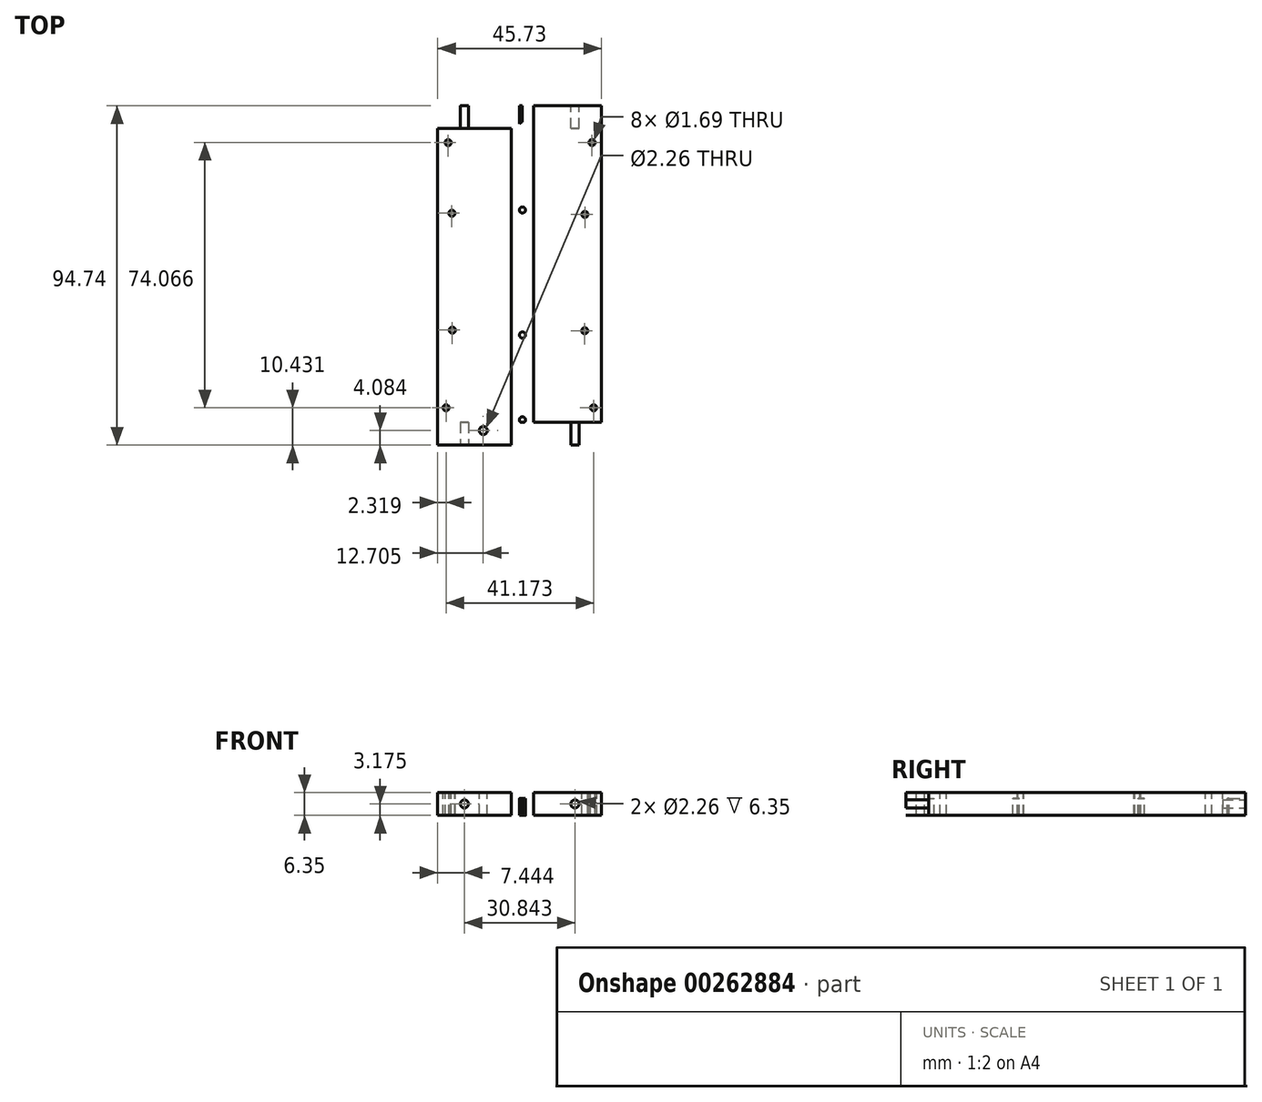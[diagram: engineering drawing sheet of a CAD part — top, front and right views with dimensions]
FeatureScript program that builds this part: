
annotation { "Feature Type Name" : "Feature", "Feature Type Description" : "" }
export const myFeature = defineFeature(function(context is Context, id is Id, definition is map)
    precondition{}
    {
        {
            var Q0;
            Q0=qCreatedBy(makeId("Top.planeOp"),FACE);
            var sketch = newSketch(context, id + "F0", { "sketchPlane" : qUnion([Q0])});
            skLineSegment(sketch, "E0.bottom", {"start": v(0, 0) * mm, "end": v(52.07, 0) * mm});
            skLineSegment(sketch, "E0.top", {"start": v(0, 101.6) * mm, "end": v(52.07, 101.6) * mm});
            skLineSegment(sketch, "E0.left", {"start": v(0, 0) * mm, "end": v(0, 101.6) * mm});
            skLineSegment(sketch, "E0.right", {"start": v(52.07, 0) * mm, "end": v(52.07, 101.6) * mm});
            skLineSegment(sketch, "E1.bottom", {"start": v(3.17, 3.43) * mm, "end": v(48.9, 3.43) * mm});
            skLineSegment(sketch, "E1.top", {"start": v(3.17, 98.17) * mm, "end": v(48.9, 98.17) * mm});
            skLineSegment(sketch, "E1.left", {"start": v(3.17, 3.43) * mm, "end": v(3.17, 98.17) * mm});
            skLineSegment(sketch, "E1.right", {"start": v(48.9, 3.43) * mm, "end": v(48.9, 98.17) * mm});
            skSolve(sketch);
        }
        {
            var Q0;
            {var subQ0=sQuery(id+"F0.wireOp",EDGE,"E1.left");Q0=makeQuery(id+"F0.imprint","IMPRINT",FACE,{"disambiguationData":[TD([[makeQuery(id+"F0.imprint","IMPRINT",EDGE,{"derivedFrom":subQ0}),-1.0]])]});}
            var Q1;
            {var subQ0=sQuery(id+"F0.wireOp",EDGE,"E1.right");Q1=makeQuery(id+"F0.imprint","IMPRINT",FACE,{"disambiguationData":[TD([[makeQuery(id+"F0.imprint","IMPRINT",EDGE,{"derivedFrom":subQ0}),1.0]])]});}
            var Q2;
            {var subQ0=sQuery(id+"F0.wireOp",EDGE,"10e28cab-1427-4d4f-a1a2-41381d8ae787");Q2=makeQuery(id+"F0.imprint","IMPRINT",FACE,{"disambiguationData":[TD([[makeQuery(id+"F0.imprint","IMPRINT",EDGE,{"derivedFrom":subQ0}),1.0]])]});}
            var Q3;
            {var subQ0=sQuery(id+"F0.wireOp",EDGE,"10e28cab-1427-4d4f-a1a2-41381d8ae787");Q3=makeQuery(id+"F0.imprint","IMPRINT",FACE,{"disambiguationData":[TD([[makeQuery(id+"F0.imprint","IMPRINT",EDGE,{"derivedFrom":subQ0}),-1.0]])]});}
            extrude(context, id + "F1", {"entities" : qUnion([Q0, Q1, Q2, Q3]), "oppositeDirection" : true, "depth" : 6.35 * mm});
        }
        {
            var Q0;
            Q0=qCreatedBy(makeId("Top.planeOp"),FACE);
            var Q1;
            Q1=qCreatedBy(makeId("Front.planeOp"),FACE);
            var Q2;
            Q2=qCreatedBy(makeId("Top.planeOp"),FACE);
            var Q3;
            Q3=qCreatedBy(makeId("Top.planeOp"),FACE);
            var sketch = newSketch(context, id + "F2", { "sketchPlane" : qUnion([Q0, Q1, Q2, Q3])});
            skLineSegment(sketch, "E2", {"start": v(3.17, 11.6) * mm, "end": v(3.17, 90.4) * mm});
            skLineSegment(sketch, "E3", {"start": v(3.17, 90.65) * mm, "end": v(48.9, 90.65) * mm});
            skLineSegment(sketch, "E4", {"start": v(48.9, 90.65) * mm, "end": v(48.9, 11.85) * mm});
            skLineSegment(sketch, "E5", {"start": v(48.9, 11.85) * mm, "end": v(3.17, 11.85) * mm});
            skLineSegment(sketch, "E6", {"start": v(25.2, 45.84) * mm, "end": v(25.2, 56.82) * mm});
            skLineSegment(sketch, "E7", {"start": v(25.2, 56.82) * mm, "end": v(28.45, 56.82) * mm});
            skLineSegment(sketch, "E8", {"start": v(28.45, 56.82) * mm, "end": v(28.45, 45.84) * mm});
            skLineSegment(sketch, "E9", {"start": v(28.45, 45.84) * mm, "end": v(25.2, 45.84) * mm});
            skLineSegment(sketch, "E10", {"start": v(14.78, 45.41) * mm, "end": v(14.78, 30.68) * mm});
            skArc(sketch, "E11", {"start": v(14.78, 30.68) * mm, "mid": v(14.1, 29.06) * mm, "end": v(12.48, 28.38) * mm});
            skLineSegment(sketch, "E12", {"start": v(12.48, 28.38) * mm, "end": v(3.17, 28.38) * mm});
            skLineSegment(sketch, "E13", {"start": v(3.17, 28.38) * mm, "end": v(3.17, 27.9) * mm});
            skLineSegment(sketch, "E14", {"start": v(3.17, 27.9) * mm, "end": v(12.48, 27.9) * mm});
            skArc(sketch, "E15", {"start": v(12.48, 27.9) * mm, "mid": v(14.45, 28.71) * mm, "end": v(15.26, 30.68) * mm});
            skLineSegment(sketch, "E16", {"start": v(15.26, 30.68) * mm, "end": v(15.26, 45.41) * mm});
            skArc(sketch, "E17", {"start": v(15.26, 45.41) * mm, "mid": v(15.93, 47.04) * mm, "end": v(17.56, 47.71) * mm});
            skLineSegment(sketch, "E18", {"start": v(17.56, 47.71) * mm, "end": v(25.2, 47.71) * mm});
            skLineSegment(sketch, "E19", {"start": v(25.2, 47.71) * mm, "end": v(25.2, 48.2) * mm});
            skLineSegment(sketch, "E20", {"start": v(25.2, 48.2) * mm, "end": v(17.56, 48.2) * mm});
            skArc(sketch, "E21", {"start": v(17.56, 48.2) * mm, "mid": v(15.6, 47.38) * mm, "end": v(14.78, 45.41) * mm});
            skLineSegment(sketch, "E22", {"start": v(25.2, 56.49) * mm, "end": v(25.2, 56.82) * mm});
            skLineSegment(sketch, "E23", {"start": v(28.45, 56.82) * mm, "end": v(28.45, 56.5) * mm});
            skLineSegment(sketch, "E24", {"start": v(28.45, 56.5) * mm, "end": v(36.08, 56.5) * mm});
            skLineSegment(sketch, "E25", {"start": v(36.08, 56.5) * mm, "end": v(36.27, 56.5) * mm});
            skLineSegment(sketch, "E26", {"start": v(36.27, 56.5) * mm, "end": v(36.44, 56.53) * mm});
            skLineSegment(sketch, "E27", {"start": v(36.44, 56.53) * mm, "end": v(36.62, 56.57) * mm});
            skLineSegment(sketch, "E28", {"start": v(36.62, 56.57) * mm, "end": v(36.79, 56.63) * mm});
            skLineSegment(sketch, "E29", {"start": v(36.79, 56.63) * mm, "end": v(36.95, 56.7) * mm});
            skLineSegment(sketch, "E30", {"start": v(36.95, 56.7) * mm, "end": v(37.11, 56.78) * mm});
            skLineSegment(sketch, "E31", {"start": v(37.11, 56.78) * mm, "end": v(37.26, 56.87) * mm});
            skLineSegment(sketch, "E32", {"start": v(37.26, 56.87) * mm, "end": v(37.4, 56.98) * mm});
            skLineSegment(sketch, "E33", {"start": v(37.4, 56.98) * mm, "end": v(37.53, 57.1) * mm});
            skLineSegment(sketch, "E34", {"start": v(37.53, 57.1) * mm, "end": v(37.65, 57.23) * mm});
            skLineSegment(sketch, "E35", {"start": v(37.65, 57.23) * mm, "end": v(37.76, 57.37) * mm});
            skLineSegment(sketch, "E36", {"start": v(37.76, 57.37) * mm, "end": v(37.86, 57.52) * mm});
            skLineSegment(sketch, "E37", {"start": v(37.86, 57.52) * mm, "end": v(37.94, 57.68) * mm});
            skLineSegment(sketch, "E38", {"start": v(37.94, 57.68) * mm, "end": v(38, 57.85) * mm});
            skLineSegment(sketch, "E39", {"start": v(38, 57.85) * mm, "end": v(38.06, 58.02) * mm});
            skLineSegment(sketch, "E40", {"start": v(38.06, 58.02) * mm, "end": v(38.1, 58.2) * mm});
            skLineSegment(sketch, "E41", {"start": v(38.1, 58.2) * mm, "end": v(38.12, 58.37) * mm});
            skLineSegment(sketch, "E42", {"start": v(38.12, 58.37) * mm, "end": v(38.13, 58.55) * mm});
            skLineSegment(sketch, "E43", {"start": v(38.13, 58.55) * mm, "end": v(38.13, 73.9) * mm});
            skLineSegment(sketch, "E44", {"start": v(38.13, 73.9) * mm, "end": v(38.14, 73.9) * mm});
            skLineSegment(sketch, "E45", {"start": v(38.14, 73.9) * mm, "end": v(38.14, 73.91) * mm});
            skLineSegment(sketch, "E46", {"start": v(38.14, 73.91) * mm, "end": v(38.18, 74.18) * mm});
            skLineSegment(sketch, "E47", {"start": v(38.18, 74.18) * mm, "end": v(38.24, 74.43) * mm});
            skLineSegment(sketch, "E48", {"start": v(38.24, 74.43) * mm, "end": v(38.32, 74.69) * mm});
            skLineSegment(sketch, "E49", {"start": v(38.32, 74.69) * mm, "end": v(38.42, 74.93) * mm});
            skLineSegment(sketch, "E50", {"start": v(38.42, 74.93) * mm, "end": v(38.54, 75.17) * mm});
            skLineSegment(sketch, "E51", {"start": v(38.54, 75.17) * mm, "end": v(38.68, 75.39) * mm});
            skLineSegment(sketch, "E52", {"start": v(38.68, 75.39) * mm, "end": v(38.84, 75.6) * mm});
            skLineSegment(sketch, "E53", {"start": v(38.84, 75.6) * mm, "end": v(39.02, 75.8) * mm});
            skLineSegment(sketch, "E54", {"start": v(39.02, 75.8) * mm, "end": v(39.22, 75.97) * mm});
            skLineSegment(sketch, "E55", {"start": v(39.22, 75.97) * mm, "end": v(39.43, 76.13) * mm});
            skLineSegment(sketch, "E56", {"start": v(39.43, 76.13) * mm, "end": v(39.65, 76.28) * mm});
            skLineSegment(sketch, "E57", {"start": v(39.65, 76.28) * mm, "end": v(39.88, 76.4) * mm});
            skLineSegment(sketch, "E58", {"start": v(39.88, 76.4) * mm, "end": v(40.13, 76.5) * mm});
            skLineSegment(sketch, "E59", {"start": v(40.13, 76.5) * mm, "end": v(40.38, 76.58) * mm});
            skLineSegment(sketch, "E60", {"start": v(40.38, 76.58) * mm, "end": v(40.64, 76.64) * mm});
            skLineSegment(sketch, "E61", {"start": v(40.64, 76.64) * mm, "end": v(40.9, 76.67) * mm});
            skLineSegment(sketch, "E62", {"start": v(40.9, 76.67) * mm, "end": v(40.91, 76.67) * mm});
            skLineSegment(sketch, "E63", {"start": v(40.91, 76.67) * mm, "end": v(40.91, 76.68) * mm});
            skLineSegment(sketch, "E64", {"start": v(40.91, 76.68) * mm, "end": v(48.9, 76.68) * mm});
            skLineSegment(sketch, "E65", {"start": v(48.9, 76.68) * mm, "end": v(48.9, 90.65) * mm});
            skLineSegment(sketch, "E66", {"start": v(48.9, 90.65) * mm, "end": v(3.17, 90.65) * mm});
            skLineSegment(sketch, "E67", {"start": v(3.17, 90.65) * mm, "end": v(3.17, 76.67) * mm});
            skLineSegment(sketch, "E68", {"start": v(3.17, 76.67) * mm, "end": v(12.73, 76.67) * mm});
            skLineSegment(sketch, "E69", {"start": v(12.73, 76.67) * mm, "end": v(12.73, 76.66) * mm});
            skLineSegment(sketch, "E70", {"start": v(12.73, 76.66) * mm, "end": v(12.74, 76.66) * mm});
            skLineSegment(sketch, "E71", {"start": v(12.74, 76.66) * mm, "end": v(13, 76.62) * mm});
            skLineSegment(sketch, "E72", {"start": v(13, 76.62) * mm, "end": v(13.26, 76.56) * mm});
            skLineSegment(sketch, "E73", {"start": v(13.26, 76.56) * mm, "end": v(13.5, 76.48) * mm});
            skLineSegment(sketch, "E74", {"start": v(13.5, 76.48) * mm, "end": v(13.75, 76.38) * mm});
            skLineSegment(sketch, "E75", {"start": v(13.75, 76.38) * mm, "end": v(13.99, 76.26) * mm});
            skLineSegment(sketch, "E76", {"start": v(13.99, 76.26) * mm, "end": v(14.21, 76.12) * mm});
            skLineSegment(sketch, "E77", {"start": v(14.21, 76.12) * mm, "end": v(14.42, 75.96) * mm});
            skLineSegment(sketch, "E78", {"start": v(14.42, 75.96) * mm, "end": v(14.62, 75.78) * mm});
            skLineSegment(sketch, "E79", {"start": v(14.62, 75.78) * mm, "end": v(14.8, 75.58) * mm});
            skLineSegment(sketch, "E80", {"start": v(14.8, 75.58) * mm, "end": v(14.96, 75.37) * mm});
            skLineSegment(sketch, "E81", {"start": v(14.96, 75.37) * mm, "end": v(15.1, 75.15) * mm});
            skLineSegment(sketch, "E82", {"start": v(15.1, 75.15) * mm, "end": v(15.22, 74.91) * mm});
            skLineSegment(sketch, "E83", {"start": v(15.22, 74.91) * mm, "end": v(15.32, 74.67) * mm});
            skLineSegment(sketch, "E84", {"start": v(15.32, 74.67) * mm, "end": v(15.4, 74.42) * mm});
            skLineSegment(sketch, "E85", {"start": v(15.4, 74.42) * mm, "end": v(15.46, 74.16) * mm});
            skLineSegment(sketch, "E86", {"start": v(15.46, 74.16) * mm, "end": v(15.5, 73.9) * mm});
            skLineSegment(sketch, "E87", {"start": v(15.5, 73.9) * mm, "end": v(15.5, 73.89) * mm});
            skLineSegment(sketch, "E88", {"start": v(15.5, 73.89) * mm, "end": v(15.5, 73.89) * mm});
            skLineSegment(sketch, "E89", {"start": v(15.5, 73.89) * mm, "end": v(15.5, 58.54) * mm});
            skLineSegment(sketch, "E90", {"start": v(15.5, 58.54) * mm, "end": v(15.51, 58.35) * mm});
            skLineSegment(sketch, "E91", {"start": v(15.51, 58.35) * mm, "end": v(15.54, 58.18) * mm});
            skLineSegment(sketch, "E92", {"start": v(15.54, 58.18) * mm, "end": v(15.58, 58) * mm});
            skLineSegment(sketch, "E93", {"start": v(15.58, 58) * mm, "end": v(15.63, 57.83) * mm});
            skLineSegment(sketch, "E94", {"start": v(15.63, 57.83) * mm, "end": v(15.7, 57.67) * mm});
            skLineSegment(sketch, "E95", {"start": v(15.7, 57.67) * mm, "end": v(15.78, 57.5) * mm});
            skLineSegment(sketch, "E96", {"start": v(15.78, 57.5) * mm, "end": v(15.88, 57.36) * mm});
            skLineSegment(sketch, "E97", {"start": v(15.88, 57.36) * mm, "end": v(15.99, 57.22) * mm});
            skLineSegment(sketch, "E98", {"start": v(15.99, 57.22) * mm, "end": v(16.1, 57.08) * mm});
            skLineSegment(sketch, "E99", {"start": v(16.1, 57.08) * mm, "end": v(16.24, 56.96) * mm});
            skLineSegment(sketch, "E100", {"start": v(16.24, 56.96) * mm, "end": v(16.38, 56.86) * mm});
            skLineSegment(sketch, "E101", {"start": v(16.38, 56.86) * mm, "end": v(16.53, 56.76) * mm});
            skLineSegment(sketch, "E102", {"start": v(16.53, 56.76) * mm, "end": v(16.69, 56.68) * mm});
            skLineSegment(sketch, "E103", {"start": v(16.69, 56.68) * mm, "end": v(16.85, 56.6) * mm});
            skLineSegment(sketch, "E104", {"start": v(16.85, 56.6) * mm, "end": v(17.02, 56.56) * mm});
            skLineSegment(sketch, "E105", {"start": v(17.02, 56.56) * mm, "end": v(17.2, 56.52) * mm});
            skLineSegment(sketch, "E106", {"start": v(17.2, 56.52) * mm, "end": v(17.37, 56.5) * mm});
            skLineSegment(sketch, "E107", {"start": v(17.37, 56.5) * mm, "end": v(17.56, 56.49) * mm});
            skLineSegment(sketch, "E108", {"start": v(17.56, 56.49) * mm, "end": v(25.2, 56.49) * mm});
            skLineSegment(sketch, "E109", {"start": v(38.39, 73.65) * mm, "end": v(38.39, 58.55) * mm});
            skArc(sketch, "E110", {"start": v(38.39, 58.55) * mm, "mid": v(37.71, 56.92) * mm, "end": v(36.09, 56.25) * mm});
            skLineSegment(sketch, "E111", {"start": v(36.09, 56.25) * mm, "end": v(28.45, 56.25) * mm});
            skLineSegment(sketch, "E112", {"start": v(28.45, 56.25) * mm, "end": v(28.45, 55.77) * mm});
            skLineSegment(sketch, "E113", {"start": v(28.45, 55.77) * mm, "end": v(36.09, 55.77) * mm});
            skArc(sketch, "E114", {"start": v(36.09, 55.77) * mm, "mid": v(38.05, 56.58) * mm, "end": v(38.87, 58.55) * mm});
            skLineSegment(sketch, "E115", {"start": v(38.87, 58.55) * mm, "end": v(38.87, 73.65) * mm});
            skArc(sketch, "E116", {"start": v(38.87, 73.65) * mm, "mid": v(39.54, 75.27) * mm, "end": v(41.17, 75.95) * mm});
            skLineSegment(sketch, "E117", {"start": v(41.17, 75.95) * mm, "end": v(47.9, 75.95) * mm});
            skLineSegment(sketch, "E118", {"start": v(47.9, 75.95) * mm, "end": v(47.9, 76.43) * mm});
            skLineSegment(sketch, "E119", {"start": v(47.9, 76.43) * mm, "end": v(41.17, 76.43) * mm});
            skArc(sketch, "E120", {"start": v(41.17, 76.43) * mm, "mid": v(39.2, 75.61) * mm, "end": v(38.39, 73.65) * mm});
            skLineSegment(sketch, "E121", {"start": v(28.45, 50.12) * mm, "end": v(28.45, 48.46) * mm});
            skLineSegment(sketch, "E122", {"start": v(28.45, 48.46) * mm, "end": v(36.33, 48.46) * mm});
            skLineSegment(sketch, "E123", {"start": v(36.33, 48.46) * mm, "end": v(36.33, 48.45) * mm});
            skLineSegment(sketch, "E124", {"start": v(36.33, 48.45) * mm, "end": v(36.34, 48.45) * mm});
            skLineSegment(sketch, "E125", {"start": v(36.34, 48.45) * mm, "end": v(36.6, 48.42) * mm});
            skLineSegment(sketch, "E126", {"start": v(36.6, 48.42) * mm, "end": v(36.87, 48.36) * mm});
            skLineSegment(sketch, "E127", {"start": v(36.87, 48.36) * mm, "end": v(37.12, 48.28) * mm});
            skLineSegment(sketch, "E128", {"start": v(37.12, 48.28) * mm, "end": v(37.36, 48.18) * mm});
            skLineSegment(sketch, "E129", {"start": v(37.36, 48.18) * mm, "end": v(37.6, 48.06) * mm});
            skLineSegment(sketch, "E130", {"start": v(37.6, 48.06) * mm, "end": v(37.82, 47.92) * mm});
            skLineSegment(sketch, "E131", {"start": v(37.82, 47.92) * mm, "end": v(38.03, 47.75) * mm});
            skLineSegment(sketch, "E132", {"start": v(38.03, 47.75) * mm, "end": v(38.23, 47.58) * mm});
            skLineSegment(sketch, "E133", {"start": v(38.23, 47.58) * mm, "end": v(38.4, 47.38) * mm});
            skLineSegment(sketch, "E134", {"start": v(38.4, 47.38) * mm, "end": v(38.57, 47.17) * mm});
            skLineSegment(sketch, "E135", {"start": v(38.57, 47.17) * mm, "end": v(38.7, 46.95) * mm});
            skLineSegment(sketch, "E136", {"start": v(38.7, 46.95) * mm, "end": v(38.83, 46.71) * mm});
            skLineSegment(sketch, "E137", {"start": v(38.83, 46.71) * mm, "end": v(38.93, 46.47) * mm});
            skLineSegment(sketch, "E138", {"start": v(38.93, 46.47) * mm, "end": v(39.01, 46.21) * mm});
            skLineSegment(sketch, "E139", {"start": v(39.01, 46.21) * mm, "end": v(39.07, 45.96) * mm});
            skLineSegment(sketch, "E140", {"start": v(39.07, 45.96) * mm, "end": v(39.1, 45.7) * mm});
            skLineSegment(sketch, "E141", {"start": v(39.1, 45.7) * mm, "end": v(39.1, 45.68) * mm});
            skLineSegment(sketch, "E142", {"start": v(39.1, 45.68) * mm, "end": v(39.12, 45.68) * mm});
            skLineSegment(sketch, "E143", {"start": v(39.12, 45.68) * mm, "end": v(39.12, 30.7) * mm});
            skLineSegment(sketch, "E144", {"start": v(39.12, 30.7) * mm, "end": v(39.12, 30.52) * mm});
            skLineSegment(sketch, "E145", {"start": v(39.12, 30.52) * mm, "end": v(39.15, 30.34) * mm});
            skLineSegment(sketch, "E146", {"start": v(39.15, 30.34) * mm, "end": v(39.19, 30.17) * mm});
            skLineSegment(sketch, "E147", {"start": v(39.19, 30.17) * mm, "end": v(39.24, 30) * mm});
            skLineSegment(sketch, "E148", {"start": v(39.24, 30) * mm, "end": v(39.3, 29.83) * mm});
            skLineSegment(sketch, "E149", {"start": v(39.3, 29.83) * mm, "end": v(39.39, 29.67) * mm});
            skLineSegment(sketch, "E150", {"start": v(39.39, 29.67) * mm, "end": v(39.49, 29.52) * mm});
            skLineSegment(sketch, "E151", {"start": v(39.49, 29.52) * mm, "end": v(39.6, 29.38) * mm});
            skLineSegment(sketch, "E152", {"start": v(39.6, 29.38) * mm, "end": v(39.71, 29.25) * mm});
            skLineSegment(sketch, "E153", {"start": v(39.71, 29.25) * mm, "end": v(39.85, 29.13) * mm});
            skLineSegment(sketch, "E154", {"start": v(39.85, 29.13) * mm, "end": v(39.99, 29.02) * mm});
            skLineSegment(sketch, "E155", {"start": v(39.99, 29.02) * mm, "end": v(40.14, 28.93) * mm});
            skLineSegment(sketch, "E156", {"start": v(40.14, 28.93) * mm, "end": v(40.3, 28.84) * mm});
            skLineSegment(sketch, "E157", {"start": v(40.3, 28.84) * mm, "end": v(40.46, 28.78) * mm});
            skLineSegment(sketch, "E158", {"start": v(40.46, 28.78) * mm, "end": v(40.63, 28.72) * mm});
            skLineSegment(sketch, "E159", {"start": v(40.63, 28.72) * mm, "end": v(40.8, 28.68) * mm});
            skLineSegment(sketch, "E160", {"start": v(40.8, 28.68) * mm, "end": v(40.98, 28.66) * mm});
            skLineSegment(sketch, "E161", {"start": v(40.98, 28.66) * mm, "end": v(41.17, 28.65) * mm});
            skLineSegment(sketch, "E162", {"start": v(41.17, 28.65) * mm, "end": v(48.9, 28.65) * mm});
            skLineSegment(sketch, "E163", {"start": v(48.9, 28.65) * mm, "end": v(48.9, 43.61) * mm});
            skLineSegment(sketch, "E164", {"start": v(48.9, 43.61) * mm, "end": v(46.28, 43.61) * mm});
            skLineSegment(sketch, "E165", {"start": v(46.28, 43.61) * mm, "end": v(46.28, 43.62) * mm});
            skLineSegment(sketch, "E166", {"start": v(46.28, 43.62) * mm, "end": v(46.27, 43.62) * mm});
            skLineSegment(sketch, "E167", {"start": v(46.27, 43.62) * mm, "end": v(46, 43.66) * mm});
            skLineSegment(sketch, "E168", {"start": v(46, 43.66) * mm, "end": v(45.74, 43.72) * mm});
            skLineSegment(sketch, "E169", {"start": v(45.74, 43.72) * mm, "end": v(45.5, 43.8) * mm});
            skLineSegment(sketch, "E170", {"start": v(45.5, 43.8) * mm, "end": v(45.25, 43.9) * mm});
            skLineSegment(sketch, "E171", {"start": v(45.25, 43.9) * mm, "end": v(45.01, 44.02) * mm});
            skLineSegment(sketch, "E172", {"start": v(45.01, 44.02) * mm, "end": v(44.79, 44.16) * mm});
            skLineSegment(sketch, "E173", {"start": v(44.79, 44.16) * mm, "end": v(44.58, 44.32) * mm});
            skLineSegment(sketch, "E174", {"start": v(44.58, 44.32) * mm, "end": v(44.38, 44.5) * mm});
            skLineSegment(sketch, "E175", {"start": v(44.38, 44.5) * mm, "end": v(44.2, 44.7) * mm});
            skLineSegment(sketch, "E176", {"start": v(44.2, 44.7) * mm, "end": v(44.04, 44.9) * mm});
            skLineSegment(sketch, "E177", {"start": v(44.04, 44.9) * mm, "end": v(43.9, 45.13) * mm});
            skLineSegment(sketch, "E178", {"start": v(43.9, 45.13) * mm, "end": v(43.78, 45.36) * mm});
            skLineSegment(sketch, "E179", {"start": v(43.78, 45.36) * mm, "end": v(43.68, 45.6) * mm});
            skLineSegment(sketch, "E180", {"start": v(43.68, 45.6) * mm, "end": v(43.6, 45.86) * mm});
            skLineSegment(sketch, "E181", {"start": v(43.6, 45.86) * mm, "end": v(43.54, 46.12) * mm});
            skLineSegment(sketch, "E182", {"start": v(43.54, 46.12) * mm, "end": v(43.5, 46.38) * mm});
            skLineSegment(sketch, "E183", {"start": v(43.5, 46.38) * mm, "end": v(43.5, 46.4) * mm});
            skLineSegment(sketch, "E184", {"start": v(43.5, 46.4) * mm, "end": v(43.5, 46.4) * mm});
            skLineSegment(sketch, "E185", {"start": v(43.5, 46.4) * mm, "end": v(43.5, 48.07) * mm});
            skLineSegment(sketch, "E186", {"start": v(43.5, 48.07) * mm, "end": v(43.49, 48.26) * mm});
            skLineSegment(sketch, "E187", {"start": v(43.49, 48.26) * mm, "end": v(43.46, 48.43) * mm});
            skLineSegment(sketch, "E188", {"start": v(43.46, 48.43) * mm, "end": v(43.42, 48.6) * mm});
            skLineSegment(sketch, "E189", {"start": v(43.42, 48.6) * mm, "end": v(43.37, 48.78) * mm});
            skLineSegment(sketch, "E190", {"start": v(43.37, 48.78) * mm, "end": v(43.3, 48.94) * mm});
            skLineSegment(sketch, "E191", {"start": v(43.3, 48.94) * mm, "end": v(43.22, 49.1) * mm});
            skLineSegment(sketch, "E192", {"start": v(43.22, 49.1) * mm, "end": v(43.12, 49.25) * mm});
            skLineSegment(sketch, "E193", {"start": v(43.12, 49.25) * mm, "end": v(43.02, 49.4) * mm});
            skLineSegment(sketch, "E194", {"start": v(43.02, 49.4) * mm, "end": v(42.9, 49.53) * mm});
            skLineSegment(sketch, "E195", {"start": v(42.9, 49.53) * mm, "end": v(42.76, 49.65) * mm});
            skLineSegment(sketch, "E196", {"start": v(42.76, 49.65) * mm, "end": v(42.62, 49.75) * mm});
            skLineSegment(sketch, "E197", {"start": v(42.62, 49.75) * mm, "end": v(42.47, 49.85) * mm});
            skLineSegment(sketch, "E198", {"start": v(42.47, 49.85) * mm, "end": v(42.31, 49.93) * mm});
            skLineSegment(sketch, "E199", {"start": v(42.31, 49.93) * mm, "end": v(42.15, 50) * mm});
            skLineSegment(sketch, "E200", {"start": v(42.15, 50) * mm, "end": v(41.98, 50.05) * mm});
            skLineSegment(sketch, "E201", {"start": v(41.98, 50.05) * mm, "end": v(41.8, 50.1) * mm});
            skLineSegment(sketch, "E202", {"start": v(41.8, 50.1) * mm, "end": v(41.63, 50.12) * mm});
            skLineSegment(sketch, "E203", {"start": v(41.63, 50.12) * mm, "end": v(41.44, 50.12) * mm});
            skLineSegment(sketch, "E204", {"start": v(41.44, 50.12) * mm, "end": v(28.45, 50.12) * mm});
            skLineSegment(sketch, "E205", {"start": v(3.17, 59.88) * mm, "end": v(7.05, 59.88) * mm});
            skArc(sketch, "E206", {"start": v(7.05, 59.88) * mm, "mid": v(8.68, 59.2) * mm, "end": v(9.35, 57.58) * mm});
            skLineSegment(sketch, "E207", {"start": v(9.35, 57.58) * mm, "end": v(9.35, 55.84) * mm});
            skArc(sketch, "E208", {"start": v(9.35, 55.84) * mm, "mid": v(10.16, 53.88) * mm, "end": v(12.13, 53.06) * mm});
            skLineSegment(sketch, "E209", {"start": v(12.13, 53.06) * mm, "end": v(25.2, 53.06) * mm});
            skLineSegment(sketch, "E210", {"start": v(25.2, 53.06) * mm, "end": v(25.2, 53.54) * mm});
            skLineSegment(sketch, "E211", {"start": v(25.2, 53.54) * mm, "end": v(12.13, 53.54) * mm});
            skArc(sketch, "E212", {"start": v(12.13, 53.54) * mm, "mid": v(10.5, 54.22) * mm, "end": v(9.83, 55.84) * mm});
            skLineSegment(sketch, "E213", {"start": v(9.83, 55.84) * mm, "end": v(9.83, 57.58) * mm});
            skArc(sketch, "E214", {"start": v(9.83, 57.58) * mm, "mid": v(9.02, 59.55) * mm, "end": v(7.05, 60.36) * mm});
            skLineSegment(sketch, "E215", {"start": v(7.05, 60.36) * mm, "end": v(3.17, 60.36) * mm});
            skLineSegment(sketch, "E216", {"start": v(3.17, 60.36) * mm, "end": v(3.17, 59.88) * mm});
            skLineSegment(sketch, "E217", {"start": v(25.2, 53.8) * mm, "end": v(25.2, 55.5) * mm});
            skLineSegment(sketch, "E218", {"start": v(25.2, 55.5) * mm, "end": v(17.3, 55.5) * mm});
            skLineSegment(sketch, "E219", {"start": v(17.3, 55.5) * mm, "end": v(17.3, 55.5) * mm});
            skLineSegment(sketch, "E220", {"start": v(17.3, 55.5) * mm, "end": v(17.29, 55.5) * mm});
            skLineSegment(sketch, "E221", {"start": v(17.29, 55.5) * mm, "end": v(17.02, 55.54) * mm});
            skLineSegment(sketch, "E222", {"start": v(17.02, 55.54) * mm, "end": v(16.77, 55.6) * mm});
            skLineSegment(sketch, "E223", {"start": v(16.77, 55.6) * mm, "end": v(16.51, 55.68) * mm});
            skLineSegment(sketch, "E224", {"start": v(16.51, 55.68) * mm, "end": v(16.27, 55.78) * mm});
            skLineSegment(sketch, "E225", {"start": v(16.27, 55.78) * mm, "end": v(16.03, 55.9) * mm});
            skLineSegment(sketch, "E226", {"start": v(16.03, 55.9) * mm, "end": v(15.81, 56.04) * mm});
            skLineSegment(sketch, "E227", {"start": v(15.81, 56.04) * mm, "end": v(15.6, 56.2) * mm});
            skLineSegment(sketch, "E228", {"start": v(15.6, 56.2) * mm, "end": v(15.4, 56.38) * mm});
            skLineSegment(sketch, "E229", {"start": v(15.4, 56.38) * mm, "end": v(15.23, 56.58) * mm});
            skLineSegment(sketch, "E230", {"start": v(15.23, 56.58) * mm, "end": v(15.06, 56.79) * mm});
            skLineSegment(sketch, "E231", {"start": v(15.06, 56.79) * mm, "end": v(14.92, 57.01) * mm});
            skLineSegment(sketch, "E232", {"start": v(14.92, 57.01) * mm, "end": v(14.8, 57.25) * mm});
            skLineSegment(sketch, "E233", {"start": v(14.8, 57.25) * mm, "end": v(14.7, 57.5) * mm});
            skLineSegment(sketch, "E234", {"start": v(14.7, 57.5) * mm, "end": v(14.62, 57.74) * mm});
            skLineSegment(sketch, "E235", {"start": v(14.62, 57.74) * mm, "end": v(14.56, 58) * mm});
            skLineSegment(sketch, "E236", {"start": v(14.56, 58) * mm, "end": v(14.53, 58.27) * mm});
            skLineSegment(sketch, "E237", {"start": v(14.53, 58.27) * mm, "end": v(14.53, 58.28) * mm});
            skLineSegment(sketch, "E238", {"start": v(14.53, 58.28) * mm, "end": v(14.52, 58.28) * mm});
            skLineSegment(sketch, "E239", {"start": v(14.52, 58.28) * mm, "end": v(14.52, 73.63) * mm});
            skLineSegment(sketch, "E240", {"start": v(14.52, 73.63) * mm, "end": v(14.5, 73.81) * mm});
            skLineSegment(sketch, "E241", {"start": v(14.5, 73.81) * mm, "end": v(14.48, 73.99) * mm});
            skLineSegment(sketch, "E242", {"start": v(14.48, 73.99) * mm, "end": v(14.45, 74.16) * mm});
            skLineSegment(sketch, "E243", {"start": v(14.45, 74.16) * mm, "end": v(14.4, 74.33) * mm});
            skLineSegment(sketch, "E244", {"start": v(14.4, 74.33) * mm, "end": v(14.32, 74.5) * mm});
            skLineSegment(sketch, "E245", {"start": v(14.32, 74.5) * mm, "end": v(14.24, 74.65) * mm});
            skLineSegment(sketch, "E246", {"start": v(14.24, 74.65) * mm, "end": v(14.15, 74.8) * mm});
            skLineSegment(sketch, "E247", {"start": v(14.15, 74.8) * mm, "end": v(14.04, 74.95) * mm});
            skLineSegment(sketch, "E248", {"start": v(14.04, 74.95) * mm, "end": v(13.92, 75.08) * mm});
            skLineSegment(sketch, "E249", {"start": v(13.92, 75.08) * mm, "end": v(13.79, 75.2) * mm});
            skLineSegment(sketch, "E250", {"start": v(13.79, 75.2) * mm, "end": v(13.64, 75.3) * mm});
            skLineSegment(sketch, "E251", {"start": v(13.64, 75.3) * mm, "end": v(13.5, 75.4) * mm});
            skLineSegment(sketch, "E252", {"start": v(13.5, 75.4) * mm, "end": v(13.34, 75.48) * mm});
            skLineSegment(sketch, "E253", {"start": v(13.34, 75.48) * mm, "end": v(13.17, 75.55) * mm});
            skLineSegment(sketch, "E254", {"start": v(13.17, 75.55) * mm, "end": v(13, 75.6) * mm});
            skLineSegment(sketch, "E255", {"start": v(13, 75.6) * mm, "end": v(12.83, 75.65) * mm});
            skLineSegment(sketch, "E256", {"start": v(12.83, 75.65) * mm, "end": v(12.65, 75.67) * mm});
            skLineSegment(sketch, "E257", {"start": v(12.65, 75.67) * mm, "end": v(12.47, 75.68) * mm});
            skLineSegment(sketch, "E258", {"start": v(12.47, 75.68) * mm, "end": v(3.17, 75.68) * mm});
            skLineSegment(sketch, "E259", {"start": v(3.17, 75.68) * mm, "end": v(3.17, 60.61) * mm});
            skLineSegment(sketch, "E260", {"start": v(3.17, 60.61) * mm, "end": v(7.3, 60.61) * mm});
            skLineSegment(sketch, "E261", {"start": v(7.3, 60.61) * mm, "end": v(7.3, 60.6) * mm});
            skLineSegment(sketch, "E262", {"start": v(7.3, 60.6) * mm, "end": v(7.31, 60.6) * mm});
            skLineSegment(sketch, "E263", {"start": v(7.31, 60.6) * mm, "end": v(7.58, 60.57) * mm});
            skLineSegment(sketch, "E264", {"start": v(7.58, 60.57) * mm, "end": v(7.84, 60.51) * mm});
            skLineSegment(sketch, "E265", {"start": v(7.84, 60.51) * mm, "end": v(8.09, 60.43) * mm});
            skLineSegment(sketch, "E266", {"start": v(8.09, 60.43) * mm, "end": v(8.33, 60.33) * mm});
            skLineSegment(sketch, "E267", {"start": v(8.33, 60.33) * mm, "end": v(8.57, 60.2) * mm});
            skLineSegment(sketch, "E268", {"start": v(8.57, 60.2) * mm, "end": v(8.8, 60.07) * mm});
            skLineSegment(sketch, "E269", {"start": v(8.8, 60.07) * mm, "end": v(9, 59.9) * mm});
            skLineSegment(sketch, "E270", {"start": v(9, 59.9) * mm, "end": v(9.2, 59.73) * mm});
            skLineSegment(sketch, "E271", {"start": v(9.2, 59.73) * mm, "end": v(9.38, 59.53) * mm});
            skLineSegment(sketch, "E272", {"start": v(9.38, 59.53) * mm, "end": v(9.54, 59.32) * mm});
            skLineSegment(sketch, "E273", {"start": v(9.54, 59.32) * mm, "end": v(9.68, 59.1) * mm});
            skLineSegment(sketch, "E274", {"start": v(9.68, 59.1) * mm, "end": v(9.8, 58.86) * mm});
            skLineSegment(sketch, "E275", {"start": v(9.8, 58.86) * mm, "end": v(9.9, 58.62) * mm});
            skLineSegment(sketch, "E276", {"start": v(9.9, 58.62) * mm, "end": v(9.98, 58.36) * mm});
            skLineSegment(sketch, "E277", {"start": v(9.98, 58.36) * mm, "end": v(10.04, 58.1) * mm});
            skLineSegment(sketch, "E278", {"start": v(10.04, 58.1) * mm, "end": v(10.07, 57.84) * mm});
            skLineSegment(sketch, "E279", {"start": v(10.07, 57.84) * mm, "end": v(10.07, 57.83) * mm});
            skLineSegment(sketch, "E280", {"start": v(10.07, 57.83) * mm, "end": v(10.09, 57.83) * mm});
            skLineSegment(sketch, "E281", {"start": v(10.09, 57.83) * mm, "end": v(10.09, 55.85) * mm});
            skLineSegment(sketch, "E282", {"start": v(10.09, 55.85) * mm, "end": v(10.1, 55.66) * mm});
            skLineSegment(sketch, "E283", {"start": v(10.1, 55.66) * mm, "end": v(10.12, 55.49) * mm});
            skLineSegment(sketch, "E284", {"start": v(10.12, 55.49) * mm, "end": v(10.16, 55.31) * mm});
            skLineSegment(sketch, "E285", {"start": v(10.16, 55.31) * mm, "end": v(10.2, 55.14) * mm});
            skLineSegment(sketch, "E286", {"start": v(10.2, 55.14) * mm, "end": v(10.28, 54.98) * mm});
            skLineSegment(sketch, "E287", {"start": v(10.28, 54.98) * mm, "end": v(10.36, 54.82) * mm});
            skLineSegment(sketch, "E288", {"start": v(10.36, 54.82) * mm, "end": v(10.46, 54.67) * mm});
            skLineSegment(sketch, "E289", {"start": v(10.46, 54.67) * mm, "end": v(10.56, 54.53) * mm});
            skLineSegment(sketch, "E290", {"start": v(10.56, 54.53) * mm, "end": v(10.68, 54.4) * mm});
            skLineSegment(sketch, "E291", {"start": v(10.68, 54.4) * mm, "end": v(10.82, 54.28) * mm});
            skLineSegment(sketch, "E292", {"start": v(10.82, 54.28) * mm, "end": v(10.96, 54.17) * mm});
            skLineSegment(sketch, "E293", {"start": v(10.96, 54.17) * mm, "end": v(11.1, 54.07) * mm});
            skLineSegment(sketch, "E294", {"start": v(11.1, 54.07) * mm, "end": v(11.27, 53.99) * mm});
            skLineSegment(sketch, "E295", {"start": v(11.27, 53.99) * mm, "end": v(11.43, 53.92) * mm});
            skLineSegment(sketch, "E296", {"start": v(11.43, 53.92) * mm, "end": v(11.6, 53.87) * mm});
            skLineSegment(sketch, "E297", {"start": v(11.6, 53.87) * mm, "end": v(11.78, 53.83) * mm});
            skLineSegment(sketch, "E298", {"start": v(11.78, 53.83) * mm, "end": v(11.95, 53.8) * mm});
            skLineSegment(sketch, "E299", {"start": v(11.95, 53.8) * mm, "end": v(12.14, 53.8) * mm});
            skLineSegment(sketch, "E300", {"start": v(12.14, 53.8) * mm, "end": v(25.2, 53.8) * mm});
            skLineSegment(sketch, "E301", {"start": v(9.1, 55.59) * mm, "end": v(9.1, 57.57) * mm});
            skLineSegment(sketch, "E302", {"start": v(9.1, 57.57) * mm, "end": v(9.09, 57.76) * mm});
            skLineSegment(sketch, "E303", {"start": v(9.09, 57.76) * mm, "end": v(9.06, 57.93) * mm});
            skLineSegment(sketch, "E304", {"start": v(9.06, 57.93) * mm, "end": v(9.03, 58.1) * mm});
            skLineSegment(sketch, "E305", {"start": v(9.03, 58.1) * mm, "end": v(8.97, 58.28) * mm});
            skLineSegment(sketch, "E306", {"start": v(8.97, 58.28) * mm, "end": v(8.9, 58.44) * mm});
            skLineSegment(sketch, "E307", {"start": v(8.9, 58.44) * mm, "end": v(8.82, 58.6) * mm});
            skLineSegment(sketch, "E308", {"start": v(8.82, 58.6) * mm, "end": v(8.73, 58.75) * mm});
            skLineSegment(sketch, "E309", {"start": v(8.73, 58.75) * mm, "end": v(8.62, 58.9) * mm});
            skLineSegment(sketch, "E310", {"start": v(8.62, 58.9) * mm, "end": v(8.5, 59.02) * mm});
            skLineSegment(sketch, "E311", {"start": v(8.5, 59.02) * mm, "end": v(8.36, 59.15) * mm});
            skLineSegment(sketch, "E312", {"start": v(8.36, 59.15) * mm, "end": v(8.22, 59.25) * mm});
            skLineSegment(sketch, "E313", {"start": v(8.22, 59.25) * mm, "end": v(8.07, 59.35) * mm});
            skLineSegment(sketch, "E314", {"start": v(8.07, 59.35) * mm, "end": v(7.91, 59.43) * mm});
            skLineSegment(sketch, "E315", {"start": v(7.91, 59.43) * mm, "end": v(7.75, 59.5) * mm});
            skLineSegment(sketch, "E316", {"start": v(7.75, 59.5) * mm, "end": v(7.58, 59.55) * mm});
            skLineSegment(sketch, "E317", {"start": v(7.58, 59.55) * mm, "end": v(7.4, 59.6) * mm});
            skLineSegment(sketch, "E318", {"start": v(7.4, 59.6) * mm, "end": v(7.23, 59.62) * mm});
            skLineSegment(sketch, "E319", {"start": v(7.23, 59.62) * mm, "end": v(7.04, 59.62) * mm});
            skLineSegment(sketch, "E320", {"start": v(7.04, 59.62) * mm, "end": v(3.17, 59.62) * mm});
            skLineSegment(sketch, "E321", {"start": v(3.17, 59.62) * mm, "end": v(3.17, 44.59) * mm});
            skLineSegment(sketch, "E322", {"start": v(3.17, 44.59) * mm, "end": v(7.1, 44.59) * mm});
            skLineSegment(sketch, "E323", {"start": v(7.1, 44.59) * mm, "end": v(7.29, 44.6) * mm});
            skLineSegment(sketch, "E324", {"start": v(7.29, 44.6) * mm, "end": v(7.46, 44.62) * mm});
            skLineSegment(sketch, "E325", {"start": v(7.46, 44.62) * mm, "end": v(7.64, 44.66) * mm});
            skLineSegment(sketch, "E326", {"start": v(7.64, 44.66) * mm, "end": v(7.8, 44.71) * mm});
            skLineSegment(sketch, "E327", {"start": v(7.8, 44.71) * mm, "end": v(7.97, 44.78) * mm});
            skLineSegment(sketch, "E328", {"start": v(7.97, 44.78) * mm, "end": v(8.13, 44.86) * mm});
            skLineSegment(sketch, "E329", {"start": v(8.13, 44.86) * mm, "end": v(8.28, 44.96) * mm});
            skLineSegment(sketch, "E330", {"start": v(8.28, 44.96) * mm, "end": v(8.42, 45.07) * mm});
            skLineSegment(sketch, "E331", {"start": v(8.42, 45.07) * mm, "end": v(8.55, 45.19) * mm});
            skLineSegment(sketch, "E332", {"start": v(8.55, 45.19) * mm, "end": v(8.68, 45.32) * mm});
            skLineSegment(sketch, "E333", {"start": v(8.68, 45.32) * mm, "end": v(8.78, 45.46) * mm});
            skLineSegment(sketch, "E334", {"start": v(8.78, 45.46) * mm, "end": v(8.88, 45.6) * mm});
            skLineSegment(sketch, "E335", {"start": v(8.88, 45.6) * mm, "end": v(8.96, 45.77) * mm});
            skLineSegment(sketch, "E336", {"start": v(8.96, 45.77) * mm, "end": v(9.03, 45.93) * mm});
            skLineSegment(sketch, "E337", {"start": v(9.03, 45.93) * mm, "end": v(9.08, 46.1) * mm});
            skLineSegment(sketch, "E338", {"start": v(9.08, 46.1) * mm, "end": v(9.12, 46.28) * mm});
            skLineSegment(sketch, "E339", {"start": v(9.12, 46.28) * mm, "end": v(9.15, 46.45) * mm});
            skLineSegment(sketch, "E340", {"start": v(9.15, 46.45) * mm, "end": v(9.15, 46.64) * mm});
            skLineSegment(sketch, "E341", {"start": v(9.15, 46.64) * mm, "end": v(9.15, 48.32) * mm});
            skLineSegment(sketch, "E342", {"start": v(9.15, 48.32) * mm, "end": v(9.16, 48.32) * mm});
            skLineSegment(sketch, "E343", {"start": v(9.16, 48.32) * mm, "end": v(9.17, 48.33) * mm});
            skLineSegment(sketch, "E344", {"start": v(9.17, 48.33) * mm, "end": v(9.2, 48.6) * mm});
            skLineSegment(sketch, "E345", {"start": v(9.2, 48.6) * mm, "end": v(9.26, 48.85) * mm});
            skLineSegment(sketch, "E346", {"start": v(9.26, 48.85) * mm, "end": v(9.34, 49.1) * mm});
            skLineSegment(sketch, "E347", {"start": v(9.34, 49.1) * mm, "end": v(9.44, 49.35) * mm});
            skLineSegment(sketch, "E348", {"start": v(9.44, 49.35) * mm, "end": v(9.56, 49.58) * mm});
            skLineSegment(sketch, "E349", {"start": v(9.56, 49.58) * mm, "end": v(9.7, 49.8) * mm});
            skLineSegment(sketch, "E350", {"start": v(9.7, 49.8) * mm, "end": v(9.86, 50.01) * mm});
            skLineSegment(sketch, "E351", {"start": v(9.86, 50.01) * mm, "end": v(10.04, 50.21) * mm});
            skLineSegment(sketch, "E352", {"start": v(10.04, 50.21) * mm, "end": v(10.24, 50.39) * mm});
            skLineSegment(sketch, "E353", {"start": v(10.24, 50.39) * mm, "end": v(10.45, 50.55) * mm});
            skLineSegment(sketch, "E354", {"start": v(10.45, 50.55) * mm, "end": v(10.67, 50.7) * mm});
            skLineSegment(sketch, "E355", {"start": v(10.67, 50.7) * mm, "end": v(10.9, 50.81) * mm});
            skLineSegment(sketch, "E356", {"start": v(10.9, 50.81) * mm, "end": v(11.15, 50.92) * mm});
            skLineSegment(sketch, "E357", {"start": v(11.15, 50.92) * mm, "end": v(11.4, 51) * mm});
            skLineSegment(sketch, "E358", {"start": v(11.4, 51) * mm, "end": v(11.66, 51.05) * mm});
            skLineSegment(sketch, "E359", {"start": v(11.66, 51.05) * mm, "end": v(11.92, 51.09) * mm});
            skLineSegment(sketch, "E360", {"start": v(11.92, 51.09) * mm, "end": v(11.94, 51.09) * mm});
            skLineSegment(sketch, "E361", {"start": v(11.94, 51.09) * mm, "end": v(11.94, 51.1) * mm});
            skLineSegment(sketch, "E362", {"start": v(11.94, 51.1) * mm, "end": v(25.2, 51.1) * mm});
            skLineSegment(sketch, "E363", {"start": v(25.2, 51.1) * mm, "end": v(25.2, 52.8) * mm});
            skLineSegment(sketch, "E364", {"start": v(25.2, 52.8) * mm, "end": v(11.88, 52.8) * mm});
            skLineSegment(sketch, "E365", {"start": v(11.88, 52.8) * mm, "end": v(11.88, 52.82) * mm});
            skLineSegment(sketch, "E366", {"start": v(11.88, 52.82) * mm, "end": v(11.87, 52.82) * mm});
            skLineSegment(sketch, "E367", {"start": v(11.87, 52.82) * mm, "end": v(11.6, 52.85) * mm});
            skLineSegment(sketch, "E368", {"start": v(11.6, 52.85) * mm, "end": v(11.34, 52.91) * mm});
            skLineSegment(sketch, "E369", {"start": v(11.34, 52.91) * mm, "end": v(11.1, 53) * mm});
            skLineSegment(sketch, "E370", {"start": v(11.1, 53) * mm, "end": v(10.85, 53.1) * mm});
            skLineSegment(sketch, "E371", {"start": v(10.85, 53.1) * mm, "end": v(10.61, 53.21) * mm});
            skLineSegment(sketch, "E372", {"start": v(10.61, 53.21) * mm, "end": v(10.39, 53.36) * mm});
            skLineSegment(sketch, "E373", {"start": v(10.39, 53.36) * mm, "end": v(10.18, 53.52) * mm});
            skLineSegment(sketch, "E374", {"start": v(10.18, 53.52) * mm, "end": v(9.98, 53.7) * mm});
            skLineSegment(sketch, "E375", {"start": v(9.98, 53.7) * mm, "end": v(9.8, 53.9) * mm});
            skLineSegment(sketch, "E376", {"start": v(9.8, 53.9) * mm, "end": v(9.64, 54.1) * mm});
            skLineSegment(sketch, "E377", {"start": v(9.64, 54.1) * mm, "end": v(9.5, 54.32) * mm});
            skLineSegment(sketch, "E378", {"start": v(9.5, 54.32) * mm, "end": v(9.38, 54.56) * mm});
            skLineSegment(sketch, "E379", {"start": v(9.38, 54.56) * mm, "end": v(9.28, 54.8) * mm});
            skLineSegment(sketch, "E380", {"start": v(9.28, 54.8) * mm, "end": v(9.2, 55.06) * mm});
            skLineSegment(sketch, "E381", {"start": v(9.2, 55.06) * mm, "end": v(9.14, 55.32) * mm});
            skLineSegment(sketch, "E382", {"start": v(9.14, 55.32) * mm, "end": v(9.1, 55.58) * mm});
            skLineSegment(sketch, "E383", {"start": v(9.1, 55.58) * mm, "end": v(9.1, 55.59) * mm});
            skLineSegment(sketch, "E384", {"start": v(9.1, 55.59) * mm, "end": v(9.1, 55.59) * mm});
            skLineSegment(sketch, "E385", {"start": v(26.9, 42.17) * mm, "end": v(26.9, 43.19) * mm});
            skLineSegment(sketch, "E386", {"start": v(26.9, 43.19) * mm, "end": v(28.22, 43.19) * mm});
            skLineSegment(sketch, "E387", {"start": v(28.22, 43.19) * mm, "end": v(28.22, 42.17) * mm});
            skLineSegment(sketch, "E388", {"start": v(28.22, 42.17) * mm, "end": v(26.9, 42.17) * mm});
            skLineSegment(sketch, "E389", {"start": v(28.6, 42.17) * mm, "end": v(28.6, 43.19) * mm});
            skLineSegment(sketch, "E390", {"start": v(28.6, 43.19) * mm, "end": v(29.92, 43.19) * mm});
            skLineSegment(sketch, "E391", {"start": v(29.92, 43.19) * mm, "end": v(29.92, 42.17) * mm});
            skLineSegment(sketch, "E392", {"start": v(29.92, 42.17) * mm, "end": v(28.6, 42.17) * mm});
            skLineSegment(sketch, "E393", {"start": v(21.8, 42.17) * mm, "end": v(21.8, 43.19) * mm});
            skLineSegment(sketch, "E394", {"start": v(21.8, 43.19) * mm, "end": v(23.11, 43.19) * mm});
            skLineSegment(sketch, "E395", {"start": v(23.11, 43.19) * mm, "end": v(23.11, 42.17) * mm});
            skLineSegment(sketch, "E396", {"start": v(23.11, 42.17) * mm, "end": v(21.8, 42.17) * mm});
            skLineSegment(sketch, "E397", {"start": v(25.8, 43.19) * mm, "end": v(25.8, 44.25) * mm});
            skLineSegment(sketch, "E398", {"start": v(25.8, 44.25) * mm, "end": v(26.31, 44.25) * mm});
            skLineSegment(sketch, "E399", {"start": v(26.31, 44.25) * mm, "end": v(26.31, 43.19) * mm});
            skLineSegment(sketch, "E400", {"start": v(26.31, 43.19) * mm, "end": v(25.8, 43.19) * mm});
            skLineSegment(sketch, "E401", {"start": v(27.33, 43.19) * mm, "end": v(27.33, 44.25) * mm});
            skLineSegment(sketch, "E402", {"start": v(27.33, 44.25) * mm, "end": v(27.84, 44.25) * mm});
            skLineSegment(sketch, "E403", {"start": v(27.84, 44.25) * mm, "end": v(27.84, 43.19) * mm});
            skLineSegment(sketch, "E404", {"start": v(27.84, 43.19) * mm, "end": v(27.33, 43.19) * mm});
            skLineSegment(sketch, "E405", {"start": v(28.44, 47.73) * mm, "end": v(36.08, 47.73) * mm});
            skArc(sketch, "E406", {"start": v(36.08, 47.73) * mm, "mid": v(37.7, 47.05) * mm, "end": v(38.38, 45.43) * mm});
            skLineSegment(sketch, "E407", {"start": v(38.38, 45.43) * mm, "end": v(38.38, 30.7) * mm});
            skArc(sketch, "E408", {"start": v(38.38, 30.7) * mm, "mid": v(39.2, 28.73) * mm, "end": v(41.16, 27.92) * mm});
            skLineSegment(sketch, "E409", {"start": v(41.16, 27.92) * mm, "end": v(48.9, 27.92) * mm});
            skLineSegment(sketch, "E410", {"start": v(48.9, 27.92) * mm, "end": v(48.9, 28.4) * mm});
            skLineSegment(sketch, "E411", {"start": v(48.9, 28.4) * mm, "end": v(41.16, 28.4) * mm});
            skArc(sketch, "E412", {"start": v(41.16, 28.4) * mm, "mid": v(39.53, 29.07) * mm, "end": v(38.86, 30.7) * mm});
            skLineSegment(sketch, "E413", {"start": v(38.86, 30.7) * mm, "end": v(38.86, 45.43) * mm});
            skArc(sketch, "E414", {"start": v(38.86, 45.43) * mm, "mid": v(38.05, 47.4) * mm, "end": v(36.08, 48.2) * mm});
            skLineSegment(sketch, "E415", {"start": v(36.08, 48.2) * mm, "end": v(28.44, 48.2) * mm});
            skLineSegment(sketch, "E416", {"start": v(28.44, 48.2) * mm, "end": v(28.44, 47.73) * mm});
            skLineSegment(sketch, "E417", {"start": v(28.45, 50.38) * mm, "end": v(41.45, 50.38) * mm});
            skArc(sketch, "E418", {"start": v(41.45, 50.38) * mm, "mid": v(43.08, 49.7) * mm, "end": v(43.75, 48.08) * mm});
            skLineSegment(sketch, "E419", {"start": v(43.75, 48.08) * mm, "end": v(43.75, 46.65) * mm});
            skArc(sketch, "E420", {"start": v(43.75, 46.65) * mm, "mid": v(44.56, 44.68) * mm, "end": v(46.53, 43.87) * mm});
            skLineSegment(sketch, "E421", {"start": v(46.53, 43.87) * mm, "end": v(48.9, 43.87) * mm});
            skLineSegment(sketch, "E422", {"start": v(48.9, 43.87) * mm, "end": v(48.9, 44.35) * mm});
            skLineSegment(sketch, "E423", {"start": v(48.9, 44.35) * mm, "end": v(46.53, 44.35) * mm});
            skArc(sketch, "E424", {"start": v(46.53, 44.35) * mm, "mid": v(44.9, 45.02) * mm, "end": v(44.23, 46.65) * mm});
            skLineSegment(sketch, "E425", {"start": v(44.23, 46.65) * mm, "end": v(44.23, 48.08) * mm});
            skArc(sketch, "E426", {"start": v(44.23, 48.08) * mm, "mid": v(43.42, 50.05) * mm, "end": v(41.45, 50.86) * mm});
            skLineSegment(sketch, "E427", {"start": v(41.45, 50.86) * mm, "end": v(28.45, 50.86) * mm});
            skLineSegment(sketch, "E428", {"start": v(28.45, 50.86) * mm, "end": v(28.45, 50.38) * mm});
            skLineSegment(sketch, "E429", {"start": v(47.9, 76.43) * mm, "end": v(48.9, 76.43) * mm});
            skLineSegment(sketch, "E430", {"start": v(48.9, 76.43) * mm, "end": v(48.9, 75.95) * mm});
            skLineSegment(sketch, "E431", {"start": v(48.9, 75.95) * mm, "end": v(47.9, 75.95) * mm});
            skLineSegment(sketch, "E432", {"start": v(9.4, 48.06) * mm, "end": v(9.4, 46.63) * mm});
            skArc(sketch, "E433", {"start": v(9.4, 46.63) * mm, "mid": v(8.73, 45) * mm, "end": v(7.1, 44.33) * mm});
            skLineSegment(sketch, "E434", {"start": v(7.1, 44.33) * mm, "end": v(3.17, 44.33) * mm});
            skLineSegment(sketch, "E435", {"start": v(3.17, 44.33) * mm, "end": v(3.17, 43.99) * mm});
            skLineSegment(sketch, "E436", {"start": v(3.17, 43.99) * mm, "end": v(7.1, 43.99) * mm});
            skArc(sketch, "E437", {"start": v(7.1, 43.99) * mm, "mid": v(9.05, 44.73) * mm, "end": v(9.9, 46.63) * mm});
            skLineSegment(sketch, "E438", {"start": v(9.9, 46.63) * mm, "end": v(9.9, 48.06) * mm});
            skArc(sketch, "E439", {"start": v(9.9, 48.06) * mm, "mid": v(10.56, 49.69) * mm, "end": v(12.19, 50.36) * mm});
            skLineSegment(sketch, "E440", {"start": v(12.19, 50.36) * mm, "end": v(25.2, 50.36) * mm});
            skLineSegment(sketch, "E441", {"start": v(25.2, 50.36) * mm, "end": v(25.2, 50.85) * mm});
            skLineSegment(sketch, "E442", {"start": v(25.2, 50.85) * mm, "end": v(12.19, 50.85) * mm});
            skArc(sketch, "E443", {"start": v(12.19, 50.85) * mm, "mid": v(10.22, 50.03) * mm, "end": v(9.4, 48.06) * mm});
            skLineSegment(sketch, "E444", {"start": v(3.17, 75.93) * mm, "end": v(12.47, 75.93) * mm});
            skArc(sketch, "E445", {"start": v(12.47, 75.93) * mm, "mid": v(14.1, 75.26) * mm, "end": v(14.77, 73.63) * mm});
            skLineSegment(sketch, "E446", {"start": v(14.77, 73.63) * mm, "end": v(14.77, 58.53) * mm});
            skArc(sketch, "E447", {"start": v(14.77, 58.53) * mm, "mid": v(15.58, 56.56) * mm, "end": v(17.55, 55.75) * mm});
            skLineSegment(sketch, "E448", {"start": v(17.55, 55.75) * mm, "end": v(25.2, 55.75) * mm});
            skLineSegment(sketch, "E449", {"start": v(25.2, 55.75) * mm, "end": v(25.2, 56.23) * mm});
            skLineSegment(sketch, "E450", {"start": v(25.2, 56.23) * mm, "end": v(17.55, 56.23) * mm});
            skArc(sketch, "E451", {"start": v(17.55, 56.23) * mm, "mid": v(15.93, 56.9) * mm, "end": v(15.25, 58.53) * mm});
            skLineSegment(sketch, "E452", {"start": v(15.25, 58.53) * mm, "end": v(15.25, 73.63) * mm});
            skArc(sketch, "E453", {"start": v(15.25, 73.63) * mm, "mid": v(14.44, 75.6) * mm, "end": v(12.47, 76.41) * mm});
            skLineSegment(sketch, "E454", {"start": v(12.47, 76.41) * mm, "end": v(3.17, 76.41) * mm});
            skLineSegment(sketch, "E455", {"start": v(3.17, 76.41) * mm, "end": v(3.17, 75.93) * mm});
            skLineSegment(sketch, "E456", {"start": v(28.45, 52.82) * mm, "end": v(28.45, 51.12) * mm});
            skLineSegment(sketch, "E457", {"start": v(28.45, 51.12) * mm, "end": v(41.7, 51.12) * mm});
            skLineSegment(sketch, "E458", {"start": v(41.7, 51.12) * mm, "end": v(41.7, 51.1) * mm});
            skLineSegment(sketch, "E459", {"start": v(41.7, 51.1) * mm, "end": v(41.71, 51.1) * mm});
            skLineSegment(sketch, "E460", {"start": v(41.71, 51.1) * mm, "end": v(41.98, 51.07) * mm});
            skLineSegment(sketch, "E461", {"start": v(41.98, 51.07) * mm, "end": v(42.24, 51.01) * mm});
            skLineSegment(sketch, "E462", {"start": v(42.24, 51.01) * mm, "end": v(42.49, 50.93) * mm});
            skLineSegment(sketch, "E463", {"start": v(42.49, 50.93) * mm, "end": v(42.73, 50.83) * mm});
            skLineSegment(sketch, "E464", {"start": v(42.73, 50.83) * mm, "end": v(42.97, 50.7) * mm});
            skLineSegment(sketch, "E465", {"start": v(42.97, 50.7) * mm, "end": v(43.2, 50.57) * mm});
            skLineSegment(sketch, "E466", {"start": v(43.2, 50.57) * mm, "end": v(43.4, 50.4) * mm});
            skLineSegment(sketch, "E467", {"start": v(43.4, 50.4) * mm, "end": v(43.6, 50.23) * mm});
            skLineSegment(sketch, "E468", {"start": v(43.6, 50.23) * mm, "end": v(43.78, 50.03) * mm});
            skLineSegment(sketch, "E469", {"start": v(43.78, 50.03) * mm, "end": v(43.94, 49.82) * mm});
            skLineSegment(sketch, "E470", {"start": v(43.94, 49.82) * mm, "end": v(44.08, 49.6) * mm});
            skLineSegment(sketch, "E471", {"start": v(44.08, 49.6) * mm, "end": v(44.2, 49.36) * mm});
            skLineSegment(sketch, "E472", {"start": v(44.2, 49.36) * mm, "end": v(44.3, 49.12) * mm});
            skLineSegment(sketch, "E473", {"start": v(44.3, 49.12) * mm, "end": v(44.38, 48.87) * mm});
            skLineSegment(sketch, "E474", {"start": v(44.38, 48.87) * mm, "end": v(44.44, 48.6) * mm});
            skLineSegment(sketch, "E475", {"start": v(44.44, 48.6) * mm, "end": v(44.47, 48.34) * mm});
            skLineSegment(sketch, "E476", {"start": v(44.47, 48.34) * mm, "end": v(44.47, 48.33) * mm});
            skLineSegment(sketch, "E477", {"start": v(44.47, 48.33) * mm, "end": v(44.49, 48.33) * mm});
            skLineSegment(sketch, "E478", {"start": v(44.49, 48.33) * mm, "end": v(44.49, 46.65) * mm});
            skLineSegment(sketch, "E479", {"start": v(44.49, 46.65) * mm, "end": v(44.5, 46.47) * mm});
            skLineSegment(sketch, "E480", {"start": v(44.5, 46.47) * mm, "end": v(44.52, 46.3) * mm});
            skLineSegment(sketch, "E481", {"start": v(44.52, 46.3) * mm, "end": v(44.56, 46.12) * mm});
            skLineSegment(sketch, "E482", {"start": v(44.56, 46.12) * mm, "end": v(44.6, 45.95) * mm});
            skLineSegment(sketch, "E483", {"start": v(44.6, 45.95) * mm, "end": v(44.68, 45.78) * mm});
            skLineSegment(sketch, "E484", {"start": v(44.68, 45.78) * mm, "end": v(44.76, 45.63) * mm});
            skLineSegment(sketch, "E485", {"start": v(44.76, 45.63) * mm, "end": v(44.86, 45.48) * mm});
            skLineSegment(sketch, "E486", {"start": v(44.86, 45.48) * mm, "end": v(44.96, 45.33) * mm});
            skLineSegment(sketch, "E487", {"start": v(44.96, 45.33) * mm, "end": v(45.08, 45.2) * mm});
            skLineSegment(sketch, "E488", {"start": v(45.08, 45.2) * mm, "end": v(45.22, 45.08) * mm});
            skLineSegment(sketch, "E489", {"start": v(45.22, 45.08) * mm, "end": v(45.36, 44.97) * mm});
            skLineSegment(sketch, "E490", {"start": v(45.36, 44.97) * mm, "end": v(45.5, 44.88) * mm});
            skLineSegment(sketch, "E491", {"start": v(45.5, 44.88) * mm, "end": v(45.67, 44.8) * mm});
            skLineSegment(sketch, "E492", {"start": v(45.67, 44.8) * mm, "end": v(45.83, 44.73) * mm});
            skLineSegment(sketch, "E493", {"start": v(45.83, 44.73) * mm, "end": v(46, 44.67) * mm});
            skLineSegment(sketch, "E494", {"start": v(46, 44.67) * mm, "end": v(46.17, 44.63) * mm});
            skLineSegment(sketch, "E495", {"start": v(46.17, 44.63) * mm, "end": v(46.35, 44.61) * mm});
            skLineSegment(sketch, "E496", {"start": v(46.35, 44.61) * mm, "end": v(46.54, 44.6) * mm});
            skLineSegment(sketch, "E497", {"start": v(46.54, 44.6) * mm, "end": v(48.9, 44.6) * mm});
            skLineSegment(sketch, "E498", {"start": v(48.9, 44.6) * mm, "end": v(48.9, 59.64) * mm});
            skLineSegment(sketch, "E499", {"start": v(48.9, 59.64) * mm, "end": v(46.6, 59.64) * mm});
            skLineSegment(sketch, "E500", {"start": v(46.6, 59.64) * mm, "end": v(46.41, 59.63) * mm});
            skLineSegment(sketch, "E501", {"start": v(46.41, 59.63) * mm, "end": v(46.23, 59.6) * mm});
            skLineSegment(sketch, "E502", {"start": v(46.23, 59.6) * mm, "end": v(46.06, 59.57) * mm});
            skLineSegment(sketch, "E503", {"start": v(46.06, 59.57) * mm, "end": v(45.89, 59.52) * mm});
            skLineSegment(sketch, "E504", {"start": v(45.89, 59.52) * mm, "end": v(45.72, 59.45) * mm});
            skLineSegment(sketch, "E505", {"start": v(45.72, 59.45) * mm, "end": v(45.57, 59.37) * mm});
            skLineSegment(sketch, "E506", {"start": v(45.57, 59.37) * mm, "end": v(45.42, 59.27) * mm});
            skLineSegment(sketch, "E507", {"start": v(45.42, 59.27) * mm, "end": v(45.27, 59.16) * mm});
            skLineSegment(sketch, "E508", {"start": v(45.27, 59.16) * mm, "end": v(45.14, 59.04) * mm});
            skLineSegment(sketch, "E509", {"start": v(45.14, 59.04) * mm, "end": v(45.02, 58.9) * mm});
            skLineSegment(sketch, "E510", {"start": v(45.02, 58.9) * mm, "end": v(44.91, 58.77) * mm});
            skLineSegment(sketch, "E511", {"start": v(44.91, 58.77) * mm, "end": v(44.82, 58.62) * mm});
            skLineSegment(sketch, "E512", {"start": v(44.82, 58.62) * mm, "end": v(44.74, 58.46) * mm});
            skLineSegment(sketch, "E513", {"start": v(44.74, 58.46) * mm, "end": v(44.67, 58.3) * mm});
            skLineSegment(sketch, "E514", {"start": v(44.67, 58.3) * mm, "end": v(44.61, 58.12) * mm});
            skLineSegment(sketch, "E515", {"start": v(44.61, 58.12) * mm, "end": v(44.58, 57.95) * mm});
            skLineSegment(sketch, "E516", {"start": v(44.58, 57.95) * mm, "end": v(44.55, 57.77) * mm});
            skLineSegment(sketch, "E517", {"start": v(44.55, 57.77) * mm, "end": v(44.54, 57.59) * mm});
            skLineSegment(sketch, "E518", {"start": v(44.54, 57.59) * mm, "end": v(44.54, 55.6) * mm});
            skLineSegment(sketch, "E519", {"start": v(44.54, 55.6) * mm, "end": v(44.53, 55.6) * mm});
            skLineSegment(sketch, "E520", {"start": v(44.53, 55.6) * mm, "end": v(44.53, 55.6) * mm});
            skLineSegment(sketch, "E521", {"start": v(44.53, 55.6) * mm, "end": v(44.5, 55.33) * mm});
            skLineSegment(sketch, "E522", {"start": v(44.5, 55.33) * mm, "end": v(44.44, 55.07) * mm});
            skLineSegment(sketch, "E523", {"start": v(44.44, 55.07) * mm, "end": v(44.36, 54.82) * mm});
            skLineSegment(sketch, "E524", {"start": v(44.36, 54.82) * mm, "end": v(44.26, 54.58) * mm});
            skLineSegment(sketch, "E525", {"start": v(44.26, 54.58) * mm, "end": v(44.14, 54.34) * mm});
            skLineSegment(sketch, "E526", {"start": v(44.14, 54.34) * mm, "end": v(44, 54.12) * mm});
            skLineSegment(sketch, "E527", {"start": v(44, 54.12) * mm, "end": v(43.83, 53.9) * mm});
            skLineSegment(sketch, "E528", {"start": v(43.83, 53.9) * mm, "end": v(43.66, 53.71) * mm});
            skLineSegment(sketch, "E529", {"start": v(43.66, 53.71) * mm, "end": v(43.46, 53.53) * mm});
            skLineSegment(sketch, "E530", {"start": v(43.46, 53.53) * mm, "end": v(43.25, 53.37) * mm});
            skLineSegment(sketch, "E531", {"start": v(43.25, 53.37) * mm, "end": v(43.03, 53.23) * mm});
            skLineSegment(sketch, "E532", {"start": v(43.03, 53.23) * mm, "end": v(42.8, 53.1) * mm});
            skLineSegment(sketch, "E533", {"start": v(42.8, 53.1) * mm, "end": v(42.55, 53) * mm});
            skLineSegment(sketch, "E534", {"start": v(42.55, 53) * mm, "end": v(42.3, 52.93) * mm});
            skLineSegment(sketch, "E535", {"start": v(42.3, 52.93) * mm, "end": v(42.04, 52.87) * mm});
            skLineSegment(sketch, "E536", {"start": v(42.04, 52.87) * mm, "end": v(41.77, 52.83) * mm});
            skLineSegment(sketch, "E537", {"start": v(41.77, 52.83) * mm, "end": v(41.76, 52.83) * mm});
            skLineSegment(sketch, "E538", {"start": v(41.76, 52.83) * mm, "end": v(41.76, 52.82) * mm});
            skLineSegment(sketch, "E539", {"start": v(41.76, 52.82) * mm, "end": v(28.45, 52.82) * mm});
            skLineSegment(sketch, "E540", {"start": v(25.2, 48.45) * mm, "end": v(25.2, 50.1) * mm});
            skLineSegment(sketch, "E541", {"start": v(25.2, 50.1) * mm, "end": v(12.2, 50.1) * mm});
            skLineSegment(sketch, "E542", {"start": v(12.2, 50.1) * mm, "end": v(12.01, 50.1) * mm});
            skLineSegment(sketch, "E543", {"start": v(12.01, 50.1) * mm, "end": v(11.83, 50.08) * mm});
            skLineSegment(sketch, "E544", {"start": v(11.83, 50.08) * mm, "end": v(11.66, 50.04) * mm});
            skLineSegment(sketch, "E545", {"start": v(11.66, 50.04) * mm, "end": v(11.49, 49.98) * mm});
            skLineSegment(sketch, "E546", {"start": v(11.49, 49.98) * mm, "end": v(11.33, 49.92) * mm});
            skLineSegment(sketch, "E547", {"start": v(11.33, 49.92) * mm, "end": v(11.17, 49.83) * mm});
            skLineSegment(sketch, "E548", {"start": v(11.17, 49.83) * mm, "end": v(11.02, 49.74) * mm});
            skLineSegment(sketch, "E549", {"start": v(11.02, 49.74) * mm, "end": v(10.88, 49.63) * mm});
            skLineSegment(sketch, "E550", {"start": v(10.88, 49.63) * mm, "end": v(10.74, 49.5) * mm});
            skLineSegment(sketch, "E551", {"start": v(10.74, 49.5) * mm, "end": v(10.62, 49.38) * mm});
            skLineSegment(sketch, "E552", {"start": v(10.62, 49.38) * mm, "end": v(10.51, 49.24) * mm});
            skLineSegment(sketch, "E553", {"start": v(10.51, 49.24) * mm, "end": v(10.42, 49.09) * mm});
            skLineSegment(sketch, "E554", {"start": v(10.42, 49.09) * mm, "end": v(10.34, 48.93) * mm});
            skLineSegment(sketch, "E555", {"start": v(10.34, 48.93) * mm, "end": v(10.27, 48.76) * mm});
            skLineSegment(sketch, "E556", {"start": v(10.27, 48.76) * mm, "end": v(10.21, 48.6) * mm});
            skLineSegment(sketch, "E557", {"start": v(10.21, 48.6) * mm, "end": v(10.18, 48.42) * mm});
            skLineSegment(sketch, "E558", {"start": v(10.18, 48.42) * mm, "end": v(10.15, 48.24) * mm});
            skLineSegment(sketch, "E559", {"start": v(10.15, 48.24) * mm, "end": v(10.14, 48.06) * mm});
            skLineSegment(sketch, "E560", {"start": v(10.14, 48.06) * mm, "end": v(10.14, 46.38) * mm});
            skLineSegment(sketch, "E561", {"start": v(10.14, 46.38) * mm, "end": v(10.13, 46.38) * mm});
            skLineSegment(sketch, "E562", {"start": v(10.13, 46.38) * mm, "end": v(10.13, 46.37) * mm});
            skLineSegment(sketch, "E563", {"start": v(10.13, 46.37) * mm, "end": v(10.09, 46.11) * mm});
            skLineSegment(sketch, "E564", {"start": v(10.09, 46.11) * mm, "end": v(10.02, 45.86) * mm});
            skLineSegment(sketch, "E565", {"start": v(10.02, 45.86) * mm, "end": v(9.94, 45.62) * mm});
            skLineSegment(sketch, "E566", {"start": v(9.94, 45.62) * mm, "end": v(9.83, 45.38) * mm});
            skLineSegment(sketch, "E567", {"start": v(9.83, 45.38) * mm, "end": v(9.7, 45.15) * mm});
            skLineSegment(sketch, "E568", {"start": v(9.7, 45.15) * mm, "end": v(9.56, 44.94) * mm});
            skLineSegment(sketch, "E569", {"start": v(9.56, 44.94) * mm, "end": v(9.4, 44.74) * mm});
            skLineSegment(sketch, "E570", {"start": v(9.4, 44.74) * mm, "end": v(9.22, 44.55) * mm});
            skLineSegment(sketch, "E571", {"start": v(9.22, 44.55) * mm, "end": v(9.03, 44.38) * mm});
            skLineSegment(sketch, "E572", {"start": v(9.03, 44.38) * mm, "end": v(8.82, 44.23) * mm});
            skLineSegment(sketch, "E573", {"start": v(8.82, 44.23) * mm, "end": v(8.6, 44.1) * mm});
            skLineSegment(sketch, "E574", {"start": v(8.6, 44.1) * mm, "end": v(8.36, 43.98) * mm});
            skLineSegment(sketch, "E575", {"start": v(8.36, 43.98) * mm, "end": v(8.12, 43.89) * mm});
            skLineSegment(sketch, "E576", {"start": v(8.12, 43.89) * mm, "end": v(7.87, 43.82) * mm});
            skLineSegment(sketch, "E577", {"start": v(7.87, 43.82) * mm, "end": v(7.62, 43.77) * mm});
            skLineSegment(sketch, "E578", {"start": v(7.62, 43.77) * mm, "end": v(7.36, 43.74) * mm});
            skLineSegment(sketch, "E579", {"start": v(7.36, 43.74) * mm, "end": v(7.36, 43.73) * mm});
            skLineSegment(sketch, "E580", {"start": v(7.36, 43.73) * mm, "end": v(3.17, 43.73) * mm});
            skLineSegment(sketch, "E581", {"start": v(3.17, 43.73) * mm, "end": v(3.17, 28.64) * mm});
            skLineSegment(sketch, "E582", {"start": v(3.17, 28.64) * mm, "end": v(12.47, 28.64) * mm});
            skLineSegment(sketch, "E583", {"start": v(12.47, 28.64) * mm, "end": v(12.66, 28.64) * mm});
            skLineSegment(sketch, "E584", {"start": v(12.66, 28.64) * mm, "end": v(12.83, 28.67) * mm});
            skLineSegment(sketch, "E585", {"start": v(12.83, 28.67) * mm, "end": v(13, 28.7) * mm});
            skLineSegment(sketch, "E586", {"start": v(13, 28.7) * mm, "end": v(13.18, 28.76) * mm});
            skLineSegment(sketch, "E587", {"start": v(13.18, 28.76) * mm, "end": v(13.34, 28.83) * mm});
            skLineSegment(sketch, "E588", {"start": v(13.34, 28.83) * mm, "end": v(13.5, 28.9) * mm});
            skLineSegment(sketch, "E589", {"start": v(13.5, 28.9) * mm, "end": v(13.65, 29) * mm});
            skLineSegment(sketch, "E590", {"start": v(13.65, 29) * mm, "end": v(13.8, 29.11) * mm});
            skLineSegment(sketch, "E591", {"start": v(13.8, 29.11) * mm, "end": v(13.92, 29.23) * mm});
            skLineSegment(sketch, "E592", {"start": v(13.92, 29.23) * mm, "end": v(14.05, 29.37) * mm});
            skLineSegment(sketch, "E593", {"start": v(14.05, 29.37) * mm, "end": v(14.15, 29.5) * mm});
            skLineSegment(sketch, "E594", {"start": v(14.15, 29.5) * mm, "end": v(14.25, 29.66) * mm});
            skLineSegment(sketch, "E595", {"start": v(14.25, 29.66) * mm, "end": v(14.33, 29.82) * mm});
            skLineSegment(sketch, "E596", {"start": v(14.33, 29.82) * mm, "end": v(14.4, 29.98) * mm});
            skLineSegment(sketch, "E597", {"start": v(14.4, 29.98) * mm, "end": v(14.45, 30.15) * mm});
            skLineSegment(sketch, "E598", {"start": v(14.45, 30.15) * mm, "end": v(14.5, 30.33) * mm});
            skLineSegment(sketch, "E599", {"start": v(14.5, 30.33) * mm, "end": v(14.52, 30.5) * mm});
            skLineSegment(sketch, "E600", {"start": v(14.52, 30.5) * mm, "end": v(14.52, 30.69) * mm});
            skLineSegment(sketch, "E601", {"start": v(14.52, 30.69) * mm, "end": v(14.52, 45.67) * mm});
            skLineSegment(sketch, "E602", {"start": v(14.52, 45.67) * mm, "end": v(14.53, 45.67) * mm});
            skLineSegment(sketch, "E603", {"start": v(14.53, 45.67) * mm, "end": v(14.54, 45.68) * mm});
            skLineSegment(sketch, "E604", {"start": v(14.54, 45.68) * mm, "end": v(14.57, 45.94) * mm});
            skLineSegment(sketch, "E605", {"start": v(14.57, 45.94) * mm, "end": v(14.63, 46.2) * mm});
            skLineSegment(sketch, "E606", {"start": v(14.63, 46.2) * mm, "end": v(14.7, 46.45) * mm});
            skLineSegment(sketch, "E607", {"start": v(14.7, 46.45) * mm, "end": v(14.8, 46.7) * mm});
            skLineSegment(sketch, "E608", {"start": v(14.8, 46.7) * mm, "end": v(14.93, 46.93) * mm});
            skLineSegment(sketch, "E609", {"start": v(14.93, 46.93) * mm, "end": v(15.07, 47.15) * mm});
            skLineSegment(sketch, "E610", {"start": v(15.07, 47.15) * mm, "end": v(15.23, 47.36) * mm});
            skLineSegment(sketch, "E611", {"start": v(15.23, 47.36) * mm, "end": v(15.41, 47.56) * mm});
            skLineSegment(sketch, "E612", {"start": v(15.41, 47.56) * mm, "end": v(15.6, 47.74) * mm});
            skLineSegment(sketch, "E613", {"start": v(15.6, 47.74) * mm, "end": v(15.82, 47.9) * mm});
            skLineSegment(sketch, "E614", {"start": v(15.82, 47.9) * mm, "end": v(16.04, 48.04) * mm});
            skLineSegment(sketch, "E615", {"start": v(16.04, 48.04) * mm, "end": v(16.28, 48.16) * mm});
            skLineSegment(sketch, "E616", {"start": v(16.28, 48.16) * mm, "end": v(16.52, 48.26) * mm});
            skLineSegment(sketch, "E617", {"start": v(16.52, 48.26) * mm, "end": v(16.77, 48.34) * mm});
            skLineSegment(sketch, "E618", {"start": v(16.77, 48.34) * mm, "end": v(17.03, 48.4) * mm});
            skLineSegment(sketch, "E619", {"start": v(17.03, 48.4) * mm, "end": v(17.3, 48.44) * mm});
            skLineSegment(sketch, "E620", {"start": v(17.3, 48.44) * mm, "end": v(17.3, 48.44) * mm});
            skLineSegment(sketch, "E621", {"start": v(17.3, 48.44) * mm, "end": v(17.3, 48.45) * mm});
            skLineSegment(sketch, "E622", {"start": v(17.3, 48.45) * mm, "end": v(25.2, 48.45) * mm});
            skLineSegment(sketch, "E623", {"start": v(43.8, 57.6) * mm, "end": v(43.8, 55.86) * mm});
            skArc(sketch, "E624", {"start": v(43.8, 55.86) * mm, "mid": v(43.13, 54.23) * mm, "end": v(41.5, 53.56) * mm});
            skLineSegment(sketch, "E625", {"start": v(41.5, 53.56) * mm, "end": v(28.45, 53.56) * mm});
            skLineSegment(sketch, "E626", {"start": v(28.45, 53.56) * mm, "end": v(28.45, 53.08) * mm});
            skLineSegment(sketch, "E627", {"start": v(28.45, 53.08) * mm, "end": v(41.5, 53.08) * mm});
            skArc(sketch, "E628", {"start": v(41.5, 53.08) * mm, "mid": v(43.48, 53.9) * mm, "end": v(44.3, 55.86) * mm});
            skLineSegment(sketch, "E629", {"start": v(44.3, 55.86) * mm, "end": v(44.3, 57.6) * mm});
            skArc(sketch, "E630", {"start": v(44.3, 57.6) * mm, "mid": v(44.96, 59.22) * mm, "end": v(46.59, 59.9) * mm});
            skLineSegment(sketch, "E631", {"start": v(46.59, 59.9) * mm, "end": v(48.9, 59.9) * mm});
            skLineSegment(sketch, "E632", {"start": v(48.9, 59.9) * mm, "end": v(48.9, 60.38) * mm});
            skLineSegment(sketch, "E633", {"start": v(48.9, 60.38) * mm, "end": v(46.59, 60.38) * mm});
            skArc(sketch, "E634", {"start": v(46.59, 60.38) * mm, "mid": v(44.62, 59.56) * mm, "end": v(43.8, 57.6) * mm});
            skLineSegment(sketch, "E635", {"start": v(28.45, 47.47) * mm, "end": v(28.45, 45.84) * mm});
            skLineSegment(sketch, "E636", {"start": v(25.2, 45.84) * mm, "end": v(25.2, 47.46) * mm});
            skLineSegment(sketch, "E637", {"start": v(25.2, 47.46) * mm, "end": v(17.56, 47.46) * mm});
            skLineSegment(sketch, "E638", {"start": v(17.56, 47.46) * mm, "end": v(17.38, 47.45) * mm});
            skLineSegment(sketch, "E639", {"start": v(17.38, 47.45) * mm, "end": v(17.2, 47.43) * mm});
            skLineSegment(sketch, "E640", {"start": v(17.2, 47.43) * mm, "end": v(17.03, 47.39) * mm});
            skLineSegment(sketch, "E641", {"start": v(17.03, 47.39) * mm, "end": v(16.86, 47.33) * mm});
            skLineSegment(sketch, "E642", {"start": v(16.86, 47.33) * mm, "end": v(16.7, 47.27) * mm});
            skLineSegment(sketch, "E643", {"start": v(16.7, 47.27) * mm, "end": v(16.54, 47.18) * mm});
            skLineSegment(sketch, "E644", {"start": v(16.54, 47.18) * mm, "end": v(16.39, 47.09) * mm});
            skLineSegment(sketch, "E645", {"start": v(16.39, 47.09) * mm, "end": v(16.24, 46.98) * mm});
            skLineSegment(sketch, "E646", {"start": v(16.24, 46.98) * mm, "end": v(16.11, 46.86) * mm});
            skLineSegment(sketch, "E647", {"start": v(16.11, 46.86) * mm, "end": v(16, 46.73) * mm});
            skLineSegment(sketch, "E648", {"start": v(16, 46.73) * mm, "end": v(15.88, 46.59) * mm});
            skLineSegment(sketch, "E649", {"start": v(15.88, 46.59) * mm, "end": v(15.79, 46.43) * mm});
            skLineSegment(sketch, "E650", {"start": v(15.79, 46.43) * mm, "end": v(15.7, 46.28) * mm});
            skLineSegment(sketch, "E651", {"start": v(15.7, 46.28) * mm, "end": v(15.64, 46.11) * mm});
            skLineSegment(sketch, "E652", {"start": v(15.64, 46.11) * mm, "end": v(15.58, 45.94) * mm});
            skLineSegment(sketch, "E653", {"start": v(15.58, 45.94) * mm, "end": v(15.55, 45.77) * mm});
            skLineSegment(sketch, "E654", {"start": v(15.55, 45.77) * mm, "end": v(15.52, 45.6) * mm});
            skLineSegment(sketch, "E655", {"start": v(15.52, 45.6) * mm, "end": v(15.51, 45.4) * mm});
            skLineSegment(sketch, "E656", {"start": v(15.51, 45.4) * mm, "end": v(15.51, 30.43) * mm});
            skLineSegment(sketch, "E657", {"start": v(15.51, 30.43) * mm, "end": v(15.5, 30.43) * mm});
            skLineSegment(sketch, "E658", {"start": v(15.5, 30.43) * mm, "end": v(15.5, 30.42) * mm});
            skLineSegment(sketch, "E659", {"start": v(15.5, 30.42) * mm, "end": v(15.47, 30.15) * mm});
            skLineSegment(sketch, "E660", {"start": v(15.47, 30.15) * mm, "end": v(15.41, 29.9) * mm});
            skLineSegment(sketch, "E661", {"start": v(15.41, 29.9) * mm, "end": v(15.33, 29.64) * mm});
            skLineSegment(sketch, "E662", {"start": v(15.33, 29.64) * mm, "end": v(15.23, 29.4) * mm});
            skLineSegment(sketch, "E663", {"start": v(15.23, 29.4) * mm, "end": v(15.1, 29.16) * mm});
            skLineSegment(sketch, "E664", {"start": v(15.1, 29.16) * mm, "end": v(14.97, 28.94) * mm});
            skLineSegment(sketch, "E665", {"start": v(14.97, 28.94) * mm, "end": v(14.8, 28.73) * mm});
            skLineSegment(sketch, "E666", {"start": v(14.8, 28.73) * mm, "end": v(14.63, 28.53) * mm});
            skLineSegment(sketch, "E667", {"start": v(14.63, 28.53) * mm, "end": v(14.43, 28.36) * mm});
            skLineSegment(sketch, "E668", {"start": v(14.43, 28.36) * mm, "end": v(14.22, 28.2) * mm});
            skLineSegment(sketch, "E669", {"start": v(14.22, 28.2) * mm, "end": v(14, 28.05) * mm});
            skLineSegment(sketch, "E670", {"start": v(14, 28.05) * mm, "end": v(13.76, 27.93) * mm});
            skLineSegment(sketch, "E671", {"start": v(13.76, 27.93) * mm, "end": v(13.52, 27.83) * mm});
            skLineSegment(sketch, "E672", {"start": v(13.52, 27.83) * mm, "end": v(13.26, 27.75) * mm});
            skLineSegment(sketch, "E673", {"start": v(13.26, 27.75) * mm, "end": v(13, 27.7) * mm});
            skLineSegment(sketch, "E674", {"start": v(13, 27.7) * mm, "end": v(12.74, 27.66) * mm});
            skLineSegment(sketch, "E675", {"start": v(12.74, 27.66) * mm, "end": v(12.73, 27.66) * mm});
            skLineSegment(sketch, "E676", {"start": v(12.73, 27.66) * mm, "end": v(12.73, 27.65) * mm});
            skLineSegment(sketch, "E677", {"start": v(12.73, 27.65) * mm, "end": v(3.17, 27.65) * mm});
            skLineSegment(sketch, "E678", {"start": v(3.17, 27.65) * mm, "end": v(3.17, 11.85) * mm});
            skLineSegment(sketch, "E679", {"start": v(3.17, 11.85) * mm, "end": v(48.9, 11.85) * mm});
            skLineSegment(sketch, "E680", {"start": v(48.9, 11.85) * mm, "end": v(48.9, 27.66) * mm});
            skLineSegment(sketch, "E681", {"start": v(48.9, 27.66) * mm, "end": v(40.9, 27.66) * mm});
            skLineSegment(sketch, "E682", {"start": v(40.9, 27.66) * mm, "end": v(40.9, 27.67) * mm});
            skLineSegment(sketch, "E683", {"start": v(40.9, 27.67) * mm, "end": v(40.9, 27.67) * mm});
            skLineSegment(sketch, "E684", {"start": v(40.9, 27.67) * mm, "end": v(40.63, 27.7) * mm});
            skLineSegment(sketch, "E685", {"start": v(40.63, 27.7) * mm, "end": v(40.37, 27.76) * mm});
            skLineSegment(sketch, "E686", {"start": v(40.37, 27.76) * mm, "end": v(40.12, 27.84) * mm});
            skLineSegment(sketch, "E687", {"start": v(40.12, 27.84) * mm, "end": v(39.88, 27.95) * mm});
            skLineSegment(sketch, "E688", {"start": v(39.88, 27.95) * mm, "end": v(39.64, 28.07) * mm});
            skLineSegment(sketch, "E689", {"start": v(39.64, 28.07) * mm, "end": v(39.42, 28.21) * mm});
            skLineSegment(sketch, "E690", {"start": v(39.42, 28.21) * mm, "end": v(39.2, 28.37) * mm});
            skLineSegment(sketch, "E691", {"start": v(39.2, 28.37) * mm, "end": v(39.01, 28.55) * mm});
            skLineSegment(sketch, "E692", {"start": v(39.01, 28.55) * mm, "end": v(38.83, 28.75) * mm});
            skLineSegment(sketch, "E693", {"start": v(38.83, 28.75) * mm, "end": v(38.67, 28.96) * mm});
            skLineSegment(sketch, "E694", {"start": v(38.67, 28.96) * mm, "end": v(38.53, 29.18) * mm});
            skLineSegment(sketch, "E695", {"start": v(38.53, 29.18) * mm, "end": v(38.4, 29.41) * mm});
            skLineSegment(sketch, "E696", {"start": v(38.4, 29.41) * mm, "end": v(38.3, 29.66) * mm});
            skLineSegment(sketch, "E697", {"start": v(38.3, 29.66) * mm, "end": v(38.23, 29.91) * mm});
            skLineSegment(sketch, "E698", {"start": v(38.23, 29.91) * mm, "end": v(38.17, 30.17) * mm});
            skLineSegment(sketch, "E699", {"start": v(38.17, 30.17) * mm, "end": v(38.14, 30.43) * mm});
            skLineSegment(sketch, "E700", {"start": v(38.14, 30.43) * mm, "end": v(38.14, 30.44) * mm});
            skLineSegment(sketch, "E701", {"start": v(38.14, 30.44) * mm, "end": v(38.12, 30.44) * mm});
            skLineSegment(sketch, "E702", {"start": v(38.12, 30.44) * mm, "end": v(38.12, 45.42) * mm});
            skLineSegment(sketch, "E703", {"start": v(38.12, 45.42) * mm, "end": v(38.12, 45.6) * mm});
            skLineSegment(sketch, "E704", {"start": v(38.12, 45.6) * mm, "end": v(38.1, 45.78) * mm});
            skLineSegment(sketch, "E705", {"start": v(38.1, 45.78) * mm, "end": v(38.05, 45.96) * mm});
            skLineSegment(sketch, "E706", {"start": v(38.05, 45.96) * mm, "end": v(38, 46.13) * mm});
            skLineSegment(sketch, "E707", {"start": v(38, 46.13) * mm, "end": v(37.93, 46.3) * mm});
            skLineSegment(sketch, "E708", {"start": v(37.93, 46.3) * mm, "end": v(37.85, 46.45) * mm});
            skLineSegment(sketch, "E709", {"start": v(37.85, 46.45) * mm, "end": v(37.75, 46.6) * mm});
            skLineSegment(sketch, "E710", {"start": v(37.75, 46.6) * mm, "end": v(37.65, 46.74) * mm});
            skLineSegment(sketch, "E711", {"start": v(37.65, 46.74) * mm, "end": v(37.53, 46.87) * mm});
            skLineSegment(sketch, "E712", {"start": v(37.53, 46.87) * mm, "end": v(37.4, 47) * mm});
            skLineSegment(sketch, "E713", {"start": v(37.4, 47) * mm, "end": v(37.25, 47.1) * mm});
            skLineSegment(sketch, "E714", {"start": v(37.25, 47.1) * mm, "end": v(37.1, 47.2) * mm});
            skLineSegment(sketch, "E715", {"start": v(37.1, 47.2) * mm, "end": v(36.94, 47.28) * mm});
            skLineSegment(sketch, "E716", {"start": v(36.94, 47.28) * mm, "end": v(36.78, 47.35) * mm});
            skLineSegment(sketch, "E717", {"start": v(36.78, 47.35) * mm, "end": v(36.6, 47.4) * mm});
            skLineSegment(sketch, "E718", {"start": v(36.6, 47.4) * mm, "end": v(36.44, 47.44) * mm});
            skLineSegment(sketch, "E719", {"start": v(36.44, 47.44) * mm, "end": v(36.26, 47.47) * mm});
            skLineSegment(sketch, "E720", {"start": v(36.26, 47.47) * mm, "end": v(36.07, 47.47) * mm});
            skLineSegment(sketch, "E721", {"start": v(36.07, 47.47) * mm, "end": v(28.45, 47.47) * mm});
            skLineSegment(sketch, "E722", {"start": v(20.1, 42.17) * mm, "end": v(20.1, 43.19) * mm});
            skLineSegment(sketch, "E723", {"start": v(20.1, 43.19) * mm, "end": v(21.41, 43.19) * mm});
            skLineSegment(sketch, "E724", {"start": v(21.41, 43.19) * mm, "end": v(21.41, 42.17) * mm});
            skLineSegment(sketch, "E725", {"start": v(21.41, 42.17) * mm, "end": v(20.1, 42.17) * mm});
            skLineSegment(sketch, "E726", {"start": v(30.3, 42.17) * mm, "end": v(30.3, 43.19) * mm});
            skLineSegment(sketch, "E727", {"start": v(30.3, 43.19) * mm, "end": v(31.62, 43.19) * mm});
            skLineSegment(sketch, "E728", {"start": v(31.62, 43.19) * mm, "end": v(31.62, 42.17) * mm});
            skLineSegment(sketch, "E729", {"start": v(31.62, 42.17) * mm, "end": v(30.3, 42.17) * mm});
            skLineSegment(sketch, "E730", {"start": v(32, 58.37) * mm, "end": v(32, 59.43) * mm});
            skLineSegment(sketch, "E731", {"start": v(32, 59.43) * mm, "end": v(32.51, 59.43) * mm});
            skLineSegment(sketch, "E732", {"start": v(32.51, 59.43) * mm, "end": v(32.51, 58.37) * mm});
            skLineSegment(sketch, "E733", {"start": v(32.51, 58.37) * mm, "end": v(32, 58.37) * mm});
            skLineSegment(sketch, "E734", {"start": v(20.9, 43.19) * mm, "end": v(20.9, 44.25) * mm});
            skLineSegment(sketch, "E735", {"start": v(20.9, 44.25) * mm, "end": v(21.41, 44.25) * mm});
            skLineSegment(sketch, "E736", {"start": v(21.41, 44.25) * mm, "end": v(21.41, 43.19) * mm});
            skLineSegment(sketch, "E737", {"start": v(21.41, 43.19) * mm, "end": v(20.9, 43.19) * mm});
            skLineSegment(sketch, "E738", {"start": v(32, 42.17) * mm, "end": v(32, 43.19) * mm});
            skLineSegment(sketch, "E739", {"start": v(32, 43.19) * mm, "end": v(33.32, 43.19) * mm});
            skLineSegment(sketch, "E740", {"start": v(33.32, 43.19) * mm, "end": v(33.32, 42.17) * mm});
            skLineSegment(sketch, "E741", {"start": v(33.32, 42.17) * mm, "end": v(32, 42.17) * mm});
            skLineSegment(sketch, "E742", {"start": v(24.28, 43.19) * mm, "end": v(24.28, 44.25) * mm});
            skLineSegment(sketch, "E743", {"start": v(24.28, 44.25) * mm, "end": v(24.8, 44.25) * mm});
            skLineSegment(sketch, "E744", {"start": v(24.8, 44.25) * mm, "end": v(24.8, 43.19) * mm});
            skLineSegment(sketch, "E745", {"start": v(24.8, 43.19) * mm, "end": v(24.28, 43.19) * mm});
            skLineSegment(sketch, "E746", {"start": v(24.28, 58.34) * mm, "end": v(24.28, 59.4) * mm});
            skLineSegment(sketch, "E747", {"start": v(24.28, 59.4) * mm, "end": v(24.8, 59.4) * mm});
            skLineSegment(sketch, "E748", {"start": v(24.8, 59.4) * mm, "end": v(24.8, 58.34) * mm});
            skLineSegment(sketch, "E749", {"start": v(24.8, 58.34) * mm, "end": v(24.28, 58.34) * mm});
            skLineSegment(sketch, "E750", {"start": v(23.5, 42.17) * mm, "end": v(23.5, 43.19) * mm});
            skLineSegment(sketch, "E751", {"start": v(23.5, 43.19) * mm, "end": v(24.82, 43.19) * mm});
            skLineSegment(sketch, "E752", {"start": v(24.82, 43.19) * mm, "end": v(24.82, 42.17) * mm});
            skLineSegment(sketch, "E753", {"start": v(24.82, 42.17) * mm, "end": v(23.5, 42.17) * mm});
            skLineSegment(sketch, "E754", {"start": v(22.48, 43.19) * mm, "end": v(22.48, 44.25) * mm});
            skLineSegment(sketch, "E755", {"start": v(22.48, 44.25) * mm, "end": v(22.99, 44.25) * mm});
            skLineSegment(sketch, "E756", {"start": v(22.99, 44.25) * mm, "end": v(22.99, 43.19) * mm});
            skLineSegment(sketch, "E757", {"start": v(22.99, 43.19) * mm, "end": v(22.48, 43.19) * mm});
            skLineSegment(sketch, "E758", {"start": v(32, 43.16) * mm, "end": v(32, 44.23) * mm});
            skLineSegment(sketch, "E759", {"start": v(32, 44.23) * mm, "end": v(32.51, 44.23) * mm});
            skLineSegment(sketch, "E760", {"start": v(32.51, 44.23) * mm, "end": v(32.51, 43.16) * mm});
            skLineSegment(sketch, "E761", {"start": v(32.51, 43.16) * mm, "end": v(32, 43.16) * mm});
            skLineSegment(sketch, "E762", {"start": v(30.58, 43.19) * mm, "end": v(30.58, 44.25) * mm});
            skLineSegment(sketch, "E763", {"start": v(30.58, 44.25) * mm, "end": v(31.09, 44.25) * mm});
            skLineSegment(sketch, "E764", {"start": v(31.09, 44.25) * mm, "end": v(31.09, 43.19) * mm});
            skLineSegment(sketch, "E765", {"start": v(31.09, 43.19) * mm, "end": v(30.58, 43.19) * mm});
            skLineSegment(sketch, "E766", {"start": v(25.2, 42.17) * mm, "end": v(25.2, 43.19) * mm});
            skLineSegment(sketch, "E767", {"start": v(25.2, 43.19) * mm, "end": v(26.52, 43.19) * mm});
            skLineSegment(sketch, "E768", {"start": v(26.52, 43.19) * mm, "end": v(26.52, 42.17) * mm});
            skLineSegment(sketch, "E769", {"start": v(26.52, 42.17) * mm, "end": v(25.2, 42.17) * mm});
            skLineSegment(sketch, "E770", {"start": v(23.5, 59.4) * mm, "end": v(23.5, 60.42) * mm});
            skLineSegment(sketch, "E771", {"start": v(23.5, 60.42) * mm, "end": v(24.82, 60.42) * mm});
            skLineSegment(sketch, "E772", {"start": v(24.82, 60.42) * mm, "end": v(24.82, 59.4) * mm});
            skLineSegment(sketch, "E773", {"start": v(24.82, 59.4) * mm, "end": v(23.5, 59.4) * mm});
            skLineSegment(sketch, "E774", {"start": v(30.3, 59.4) * mm, "end": v(30.3, 60.42) * mm});
            skLineSegment(sketch, "E775", {"start": v(30.3, 60.42) * mm, "end": v(31.62, 60.42) * mm});
            skLineSegment(sketch, "E776", {"start": v(31.62, 60.42) * mm, "end": v(31.62, 59.4) * mm});
            skLineSegment(sketch, "E777", {"start": v(31.62, 59.4) * mm, "end": v(30.3, 59.4) * mm});
            skLineSegment(sketch, "E778", {"start": v(21.8, 59.4) * mm, "end": v(21.8, 60.42) * mm});
            skLineSegment(sketch, "E779", {"start": v(21.8, 60.42) * mm, "end": v(23.11, 60.42) * mm});
            skLineSegment(sketch, "E780", {"start": v(23.11, 60.42) * mm, "end": v(23.11, 59.4) * mm});
            skLineSegment(sketch, "E781", {"start": v(23.11, 59.4) * mm, "end": v(21.8, 59.4) * mm});
            skLineSegment(sketch, "E782", {"start": v(32, 59.4) * mm, "end": v(32, 60.42) * mm});
            skLineSegment(sketch, "E783", {"start": v(32, 60.42) * mm, "end": v(33.32, 60.42) * mm});
            skLineSegment(sketch, "E784", {"start": v(33.32, 60.42) * mm, "end": v(33.32, 59.4) * mm});
            skLineSegment(sketch, "E785", {"start": v(33.32, 59.4) * mm, "end": v(32, 59.4) * mm});
            skLineSegment(sketch, "E786", {"start": v(27.33, 58.34) * mm, "end": v(27.33, 59.4) * mm});
            skLineSegment(sketch, "E787", {"start": v(27.33, 59.4) * mm, "end": v(27.84, 59.4) * mm});
            skLineSegment(sketch, "E788", {"start": v(27.84, 59.4) * mm, "end": v(27.84, 58.34) * mm});
            skLineSegment(sketch, "E789", {"start": v(27.84, 58.34) * mm, "end": v(27.33, 58.34) * mm});
            skLineSegment(sketch, "E790", {"start": v(20.1, 59.4) * mm, "end": v(20.1, 60.42) * mm});
            skLineSegment(sketch, "E791", {"start": v(20.1, 60.42) * mm, "end": v(21.41, 60.42) * mm});
            skLineSegment(sketch, "E792", {"start": v(21.41, 60.42) * mm, "end": v(21.41, 59.4) * mm});
            skLineSegment(sketch, "E793", {"start": v(21.41, 59.4) * mm, "end": v(20.1, 59.4) * mm});
            skLineSegment(sketch, "E794", {"start": v(25.2, 59.4) * mm, "end": v(25.2, 60.42) * mm});
            skLineSegment(sketch, "E795", {"start": v(25.2, 60.42) * mm, "end": v(26.52, 60.42) * mm});
            skLineSegment(sketch, "E796", {"start": v(26.52, 60.42) * mm, "end": v(26.52, 59.4) * mm});
            skLineSegment(sketch, "E797", {"start": v(26.52, 59.4) * mm, "end": v(25.2, 59.4) * mm});
            skLineSegment(sketch, "E798", {"start": v(28.6, 59.4) * mm, "end": v(28.6, 60.42) * mm});
            skLineSegment(sketch, "E799", {"start": v(28.6, 60.42) * mm, "end": v(29.92, 60.42) * mm});
            skLineSegment(sketch, "E800", {"start": v(29.92, 60.42) * mm, "end": v(29.92, 59.4) * mm});
            skLineSegment(sketch, "E801", {"start": v(29.92, 59.4) * mm, "end": v(28.6, 59.4) * mm});
            skLineSegment(sketch, "E802", {"start": v(28.85, 58.34) * mm, "end": v(28.85, 59.4) * mm});
            skLineSegment(sketch, "E803", {"start": v(28.85, 59.4) * mm, "end": v(29.36, 59.4) * mm});
            skLineSegment(sketch, "E804", {"start": v(29.36, 59.4) * mm, "end": v(29.36, 58.34) * mm});
            skLineSegment(sketch, "E805", {"start": v(29.36, 58.34) * mm, "end": v(28.85, 58.34) * mm});
            skLineSegment(sketch, "E806", {"start": v(26.9, 59.4) * mm, "end": v(26.9, 60.42) * mm});
            skLineSegment(sketch, "E807", {"start": v(26.9, 60.42) * mm, "end": v(28.22, 60.42) * mm});
            skLineSegment(sketch, "E808", {"start": v(28.22, 60.42) * mm, "end": v(28.22, 59.4) * mm});
            skLineSegment(sketch, "E809", {"start": v(28.22, 59.4) * mm, "end": v(26.9, 59.4) * mm});
            skLineSegment(sketch, "E810", {"start": v(22.48, 58.34) * mm, "end": v(22.48, 59.4) * mm});
            skLineSegment(sketch, "E811", {"start": v(22.48, 59.4) * mm, "end": v(22.99, 59.4) * mm});
            skLineSegment(sketch, "E812", {"start": v(22.99, 59.4) * mm, "end": v(22.99, 58.34) * mm});
            skLineSegment(sketch, "E813", {"start": v(22.99, 58.34) * mm, "end": v(22.48, 58.34) * mm});
            skLineSegment(sketch, "E814", {"start": v(20.9, 58.34) * mm, "end": v(20.9, 59.4) * mm});
            skLineSegment(sketch, "E815", {"start": v(20.9, 59.4) * mm, "end": v(21.41, 59.4) * mm});
            skLineSegment(sketch, "E816", {"start": v(21.41, 59.4) * mm, "end": v(21.41, 58.34) * mm});
            skLineSegment(sketch, "E817", {"start": v(21.41, 58.34) * mm, "end": v(20.9, 58.34) * mm});
            skLineSegment(sketch, "E818", {"start": v(28.45, 55.51) * mm, "end": v(28.45, 53.81) * mm});
            skLineSegment(sketch, "E819", {"start": v(28.45, 53.81) * mm, "end": v(41.5, 53.81) * mm});
            skLineSegment(sketch, "E820", {"start": v(41.5, 53.81) * mm, "end": v(41.69, 53.82) * mm});
            skLineSegment(sketch, "E821", {"start": v(41.69, 53.82) * mm, "end": v(41.86, 53.85) * mm});
            skLineSegment(sketch, "E822", {"start": v(41.86, 53.85) * mm, "end": v(42.04, 53.88) * mm});
            skLineSegment(sketch, "E823", {"start": v(42.04, 53.88) * mm, "end": v(42.2, 53.94) * mm});
            skLineSegment(sketch, "E824", {"start": v(42.2, 53.94) * mm, "end": v(42.37, 54) * mm});
            skLineSegment(sketch, "E825", {"start": v(42.37, 54) * mm, "end": v(42.53, 54.09) * mm});
            skLineSegment(sketch, "E826", {"start": v(42.53, 54.09) * mm, "end": v(42.68, 54.18) * mm});
            skLineSegment(sketch, "E827", {"start": v(42.68, 54.18) * mm, "end": v(42.82, 54.3) * mm});
            skLineSegment(sketch, "E828", {"start": v(42.82, 54.3) * mm, "end": v(42.95, 54.41) * mm});
            skLineSegment(sketch, "E829", {"start": v(42.95, 54.41) * mm, "end": v(43.08, 54.54) * mm});
            skLineSegment(sketch, "E830", {"start": v(43.08, 54.54) * mm, "end": v(43.18, 54.69) * mm});
            skLineSegment(sketch, "E831", {"start": v(43.18, 54.69) * mm, "end": v(43.28, 54.84) * mm});
            skLineSegment(sketch, "E832", {"start": v(43.28, 54.84) * mm, "end": v(43.36, 55) * mm});
            skLineSegment(sketch, "E833", {"start": v(43.36, 55) * mm, "end": v(43.43, 55.16) * mm});
            skLineSegment(sketch, "E834", {"start": v(43.43, 55.16) * mm, "end": v(43.48, 55.33) * mm});
            skLineSegment(sketch, "E835", {"start": v(43.48, 55.33) * mm, "end": v(43.52, 55.5) * mm});
            skLineSegment(sketch, "E836", {"start": v(43.52, 55.5) * mm, "end": v(43.55, 55.68) * mm});
            skLineSegment(sketch, "E837", {"start": v(43.55, 55.68) * mm, "end": v(43.55, 55.86) * mm});
            skLineSegment(sketch, "E838", {"start": v(43.55, 55.86) * mm, "end": v(43.55, 57.85) * mm});
            skLineSegment(sketch, "E839", {"start": v(43.55, 57.85) * mm, "end": v(43.56, 57.85) * mm});
            skLineSegment(sketch, "E840", {"start": v(43.56, 57.85) * mm, "end": v(43.56, 57.86) * mm});
            skLineSegment(sketch, "E841", {"start": v(43.56, 57.86) * mm, "end": v(43.6, 58.12) * mm});
            skLineSegment(sketch, "E842", {"start": v(43.6, 58.12) * mm, "end": v(43.66, 58.38) * mm});
            skLineSegment(sketch, "E843", {"start": v(43.66, 58.38) * mm, "end": v(43.74, 58.63) * mm});
            skLineSegment(sketch, "E844", {"start": v(43.74, 58.63) * mm, "end": v(43.84, 58.88) * mm});
            skLineSegment(sketch, "E845", {"start": v(43.84, 58.88) * mm, "end": v(43.96, 59.11) * mm});
            skLineSegment(sketch, "E846", {"start": v(43.96, 59.11) * mm, "end": v(44.1, 59.34) * mm});
            skLineSegment(sketch, "E847", {"start": v(44.1, 59.34) * mm, "end": v(44.26, 59.55) * mm});
            skLineSegment(sketch, "E848", {"start": v(44.26, 59.55) * mm, "end": v(44.44, 59.74) * mm});
            skLineSegment(sketch, "E849", {"start": v(44.44, 59.74) * mm, "end": v(44.64, 59.92) * mm});
            skLineSegment(sketch, "E850", {"start": v(44.64, 59.92) * mm, "end": v(44.85, 60.08) * mm});
            skLineSegment(sketch, "E851", {"start": v(44.85, 60.08) * mm, "end": v(45.07, 60.22) * mm});
            skLineSegment(sketch, "E852", {"start": v(45.07, 60.22) * mm, "end": v(45.3, 60.35) * mm});
            skLineSegment(sketch, "E853", {"start": v(45.3, 60.35) * mm, "end": v(45.55, 60.45) * mm});
            skLineSegment(sketch, "E854", {"start": v(45.55, 60.45) * mm, "end": v(45.8, 60.53) * mm});
            skLineSegment(sketch, "E855", {"start": v(45.8, 60.53) * mm, "end": v(46.06, 60.58) * mm});
            skLineSegment(sketch, "E856", {"start": v(46.06, 60.58) * mm, "end": v(46.32, 60.62) * mm});
            skLineSegment(sketch, "E857", {"start": v(46.32, 60.62) * mm, "end": v(46.33, 60.62) * mm});
            skLineSegment(sketch, "E858", {"start": v(46.33, 60.62) * mm, "end": v(46.33, 60.63) * mm});
            skLineSegment(sketch, "E859", {"start": v(46.33, 60.63) * mm, "end": v(48.9, 60.63) * mm});
            skLineSegment(sketch, "E860", {"start": v(48.9, 60.63) * mm, "end": v(48.9, 75.7) * mm});
            skLineSegment(sketch, "E861", {"start": v(48.9, 75.7) * mm, "end": v(41.17, 75.7) * mm});
            skLineSegment(sketch, "E862", {"start": v(41.17, 75.7) * mm, "end": v(40.99, 75.68) * mm});
            skLineSegment(sketch, "E863", {"start": v(40.99, 75.68) * mm, "end": v(40.81, 75.66) * mm});
            skLineSegment(sketch, "E864", {"start": v(40.81, 75.66) * mm, "end": v(40.64, 75.62) * mm});
            skLineSegment(sketch, "E865", {"start": v(40.64, 75.62) * mm, "end": v(40.47, 75.57) * mm});
            skLineSegment(sketch, "E866", {"start": v(40.47, 75.57) * mm, "end": v(40.3, 75.5) * mm});
            skLineSegment(sketch, "E867", {"start": v(40.3, 75.5) * mm, "end": v(40.15, 75.42) * mm});
            skLineSegment(sketch, "E868", {"start": v(40.15, 75.42) * mm, "end": v(40, 75.32) * mm});
            skLineSegment(sketch, "E869", {"start": v(40, 75.32) * mm, "end": v(39.85, 75.21) * mm});
            skLineSegment(sketch, "E870", {"start": v(39.85, 75.21) * mm, "end": v(39.72, 75.1) * mm});
            skLineSegment(sketch, "E871", {"start": v(39.72, 75.1) * mm, "end": v(39.6, 74.96) * mm});
            skLineSegment(sketch, "E872", {"start": v(39.6, 74.96) * mm, "end": v(39.5, 74.82) * mm});
            skLineSegment(sketch, "E873", {"start": v(39.5, 74.82) * mm, "end": v(39.4, 74.67) * mm});
            skLineSegment(sketch, "E874", {"start": v(39.4, 74.67) * mm, "end": v(39.31, 74.51) * mm});
            skLineSegment(sketch, "E875", {"start": v(39.31, 74.51) * mm, "end": v(39.25, 74.35) * mm});
            skLineSegment(sketch, "E876", {"start": v(39.25, 74.35) * mm, "end": v(39.2, 74.18) * mm});
            skLineSegment(sketch, "E877", {"start": v(39.2, 74.18) * mm, "end": v(39.15, 74) * mm});
            skLineSegment(sketch, "E878", {"start": v(39.15, 74) * mm, "end": v(39.13, 73.83) * mm});
            skLineSegment(sketch, "E879", {"start": v(39.13, 73.83) * mm, "end": v(39.12, 73.64) * mm});
            skLineSegment(sketch, "E880", {"start": v(39.12, 73.64) * mm, "end": v(39.12, 58.3) * mm});
            skLineSegment(sketch, "E881", {"start": v(39.12, 58.3) * mm, "end": v(39.11, 58.3) * mm});
            skLineSegment(sketch, "E882", {"start": v(39.11, 58.3) * mm, "end": v(39.11, 58.28) * mm});
            skLineSegment(sketch, "E883", {"start": v(39.11, 58.28) * mm, "end": v(39.08, 58.02) * mm});
            skLineSegment(sketch, "E884", {"start": v(39.08, 58.02) * mm, "end": v(39.02, 57.76) * mm});
            skLineSegment(sketch, "E885", {"start": v(39.02, 57.76) * mm, "end": v(38.94, 57.5) * mm});
            skLineSegment(sketch, "E886", {"start": v(38.94, 57.5) * mm, "end": v(38.84, 57.26) * mm});
            skLineSegment(sketch, "E887", {"start": v(38.84, 57.26) * mm, "end": v(38.72, 57.03) * mm});
            skLineSegment(sketch, "E888", {"start": v(38.72, 57.03) * mm, "end": v(38.57, 56.8) * mm});
            skLineSegment(sketch, "E889", {"start": v(38.57, 56.8) * mm, "end": v(38.41, 56.6) * mm});
            skLineSegment(sketch, "E890", {"start": v(38.41, 56.6) * mm, "end": v(38.23, 56.4) * mm});
            skLineSegment(sketch, "E891", {"start": v(38.23, 56.4) * mm, "end": v(38.04, 56.22) * mm});
            skLineSegment(sketch, "E892", {"start": v(38.04, 56.22) * mm, "end": v(37.83, 56.06) * mm});
            skLineSegment(sketch, "E893", {"start": v(37.83, 56.06) * mm, "end": v(37.6, 55.92) * mm});
            skLineSegment(sketch, "E894", {"start": v(37.6, 55.92) * mm, "end": v(37.37, 55.8) * mm});
            skLineSegment(sketch, "E895", {"start": v(37.37, 55.8) * mm, "end": v(37.13, 55.7) * mm});
            skLineSegment(sketch, "E896", {"start": v(37.13, 55.7) * mm, "end": v(36.87, 55.61) * mm});
            skLineSegment(sketch, "E897", {"start": v(36.87, 55.61) * mm, "end": v(36.61, 55.56) * mm});
            skLineSegment(sketch, "E898", {"start": v(36.61, 55.56) * mm, "end": v(36.35, 55.52) * mm});
            skLineSegment(sketch, "E899", {"start": v(36.35, 55.52) * mm, "end": v(36.34, 55.52) * mm});
            skLineSegment(sketch, "E900", {"start": v(36.34, 55.52) * mm, "end": v(36.34, 55.51) * mm});
            skLineSegment(sketch, "E901", {"start": v(36.34, 55.51) * mm, "end": v(28.45, 55.51) * mm});
            skLineSegment(sketch, "E902", {"start": v(30.58, 58.34) * mm, "end": v(30.58, 59.4) * mm});
            skLineSegment(sketch, "E903", {"start": v(30.58, 59.4) * mm, "end": v(31.09, 59.4) * mm});
            skLineSegment(sketch, "E904", {"start": v(31.09, 59.4) * mm, "end": v(31.09, 58.34) * mm});
            skLineSegment(sketch, "E905", {"start": v(31.09, 58.34) * mm, "end": v(30.58, 58.34) * mm});
            skLineSegment(sketch, "E906", {"start": v(25.8, 58.34) * mm, "end": v(25.8, 59.4) * mm});
            skLineSegment(sketch, "E907", {"start": v(25.8, 59.4) * mm, "end": v(26.31, 59.4) * mm});
            skLineSegment(sketch, "E908", {"start": v(26.31, 59.4) * mm, "end": v(26.31, 58.34) * mm});
            skLineSegment(sketch, "E909", {"start": v(26.31, 58.34) * mm, "end": v(25.8, 58.34) * mm});
            skLineSegment(sketch, "E910", {"start": v(28.85, 43.19) * mm, "end": v(28.85, 44.25) * mm});
            skLineSegment(sketch, "E911", {"start": v(28.85, 44.25) * mm, "end": v(29.36, 44.25) * mm});
            skLineSegment(sketch, "E912", {"start": v(29.36, 44.25) * mm, "end": v(29.36, 43.19) * mm});
            skLineSegment(sketch, "E913", {"start": v(29.36, 43.19) * mm, "end": v(28.85, 43.19) * mm});
            skCircle(sketch, "E914", {"center": v(0, 76.17) * mm, "radius": 0.5 * mm});
            skCircle(sketch, "E915", {"center": v(0, 60.12) * mm, "radius": 0.5 * mm});
            skCircle(sketch, "E916", {"center": v(0, 44.16) * mm, "radius": 0.5 * mm});
            skCircle(sketch, "E917", {"center": v(0, 28.14) * mm, "radius": 0.5 * mm});
            skCircle(sketch, "E918", {"center": v(52.07, 28.16) * mm, "radius": 0.5 * mm});
            skCircle(sketch, "E919", {"center": v(26.82, 10) * mm, "radius": 0.85 * mm});
            skCircle(sketch, "E920", {"center": v(26.84, 62.94) * mm, "radius": 0.85 * mm});
            skCircle(sketch, "E921", {"center": v(26.85, 38.91) * mm, "radius": 0.85 * mm});
            skCircle(sketch, "E922", {"center": v(26.85, 68.48) * mm, "radius": 0.85 * mm});
            skCircle(sketch, "E923", {"center": v(26.85, 33.77) * mm, "radius": 0.85 * mm});
            skCircle(sketch, "E924", {"center": v(0, 79.48) * mm, "radius": 0.6 * mm});
            skCircle(sketch, "E925", {"center": v(0, 73.14) * mm, "radius": 0.6 * mm});
            skCircle(sketch, "E926", {"center": v(0, 63.43) * mm, "radius": 0.6 * mm});
            skCircle(sketch, "E927", {"center": v(0, 57.08) * mm, "radius": 0.6 * mm});
            skPoint(sketch, "E928", {"position": v(3.17, 11.6) * mm});
            skPoint(sketch, "E929", {"position": v(26.03, 11.85) * mm});
            skLineSegment(sketch, "E930", {"start": v(3.17, 98.17) * mm, "end": v(3.17, 2.92) * mm});
            skPoint(sketch, "E931", {"position": v(3.17, 28.14) * mm});
            skPoint(sketch, "E932", {"position": v(3.17, 44.16) * mm});
            skPoint(sketch, "E933", {"position": v(3.17, 60.12) * mm});
            skPoint(sketch, "E934", {"position": v(3.17, 76.17) * mm});
            skPoint(sketch, "E935", {"position": v(48.9, 28.16) * mm});
            skPoint(sketch, "E936", {"position": v(48.9, 44.1) * mm});
            skPoint(sketch, "E937", {"position": v(48.9, 60.14) * mm});
            skPoint(sketch, "E938", {"position": v(48.9, 76.19) * mm});
            skPoint(sketch, "E939", {"position": v(3.17, 98.17) * mm});
            skSolve(sketch);
        }
        {
            var Q0;
            Q0=qCreatedBy(makeId("Top.planeOp"),FACE);
            var sketch = newSketch(context, id + "F3", { "sketchPlane" : qUnion([Q0])});
            skArc(sketch, "E940", {"start": v(26.16, 63.5) * mm, "mid": v(26.8, 62.86) * mm, "end": v(27.43, 63.5) * mm});
            skArc(sketch, "E941", {"start": v(27.43, 63.5) * mm, "mid": v(26.8, 64.13) * mm, "end": v(26.16, 63.5) * mm});
            skArc(sketch, "E942", {"start": v(5.7, 87.9) * mm, "mid": v(6.07, 87.52) * mm, "end": v(6.45, 87.9) * mm});
            skArc(sketch, "E943", {"start": v(6.45, 87.9) * mm, "mid": v(6.07, 88.28) * mm, "end": v(5.7, 87.9) * mm});
            skArc(sketch, "E944", {"start": v(45.85, 87.93) * mm, "mid": v(46.23, 87.55) * mm, "end": v(46.61, 87.93) * mm});
            skArc(sketch, "E945", {"start": v(46.61, 87.93) * mm, "mid": v(46.23, 88.3) * mm, "end": v(45.85, 87.93) * mm});
            skArc(sketch, "E946", {"start": v(5.1, 13.86) * mm, "mid": v(5.49, 13.48) * mm, "end": v(5.87, 13.86) * mm});
            skArc(sketch, "E947", {"start": v(5.87, 13.86) * mm, "mid": v(5.49, 14.24) * mm, "end": v(5.1, 13.86) * mm});
            skArc(sketch, "E948", {"start": v(46.28, 13.86) * mm, "mid": v(46.66, 13.48) * mm, "end": v(47.04, 13.86) * mm});
            skArc(sketch, "E949", {"start": v(47.04, 13.86) * mm, "mid": v(46.66, 14.24) * mm, "end": v(46.28, 13.86) * mm});
            skArc(sketch, "E950", {"start": v(41.35, 64.06) * mm, "mid": v(41.48, 63.93) * mm, "end": v(41.6, 64.06) * mm});
            skArc(sketch, "E951", {"start": v(41.6, 64.06) * mm, "mid": v(41.48, 64.18) * mm, "end": v(41.35, 64.06) * mm});
            skArc(sketch, "E952", {"start": v(41.35, 70.15) * mm, "mid": v(41.48, 70.03) * mm, "end": v(41.6, 70.15) * mm});
            skArc(sketch, "E953", {"start": v(41.6, 70.15) * mm, "mid": v(41.48, 70.28) * mm, "end": v(41.35, 70.15) * mm});
            skArc(sketch, "E954", {"start": v(41.35, 68.63) * mm, "mid": v(41.48, 68.5) * mm, "end": v(41.6, 68.63) * mm});
            skArc(sketch, "E955", {"start": v(41.6, 68.63) * mm, "mid": v(41.48, 68.76) * mm, "end": v(41.35, 68.63) * mm});
            skArc(sketch, "E956", {"start": v(41.35, 67.1) * mm, "mid": v(41.48, 66.98) * mm, "end": v(41.6, 67.1) * mm});
            skArc(sketch, "E957", {"start": v(41.6, 67.1) * mm, "mid": v(41.48, 67.23) * mm, "end": v(41.35, 67.1) * mm});
            skArc(sketch, "E958", {"start": v(41.35, 65.58) * mm, "mid": v(41.48, 65.45) * mm, "end": v(41.6, 65.58) * mm});
            skArc(sketch, "E959", {"start": v(41.6, 65.58) * mm, "mid": v(41.48, 65.7) * mm, "end": v(41.35, 65.58) * mm});
            skArc(sketch, "E960", {"start": v(41.35, 71.68) * mm, "mid": v(41.48, 71.55) * mm, "end": v(41.6, 71.68) * mm});
            skArc(sketch, "E961", {"start": v(41.6, 71.68) * mm, "mid": v(41.48, 71.8) * mm, "end": v(41.35, 71.68) * mm});
            skArc(sketch, "E962", {"start": v(41.35, 73.2) * mm, "mid": v(41.48, 73.07) * mm, "end": v(41.6, 73.2) * mm});
            skArc(sketch, "E963", {"start": v(41.6, 73.2) * mm, "mid": v(41.48, 73.33) * mm, "end": v(41.35, 73.2) * mm});
            skArc(sketch, "E964", {"start": v(41.35, 62.53) * mm, "mid": v(41.48, 62.4) * mm, "end": v(41.6, 62.53) * mm});
            skArc(sketch, "E965", {"start": v(41.6, 62.53) * mm, "mid": v(41.48, 62.66) * mm, "end": v(41.35, 62.53) * mm});
            skArc(sketch, "E966", {"start": v(46.94, 73.07) * mm, "mid": v(47.07, 72.94) * mm, "end": v(47.2, 73.07) * mm});
            skArc(sketch, "E967", {"start": v(47.2, 73.07) * mm, "mid": v(47.07, 73.2) * mm, "end": v(46.94, 73.07) * mm});
            skArc(sketch, "E968", {"start": v(46.94, 71.54) * mm, "mid": v(47.07, 71.42) * mm, "end": v(47.2, 71.54) * mm});
            skArc(sketch, "E969", {"start": v(47.2, 71.54) * mm, "mid": v(47.07, 71.67) * mm, "end": v(46.94, 71.54) * mm});
            skArc(sketch, "E970", {"start": v(46.94, 62.4) * mm, "mid": v(47.07, 62.27) * mm, "end": v(47.2, 62.4) * mm});
            skArc(sketch, "E971", {"start": v(47.2, 62.4) * mm, "mid": v(47.07, 62.53) * mm, "end": v(46.94, 62.4) * mm});
            skArc(sketch, "E972", {"start": v(46.94, 63.92) * mm, "mid": v(47.07, 63.8) * mm, "end": v(47.2, 63.92) * mm});
            skArc(sketch, "E973", {"start": v(47.2, 63.92) * mm, "mid": v(47.07, 64.05) * mm, "end": v(46.94, 63.92) * mm});
            skArc(sketch, "E974", {"start": v(46.94, 65.45) * mm, "mid": v(47.07, 65.32) * mm, "end": v(47.2, 65.45) * mm});
            skArc(sketch, "E975", {"start": v(47.2, 65.45) * mm, "mid": v(47.07, 65.58) * mm, "end": v(46.94, 65.45) * mm});
            skArc(sketch, "E976", {"start": v(46.94, 66.97) * mm, "mid": v(47.07, 66.85) * mm, "end": v(47.2, 66.97) * mm});
            skArc(sketch, "E977", {"start": v(47.2, 66.97) * mm, "mid": v(47.07, 67.1) * mm, "end": v(46.94, 66.97) * mm});
            skArc(sketch, "E978", {"start": v(46.94, 68.5) * mm, "mid": v(47.07, 68.37) * mm, "end": v(47.2, 68.5) * mm});
            skArc(sketch, "E979", {"start": v(47.2, 68.5) * mm, "mid": v(47.07, 68.62) * mm, "end": v(46.94, 68.5) * mm});
            skArc(sketch, "E980", {"start": v(46.94, 70.02) * mm, "mid": v(47.07, 69.9) * mm, "end": v(47.2, 70.02) * mm});
            skArc(sketch, "E981", {"start": v(47.2, 70.02) * mm, "mid": v(47.07, 70.15) * mm, "end": v(46.94, 70.02) * mm});
            skArc(sketch, "E982", {"start": v(41.48, 32.4) * mm, "mid": v(41.6, 32.28) * mm, "end": v(41.73, 32.4) * mm});
            skArc(sketch, "E983", {"start": v(41.73, 32.4) * mm, "mid": v(41.6, 32.53) * mm, "end": v(41.48, 32.4) * mm});
            skArc(sketch, "E984", {"start": v(41.48, 38.5) * mm, "mid": v(41.6, 38.38) * mm, "end": v(41.73, 38.5) * mm});
            skArc(sketch, "E985", {"start": v(41.73, 38.5) * mm, "mid": v(41.6, 38.63) * mm, "end": v(41.48, 38.5) * mm});
            skArc(sketch, "E986", {"start": v(41.48, 36.98) * mm, "mid": v(41.6, 36.85) * mm, "end": v(41.73, 36.98) * mm});
            skArc(sketch, "E987", {"start": v(41.73, 36.98) * mm, "mid": v(41.6, 37.1) * mm, "end": v(41.48, 36.98) * mm});
            skArc(sketch, "E988", {"start": v(41.48, 35.46) * mm, "mid": v(41.6, 35.33) * mm, "end": v(41.73, 35.46) * mm});
            skArc(sketch, "E989", {"start": v(41.73, 35.46) * mm, "mid": v(41.6, 35.58) * mm, "end": v(41.48, 35.46) * mm});
            skArc(sketch, "E990", {"start": v(41.48, 33.93) * mm, "mid": v(41.6, 33.8) * mm, "end": v(41.73, 33.93) * mm});
            skArc(sketch, "E991", {"start": v(41.73, 33.93) * mm, "mid": v(41.6, 34.06) * mm, "end": v(41.48, 33.93) * mm});
            skArc(sketch, "E992", {"start": v(41.48, 40.03) * mm, "mid": v(41.6, 39.9) * mm, "end": v(41.73, 40.03) * mm});
            skArc(sketch, "E993", {"start": v(41.73, 40.03) * mm, "mid": v(41.6, 40.15) * mm, "end": v(41.48, 40.03) * mm});
            skArc(sketch, "E994", {"start": v(41.48, 41.55) * mm, "mid": v(41.6, 41.42) * mm, "end": v(41.73, 41.55) * mm});
            skArc(sketch, "E995", {"start": v(41.73, 41.55) * mm, "mid": v(41.6, 41.68) * mm, "end": v(41.48, 41.55) * mm});
            skArc(sketch, "E996", {"start": v(41.48, 30.88) * mm, "mid": v(41.6, 30.76) * mm, "end": v(41.73, 30.88) * mm});
            skArc(sketch, "E997", {"start": v(41.73, 30.88) * mm, "mid": v(41.6, 31.01) * mm, "end": v(41.48, 30.88) * mm});
            skArc(sketch, "E998", {"start": v(47.07, 41.42) * mm, "mid": v(47.2, 41.3) * mm, "end": v(47.32, 41.42) * mm});
            skArc(sketch, "E999", {"start": v(47.32, 41.42) * mm, "mid": v(47.2, 41.55) * mm, "end": v(47.07, 41.42) * mm});
            skArc(sketch, "E1000", {"start": v(47.07, 39.9) * mm, "mid": v(47.2, 39.77) * mm, "end": v(47.32, 39.9) * mm});
            skArc(sketch, "E1001", {"start": v(47.32, 39.9) * mm, "mid": v(47.2, 40.02) * mm, "end": v(47.07, 39.9) * mm});
            skArc(sketch, "E1002", {"start": v(47.07, 30.75) * mm, "mid": v(47.2, 30.62) * mm, "end": v(47.32, 30.75) * mm});
            skArc(sketch, "E1003", {"start": v(47.32, 30.75) * mm, "mid": v(47.2, 30.88) * mm, "end": v(47.07, 30.75) * mm});
            skArc(sketch, "E1004", {"start": v(47.07, 32.28) * mm, "mid": v(47.2, 32.15) * mm, "end": v(47.32, 32.28) * mm});
            skArc(sketch, "E1005", {"start": v(47.32, 32.28) * mm, "mid": v(47.2, 32.4) * mm, "end": v(47.07, 32.28) * mm});
            skArc(sketch, "E1006", {"start": v(47.07, 33.8) * mm, "mid": v(47.2, 33.67) * mm, "end": v(47.32, 33.8) * mm});
            skArc(sketch, "E1007", {"start": v(47.32, 33.8) * mm, "mid": v(47.2, 33.93) * mm, "end": v(47.07, 33.8) * mm});
            skArc(sketch, "E1008", {"start": v(47.07, 35.32) * mm, "mid": v(47.2, 35.2) * mm, "end": v(47.32, 35.32) * mm});
            skArc(sketch, "E1009", {"start": v(47.32, 35.32) * mm, "mid": v(47.2, 35.45) * mm, "end": v(47.07, 35.32) * mm});
            skArc(sketch, "E1010", {"start": v(47.07, 36.85) * mm, "mid": v(47.2, 36.72) * mm, "end": v(47.32, 36.85) * mm});
            skArc(sketch, "E1011", {"start": v(47.32, 36.85) * mm, "mid": v(47.2, 36.97) * mm, "end": v(47.07, 36.85) * mm});
            skArc(sketch, "E1012", {"start": v(47.07, 38.37) * mm, "mid": v(47.2, 38.24) * mm, "end": v(47.32, 38.37) * mm});
            skArc(sketch, "E1013", {"start": v(47.32, 38.37) * mm, "mid": v(47.2, 38.5) * mm, "end": v(47.07, 38.37) * mm});
            skArc(sketch, "E1014", {"start": v(4.35, 31.85) * mm, "mid": v(4.47, 31.72) * mm, "end": v(4.6, 31.85) * mm});
            skArc(sketch, "E1015", {"start": v(4.6, 31.85) * mm, "mid": v(4.47, 31.98) * mm, "end": v(4.35, 31.85) * mm});
            skArc(sketch, "E1016", {"start": v(4.35, 37.95) * mm, "mid": v(4.47, 37.82) * mm, "end": v(4.6, 37.95) * mm});
            skArc(sketch, "E1017", {"start": v(4.6, 37.95) * mm, "mid": v(4.47, 38.07) * mm, "end": v(4.35, 37.95) * mm});
            skArc(sketch, "E1018", {"start": v(4.35, 36.42) * mm, "mid": v(4.47, 36.3) * mm, "end": v(4.6, 36.42) * mm});
            skArc(sketch, "E1019", {"start": v(4.6, 36.42) * mm, "mid": v(4.47, 36.55) * mm, "end": v(4.35, 36.42) * mm});
            skArc(sketch, "E1020", {"start": v(4.35, 34.9) * mm, "mid": v(4.47, 34.77) * mm, "end": v(4.6, 34.9) * mm});
            skArc(sketch, "E1021", {"start": v(4.6, 34.9) * mm, "mid": v(4.47, 35.02) * mm, "end": v(4.35, 34.9) * mm});
            skArc(sketch, "E1022", {"start": v(4.35, 33.37) * mm, "mid": v(4.47, 33.25) * mm, "end": v(4.6, 33.37) * mm});
            skArc(sketch, "E1023", {"start": v(4.6, 33.37) * mm, "mid": v(4.47, 33.5) * mm, "end": v(4.35, 33.37) * mm});
            skArc(sketch, "E1024", {"start": v(4.35, 39.47) * mm, "mid": v(4.47, 39.34) * mm, "end": v(4.6, 39.47) * mm});
            skArc(sketch, "E1025", {"start": v(4.6, 39.47) * mm, "mid": v(4.47, 39.6) * mm, "end": v(4.35, 39.47) * mm});
            skArc(sketch, "E1026", {"start": v(4.35, 41) * mm, "mid": v(4.47, 40.87) * mm, "end": v(4.6, 41) * mm});
            skArc(sketch, "E1027", {"start": v(4.6, 41) * mm, "mid": v(4.47, 41.12) * mm, "end": v(4.35, 41) * mm});
            skArc(sketch, "E1028", {"start": v(4.35, 30.33) * mm, "mid": v(4.47, 30.2) * mm, "end": v(4.6, 30.33) * mm});
            skArc(sketch, "E1029", {"start": v(4.6, 30.33) * mm, "mid": v(4.47, 30.45) * mm, "end": v(4.35, 30.33) * mm});
            skArc(sketch, "E1030", {"start": v(9.93, 40.86) * mm, "mid": v(10.06, 40.73) * mm, "end": v(10.19, 40.86) * mm});
            skArc(sketch, "E1031", {"start": v(10.19, 40.86) * mm, "mid": v(10.06, 40.99) * mm, "end": v(9.93, 40.86) * mm});
            skArc(sketch, "E1032", {"start": v(9.93, 39.34) * mm, "mid": v(10.06, 39.2) * mm, "end": v(10.19, 39.34) * mm});
            skArc(sketch, "E1033", {"start": v(10.19, 39.34) * mm, "mid": v(10.06, 39.46) * mm, "end": v(9.93, 39.34) * mm});
            skArc(sketch, "E1034", {"start": v(9.88, 65.88) * mm, "mid": v(10.01, 65.75) * mm, "end": v(10.14, 65.88) * mm});
            skArc(sketch, "E1035", {"start": v(10.14, 65.88) * mm, "mid": v(10.01, 66) * mm, "end": v(9.88, 65.88) * mm});
            skArc(sketch, "E1036", {"start": v(9.88, 64.36) * mm, "mid": v(10.01, 64.23) * mm, "end": v(10.14, 64.36) * mm});
            skArc(sketch, "E1037", {"start": v(10.14, 64.36) * mm, "mid": v(10.01, 64.48) * mm, "end": v(9.88, 64.36) * mm});
            skArc(sketch, "E1038", {"start": v(9.88, 62.83) * mm, "mid": v(10.01, 62.7) * mm, "end": v(10.14, 62.83) * mm});
            skArc(sketch, "E1039", {"start": v(10.14, 62.83) * mm, "mid": v(10.01, 62.96) * mm, "end": v(9.88, 62.83) * mm});
            skArc(sketch, "E1040", {"start": v(9.88, 71.98) * mm, "mid": v(10.01, 71.85) * mm, "end": v(10.14, 71.98) * mm});
            skArc(sketch, "E1041", {"start": v(10.14, 71.98) * mm, "mid": v(10.01, 72.1) * mm, "end": v(9.88, 71.98) * mm});
            skArc(sketch, "E1042", {"start": v(9.88, 73.5) * mm, "mid": v(10.01, 73.37) * mm, "end": v(10.14, 73.5) * mm});
            skArc(sketch, "E1043", {"start": v(10.14, 73.5) * mm, "mid": v(10.01, 73.63) * mm, "end": v(9.88, 73.5) * mm});
            skArc(sketch, "E1044", {"start": v(9.93, 37.81) * mm, "mid": v(10.06, 37.69) * mm, "end": v(10.19, 37.81) * mm});
            skArc(sketch, "E1045", {"start": v(10.19, 37.81) * mm, "mid": v(10.06, 37.94) * mm, "end": v(9.93, 37.81) * mm});
            skArc(sketch, "E1046", {"start": v(9.93, 36.29) * mm, "mid": v(10.06, 36.16) * mm, "end": v(10.19, 36.29) * mm});
            skArc(sketch, "E1047", {"start": v(10.19, 36.29) * mm, "mid": v(10.06, 36.42) * mm, "end": v(9.93, 36.29) * mm});
            skArc(sketch, "E1048", {"start": v(9.93, 34.76) * mm, "mid": v(10.06, 34.64) * mm, "end": v(10.19, 34.76) * mm});
            skArc(sketch, "E1049", {"start": v(10.19, 34.76) * mm, "mid": v(10.06, 34.9) * mm, "end": v(9.93, 34.76) * mm});
            skArc(sketch, "E1050", {"start": v(9.93, 33.24) * mm, "mid": v(10.06, 33.11) * mm, "end": v(10.19, 33.24) * mm});
            skArc(sketch, "E1051", {"start": v(10.19, 33.24) * mm, "mid": v(10.06, 33.37) * mm, "end": v(9.93, 33.24) * mm});
            skArc(sketch, "E1052", {"start": v(9.93, 31.72) * mm, "mid": v(10.06, 31.59) * mm, "end": v(10.19, 31.72) * mm});
            skArc(sketch, "E1053", {"start": v(10.19, 31.72) * mm, "mid": v(10.06, 31.84) * mm, "end": v(9.93, 31.72) * mm});
            skArc(sketch, "E1054", {"start": v(9.93, 30.2) * mm, "mid": v(10.06, 30.07) * mm, "end": v(10.19, 30.2) * mm});
            skArc(sketch, "E1055", {"start": v(10.19, 30.2) * mm, "mid": v(10.06, 30.32) * mm, "end": v(9.93, 30.2) * mm});
            skArc(sketch, "E1056", {"start": v(4.3, 70.58) * mm, "mid": v(4.42, 70.46) * mm, "end": v(4.55, 70.58) * mm});
            skArc(sketch, "E1057", {"start": v(4.55, 70.58) * mm, "mid": v(4.42, 70.71) * mm, "end": v(4.3, 70.58) * mm});
            skArc(sketch, "E1058", {"start": v(4.3, 69.06) * mm, "mid": v(4.42, 68.93) * mm, "end": v(4.55, 69.06) * mm});
            skArc(sketch, "E1059", {"start": v(4.55, 69.06) * mm, "mid": v(4.42, 69.19) * mm, "end": v(4.3, 69.06) * mm});
            skArc(sketch, "E1060", {"start": v(4.3, 67.54) * mm, "mid": v(4.42, 67.4) * mm, "end": v(4.55, 67.54) * mm});
            skArc(sketch, "E1061", {"start": v(4.55, 67.54) * mm, "mid": v(4.42, 67.66) * mm, "end": v(4.3, 67.54) * mm});
            skArc(sketch, "E1062", {"start": v(4.3, 66.01) * mm, "mid": v(4.42, 65.89) * mm, "end": v(4.55, 66.01) * mm});
            skArc(sketch, "E1063", {"start": v(4.55, 66.01) * mm, "mid": v(4.42, 66.14) * mm, "end": v(4.3, 66.01) * mm});
            skArc(sketch, "E1064", {"start": v(4.3, 64.49) * mm, "mid": v(4.42, 64.36) * mm, "end": v(4.55, 64.49) * mm});
            skArc(sketch, "E1065", {"start": v(4.55, 64.49) * mm, "mid": v(4.42, 64.62) * mm, "end": v(4.3, 64.49) * mm});
            skArc(sketch, "E1066", {"start": v(4.3, 62.96) * mm, "mid": v(4.42, 62.84) * mm, "end": v(4.55, 62.96) * mm});
            skArc(sketch, "E1067", {"start": v(4.55, 62.96) * mm, "mid": v(4.42, 63.1) * mm, "end": v(4.3, 62.96) * mm});
            skArc(sketch, "E1068", {"start": v(9.88, 67.4) * mm, "mid": v(10.01, 67.28) * mm, "end": v(10.14, 67.4) * mm});
            skArc(sketch, "E1069", {"start": v(10.14, 67.4) * mm, "mid": v(10.01, 67.53) * mm, "end": v(9.88, 67.4) * mm});
            skArc(sketch, "E1070", {"start": v(9.88, 68.93) * mm, "mid": v(10.01, 68.8) * mm, "end": v(10.14, 68.93) * mm});
            skArc(sketch, "E1071", {"start": v(10.14, 68.93) * mm, "mid": v(10.01, 69.05) * mm, "end": v(9.88, 68.93) * mm});
            skArc(sketch, "E1072", {"start": v(9.88, 70.45) * mm, "mid": v(10.01, 70.32) * mm, "end": v(10.14, 70.45) * mm});
            skArc(sketch, "E1073", {"start": v(10.14, 70.45) * mm, "mid": v(10.01, 70.58) * mm, "end": v(9.88, 70.45) * mm});
            skArc(sketch, "E1074", {"start": v(4.3, 72.1) * mm, "mid": v(4.42, 71.98) * mm, "end": v(4.55, 72.1) * mm});
            skArc(sketch, "E1075", {"start": v(4.55, 72.1) * mm, "mid": v(4.42, 72.24) * mm, "end": v(4.3, 72.1) * mm});
            skArc(sketch, "E1076", {"start": v(4.3, 73.63) * mm, "mid": v(4.42, 73.5) * mm, "end": v(4.55, 73.63) * mm});
            skArc(sketch, "E1077", {"start": v(4.55, 73.63) * mm, "mid": v(4.42, 73.76) * mm, "end": v(4.3, 73.63) * mm});
            skArc(sketch, "E1078", {"start": v(6.74, 80.18) * mm, "mid": v(6.87, 80.05) * mm, "end": v(7, 80.18) * mm});
            skArc(sketch, "E1079", {"start": v(7, 80.18) * mm, "mid": v(6.87, 80.3) * mm, "end": v(6.74, 80.18) * mm});
            skArc(sketch, "E1080", {"start": v(11.32, 80.18) * mm, "mid": v(11.44, 80.05) * mm, "end": v(11.57, 80.18) * mm});
            skArc(sketch, "E1081", {"start": v(11.57, 80.18) * mm, "mid": v(11.44, 80.3) * mm, "end": v(11.32, 80.18) * mm});
            skArc(sketch, "E1082", {"start": v(23.5, 80.18) * mm, "mid": v(23.63, 80.05) * mm, "end": v(23.76, 80.18) * mm});
            skArc(sketch, "E1083", {"start": v(23.76, 80.18) * mm, "mid": v(23.63, 80.3) * mm, "end": v(23.5, 80.18) * mm});
            skArc(sketch, "E1084", {"start": v(46.37, 80.18) * mm, "mid": v(46.5, 80.05) * mm, "end": v(46.62, 80.18) * mm});
            skArc(sketch, "E1085", {"start": v(46.62, 80.18) * mm, "mid": v(46.5, 80.3) * mm, "end": v(46.37, 80.18) * mm});
            skArc(sketch, "E1086", {"start": v(47.9, 80.18) * mm, "mid": v(48.02, 80.05) * mm, "end": v(48.15, 80.18) * mm});
            skArc(sketch, "E1087", {"start": v(48.15, 80.18) * mm, "mid": v(48.02, 80.3) * mm, "end": v(47.9, 80.18) * mm});
            skArc(sketch, "E1088", {"start": v(41.8, 80.18) * mm, "mid": v(41.92, 80.05) * mm, "end": v(42.05, 80.18) * mm});
            skArc(sketch, "E1089", {"start": v(42.05, 80.18) * mm, "mid": v(41.92, 80.3) * mm, "end": v(41.8, 80.18) * mm});
            skArc(sketch, "E1090", {"start": v(43.32, 80.18) * mm, "mid": v(43.45, 80.05) * mm, "end": v(43.57, 80.18) * mm});
            skArc(sketch, "E1091", {"start": v(43.57, 80.18) * mm, "mid": v(43.45, 80.3) * mm, "end": v(43.32, 80.18) * mm});
            skArc(sketch, "E1092", {"start": v(44.84, 80.18) * mm, "mid": v(44.97, 80.05) * mm, "end": v(45.1, 80.18) * mm});
            skArc(sketch, "E1093", {"start": v(45.1, 80.18) * mm, "mid": v(44.97, 80.3) * mm, "end": v(44.84, 80.18) * mm});
            skArc(sketch, "E1094", {"start": v(37.22, 80.18) * mm, "mid": v(37.35, 80.05) * mm, "end": v(37.48, 80.18) * mm});
            skArc(sketch, "E1095", {"start": v(37.48, 80.18) * mm, "mid": v(37.35, 80.3) * mm, "end": v(37.22, 80.18) * mm});
            skArc(sketch, "E1096", {"start": v(38.75, 80.18) * mm, "mid": v(38.87, 80.05) * mm, "end": v(39, 80.18) * mm});
            skArc(sketch, "E1097", {"start": v(39, 80.18) * mm, "mid": v(38.87, 80.3) * mm, "end": v(38.75, 80.18) * mm});
            skArc(sketch, "E1098", {"start": v(40.27, 80.18) * mm, "mid": v(40.4, 80.05) * mm, "end": v(40.53, 80.18) * mm});
            skArc(sketch, "E1099", {"start": v(40.53, 80.18) * mm, "mid": v(40.4, 80.3) * mm, "end": v(40.27, 80.18) * mm});
            skArc(sketch, "E1100", {"start": v(35.7, 80.18) * mm, "mid": v(35.83, 80.05) * mm, "end": v(35.95, 80.18) * mm});
            skArc(sketch, "E1101", {"start": v(35.95, 80.18) * mm, "mid": v(35.83, 80.3) * mm, "end": v(35.7, 80.18) * mm});
            skArc(sketch, "E1102", {"start": v(34.18, 80.18) * mm, "mid": v(34.3, 80.05) * mm, "end": v(34.43, 80.18) * mm});
            skArc(sketch, "E1103", {"start": v(34.43, 80.18) * mm, "mid": v(34.3, 80.3) * mm, "end": v(34.18, 80.18) * mm});
            skArc(sketch, "E1104", {"start": v(32.65, 80.18) * mm, "mid": v(32.78, 80.05) * mm, "end": v(32.9, 80.18) * mm});
            skArc(sketch, "E1105", {"start": v(32.9, 80.18) * mm, "mid": v(32.78, 80.3) * mm, "end": v(32.65, 80.18) * mm});
            skArc(sketch, "E1106", {"start": v(28.08, 80.18) * mm, "mid": v(28.2, 80.05) * mm, "end": v(28.33, 80.18) * mm});
            skArc(sketch, "E1107", {"start": v(28.33, 80.18) * mm, "mid": v(28.2, 80.3) * mm, "end": v(28.08, 80.18) * mm});
            skArc(sketch, "E1108", {"start": v(31.13, 80.18) * mm, "mid": v(31.25, 80.05) * mm, "end": v(31.38, 80.18) * mm});
            skArc(sketch, "E1109", {"start": v(31.38, 80.18) * mm, "mid": v(31.25, 80.3) * mm, "end": v(31.13, 80.18) * mm});
            skArc(sketch, "E1110", {"start": v(29.6, 80.18) * mm, "mid": v(29.73, 80.05) * mm, "end": v(29.86, 80.18) * mm});
            skArc(sketch, "E1111", {"start": v(29.86, 80.18) * mm, "mid": v(29.73, 80.3) * mm, "end": v(29.6, 80.18) * mm});
            skArc(sketch, "E1112", {"start": v(6.64, 24.7) * mm, "mid": v(6.77, 24.58) * mm, "end": v(6.9, 24.7) * mm});
            skArc(sketch, "E1113", {"start": v(6.9, 24.7) * mm, "mid": v(6.77, 24.83) * mm, "end": v(6.64, 24.7) * mm});
            skArc(sketch, "E1114", {"start": v(11.21, 24.7) * mm, "mid": v(11.34, 24.58) * mm, "end": v(11.47, 24.7) * mm});
            skArc(sketch, "E1115", {"start": v(11.47, 24.7) * mm, "mid": v(11.34, 24.83) * mm, "end": v(11.21, 24.7) * mm});
            skArc(sketch, "E1116", {"start": v(23.4, 24.7) * mm, "mid": v(23.53, 24.58) * mm, "end": v(23.66, 24.7) * mm});
            skArc(sketch, "E1117", {"start": v(23.66, 24.7) * mm, "mid": v(23.53, 24.83) * mm, "end": v(23.4, 24.7) * mm});
            skArc(sketch, "E1118", {"start": v(46.27, 24.7) * mm, "mid": v(46.4, 24.58) * mm, "end": v(46.52, 24.7) * mm});
            skArc(sketch, "E1119", {"start": v(46.52, 24.7) * mm, "mid": v(46.4, 24.83) * mm, "end": v(46.27, 24.7) * mm});
            skArc(sketch, "E1120", {"start": v(47.8, 24.7) * mm, "mid": v(47.92, 24.58) * mm, "end": v(48.04, 24.7) * mm});
            skArc(sketch, "E1121", {"start": v(48.04, 24.7) * mm, "mid": v(47.92, 24.83) * mm, "end": v(47.8, 24.7) * mm});
            skArc(sketch, "E1122", {"start": v(41.7, 24.7) * mm, "mid": v(41.82, 24.58) * mm, "end": v(41.95, 24.7) * mm});
            skArc(sketch, "E1123", {"start": v(41.95, 24.7) * mm, "mid": v(41.82, 24.83) * mm, "end": v(41.7, 24.7) * mm});
            skArc(sketch, "E1124", {"start": v(43.22, 24.7) * mm, "mid": v(43.35, 24.58) * mm, "end": v(43.47, 24.7) * mm});
            skArc(sketch, "E1125", {"start": v(43.47, 24.7) * mm, "mid": v(43.35, 24.83) * mm, "end": v(43.22, 24.7) * mm});
            skArc(sketch, "E1126", {"start": v(44.74, 24.7) * mm, "mid": v(44.87, 24.58) * mm, "end": v(45, 24.7) * mm});
            skArc(sketch, "E1127", {"start": v(45, 24.7) * mm, "mid": v(44.87, 24.83) * mm, "end": v(44.74, 24.7) * mm});
            skArc(sketch, "E1128", {"start": v(37.12, 24.7) * mm, "mid": v(37.25, 24.58) * mm, "end": v(37.38, 24.7) * mm});
            skArc(sketch, "E1129", {"start": v(37.38, 24.7) * mm, "mid": v(37.25, 24.83) * mm, "end": v(37.12, 24.7) * mm});
            skArc(sketch, "E1130", {"start": v(38.65, 24.7) * mm, "mid": v(38.77, 24.58) * mm, "end": v(38.9, 24.7) * mm});
            skArc(sketch, "E1131", {"start": v(38.9, 24.7) * mm, "mid": v(38.77, 24.83) * mm, "end": v(38.65, 24.7) * mm});
            skArc(sketch, "E1132", {"start": v(40.17, 24.7) * mm, "mid": v(40.3, 24.58) * mm, "end": v(40.42, 24.7) * mm});
            skArc(sketch, "E1133", {"start": v(40.42, 24.7) * mm, "mid": v(40.3, 24.83) * mm, "end": v(40.17, 24.7) * mm});
            skArc(sketch, "E1134", {"start": v(35.6, 24.7) * mm, "mid": v(35.73, 24.58) * mm, "end": v(35.85, 24.7) * mm});
            skArc(sketch, "E1135", {"start": v(35.85, 24.7) * mm, "mid": v(35.73, 24.83) * mm, "end": v(35.6, 24.7) * mm});
            skArc(sketch, "E1136", {"start": v(34.07, 24.7) * mm, "mid": v(34.2, 24.58) * mm, "end": v(34.33, 24.7) * mm});
            skArc(sketch, "E1137", {"start": v(34.33, 24.7) * mm, "mid": v(34.2, 24.83) * mm, "end": v(34.07, 24.7) * mm});
            skArc(sketch, "E1138", {"start": v(32.55, 24.7) * mm, "mid": v(32.68, 24.58) * mm, "end": v(32.8, 24.7) * mm});
            skArc(sketch, "E1139", {"start": v(32.8, 24.7) * mm, "mid": v(32.68, 24.83) * mm, "end": v(32.55, 24.7) * mm});
            skArc(sketch, "E1140", {"start": v(27.98, 24.7) * mm, "mid": v(28.1, 24.58) * mm, "end": v(28.23, 24.7) * mm});
            skArc(sketch, "E1141", {"start": v(28.23, 24.7) * mm, "mid": v(28.1, 24.83) * mm, "end": v(27.98, 24.7) * mm});
            skArc(sketch, "E1142", {"start": v(31.03, 24.7) * mm, "mid": v(31.15, 24.58) * mm, "end": v(31.28, 24.7) * mm});
            skArc(sketch, "E1143", {"start": v(31.28, 24.7) * mm, "mid": v(31.15, 24.83) * mm, "end": v(31.03, 24.7) * mm});
            skArc(sketch, "E1144", {"start": v(29.5, 24.7) * mm, "mid": v(29.63, 24.58) * mm, "end": v(29.76, 24.7) * mm});
            skArc(sketch, "E1145", {"start": v(29.76, 24.7) * mm, "mid": v(29.63, 24.83) * mm, "end": v(29.5, 24.7) * mm});
            skArc(sketch, "E1146", {"start": v(26.45, 24.7) * mm, "mid": v(26.58, 24.58) * mm, "end": v(26.7, 24.7) * mm});
            skArc(sketch, "E1147", {"start": v(26.7, 24.7) * mm, "mid": v(26.58, 24.83) * mm, "end": v(26.45, 24.7) * mm});
            skArc(sketch, "E1148", {"start": v(24.93, 24.7) * mm, "mid": v(25.06, 24.58) * mm, "end": v(25.18, 24.7) * mm});
            skArc(sketch, "E1149", {"start": v(25.18, 24.7) * mm, "mid": v(25.06, 24.83) * mm, "end": v(24.93, 24.7) * mm});
            skArc(sketch, "E1150", {"start": v(21.88, 24.7) * mm, "mid": v(22, 24.58) * mm, "end": v(22.14, 24.7) * mm});
            skArc(sketch, "E1151", {"start": v(22.14, 24.7) * mm, "mid": v(22, 24.83) * mm, "end": v(21.88, 24.7) * mm});
            skArc(sketch, "E1152", {"start": v(20.36, 24.7) * mm, "mid": v(20.49, 24.58) * mm, "end": v(20.61, 24.7) * mm});
            skArc(sketch, "E1153", {"start": v(20.61, 24.7) * mm, "mid": v(20.49, 24.83) * mm, "end": v(20.36, 24.7) * mm});
            skArc(sketch, "E1154", {"start": v(18.83, 24.7) * mm, "mid": v(18.96, 24.58) * mm, "end": v(19.09, 24.7) * mm});
            skArc(sketch, "E1155", {"start": v(19.09, 24.7) * mm, "mid": v(18.96, 24.83) * mm, "end": v(18.83, 24.7) * mm});
            skArc(sketch, "E1156", {"start": v(17.31, 24.7) * mm, "mid": v(17.44, 24.58) * mm, "end": v(17.56, 24.7) * mm});
            skArc(sketch, "E1157", {"start": v(17.56, 24.7) * mm, "mid": v(17.44, 24.83) * mm, "end": v(17.31, 24.7) * mm});
            skArc(sketch, "E1158", {"start": v(15.79, 24.7) * mm, "mid": v(15.91, 24.58) * mm, "end": v(16.04, 24.7) * mm});
            skArc(sketch, "E1159", {"start": v(16.04, 24.7) * mm, "mid": v(15.91, 24.83) * mm, "end": v(15.79, 24.7) * mm});
            skArc(sketch, "E1160", {"start": v(12.74, 24.7) * mm, "mid": v(12.87, 24.58) * mm, "end": v(13, 24.7) * mm});
            skArc(sketch, "E1161", {"start": v(13, 24.7) * mm, "mid": v(12.87, 24.83) * mm, "end": v(12.74, 24.7) * mm});
            skArc(sketch, "E1162", {"start": v(14.26, 24.7) * mm, "mid": v(14.39, 24.58) * mm, "end": v(14.52, 24.7) * mm});
            skArc(sketch, "E1163", {"start": v(14.52, 24.7) * mm, "mid": v(14.39, 24.83) * mm, "end": v(14.26, 24.7) * mm});
            skArc(sketch, "E1164", {"start": v(9.7, 24.7) * mm, "mid": v(9.82, 24.58) * mm, "end": v(9.94, 24.7) * mm});
            skArc(sketch, "E1165", {"start": v(9.94, 24.7) * mm, "mid": v(9.82, 24.83) * mm, "end": v(9.7, 24.7) * mm});
            skArc(sketch, "E1166", {"start": v(8.17, 24.7) * mm, "mid": v(8.3, 24.58) * mm, "end": v(8.42, 24.7) * mm});
            skArc(sketch, "E1167", {"start": v(8.42, 24.7) * mm, "mid": v(8.3, 24.83) * mm, "end": v(8.17, 24.7) * mm});
            skArc(sketch, "E1168", {"start": v(5.12, 24.7) * mm, "mid": v(5.25, 24.58) * mm, "end": v(5.37, 24.7) * mm});
            skArc(sketch, "E1169", {"start": v(5.37, 24.7) * mm, "mid": v(5.25, 24.83) * mm, "end": v(5.12, 24.7) * mm});
            skArc(sketch, "E1170", {"start": v(3.58, 24.72) * mm, "mid": v(3.71, 24.6) * mm, "end": v(3.84, 24.72) * mm});
            skArc(sketch, "E1171", {"start": v(3.84, 24.72) * mm, "mid": v(3.71, 24.85) * mm, "end": v(3.58, 24.72) * mm});
            skArc(sketch, "E1172", {"start": v(33.99, 27.9) * mm, "mid": v(34.11, 27.78) * mm, "end": v(34.24, 27.9) * mm});
            skArc(sketch, "E1173", {"start": v(34.24, 27.9) * mm, "mid": v(34.11, 28.03) * mm, "end": v(33.99, 27.9) * mm});
            skArc(sketch, "E1174", {"start": v(35.51, 27.9) * mm, "mid": v(35.64, 27.78) * mm, "end": v(35.77, 27.9) * mm});
            skArc(sketch, "E1175", {"start": v(35.77, 27.9) * mm, "mid": v(35.64, 28.03) * mm, "end": v(35.51, 27.9) * mm});
            skArc(sketch, "E1176", {"start": v(32.46, 27.9) * mm, "mid": v(32.6, 27.78) * mm, "end": v(32.72, 27.9) * mm});
            skArc(sketch, "E1177", {"start": v(32.72, 27.9) * mm, "mid": v(32.6, 28.03) * mm, "end": v(32.46, 27.9) * mm});
            skArc(sketch, "E1178", {"start": v(30.94, 27.9) * mm, "mid": v(31.07, 27.78) * mm, "end": v(31.2, 27.9) * mm});
            skArc(sketch, "E1179", {"start": v(31.2, 27.9) * mm, "mid": v(31.07, 28.03) * mm, "end": v(30.94, 27.9) * mm});
            skArc(sketch, "E1180", {"start": v(29.42, 27.9) * mm, "mid": v(29.54, 27.78) * mm, "end": v(29.67, 27.9) * mm});
            skArc(sketch, "E1181", {"start": v(29.67, 27.9) * mm, "mid": v(29.54, 28.03) * mm, "end": v(29.42, 27.9) * mm});
            skArc(sketch, "E1182", {"start": v(27.9, 27.9) * mm, "mid": v(28.02, 27.78) * mm, "end": v(28.15, 27.9) * mm});
            skArc(sketch, "E1183", {"start": v(28.15, 27.9) * mm, "mid": v(28.02, 28.03) * mm, "end": v(27.9, 27.9) * mm});
            skArc(sketch, "E1184", {"start": v(26.37, 27.9) * mm, "mid": v(26.5, 27.78) * mm, "end": v(26.62, 27.9) * mm});
            skArc(sketch, "E1185", {"start": v(26.62, 27.9) * mm, "mid": v(26.5, 28.03) * mm, "end": v(26.37, 27.9) * mm});
            skArc(sketch, "E1186", {"start": v(24.84, 27.9) * mm, "mid": v(24.97, 27.78) * mm, "end": v(25.1, 27.9) * mm});
            skArc(sketch, "E1187", {"start": v(25.1, 27.9) * mm, "mid": v(24.97, 28.03) * mm, "end": v(24.84, 27.9) * mm});
            skArc(sketch, "E1188", {"start": v(23.32, 27.9) * mm, "mid": v(23.45, 27.78) * mm, "end": v(23.57, 27.9) * mm});
            skArc(sketch, "E1189", {"start": v(23.57, 27.9) * mm, "mid": v(23.45, 28.03) * mm, "end": v(23.32, 27.9) * mm});
            skArc(sketch, "E1190", {"start": v(21.8, 27.9) * mm, "mid": v(21.92, 27.78) * mm, "end": v(22.05, 27.9) * mm});
            skArc(sketch, "E1191", {"start": v(22.05, 27.9) * mm, "mid": v(21.92, 28.03) * mm, "end": v(21.8, 27.9) * mm});
            skArc(sketch, "E1192", {"start": v(20.27, 27.9) * mm, "mid": v(20.4, 27.78) * mm, "end": v(20.53, 27.9) * mm});
            skArc(sketch, "E1193", {"start": v(20.53, 27.9) * mm, "mid": v(20.4, 28.03) * mm, "end": v(20.27, 27.9) * mm});
            skArc(sketch, "E1194", {"start": v(18.75, 27.9) * mm, "mid": v(18.87, 27.78) * mm, "end": v(19, 27.9) * mm});
            skArc(sketch, "E1195", {"start": v(19, 27.9) * mm, "mid": v(18.87, 28.03) * mm, "end": v(18.75, 27.9) * mm});
            skArc(sketch, "E1196", {"start": v(17.22, 27.9) * mm, "mid": v(17.35, 27.78) * mm, "end": v(17.48, 27.9) * mm});
            skArc(sketch, "E1197", {"start": v(17.48, 27.9) * mm, "mid": v(17.35, 28.03) * mm, "end": v(17.22, 27.9) * mm});
            skArc(sketch, "E1198", {"start": v(34.06, 30.75) * mm, "mid": v(34.2, 30.62) * mm, "end": v(34.32, 30.75) * mm});
            skArc(sketch, "E1199", {"start": v(34.32, 30.75) * mm, "mid": v(34.2, 30.88) * mm, "end": v(34.06, 30.75) * mm});
            skArc(sketch, "E1200", {"start": v(35.59, 30.75) * mm, "mid": v(35.71, 30.62) * mm, "end": v(35.84, 30.75) * mm});
            skArc(sketch, "E1201", {"start": v(35.84, 30.75) * mm, "mid": v(35.71, 30.88) * mm, "end": v(35.59, 30.75) * mm});
            skArc(sketch, "E1202", {"start": v(32.54, 30.75) * mm, "mid": v(32.67, 30.62) * mm, "end": v(32.8, 30.75) * mm});
            skArc(sketch, "E1203", {"start": v(32.8, 30.75) * mm, "mid": v(32.67, 30.88) * mm, "end": v(32.54, 30.75) * mm});
            skArc(sketch, "E1204", {"start": v(31.02, 30.75) * mm, "mid": v(31.14, 30.62) * mm, "end": v(31.27, 30.75) * mm});
            skArc(sketch, "E1205", {"start": v(31.27, 30.75) * mm, "mid": v(31.14, 30.88) * mm, "end": v(31.02, 30.75) * mm});
            skArc(sketch, "E1206", {"start": v(29.5, 30.75) * mm, "mid": v(29.62, 30.62) * mm, "end": v(29.75, 30.75) * mm});
            skArc(sketch, "E1207", {"start": v(29.75, 30.75) * mm, "mid": v(29.62, 30.88) * mm, "end": v(29.5, 30.75) * mm});
            skArc(sketch, "E1208", {"start": v(27.97, 30.75) * mm, "mid": v(28.1, 30.62) * mm, "end": v(28.22, 30.75) * mm});
            skArc(sketch, "E1209", {"start": v(28.22, 30.75) * mm, "mid": v(28.1, 30.88) * mm, "end": v(27.97, 30.75) * mm});
            skArc(sketch, "E1210", {"start": v(26.44, 30.75) * mm, "mid": v(26.57, 30.62) * mm, "end": v(26.7, 30.75) * mm});
            skArc(sketch, "E1211", {"start": v(26.7, 30.75) * mm, "mid": v(26.57, 30.88) * mm, "end": v(26.44, 30.75) * mm});
            skArc(sketch, "E1212", {"start": v(24.92, 30.75) * mm, "mid": v(25.05, 30.62) * mm, "end": v(25.17, 30.75) * mm});
            skArc(sketch, "E1213", {"start": v(25.17, 30.75) * mm, "mid": v(25.05, 30.88) * mm, "end": v(24.92, 30.75) * mm});
            skArc(sketch, "E1214", {"start": v(23.4, 30.75) * mm, "mid": v(23.52, 30.62) * mm, "end": v(23.65, 30.75) * mm});
            skArc(sketch, "E1215", {"start": v(23.65, 30.75) * mm, "mid": v(23.52, 30.88) * mm, "end": v(23.4, 30.75) * mm});
            skArc(sketch, "E1216", {"start": v(21.87, 30.75) * mm, "mid": v(22, 30.62) * mm, "end": v(22.13, 30.75) * mm});
            skArc(sketch, "E1217", {"start": v(22.13, 30.75) * mm, "mid": v(22, 30.88) * mm, "end": v(21.87, 30.75) * mm});
            skArc(sketch, "E1218", {"start": v(20.35, 30.75) * mm, "mid": v(20.47, 30.62) * mm, "end": v(20.6, 30.75) * mm});
            skArc(sketch, "E1219", {"start": v(20.6, 30.75) * mm, "mid": v(20.47, 30.88) * mm, "end": v(20.35, 30.75) * mm});
            skArc(sketch, "E1220", {"start": v(18.82, 30.75) * mm, "mid": v(18.95, 30.62) * mm, "end": v(19.08, 30.75) * mm});
            skArc(sketch, "E1221", {"start": v(19.08, 30.75) * mm, "mid": v(18.95, 30.88) * mm, "end": v(18.82, 30.75) * mm});
            skArc(sketch, "E1222", {"start": v(17.3, 30.75) * mm, "mid": v(17.43, 30.62) * mm, "end": v(17.55, 30.75) * mm});
            skArc(sketch, "E1223", {"start": v(17.55, 30.75) * mm, "mid": v(17.43, 30.88) * mm, "end": v(17.3, 30.75) * mm});
            skArc(sketch, "E1224", {"start": v(34.17, 33.4) * mm, "mid": v(34.3, 33.27) * mm, "end": v(34.42, 33.4) * mm});
            skArc(sketch, "E1225", {"start": v(34.42, 33.4) * mm, "mid": v(34.3, 33.52) * mm, "end": v(34.17, 33.4) * mm});
            skArc(sketch, "E1226", {"start": v(35.69, 33.4) * mm, "mid": v(35.82, 33.27) * mm, "end": v(35.94, 33.4) * mm});
            skArc(sketch, "E1227", {"start": v(35.94, 33.4) * mm, "mid": v(35.82, 33.52) * mm, "end": v(35.69, 33.4) * mm});
            skArc(sketch, "E1228", {"start": v(32.64, 33.4) * mm, "mid": v(32.77, 33.27) * mm, "end": v(32.9, 33.4) * mm});
            skArc(sketch, "E1229", {"start": v(32.9, 33.4) * mm, "mid": v(32.77, 33.52) * mm, "end": v(32.64, 33.4) * mm});
            skArc(sketch, "E1230", {"start": v(31.12, 33.4) * mm, "mid": v(31.24, 33.27) * mm, "end": v(31.37, 33.4) * mm});
            skArc(sketch, "E1231", {"start": v(31.37, 33.4) * mm, "mid": v(31.24, 33.52) * mm, "end": v(31.12, 33.4) * mm});
            skArc(sketch, "E1232", {"start": v(29.6, 33.4) * mm, "mid": v(29.72, 33.27) * mm, "end": v(29.85, 33.4) * mm});
            skArc(sketch, "E1233", {"start": v(29.85, 33.4) * mm, "mid": v(29.72, 33.52) * mm, "end": v(29.6, 33.4) * mm});
            skArc(sketch, "E1234", {"start": v(28.07, 33.4) * mm, "mid": v(28.2, 33.27) * mm, "end": v(28.32, 33.4) * mm});
            skArc(sketch, "E1235", {"start": v(28.32, 33.4) * mm, "mid": v(28.2, 33.52) * mm, "end": v(28.07, 33.4) * mm});
            skArc(sketch, "E1236", {"start": v(26.55, 33.4) * mm, "mid": v(26.67, 33.27) * mm, "end": v(26.8, 33.4) * mm});
            skArc(sketch, "E1237", {"start": v(26.8, 33.4) * mm, "mid": v(26.67, 33.52) * mm, "end": v(26.55, 33.4) * mm});
            skArc(sketch, "E1238", {"start": v(25.02, 33.4) * mm, "mid": v(25.15, 33.27) * mm, "end": v(25.28, 33.4) * mm});
            skArc(sketch, "E1239", {"start": v(25.28, 33.4) * mm, "mid": v(25.15, 33.52) * mm, "end": v(25.02, 33.4) * mm});
            skArc(sketch, "E1240", {"start": v(23.5, 33.4) * mm, "mid": v(23.62, 33.27) * mm, "end": v(23.75, 33.4) * mm});
            skArc(sketch, "E1241", {"start": v(23.75, 33.4) * mm, "mid": v(23.62, 33.52) * mm, "end": v(23.5, 33.4) * mm});
            skArc(sketch, "E1242", {"start": v(21.97, 33.4) * mm, "mid": v(22.1, 33.27) * mm, "end": v(22.23, 33.4) * mm});
            skArc(sketch, "E1243", {"start": v(22.23, 33.4) * mm, "mid": v(22.1, 33.52) * mm, "end": v(21.97, 33.4) * mm});
            skArc(sketch, "E1244", {"start": v(20.45, 33.4) * mm, "mid": v(20.58, 33.27) * mm, "end": v(20.7, 33.4) * mm});
            skArc(sketch, "E1245", {"start": v(20.7, 33.4) * mm, "mid": v(20.58, 33.52) * mm, "end": v(20.45, 33.4) * mm});
            skArc(sketch, "E1246", {"start": v(18.93, 33.4) * mm, "mid": v(19.05, 33.27) * mm, "end": v(19.18, 33.4) * mm});
            skArc(sketch, "E1247", {"start": v(19.18, 33.4) * mm, "mid": v(19.05, 33.52) * mm, "end": v(18.93, 33.4) * mm});
            skArc(sketch, "E1248", {"start": v(17.4, 33.4) * mm, "mid": v(17.53, 33.27) * mm, "end": v(17.66, 33.4) * mm});
            skArc(sketch, "E1249", {"start": v(17.66, 33.4) * mm, "mid": v(17.53, 33.52) * mm, "end": v(17.4, 33.4) * mm});
            skArc(sketch, "E1250", {"start": v(34.17, 35.98) * mm, "mid": v(34.3, 35.86) * mm, "end": v(34.42, 35.98) * mm});
            skArc(sketch, "E1251", {"start": v(34.42, 35.98) * mm, "mid": v(34.3, 36.11) * mm, "end": v(34.17, 35.98) * mm});
            skArc(sketch, "E1252", {"start": v(35.69, 35.98) * mm, "mid": v(35.82, 35.86) * mm, "end": v(35.94, 35.98) * mm});
            skArc(sketch, "E1253", {"start": v(35.94, 35.98) * mm, "mid": v(35.82, 36.11) * mm, "end": v(35.69, 35.98) * mm});
            skArc(sketch, "E1254", {"start": v(32.64, 35.98) * mm, "mid": v(32.77, 35.86) * mm, "end": v(32.9, 35.98) * mm});
            skArc(sketch, "E1255", {"start": v(32.9, 35.98) * mm, "mid": v(32.77, 36.11) * mm, "end": v(32.64, 35.98) * mm});
            skArc(sketch, "E1256", {"start": v(31.12, 35.98) * mm, "mid": v(31.24, 35.86) * mm, "end": v(31.37, 35.98) * mm});
            skArc(sketch, "E1257", {"start": v(31.37, 35.98) * mm, "mid": v(31.24, 36.11) * mm, "end": v(31.12, 35.98) * mm});
            skArc(sketch, "E1258", {"start": v(29.6, 35.98) * mm, "mid": v(29.72, 35.86) * mm, "end": v(29.85, 35.98) * mm});
            skArc(sketch, "E1259", {"start": v(29.85, 35.98) * mm, "mid": v(29.72, 36.11) * mm, "end": v(29.6, 35.98) * mm});
            skArc(sketch, "E1260", {"start": v(28.07, 35.98) * mm, "mid": v(28.2, 35.86) * mm, "end": v(28.32, 35.98) * mm});
            skArc(sketch, "E1261", {"start": v(28.32, 35.98) * mm, "mid": v(28.2, 36.11) * mm, "end": v(28.07, 35.98) * mm});
            skArc(sketch, "E1262", {"start": v(26.55, 35.98) * mm, "mid": v(26.67, 35.86) * mm, "end": v(26.8, 35.98) * mm});
            skArc(sketch, "E1263", {"start": v(26.8, 35.98) * mm, "mid": v(26.67, 36.11) * mm, "end": v(26.55, 35.98) * mm});
            skArc(sketch, "E1264", {"start": v(25.02, 35.98) * mm, "mid": v(25.15, 35.86) * mm, "end": v(25.28, 35.98) * mm});
            skArc(sketch, "E1265", {"start": v(25.28, 35.98) * mm, "mid": v(25.15, 36.11) * mm, "end": v(25.02, 35.98) * mm});
            skArc(sketch, "E1266", {"start": v(23.5, 35.98) * mm, "mid": v(23.62, 35.86) * mm, "end": v(23.75, 35.98) * mm});
            skArc(sketch, "E1267", {"start": v(23.75, 35.98) * mm, "mid": v(23.62, 36.11) * mm, "end": v(23.5, 35.98) * mm});
            skArc(sketch, "E1268", {"start": v(21.97, 35.98) * mm, "mid": v(22.1, 35.86) * mm, "end": v(22.23, 35.98) * mm});
            skArc(sketch, "E1269", {"start": v(22.23, 35.98) * mm, "mid": v(22.1, 36.11) * mm, "end": v(21.97, 35.98) * mm});
            skArc(sketch, "E1270", {"start": v(20.45, 35.98) * mm, "mid": v(20.58, 35.86) * mm, "end": v(20.7, 35.98) * mm});
            skArc(sketch, "E1271", {"start": v(20.7, 35.98) * mm, "mid": v(20.58, 36.11) * mm, "end": v(20.45, 35.98) * mm});
            skArc(sketch, "E1272", {"start": v(18.93, 35.98) * mm, "mid": v(19.05, 35.86) * mm, "end": v(19.18, 35.98) * mm});
            skArc(sketch, "E1273", {"start": v(19.18, 35.98) * mm, "mid": v(19.05, 36.11) * mm, "end": v(18.93, 35.98) * mm});
            skArc(sketch, "E1274", {"start": v(17.4, 35.98) * mm, "mid": v(17.53, 35.86) * mm, "end": v(17.66, 35.98) * mm});
            skArc(sketch, "E1275", {"start": v(17.66, 35.98) * mm, "mid": v(17.53, 36.11) * mm, "end": v(17.4, 35.98) * mm});
            skArc(sketch, "E1276", {"start": v(8.27, 80.18) * mm, "mid": v(8.4, 80.05) * mm, "end": v(8.52, 80.18) * mm});
            skArc(sketch, "E1277", {"start": v(8.52, 80.18) * mm, "mid": v(8.4, 80.3) * mm, "end": v(8.27, 80.18) * mm});
            skArc(sketch, "E1278", {"start": v(5.22, 80.18) * mm, "mid": v(5.35, 80.05) * mm, "end": v(5.47, 80.18) * mm});
            skArc(sketch, "E1279", {"start": v(5.47, 80.18) * mm, "mid": v(5.35, 80.3) * mm, "end": v(5.22, 80.18) * mm});
            skArc(sketch, "E1280", {"start": v(3.69, 80.2) * mm, "mid": v(3.81, 80.07) * mm, "end": v(3.94, 80.2) * mm});
            skArc(sketch, "E1281", {"start": v(3.94, 80.2) * mm, "mid": v(3.81, 80.32) * mm, "end": v(3.69, 80.2) * mm});
            skArc(sketch, "E1282", {"start": v(26.56, 80.18) * mm, "mid": v(26.68, 80.05) * mm, "end": v(26.8, 80.18) * mm});
            skArc(sketch, "E1283", {"start": v(26.8, 80.18) * mm, "mid": v(26.68, 80.3) * mm, "end": v(26.56, 80.18) * mm});
            skArc(sketch, "E1284", {"start": v(25.03, 80.18) * mm, "mid": v(25.16, 80.05) * mm, "end": v(25.29, 80.18) * mm});
            skArc(sketch, "E1285", {"start": v(25.29, 80.18) * mm, "mid": v(25.16, 80.3) * mm, "end": v(25.03, 80.18) * mm});
            skArc(sketch, "E1286", {"start": v(21.98, 80.18) * mm, "mid": v(22.11, 80.05) * mm, "end": v(22.24, 80.18) * mm});
            skArc(sketch, "E1287", {"start": v(22.24, 80.18) * mm, "mid": v(22.11, 80.3) * mm, "end": v(21.98, 80.18) * mm});
            skArc(sketch, "E1288", {"start": v(20.46, 80.18) * mm, "mid": v(20.59, 80.05) * mm, "end": v(20.71, 80.18) * mm});
            skArc(sketch, "E1289", {"start": v(20.71, 80.18) * mm, "mid": v(20.59, 80.3) * mm, "end": v(20.46, 80.18) * mm});
            skArc(sketch, "E1290", {"start": v(18.94, 80.18) * mm, "mid": v(19.06, 80.05) * mm, "end": v(19.19, 80.18) * mm});
            skArc(sketch, "E1291", {"start": v(19.19, 80.18) * mm, "mid": v(19.06, 80.3) * mm, "end": v(18.94, 80.18) * mm});
            skArc(sketch, "E1292", {"start": v(17.41, 80.18) * mm, "mid": v(17.54, 80.05) * mm, "end": v(17.67, 80.18) * mm});
            skArc(sketch, "E1293", {"start": v(17.67, 80.18) * mm, "mid": v(17.54, 80.3) * mm, "end": v(17.41, 80.18) * mm});
            skArc(sketch, "E1294", {"start": v(15.89, 80.18) * mm, "mid": v(16.01, 80.05) * mm, "end": v(16.14, 80.18) * mm});
            skArc(sketch, "E1295", {"start": v(16.14, 80.18) * mm, "mid": v(16.01, 80.3) * mm, "end": v(15.89, 80.18) * mm});
            skArc(sketch, "E1296", {"start": v(12.84, 80.18) * mm, "mid": v(12.97, 80.05) * mm, "end": v(13.1, 80.18) * mm});
            skArc(sketch, "E1297", {"start": v(13.1, 80.18) * mm, "mid": v(12.97, 80.3) * mm, "end": v(12.84, 80.18) * mm});
            skArc(sketch, "E1298", {"start": v(14.36, 80.18) * mm, "mid": v(14.5, 80.05) * mm, "end": v(14.62, 80.18) * mm});
            skArc(sketch, "E1299", {"start": v(14.62, 80.18) * mm, "mid": v(14.5, 80.3) * mm, "end": v(14.36, 80.18) * mm});
            skArc(sketch, "E1300", {"start": v(9.8, 80.18) * mm, "mid": v(9.92, 80.05) * mm, "end": v(10.05, 80.18) * mm});
            skArc(sketch, "E1301", {"start": v(10.05, 80.18) * mm, "mid": v(9.92, 80.3) * mm, "end": v(9.8, 80.18) * mm});
            skArc(sketch, "E1302", {"start": v(33.89, 76.14) * mm, "mid": v(34.01, 76.01) * mm, "end": v(34.14, 76.14) * mm});
            skArc(sketch, "E1303", {"start": v(34.14, 76.14) * mm, "mid": v(34.01, 76.27) * mm, "end": v(33.89, 76.14) * mm});
            skArc(sketch, "E1304", {"start": v(35.41, 76.14) * mm, "mid": v(35.54, 76.01) * mm, "end": v(35.66, 76.14) * mm});
            skArc(sketch, "E1305", {"start": v(35.66, 76.14) * mm, "mid": v(35.54, 76.27) * mm, "end": v(35.41, 76.14) * mm});
            skArc(sketch, "E1306", {"start": v(32.36, 76.14) * mm, "mid": v(32.49, 76.01) * mm, "end": v(32.62, 76.14) * mm});
            skArc(sketch, "E1307", {"start": v(32.62, 76.14) * mm, "mid": v(32.49, 76.27) * mm, "end": v(32.36, 76.14) * mm});
            skArc(sketch, "E1308", {"start": v(30.84, 76.14) * mm, "mid": v(30.97, 76.01) * mm, "end": v(31.1, 76.14) * mm});
            skArc(sketch, "E1309", {"start": v(31.1, 76.14) * mm, "mid": v(30.97, 76.27) * mm, "end": v(30.84, 76.14) * mm});
            skArc(sketch, "E1310", {"start": v(29.31, 76.14) * mm, "mid": v(29.44, 76.01) * mm, "end": v(29.57, 76.14) * mm});
            skArc(sketch, "E1311", {"start": v(29.57, 76.14) * mm, "mid": v(29.44, 76.27) * mm, "end": v(29.31, 76.14) * mm});
            skArc(sketch, "E1312", {"start": v(27.8, 76.14) * mm, "mid": v(27.92, 76.01) * mm, "end": v(28.04, 76.14) * mm});
            skArc(sketch, "E1313", {"start": v(28.04, 76.14) * mm, "mid": v(27.92, 76.27) * mm, "end": v(27.8, 76.14) * mm});
            skArc(sketch, "E1314", {"start": v(26.27, 76.14) * mm, "mid": v(26.4, 76.01) * mm, "end": v(26.52, 76.14) * mm});
            skArc(sketch, "E1315", {"start": v(26.52, 76.14) * mm, "mid": v(26.4, 76.27) * mm, "end": v(26.27, 76.14) * mm});
            skArc(sketch, "E1316", {"start": v(24.74, 76.14) * mm, "mid": v(24.87, 76.01) * mm, "end": v(25, 76.14) * mm});
            skArc(sketch, "E1317", {"start": v(25, 76.14) * mm, "mid": v(24.87, 76.27) * mm, "end": v(24.74, 76.14) * mm});
            skArc(sketch, "E1318", {"start": v(23.22, 76.14) * mm, "mid": v(23.35, 76.01) * mm, "end": v(23.47, 76.14) * mm});
            skArc(sketch, "E1319", {"start": v(23.47, 76.14) * mm, "mid": v(23.35, 76.27) * mm, "end": v(23.22, 76.14) * mm});
            skArc(sketch, "E1320", {"start": v(21.7, 76.14) * mm, "mid": v(21.82, 76.01) * mm, "end": v(21.95, 76.14) * mm});
            skArc(sketch, "E1321", {"start": v(21.95, 76.14) * mm, "mid": v(21.82, 76.27) * mm, "end": v(21.7, 76.14) * mm});
            skArc(sketch, "E1322", {"start": v(20.17, 76.14) * mm, "mid": v(20.3, 76.01) * mm, "end": v(20.42, 76.14) * mm});
            skArc(sketch, "E1323", {"start": v(20.42, 76.14) * mm, "mid": v(20.3, 76.27) * mm, "end": v(20.17, 76.14) * mm});
            skArc(sketch, "E1324", {"start": v(18.65, 76.14) * mm, "mid": v(18.77, 76.01) * mm, "end": v(18.9, 76.14) * mm});
            skArc(sketch, "E1325", {"start": v(18.9, 76.14) * mm, "mid": v(18.77, 76.27) * mm, "end": v(18.65, 76.14) * mm});
            skArc(sketch, "E1326", {"start": v(17.12, 76.14) * mm, "mid": v(17.25, 76.01) * mm, "end": v(17.38, 76.14) * mm});
            skArc(sketch, "E1327", {"start": v(17.38, 76.14) * mm, "mid": v(17.25, 76.27) * mm, "end": v(17.12, 76.14) * mm});
            skArc(sketch, "E1328", {"start": v(34.01, 72.94) * mm, "mid": v(34.14, 72.81) * mm, "end": v(34.27, 72.94) * mm});
            skArc(sketch, "E1329", {"start": v(34.27, 72.94) * mm, "mid": v(34.14, 73.07) * mm, "end": v(34.01, 72.94) * mm});
            skArc(sketch, "E1330", {"start": v(35.54, 72.94) * mm, "mid": v(35.66, 72.81) * mm, "end": v(35.8, 72.94) * mm});
            skArc(sketch, "E1331", {"start": v(35.8, 72.94) * mm, "mid": v(35.66, 73.07) * mm, "end": v(35.54, 72.94) * mm});
            skArc(sketch, "E1332", {"start": v(32.49, 72.94) * mm, "mid": v(32.62, 72.81) * mm, "end": v(32.74, 72.94) * mm});
            skArc(sketch, "E1333", {"start": v(32.74, 72.94) * mm, "mid": v(32.62, 73.07) * mm, "end": v(32.49, 72.94) * mm});
            skArc(sketch, "E1334", {"start": v(30.97, 72.94) * mm, "mid": v(31.1, 72.81) * mm, "end": v(31.22, 72.94) * mm});
            skArc(sketch, "E1335", {"start": v(31.22, 72.94) * mm, "mid": v(31.1, 73.07) * mm, "end": v(30.97, 72.94) * mm});
            skArc(sketch, "E1336", {"start": v(29.44, 72.94) * mm, "mid": v(29.57, 72.81) * mm, "end": v(29.7, 72.94) * mm});
            skArc(sketch, "E1337", {"start": v(29.7, 72.94) * mm, "mid": v(29.57, 73.07) * mm, "end": v(29.44, 72.94) * mm});
            skArc(sketch, "E1338", {"start": v(27.92, 72.94) * mm, "mid": v(28.04, 72.81) * mm, "end": v(28.17, 72.94) * mm});
            skArc(sketch, "E1339", {"start": v(28.17, 72.94) * mm, "mid": v(28.04, 73.07) * mm, "end": v(27.92, 72.94) * mm});
            skArc(sketch, "E1340", {"start": v(26.4, 72.94) * mm, "mid": v(26.52, 72.81) * mm, "end": v(26.65, 72.94) * mm});
            skArc(sketch, "E1341", {"start": v(26.65, 72.94) * mm, "mid": v(26.52, 73.07) * mm, "end": v(26.4, 72.94) * mm});
            skArc(sketch, "E1342", {"start": v(24.87, 72.94) * mm, "mid": v(25, 72.81) * mm, "end": v(25.12, 72.94) * mm});
            skArc(sketch, "E1343", {"start": v(25.12, 72.94) * mm, "mid": v(25, 73.07) * mm, "end": v(24.87, 72.94) * mm});
            skArc(sketch, "E1344", {"start": v(23.35, 72.94) * mm, "mid": v(23.47, 72.81) * mm, "end": v(23.6, 72.94) * mm});
            skArc(sketch, "E1345", {"start": v(23.6, 72.94) * mm, "mid": v(23.47, 73.07) * mm, "end": v(23.35, 72.94) * mm});
            skArc(sketch, "E1346", {"start": v(21.82, 72.94) * mm, "mid": v(21.95, 72.81) * mm, "end": v(22.08, 72.94) * mm});
            skArc(sketch, "E1347", {"start": v(22.08, 72.94) * mm, "mid": v(21.95, 73.07) * mm, "end": v(21.82, 72.94) * mm});
            skArc(sketch, "E1348", {"start": v(20.3, 72.94) * mm, "mid": v(20.42, 72.81) * mm, "end": v(20.55, 72.94) * mm});
            skArc(sketch, "E1349", {"start": v(20.55, 72.94) * mm, "mid": v(20.42, 73.07) * mm, "end": v(20.3, 72.94) * mm});
            skArc(sketch, "E1350", {"start": v(18.77, 72.94) * mm, "mid": v(18.9, 72.81) * mm, "end": v(19.03, 72.94) * mm});
            skArc(sketch, "E1351", {"start": v(19.03, 72.94) * mm, "mid": v(18.9, 73.07) * mm, "end": v(18.77, 72.94) * mm});
            skArc(sketch, "E1352", {"start": v(17.25, 72.94) * mm, "mid": v(17.38, 72.81) * mm, "end": v(17.5, 72.94) * mm});
            skArc(sketch, "E1353", {"start": v(17.5, 72.94) * mm, "mid": v(17.38, 73.07) * mm, "end": v(17.25, 72.94) * mm});
            skArc(sketch, "E1354", {"start": v(34.09, 70.12) * mm, "mid": v(34.22, 70) * mm, "end": v(34.34, 70.12) * mm});
            skArc(sketch, "E1355", {"start": v(34.34, 70.12) * mm, "mid": v(34.22, 70.25) * mm, "end": v(34.09, 70.12) * mm});
            skArc(sketch, "E1356", {"start": v(35.61, 70.12) * mm, "mid": v(35.74, 70) * mm, "end": v(35.87, 70.12) * mm});
            skArc(sketch, "E1357", {"start": v(35.87, 70.12) * mm, "mid": v(35.74, 70.25) * mm, "end": v(35.61, 70.12) * mm});
            skArc(sketch, "E1358", {"start": v(32.57, 70.12) * mm, "mid": v(32.7, 70) * mm, "end": v(32.82, 70.12) * mm});
            skArc(sketch, "E1359", {"start": v(32.82, 70.12) * mm, "mid": v(32.7, 70.25) * mm, "end": v(32.57, 70.12) * mm});
            skArc(sketch, "E1360", {"start": v(31.04, 70.12) * mm, "mid": v(31.17, 70) * mm, "end": v(31.3, 70.12) * mm});
            skArc(sketch, "E1361", {"start": v(31.3, 70.12) * mm, "mid": v(31.17, 70.25) * mm, "end": v(31.04, 70.12) * mm});
            skArc(sketch, "E1362", {"start": v(29.52, 70.12) * mm, "mid": v(29.64, 70) * mm, "end": v(29.77, 70.12) * mm});
            skArc(sketch, "E1363", {"start": v(29.77, 70.12) * mm, "mid": v(29.64, 70.25) * mm, "end": v(29.52, 70.12) * mm});
            skArc(sketch, "E1364", {"start": v(28, 70.12) * mm, "mid": v(28.12, 70) * mm, "end": v(28.25, 70.12) * mm});
            skArc(sketch, "E1365", {"start": v(28.25, 70.12) * mm, "mid": v(28.12, 70.25) * mm, "end": v(28, 70.12) * mm});
            skArc(sketch, "E1366", {"start": v(26.47, 70.12) * mm, "mid": v(26.6, 70) * mm, "end": v(26.72, 70.12) * mm});
            skArc(sketch, "E1367", {"start": v(26.72, 70.12) * mm, "mid": v(26.6, 70.25) * mm, "end": v(26.47, 70.12) * mm});
            skArc(sketch, "E1368", {"start": v(24.95, 70.12) * mm, "mid": v(25.07, 70) * mm, "end": v(25.2, 70.12) * mm});
            skArc(sketch, "E1369", {"start": v(25.2, 70.12) * mm, "mid": v(25.07, 70.25) * mm, "end": v(24.95, 70.12) * mm});
            skArc(sketch, "E1370", {"start": v(23.42, 70.12) * mm, "mid": v(23.55, 70) * mm, "end": v(23.68, 70.12) * mm});
            skArc(sketch, "E1371", {"start": v(23.68, 70.12) * mm, "mid": v(23.55, 70.25) * mm, "end": v(23.42, 70.12) * mm});
            skArc(sketch, "E1372", {"start": v(21.9, 70.12) * mm, "mid": v(22.02, 70) * mm, "end": v(22.15, 70.12) * mm});
            skArc(sketch, "E1373", {"start": v(22.15, 70.12) * mm, "mid": v(22.02, 70.25) * mm, "end": v(21.9, 70.12) * mm});
            skArc(sketch, "E1374", {"start": v(20.37, 70.12) * mm, "mid": v(20.5, 70) * mm, "end": v(20.63, 70.12) * mm});
            skArc(sketch, "E1375", {"start": v(20.63, 70.12) * mm, "mid": v(20.5, 70.25) * mm, "end": v(20.37, 70.12) * mm});
            skArc(sketch, "E1376", {"start": v(18.85, 70.12) * mm, "mid": v(18.98, 70) * mm, "end": v(19.1, 70.12) * mm});
            skArc(sketch, "E1377", {"start": v(19.1, 70.12) * mm, "mid": v(18.98, 70.25) * mm, "end": v(18.85, 70.12) * mm});
            skArc(sketch, "E1378", {"start": v(17.33, 70.12) * mm, "mid": v(17.45, 70) * mm, "end": v(17.58, 70.12) * mm});
            skArc(sketch, "E1379", {"start": v(17.58, 70.12) * mm, "mid": v(17.45, 70.25) * mm, "end": v(17.33, 70.12) * mm});
            skArc(sketch, "E1380", {"start": v(34.2, 67.38) * mm, "mid": v(34.32, 67.25) * mm, "end": v(34.44, 67.38) * mm});
            skArc(sketch, "E1381", {"start": v(34.44, 67.38) * mm, "mid": v(34.32, 67.5) * mm, "end": v(34.2, 67.38) * mm});
            skArc(sketch, "E1382", {"start": v(35.71, 67.38) * mm, "mid": v(35.84, 67.25) * mm, "end": v(35.97, 67.38) * mm});
            skArc(sketch, "E1383", {"start": v(35.97, 67.38) * mm, "mid": v(35.84, 67.5) * mm, "end": v(35.71, 67.38) * mm});
            skArc(sketch, "E1384", {"start": v(32.67, 67.38) * mm, "mid": v(32.8, 67.25) * mm, "end": v(32.92, 67.38) * mm});
            skArc(sketch, "E1385", {"start": v(32.92, 67.38) * mm, "mid": v(32.8, 67.5) * mm, "end": v(32.67, 67.38) * mm});
            skArc(sketch, "E1386", {"start": v(31.14, 67.38) * mm, "mid": v(31.27, 67.25) * mm, "end": v(31.4, 67.38) * mm});
            skArc(sketch, "E1387", {"start": v(31.4, 67.38) * mm, "mid": v(31.27, 67.5) * mm, "end": v(31.14, 67.38) * mm});
            skArc(sketch, "E1388", {"start": v(29.62, 67.38) * mm, "mid": v(29.75, 67.25) * mm, "end": v(29.87, 67.38) * mm});
            skArc(sketch, "E1389", {"start": v(29.87, 67.38) * mm, "mid": v(29.75, 67.5) * mm, "end": v(29.62, 67.38) * mm});
            skArc(sketch, "E1390", {"start": v(28.1, 67.38) * mm, "mid": v(28.22, 67.25) * mm, "end": v(28.35, 67.38) * mm});
            skArc(sketch, "E1391", {"start": v(28.35, 67.38) * mm, "mid": v(28.22, 67.5) * mm, "end": v(28.1, 67.38) * mm});
            skArc(sketch, "E1392", {"start": v(26.57, 67.38) * mm, "mid": v(26.7, 67.25) * mm, "end": v(26.82, 67.38) * mm});
            skArc(sketch, "E1393", {"start": v(26.82, 67.38) * mm, "mid": v(26.7, 67.5) * mm, "end": v(26.57, 67.38) * mm});
            skArc(sketch, "E1394", {"start": v(25.05, 67.38) * mm, "mid": v(25.17, 67.25) * mm, "end": v(25.3, 67.38) * mm});
            skArc(sketch, "E1395", {"start": v(25.3, 67.38) * mm, "mid": v(25.17, 67.5) * mm, "end": v(25.05, 67.38) * mm});
            skArc(sketch, "E1396", {"start": v(23.52, 67.38) * mm, "mid": v(23.65, 67.25) * mm, "end": v(23.78, 67.38) * mm});
            skArc(sketch, "E1397", {"start": v(23.78, 67.38) * mm, "mid": v(23.65, 67.5) * mm, "end": v(23.52, 67.38) * mm});
            skArc(sketch, "E1398", {"start": v(22, 67.38) * mm, "mid": v(22.13, 67.25) * mm, "end": v(22.25, 67.38) * mm});
            skArc(sketch, "E1399", {"start": v(22.25, 67.38) * mm, "mid": v(22.13, 67.5) * mm, "end": v(22, 67.38) * mm});
            skArc(sketch, "E1400", {"start": v(20.47, 67.38) * mm, "mid": v(20.6, 67.25) * mm, "end": v(20.73, 67.38) * mm});
            skArc(sketch, "E1401", {"start": v(20.73, 67.38) * mm, "mid": v(20.6, 67.5) * mm, "end": v(20.47, 67.38) * mm});
            skArc(sketch, "E1402", {"start": v(18.95, 67.38) * mm, "mid": v(19.08, 67.25) * mm, "end": v(19.2, 67.38) * mm});
            skArc(sketch, "E1403", {"start": v(19.2, 67.38) * mm, "mid": v(19.08, 67.5) * mm, "end": v(18.95, 67.38) * mm});
            skArc(sketch, "E1404", {"start": v(17.43, 67.38) * mm, "mid": v(17.55, 67.25) * mm, "end": v(17.68, 67.38) * mm});
            skArc(sketch, "E1405", {"start": v(17.68, 67.38) * mm, "mid": v(17.55, 67.5) * mm, "end": v(17.43, 67.38) * mm});
            skArc(sketch, "E1406", {"start": v(34.35, 45.3) * mm, "mid": v(34.48, 45.16) * mm, "end": v(34.6, 45.3) * mm});
            skArc(sketch, "E1407", {"start": v(34.6, 45.3) * mm, "mid": v(34.48, 45.42) * mm, "end": v(34.35, 45.3) * mm});
            skArc(sketch, "E1408", {"start": v(35.88, 45.3) * mm, "mid": v(36, 45.16) * mm, "end": v(36.13, 45.3) * mm});
            skArc(sketch, "E1409", {"start": v(36.13, 45.3) * mm, "mid": v(36, 45.42) * mm, "end": v(35.88, 45.3) * mm});
            skArc(sketch, "E1410", {"start": v(32.83, 45.3) * mm, "mid": v(32.96, 45.16) * mm, "end": v(33.08, 45.3) * mm});
            skArc(sketch, "E1411", {"start": v(33.08, 45.3) * mm, "mid": v(32.96, 45.42) * mm, "end": v(32.83, 45.3) * mm});
            skArc(sketch, "E1412", {"start": v(31.3, 45.3) * mm, "mid": v(31.43, 45.16) * mm, "end": v(31.56, 45.3) * mm});
            skArc(sketch, "E1413", {"start": v(31.56, 45.3) * mm, "mid": v(31.43, 45.42) * mm, "end": v(31.3, 45.3) * mm});
            skArc(sketch, "E1414", {"start": v(29.78, 45.3) * mm, "mid": v(29.9, 45.16) * mm, "end": v(30.04, 45.3) * mm});
            skArc(sketch, "E1415", {"start": v(30.04, 45.3) * mm, "mid": v(29.9, 45.42) * mm, "end": v(29.78, 45.3) * mm});
            skArc(sketch, "E1416", {"start": v(28.26, 45.3) * mm, "mid": v(28.38, 45.16) * mm, "end": v(28.51, 45.3) * mm});
            skArc(sketch, "E1417", {"start": v(28.51, 45.3) * mm, "mid": v(28.38, 45.42) * mm, "end": v(28.26, 45.3) * mm});
            skArc(sketch, "E1418", {"start": v(26.73, 45.3) * mm, "mid": v(26.86, 45.16) * mm, "end": v(26.99, 45.3) * mm});
            skArc(sketch, "E1419", {"start": v(26.99, 45.3) * mm, "mid": v(26.86, 45.42) * mm, "end": v(26.73, 45.3) * mm});
            skArc(sketch, "E1420", {"start": v(25.2, 45.3) * mm, "mid": v(25.34, 45.16) * mm, "end": v(25.46, 45.3) * mm});
            skArc(sketch, "E1421", {"start": v(25.46, 45.3) * mm, "mid": v(25.34, 45.42) * mm, "end": v(25.2, 45.3) * mm});
            skArc(sketch, "E1422", {"start": v(23.69, 45.3) * mm, "mid": v(23.81, 45.16) * mm, "end": v(23.94, 45.3) * mm});
            skArc(sketch, "E1423", {"start": v(23.94, 45.3) * mm, "mid": v(23.81, 45.42) * mm, "end": v(23.69, 45.3) * mm});
            skArc(sketch, "E1424", {"start": v(22.16, 45.3) * mm, "mid": v(22.29, 45.16) * mm, "end": v(22.42, 45.3) * mm});
            skArc(sketch, "E1425", {"start": v(22.42, 45.3) * mm, "mid": v(22.29, 45.42) * mm, "end": v(22.16, 45.3) * mm});
            skArc(sketch, "E1426", {"start": v(20.64, 45.3) * mm, "mid": v(20.76, 45.16) * mm, "end": v(20.9, 45.3) * mm});
            skArc(sketch, "E1427", {"start": v(20.9, 45.3) * mm, "mid": v(20.76, 45.42) * mm, "end": v(20.64, 45.3) * mm});
            skArc(sketch, "E1428", {"start": v(19.11, 45.3) * mm, "mid": v(19.24, 45.16) * mm, "end": v(19.37, 45.3) * mm});
            skArc(sketch, "E1429", {"start": v(19.37, 45.3) * mm, "mid": v(19.24, 45.42) * mm, "end": v(19.11, 45.3) * mm});
            skArc(sketch, "E1430", {"start": v(17.59, 45.3) * mm, "mid": v(17.72, 45.16) * mm, "end": v(17.84, 45.3) * mm});
            skArc(sketch, "E1431", {"start": v(17.84, 45.3) * mm, "mid": v(17.72, 45.42) * mm, "end": v(17.59, 45.3) * mm});
            skArc(sketch, "E1432", {"start": v(34.35, 57.63) * mm, "mid": v(34.48, 57.5) * mm, "end": v(34.6, 57.63) * mm});
            skArc(sketch, "E1433", {"start": v(34.6, 57.63) * mm, "mid": v(34.48, 57.76) * mm, "end": v(34.35, 57.63) * mm});
            skArc(sketch, "E1434", {"start": v(35.87, 57.63) * mm, "mid": v(36, 57.5) * mm, "end": v(36.13, 57.63) * mm});
            skArc(sketch, "E1435", {"start": v(36.13, 57.63) * mm, "mid": v(36, 57.76) * mm, "end": v(35.87, 57.63) * mm});
            skArc(sketch, "E1436", {"start": v(32.83, 57.63) * mm, "mid": v(32.95, 57.5) * mm, "end": v(33.08, 57.63) * mm});
            skArc(sketch, "E1437", {"start": v(33.08, 57.63) * mm, "mid": v(32.95, 57.76) * mm, "end": v(32.83, 57.63) * mm});
            skArc(sketch, "E1438", {"start": v(31.3, 57.63) * mm, "mid": v(31.43, 57.5) * mm, "end": v(31.56, 57.63) * mm});
            skArc(sketch, "E1439", {"start": v(31.56, 57.63) * mm, "mid": v(31.43, 57.76) * mm, "end": v(31.3, 57.63) * mm});
            skArc(sketch, "E1440", {"start": v(29.78, 57.63) * mm, "mid": v(29.9, 57.5) * mm, "end": v(30.03, 57.63) * mm});
            skArc(sketch, "E1441", {"start": v(30.03, 57.63) * mm, "mid": v(29.9, 57.76) * mm, "end": v(29.78, 57.63) * mm});
            skArc(sketch, "E1442", {"start": v(28.25, 57.63) * mm, "mid": v(28.38, 57.5) * mm, "end": v(28.5, 57.63) * mm});
            skArc(sketch, "E1443", {"start": v(28.5, 57.63) * mm, "mid": v(28.38, 57.76) * mm, "end": v(28.25, 57.63) * mm});
            skArc(sketch, "E1444", {"start": v(26.73, 57.63) * mm, "mid": v(26.86, 57.5) * mm, "end": v(26.98, 57.63) * mm});
            skArc(sketch, "E1445", {"start": v(26.98, 57.63) * mm, "mid": v(26.86, 57.76) * mm, "end": v(26.73, 57.63) * mm});
            skArc(sketch, "E1446", {"start": v(25.2, 57.63) * mm, "mid": v(25.33, 57.5) * mm, "end": v(25.46, 57.63) * mm});
            skArc(sketch, "E1447", {"start": v(25.46, 57.63) * mm, "mid": v(25.33, 57.76) * mm, "end": v(25.2, 57.63) * mm});
            skArc(sketch, "E1448", {"start": v(23.68, 57.63) * mm, "mid": v(23.8, 57.5) * mm, "end": v(23.94, 57.63) * mm});
            skArc(sketch, "E1449", {"start": v(23.94, 57.63) * mm, "mid": v(23.8, 57.76) * mm, "end": v(23.68, 57.63) * mm});
            skArc(sketch, "E1450", {"start": v(22.16, 57.63) * mm, "mid": v(22.29, 57.5) * mm, "end": v(22.41, 57.63) * mm});
            skArc(sketch, "E1451", {"start": v(22.41, 57.63) * mm, "mid": v(22.29, 57.76) * mm, "end": v(22.16, 57.63) * mm});
            skArc(sketch, "E1452", {"start": v(20.63, 57.63) * mm, "mid": v(20.76, 57.5) * mm, "end": v(20.89, 57.63) * mm});
            skArc(sketch, "E1453", {"start": v(20.89, 57.63) * mm, "mid": v(20.76, 57.76) * mm, "end": v(20.63, 57.63) * mm});
            skArc(sketch, "E1454", {"start": v(19.11, 57.63) * mm, "mid": v(19.24, 57.5) * mm, "end": v(19.36, 57.63) * mm});
            skArc(sketch, "E1455", {"start": v(19.36, 57.63) * mm, "mid": v(19.24, 57.76) * mm, "end": v(19.11, 57.63) * mm});
            skArc(sketch, "E1456", {"start": v(17.59, 57.63) * mm, "mid": v(17.71, 57.5) * mm, "end": v(17.84, 57.63) * mm});
            skArc(sketch, "E1457", {"start": v(17.84, 57.63) * mm, "mid": v(17.71, 57.76) * mm, "end": v(17.59, 57.63) * mm});
            skArc(sketch, "E1458", {"start": v(6.67, 16.32) * mm, "mid": v(6.8, 16.2) * mm, "end": v(6.92, 16.32) * mm});
            skArc(sketch, "E1459", {"start": v(6.92, 16.32) * mm, "mid": v(6.8, 16.45) * mm, "end": v(6.67, 16.32) * mm});
            skArc(sketch, "E1460", {"start": v(11.24, 16.32) * mm, "mid": v(11.37, 16.2) * mm, "end": v(11.5, 16.32) * mm});
            skArc(sketch, "E1461", {"start": v(11.5, 16.32) * mm, "mid": v(11.37, 16.45) * mm, "end": v(11.24, 16.32) * mm});
            skArc(sketch, "E1462", {"start": v(32.58, 16.32) * mm, "mid": v(32.7, 16.2) * mm, "end": v(32.83, 16.32) * mm});
            skArc(sketch, "E1463", {"start": v(32.83, 16.32) * mm, "mid": v(32.7, 16.45) * mm, "end": v(32.58, 16.32) * mm});
            skArc(sketch, "E1464", {"start": v(44.77, 16.32) * mm, "mid": v(44.9, 16.2) * mm, "end": v(45.02, 16.32) * mm});
            skArc(sketch, "E1465", {"start": v(45.02, 16.32) * mm, "mid": v(44.9, 16.45) * mm, "end": v(44.77, 16.32) * mm});
            skArc(sketch, "E1466", {"start": v(46.3, 16.32) * mm, "mid": v(46.42, 16.2) * mm, "end": v(46.55, 16.32) * mm});
            skArc(sketch, "E1467", {"start": v(46.55, 16.32) * mm, "mid": v(46.42, 16.45) * mm, "end": v(46.3, 16.32) * mm});
            skArc(sketch, "E1468", {"start": v(47.82, 16.32) * mm, "mid": v(47.94, 16.2) * mm, "end": v(48.07, 16.32) * mm});
            skArc(sketch, "E1469", {"start": v(48.07, 16.32) * mm, "mid": v(47.94, 16.45) * mm, "end": v(47.82, 16.32) * mm});
            skArc(sketch, "E1470", {"start": v(41.72, 16.32) * mm, "mid": v(41.85, 16.2) * mm, "end": v(41.97, 16.32) * mm});
            skArc(sketch, "E1471", {"start": v(41.97, 16.32) * mm, "mid": v(41.85, 16.45) * mm, "end": v(41.72, 16.32) * mm});
            skArc(sketch, "E1472", {"start": v(43.24, 16.32) * mm, "mid": v(43.37, 16.2) * mm, "end": v(43.5, 16.32) * mm});
            skArc(sketch, "E1473", {"start": v(43.5, 16.32) * mm, "mid": v(43.37, 16.45) * mm, "end": v(43.24, 16.32) * mm});
            skArc(sketch, "E1474", {"start": v(34.1, 16.32) * mm, "mid": v(34.23, 16.2) * mm, "end": v(34.35, 16.32) * mm});
            skArc(sketch, "E1475", {"start": v(34.35, 16.32) * mm, "mid": v(34.23, 16.45) * mm, "end": v(34.1, 16.32) * mm});
            skArc(sketch, "E1476", {"start": v(35.62, 16.32) * mm, "mid": v(35.75, 16.2) * mm, "end": v(35.88, 16.32) * mm});
            skArc(sketch, "E1477", {"start": v(35.88, 16.32) * mm, "mid": v(35.75, 16.45) * mm, "end": v(35.62, 16.32) * mm});
            skArc(sketch, "E1478", {"start": v(37.15, 16.32) * mm, "mid": v(37.27, 16.2) * mm, "end": v(37.4, 16.32) * mm});
            skArc(sketch, "E1479", {"start": v(37.4, 16.32) * mm, "mid": v(37.27, 16.45) * mm, "end": v(37.15, 16.32) * mm});
            skArc(sketch, "E1480", {"start": v(38.67, 16.32) * mm, "mid": v(38.8, 16.2) * mm, "end": v(38.93, 16.32) * mm});
            skArc(sketch, "E1481", {"start": v(38.93, 16.32) * mm, "mid": v(38.8, 16.45) * mm, "end": v(38.67, 16.32) * mm});
            skArc(sketch, "E1482", {"start": v(6.76, 48.15) * mm, "mid": v(6.89, 48.02) * mm, "end": v(7.01, 48.15) * mm});
            skArc(sketch, "E1483", {"start": v(7.01, 48.15) * mm, "mid": v(6.89, 48.28) * mm, "end": v(6.76, 48.15) * mm});
            skArc(sketch, "E1484", {"start": v(6.76, 49.67) * mm, "mid": v(6.89, 49.55) * mm, "end": v(7.01, 49.67) * mm});
            skArc(sketch, "E1485", {"start": v(7.01, 49.67) * mm, "mid": v(6.89, 49.8) * mm, "end": v(6.76, 49.67) * mm});
            skArc(sketch, "E1486", {"start": v(43.8, 35.37) * mm, "mid": v(44.17, 35) * mm, "end": v(44.55, 35.37) * mm});
            skArc(sketch, "E1487", {"start": v(44.55, 35.37) * mm, "mid": v(44.17, 35.76) * mm, "end": v(43.8, 35.37) * mm});
            skArc(sketch, "E1488", {"start": v(46.55, 76.96) * mm, "mid": v(46.61, 76.9) * mm, "end": v(46.68, 76.96) * mm});
            skArc(sketch, "E1489", {"start": v(46.68, 76.96) * mm, "mid": v(46.61, 77.02) * mm, "end": v(46.55, 76.96) * mm});
            skArc(sketch, "E1490", {"start": v(46.54, 75.46) * mm, "mid": v(46.6, 75.4) * mm, "end": v(46.67, 75.46) * mm});
            skArc(sketch, "E1491", {"start": v(46.67, 75.46) * mm, "mid": v(46.6, 75.52) * mm, "end": v(46.54, 75.46) * mm});
            skArc(sketch, "E1492", {"start": v(46.53, 59.4) * mm, "mid": v(46.6, 59.34) * mm, "end": v(46.66, 59.4) * mm});
            skArc(sketch, "E1493", {"start": v(46.66, 59.4) * mm, "mid": v(46.6, 59.47) * mm, "end": v(46.53, 59.4) * mm});
            skArc(sketch, "E1494", {"start": v(46.54, 60.9) * mm, "mid": v(46.6, 60.84) * mm, "end": v(46.67, 60.9) * mm});
            skArc(sketch, "E1495", {"start": v(46.67, 60.9) * mm, "mid": v(46.6, 60.97) * mm, "end": v(46.54, 60.9) * mm});
            skArc(sketch, "E1496", {"start": v(46.54, 44.88) * mm, "mid": v(46.6, 44.81) * mm, "end": v(46.67, 44.88) * mm});
            skArc(sketch, "E1497", {"start": v(46.67, 44.88) * mm, "mid": v(46.6, 44.94) * mm, "end": v(46.54, 44.88) * mm});
            skArc(sketch, "E1498", {"start": v(46.53, 43.38) * mm, "mid": v(46.6, 43.32) * mm, "end": v(46.66, 43.38) * mm});
            skArc(sketch, "E1499", {"start": v(46.66, 43.38) * mm, "mid": v(46.6, 43.44) * mm, "end": v(46.53, 43.38) * mm});
            skArc(sketch, "E1500", {"start": v(46.59, 28.93) * mm, "mid": v(46.65, 28.86) * mm, "end": v(46.71, 28.93) * mm});
            skArc(sketch, "E1501", {"start": v(46.71, 28.93) * mm, "mid": v(46.65, 28.99) * mm, "end": v(46.59, 28.93) * mm});
            skArc(sketch, "E1502", {"start": v(46.6, 27.43) * mm, "mid": v(46.66, 27.37) * mm, "end": v(46.72, 27.43) * mm});
            skArc(sketch, "E1503", {"start": v(46.72, 27.43) * mm, "mid": v(46.66, 27.5) * mm, "end": v(46.6, 27.43) * mm});
            skArc(sketch, "E1504", {"start": v(41.98, 76.96) * mm, "mid": v(42.04, 76.9) * mm, "end": v(42.1, 76.96) * mm});
            skArc(sketch, "E1505", {"start": v(42.1, 76.96) * mm, "mid": v(42.04, 77.02) * mm, "end": v(41.98, 76.96) * mm});
            skArc(sketch, "E1506", {"start": v(41.97, 75.46) * mm, "mid": v(42.03, 75.4) * mm, "end": v(42.1, 75.46) * mm});
            skArc(sketch, "E1507", {"start": v(42.1, 75.46) * mm, "mid": v(42.03, 75.52) * mm, "end": v(41.97, 75.46) * mm});
            skArc(sketch, "E1508", {"start": v(42.01, 28.93) * mm, "mid": v(42.08, 28.86) * mm, "end": v(42.14, 28.93) * mm});
            skArc(sketch, "E1509", {"start": v(42.14, 28.93) * mm, "mid": v(42.08, 28.99) * mm, "end": v(42.01, 28.93) * mm});
            skArc(sketch, "E1510", {"start": v(42.02, 27.43) * mm, "mid": v(42.09, 27.37) * mm, "end": v(42.15, 27.43) * mm});
            skArc(sketch, "E1511", {"start": v(42.15, 27.43) * mm, "mid": v(42.09, 27.5) * mm, "end": v(42.02, 27.43) * mm});
            skArc(sketch, "E1512", {"start": v(37.82, 73.57) * mm, "mid": v(37.88, 73.5) * mm, "end": v(37.95, 73.57) * mm});
            skArc(sketch, "E1513", {"start": v(37.95, 73.57) * mm, "mid": v(37.88, 73.63) * mm, "end": v(37.82, 73.57) * mm});
            skArc(sketch, "E1514", {"start": v(38.09, 75.1) * mm, "mid": v(38.15, 75.04) * mm, "end": v(38.21, 75.1) * mm});
            skArc(sketch, "E1515", {"start": v(38.21, 75.1) * mm, "mid": v(38.15, 75.17) * mm, "end": v(38.09, 75.1) * mm});
            skArc(sketch, "E1516", {"start": v(37.9, 74.57) * mm, "mid": v(37.97, 74.5) * mm, "end": v(38.03, 74.57) * mm});
            skArc(sketch, "E1517", {"start": v(38.03, 74.57) * mm, "mid": v(37.97, 74.64) * mm, "end": v(37.9, 74.57) * mm});
            skArc(sketch, "E1518", {"start": v(41.46, 75.46) * mm, "mid": v(41.53, 75.4) * mm, "end": v(41.59, 75.46) * mm});
            skArc(sketch, "E1519", {"start": v(41.59, 75.46) * mm, "mid": v(41.53, 75.52) * mm, "end": v(41.46, 75.46) * mm});
            skArc(sketch, "E1520", {"start": v(40.95, 75.46) * mm, "mid": v(41.02, 75.4) * mm, "end": v(41.08, 75.46) * mm});
            skArc(sketch, "E1521", {"start": v(41.08, 75.46) * mm, "mid": v(41.02, 75.52) * mm, "end": v(40.95, 75.46) * mm});
            skArc(sketch, "E1522", {"start": v(41.47, 76.96) * mm, "mid": v(41.53, 76.9) * mm, "end": v(41.6, 76.96) * mm});
            skArc(sketch, "E1523", {"start": v(41.6, 76.96) * mm, "mid": v(41.53, 77.02) * mm, "end": v(41.47, 76.96) * mm});
            skArc(sketch, "E1524", {"start": v(40.96, 76.96) * mm, "mid": v(41.03, 76.9) * mm, "end": v(41.09, 76.96) * mm});
            skArc(sketch, "E1525", {"start": v(41.09, 76.96) * mm, "mid": v(41.03, 77.02) * mm, "end": v(40.96, 76.96) * mm});
            skArc(sketch, "E1526", {"start": v(39.32, 73.56) * mm, "mid": v(39.38, 73.5) * mm, "end": v(39.44, 73.56) * mm});
            skArc(sketch, "E1527", {"start": v(39.44, 73.56) * mm, "mid": v(39.38, 73.62) * mm, "end": v(39.32, 73.56) * mm});
            skArc(sketch, "E1528", {"start": v(40.47, 75.37) * mm, "mid": v(40.54, 75.3) * mm, "end": v(40.6, 75.37) * mm});
            skArc(sketch, "E1529", {"start": v(40.6, 75.37) * mm, "mid": v(40.54, 75.43) * mm, "end": v(40.47, 75.37) * mm});
            skArc(sketch, "E1530", {"start": v(40.05, 75.1) * mm, "mid": v(40.11, 75.03) * mm, "end": v(40.18, 75.1) * mm});
            skArc(sketch, "E1531", {"start": v(40.18, 75.1) * mm, "mid": v(40.11, 75.15) * mm, "end": v(40.05, 75.1) * mm});
            skArc(sketch, "E1532", {"start": v(39.32, 70.51) * mm, "mid": v(39.38, 70.45) * mm, "end": v(39.44, 70.51) * mm});
            skArc(sketch, "E1533", {"start": v(39.44, 70.51) * mm, "mid": v(39.38, 70.58) * mm, "end": v(39.32, 70.51) * mm});
            skArc(sketch, "E1534", {"start": v(39.32, 73.05) * mm, "mid": v(39.38, 72.99) * mm, "end": v(39.44, 73.05) * mm});
            skArc(sketch, "E1535", {"start": v(39.44, 73.05) * mm, "mid": v(39.38, 73.12) * mm, "end": v(39.32, 73.05) * mm});
            skArc(sketch, "E1536", {"start": v(39.32, 72.54) * mm, "mid": v(39.38, 72.48) * mm, "end": v(39.44, 72.54) * mm});
            skArc(sketch, "E1537", {"start": v(39.44, 72.54) * mm, "mid": v(39.38, 72.6) * mm, "end": v(39.32, 72.54) * mm});
            skArc(sketch, "E1538", {"start": v(39.32, 71.02) * mm, "mid": v(39.38, 70.96) * mm, "end": v(39.44, 71.02) * mm});
            skArc(sketch, "E1539", {"start": v(39.44, 71.02) * mm, "mid": v(39.38, 71.08) * mm, "end": v(39.32, 71.02) * mm});
            skArc(sketch, "E1540", {"start": v(39.32, 71.53) * mm, "mid": v(39.38, 71.47) * mm, "end": v(39.44, 71.53) * mm});
            skArc(sketch, "E1541", {"start": v(39.44, 71.53) * mm, "mid": v(39.38, 71.6) * mm, "end": v(39.32, 71.53) * mm});
            skArc(sketch, "E1542", {"start": v(39.32, 72.04) * mm, "mid": v(39.38, 71.97) * mm, "end": v(39.44, 72.04) * mm});
            skArc(sketch, "E1543", {"start": v(39.44, 72.04) * mm, "mid": v(39.38, 72.1) * mm, "end": v(39.32, 72.04) * mm});
            skArc(sketch, "E1544", {"start": v(36.94, 57.04) * mm, "mid": v(37, 56.98) * mm, "end": v(37.07, 57.04) * mm});
            skArc(sketch, "E1545", {"start": v(37.07, 57.04) * mm, "mid": v(37, 57.1) * mm, "end": v(36.94, 57.04) * mm});
            skArc(sketch, "E1546", {"start": v(37.04, 55.42) * mm, "mid": v(37.1, 55.36) * mm, "end": v(37.17, 55.42) * mm});
            skArc(sketch, "E1547", {"start": v(37.17, 55.42) * mm, "mid": v(37.1, 55.48) * mm, "end": v(37.04, 55.42) * mm});
            skArc(sketch, "E1548", {"start": v(36.94, 46.97) * mm, "mid": v(37, 46.91) * mm, "end": v(37.07, 46.97) * mm});
            skArc(sketch, "E1549", {"start": v(37.07, 46.97) * mm, "mid": v(37, 47.04) * mm, "end": v(36.94, 46.97) * mm});
            skArc(sketch, "E1550", {"start": v(37.82, 72.55) * mm, "mid": v(37.88, 72.49) * mm, "end": v(37.95, 72.55) * mm});
            skArc(sketch, "E1551", {"start": v(37.95, 72.55) * mm, "mid": v(37.88, 72.62) * mm, "end": v(37.82, 72.55) * mm});
            skArc(sketch, "E1552", {"start": v(30.23, 54.09) * mm, "mid": v(30.29, 54.03) * mm, "end": v(30.35, 54.09) * mm});
            skArc(sketch, "E1553", {"start": v(30.35, 54.09) * mm, "mid": v(30.29, 54.15) * mm, "end": v(30.23, 54.09) * mm});
            skArc(sketch, "E1554", {"start": v(30.23, 52.6) * mm, "mid": v(30.3, 52.53) * mm, "end": v(30.36, 52.6) * mm});
            skArc(sketch, "E1555", {"start": v(30.36, 52.6) * mm, "mid": v(30.3, 52.65) * mm, "end": v(30.23, 52.6) * mm});
            skArc(sketch, "E1556", {"start": v(29.2, 56.78) * mm, "mid": v(29.26, 56.71) * mm, "end": v(29.32, 56.78) * mm});
            skArc(sketch, "E1557", {"start": v(29.32, 56.78) * mm, "mid": v(29.26, 56.84) * mm, "end": v(29.2, 56.78) * mm});
            skArc(sketch, "E1558", {"start": v(28.69, 56.78) * mm, "mid": v(28.75, 56.71) * mm, "end": v(28.81, 56.78) * mm});
            skArc(sketch, "E1559", {"start": v(28.81, 56.78) * mm, "mid": v(28.75, 56.84) * mm, "end": v(28.69, 56.78) * mm});
            skArc(sketch, "E1560", {"start": v(29.71, 55.28) * mm, "mid": v(29.78, 55.21) * mm, "end": v(29.84, 55.28) * mm});
            skArc(sketch, "E1561", {"start": v(29.84, 55.28) * mm, "mid": v(29.78, 55.34) * mm, "end": v(29.71, 55.28) * mm});
            skArc(sketch, "E1562", {"start": v(29.2, 55.28) * mm, "mid": v(29.27, 55.21) * mm, "end": v(29.33, 55.28) * mm});
            skArc(sketch, "E1563", {"start": v(29.33, 55.28) * mm, "mid": v(29.27, 55.34) * mm, "end": v(29.2, 55.28) * mm});
            skArc(sketch, "E1564", {"start": v(37.04, 48.56) * mm, "mid": v(37.1, 48.5) * mm, "end": v(37.17, 48.56) * mm});
            skArc(sketch, "E1565", {"start": v(37.17, 48.56) * mm, "mid": v(37.1, 48.63) * mm, "end": v(37.04, 48.56) * mm});
            skArc(sketch, "E1566", {"start": v(28.7, 55.28) * mm, "mid": v(28.76, 55.21) * mm, "end": v(28.82, 55.28) * mm});
            skArc(sketch, "E1567", {"start": v(28.82, 55.28) * mm, "mid": v(28.76, 55.34) * mm, "end": v(28.7, 55.28) * mm});
            skArc(sketch, "E1568", {"start": v(29.22, 52.6) * mm, "mid": v(29.28, 52.53) * mm, "end": v(29.34, 52.6) * mm});
            skArc(sketch, "E1569", {"start": v(29.34, 52.6) * mm, "mid": v(29.28, 52.65) * mm, "end": v(29.22, 52.6) * mm});
            skArc(sketch, "E1570", {"start": v(29.21, 54.09) * mm, "mid": v(29.27, 54.03) * mm, "end": v(29.34, 54.09) * mm});
            skArc(sketch, "E1571", {"start": v(29.34, 54.09) * mm, "mid": v(29.27, 54.15) * mm, "end": v(29.21, 54.09) * mm});
            skArc(sketch, "E1572", {"start": v(28.7, 51.39) * mm, "mid": v(28.77, 51.33) * mm, "end": v(28.83, 51.39) * mm});
            skArc(sketch, "E1573", {"start": v(28.83, 51.39) * mm, "mid": v(28.77, 51.45) * mm, "end": v(28.7, 51.39) * mm});
            skArc(sketch, "E1574", {"start": v(29.21, 48.74) * mm, "mid": v(29.28, 48.67) * mm, "end": v(29.34, 48.74) * mm});
            skArc(sketch, "E1575", {"start": v(29.34, 48.74) * mm, "mid": v(29.28, 48.8) * mm, "end": v(29.21, 48.74) * mm});
            skArc(sketch, "E1576", {"start": v(28.7, 54.09) * mm, "mid": v(28.77, 54.03) * mm, "end": v(28.83, 54.09) * mm});
            skArc(sketch, "E1577", {"start": v(28.83, 54.09) * mm, "mid": v(28.77, 54.15) * mm, "end": v(28.7, 54.09) * mm});
            skArc(sketch, "E1578", {"start": v(28.7, 52.6) * mm, "mid": v(28.77, 52.53) * mm, "end": v(28.84, 52.6) * mm});
            skArc(sketch, "E1579", {"start": v(28.84, 52.6) * mm, "mid": v(28.77, 52.65) * mm, "end": v(28.7, 52.6) * mm});
            skArc(sketch, "E1580", {"start": v(29.73, 52.6) * mm, "mid": v(29.79, 52.53) * mm, "end": v(29.85, 52.6) * mm});
            skArc(sketch, "E1581", {"start": v(29.85, 52.6) * mm, "mid": v(29.79, 52.65) * mm, "end": v(29.73, 52.6) * mm});
            skArc(sketch, "E1582", {"start": v(29.72, 54.09) * mm, "mid": v(29.78, 54.03) * mm, "end": v(29.85, 54.09) * mm});
            skArc(sketch, "E1583", {"start": v(29.85, 54.09) * mm, "mid": v(29.78, 54.15) * mm, "end": v(29.72, 54.09) * mm});
            skArc(sketch, "E1584", {"start": v(29.72, 48.74) * mm, "mid": v(29.78, 48.67) * mm, "end": v(29.85, 48.74) * mm});
            skArc(sketch, "E1585", {"start": v(29.85, 48.74) * mm, "mid": v(29.78, 48.8) * mm, "end": v(29.72, 48.74) * mm});
            skArc(sketch, "E1586", {"start": v(31.75, 54.09) * mm, "mid": v(31.81, 54.03) * mm, "end": v(31.88, 54.09) * mm});
            skArc(sketch, "E1587", {"start": v(31.88, 54.09) * mm, "mid": v(31.81, 54.15) * mm, "end": v(31.75, 54.09) * mm});
            skArc(sketch, "E1588", {"start": v(31.24, 55.28) * mm, "mid": v(31.3, 55.21) * mm, "end": v(31.36, 55.28) * mm});
            skArc(sketch, "E1589", {"start": v(31.36, 55.28) * mm, "mid": v(31.3, 55.34) * mm, "end": v(31.24, 55.28) * mm});
            skArc(sketch, "E1590", {"start": v(31.76, 52.6) * mm, "mid": v(31.82, 52.53) * mm, "end": v(31.88, 52.6) * mm});
            skArc(sketch, "E1591", {"start": v(31.88, 52.6) * mm, "mid": v(31.82, 52.65) * mm, "end": v(31.76, 52.6) * mm});
            skArc(sketch, "E1592", {"start": v(30.74, 52.6) * mm, "mid": v(30.8, 52.53) * mm, "end": v(30.87, 52.6) * mm});
            skArc(sketch, "E1593", {"start": v(30.87, 52.6) * mm, "mid": v(30.8, 52.65) * mm, "end": v(30.74, 52.6) * mm});
            skArc(sketch, "E1594", {"start": v(32.77, 54.09) * mm, "mid": v(32.83, 54.03) * mm, "end": v(32.9, 54.09) * mm});
            skArc(sketch, "E1595", {"start": v(32.9, 54.09) * mm, "mid": v(32.83, 54.15) * mm, "end": v(32.77, 54.09) * mm});
            skArc(sketch, "E1596", {"start": v(33.27, 54.09) * mm, "mid": v(33.34, 54.03) * mm, "end": v(33.4, 54.09) * mm});
            skArc(sketch, "E1597", {"start": v(33.4, 54.09) * mm, "mid": v(33.34, 54.15) * mm, "end": v(33.27, 54.09) * mm});
            skArc(sketch, "E1598", {"start": v(32.26, 54.09) * mm, "mid": v(32.32, 54.03) * mm, "end": v(32.39, 54.09) * mm});
            skArc(sketch, "E1599", {"start": v(32.39, 54.09) * mm, "mid": v(32.32, 54.15) * mm, "end": v(32.26, 54.09) * mm});
            skArc(sketch, "E1600", {"start": v(32.25, 55.28) * mm, "mid": v(32.32, 55.21) * mm, "end": v(32.38, 55.28) * mm});
            skArc(sketch, "E1601", {"start": v(32.38, 55.28) * mm, "mid": v(32.32, 55.34) * mm, "end": v(32.25, 55.28) * mm});
            skArc(sketch, "E1602", {"start": v(32.24, 56.78) * mm, "mid": v(32.3, 56.71) * mm, "end": v(32.37, 56.78) * mm});
            skArc(sketch, "E1603", {"start": v(32.37, 56.78) * mm, "mid": v(32.3, 56.84) * mm, "end": v(32.24, 56.78) * mm});
            skArc(sketch, "E1604", {"start": v(32.27, 52.6) * mm, "mid": v(32.33, 52.53) * mm, "end": v(32.4, 52.6) * mm});
            skArc(sketch, "E1605", {"start": v(32.4, 52.6) * mm, "mid": v(32.33, 52.65) * mm, "end": v(32.27, 52.6) * mm});
            skArc(sketch, "E1606", {"start": v(36.38, 56.8) * mm, "mid": v(36.45, 56.74) * mm, "end": v(36.5, 56.8) * mm});
            skArc(sketch, "E1607", {"start": v(36.5, 56.8) * mm, "mid": v(36.45, 56.87) * mm, "end": v(36.38, 56.8) * mm});
            skArc(sketch, "E1608", {"start": v(36.43, 55.3) * mm, "mid": v(36.5, 55.23) * mm, "end": v(36.56, 55.3) * mm});
            skArc(sketch, "E1609", {"start": v(36.56, 55.3) * mm, "mid": v(36.5, 55.36) * mm, "end": v(36.43, 55.3) * mm});
            skArc(sketch, "E1610", {"start": v(35.81, 54.09) * mm, "mid": v(35.88, 54.03) * mm, "end": v(35.94, 54.09) * mm});
            skArc(sketch, "E1611", {"start": v(35.94, 54.09) * mm, "mid": v(35.88, 54.15) * mm, "end": v(35.81, 54.09) * mm});
            skArc(sketch, "E1612", {"start": v(35.3, 54.09) * mm, "mid": v(35.37, 54.03) * mm, "end": v(35.43, 54.09) * mm});
            skArc(sketch, "E1613", {"start": v(35.43, 54.09) * mm, "mid": v(35.37, 54.15) * mm, "end": v(35.3, 54.09) * mm});
            skArc(sketch, "E1614", {"start": v(36.32, 54.09) * mm, "mid": v(36.39, 54.02) * mm, "end": v(36.45, 54.09) * mm});
            skArc(sketch, "E1615", {"start": v(36.45, 54.09) * mm, "mid": v(36.39, 54.15) * mm, "end": v(36.32, 54.09) * mm});
            skArc(sketch, "E1616", {"start": v(35.3, 54.09) * mm, "mid": v(35.37, 54.02) * mm, "end": v(35.43, 54.09) * mm});
            skArc(sketch, "E1617", {"start": v(35.81, 54.09) * mm, "mid": v(35.88, 54.02) * mm, "end": v(35.94, 54.09) * mm});
            skArc(sketch, "E1618", {"start": v(36.83, 54.09) * mm, "mid": v(36.9, 54.02) * mm, "end": v(36.96, 54.09) * mm});
            skArc(sketch, "E1619", {"start": v(36.96, 54.09) * mm, "mid": v(36.9, 54.15) * mm, "end": v(36.83, 54.09) * mm});
            skArc(sketch, "E1620", {"start": v(30.73, 55.28) * mm, "mid": v(30.8, 55.21) * mm, "end": v(30.86, 55.28) * mm});
            skArc(sketch, "E1621", {"start": v(30.86, 55.28) * mm, "mid": v(30.8, 55.34) * mm, "end": v(30.73, 55.28) * mm});
            skArc(sketch, "E1622", {"start": v(34.8, 52.6) * mm, "mid": v(34.87, 52.53) * mm, "end": v(34.93, 52.6) * mm});
            skArc(sketch, "E1623", {"start": v(34.93, 52.6) * mm, "mid": v(34.87, 52.65) * mm, "end": v(34.8, 52.6) * mm});
            skArc(sketch, "E1624", {"start": v(33.79, 52.6) * mm, "mid": v(33.85, 52.53) * mm, "end": v(33.92, 52.6) * mm});
            skArc(sketch, "E1625", {"start": v(33.92, 52.6) * mm, "mid": v(33.85, 52.65) * mm, "end": v(33.79, 52.6) * mm});
            skArc(sketch, "E1626", {"start": v(36.33, 52.59) * mm, "mid": v(36.4, 52.52) * mm, "end": v(36.46, 52.59) * mm});
            skArc(sketch, "E1627", {"start": v(36.46, 52.59) * mm, "mid": v(36.4, 52.65) * mm, "end": v(36.33, 52.59) * mm});
            skArc(sketch, "E1628", {"start": v(35.31, 52.59) * mm, "mid": v(35.38, 52.52) * mm, "end": v(35.44, 52.59) * mm});
            skArc(sketch, "E1629", {"start": v(35.44, 52.59) * mm, "mid": v(35.38, 52.65) * mm, "end": v(35.31, 52.59) * mm});
            skArc(sketch, "E1630", {"start": v(35.82, 52.59) * mm, "mid": v(35.89, 52.52) * mm, "end": v(35.95, 52.59) * mm});
            skArc(sketch, "E1631", {"start": v(35.95, 52.59) * mm, "mid": v(35.89, 52.65) * mm, "end": v(35.82, 52.59) * mm});
            skArc(sketch, "E1632", {"start": v(36.84, 52.59) * mm, "mid": v(36.9, 52.52) * mm, "end": v(36.96, 52.59) * mm});
            skArc(sketch, "E1633", {"start": v(36.96, 52.59) * mm, "mid": v(36.9, 52.65) * mm, "end": v(36.84, 52.59) * mm});
            skArc(sketch, "E1634", {"start": v(34.8, 54.09) * mm, "mid": v(34.86, 54.03) * mm, "end": v(34.93, 54.09) * mm});
            skArc(sketch, "E1635", {"start": v(34.93, 54.09) * mm, "mid": v(34.86, 54.15) * mm, "end": v(34.8, 54.09) * mm});
            skArc(sketch, "E1636", {"start": v(33.78, 51.39) * mm, "mid": v(33.85, 51.33) * mm, "end": v(33.9, 51.39) * mm});
            skArc(sketch, "E1637", {"start": v(33.9, 51.39) * mm, "mid": v(33.85, 51.45) * mm, "end": v(33.78, 51.39) * mm});
            skArc(sketch, "E1638", {"start": v(35.81, 51.39) * mm, "mid": v(35.88, 51.33) * mm, "end": v(35.94, 51.39) * mm});
            skArc(sketch, "E1639", {"start": v(35.94, 51.39) * mm, "mid": v(35.88, 51.45) * mm, "end": v(35.81, 51.39) * mm});
            skArc(sketch, "E1640", {"start": v(35.3, 51.39) * mm, "mid": v(35.37, 51.33) * mm, "end": v(35.43, 51.39) * mm});
            skArc(sketch, "E1641", {"start": v(35.43, 51.39) * mm, "mid": v(35.37, 51.45) * mm, "end": v(35.3, 51.39) * mm});
            skArc(sketch, "E1642", {"start": v(34.8, 51.39) * mm, "mid": v(34.86, 51.33) * mm, "end": v(34.93, 51.39) * mm});
            skArc(sketch, "E1643", {"start": v(34.93, 51.39) * mm, "mid": v(34.86, 51.45) * mm, "end": v(34.8, 51.39) * mm});
            skArc(sketch, "E1644", {"start": v(36.32, 51.39) * mm, "mid": v(36.39, 51.32) * mm, "end": v(36.45, 51.39) * mm});
            skArc(sketch, "E1645", {"start": v(36.45, 51.39) * mm, "mid": v(36.39, 51.45) * mm, "end": v(36.32, 51.39) * mm});
            skArc(sketch, "E1646", {"start": v(35.3, 51.39) * mm, "mid": v(35.37, 51.32) * mm, "end": v(35.43, 51.39) * mm});
            skArc(sketch, "E1647", {"start": v(35.81, 51.39) * mm, "mid": v(35.88, 51.32) * mm, "end": v(35.94, 51.39) * mm});
            skArc(sketch, "E1648", {"start": v(36.83, 51.39) * mm, "mid": v(36.9, 51.32) * mm, "end": v(36.96, 51.39) * mm});
            skArc(sketch, "E1649", {"start": v(36.96, 51.39) * mm, "mid": v(36.9, 51.45) * mm, "end": v(36.83, 51.39) * mm});
            skArc(sketch, "E1650", {"start": v(30.22, 55.28) * mm, "mid": v(30.28, 55.21) * mm, "end": v(30.35, 55.28) * mm});
            skArc(sketch, "E1651", {"start": v(30.35, 55.28) * mm, "mid": v(30.28, 55.34) * mm, "end": v(30.22, 55.28) * mm});
            skArc(sketch, "E1652", {"start": v(35.82, 49.9) * mm, "mid": v(35.89, 49.83) * mm, "end": v(35.95, 49.9) * mm});
            skArc(sketch, "E1653", {"start": v(35.95, 49.9) * mm, "mid": v(35.89, 49.95) * mm, "end": v(35.82, 49.9) * mm});
            skArc(sketch, "E1654", {"start": v(36.33, 49.89) * mm, "mid": v(36.4, 49.82) * mm, "end": v(36.46, 49.89) * mm});
            skArc(sketch, "E1655", {"start": v(36.46, 49.89) * mm, "mid": v(36.4, 49.95) * mm, "end": v(36.33, 49.89) * mm});
            skArc(sketch, "E1656", {"start": v(35.32, 49.89) * mm, "mid": v(35.38, 49.82) * mm, "end": v(35.44, 49.89) * mm});
            skArc(sketch, "E1657", {"start": v(35.44, 49.89) * mm, "mid": v(35.38, 49.95) * mm, "end": v(35.32, 49.89) * mm});
            skArc(sketch, "E1658", {"start": v(35.82, 49.89) * mm, "mid": v(35.89, 49.82) * mm, "end": v(35.95, 49.89) * mm});
            skArc(sketch, "E1659", {"start": v(35.95, 49.89) * mm, "mid": v(35.89, 49.95) * mm, "end": v(35.82, 49.89) * mm});
            skArc(sketch, "E1660", {"start": v(36.84, 49.89) * mm, "mid": v(36.9, 49.82) * mm, "end": v(36.97, 49.89) * mm});
            skArc(sketch, "E1661", {"start": v(36.97, 49.89) * mm, "mid": v(36.9, 49.95) * mm, "end": v(36.84, 49.89) * mm});
            skArc(sketch, "E1662", {"start": v(34.3, 48.74) * mm, "mid": v(34.36, 48.67) * mm, "end": v(34.42, 48.74) * mm});
            skArc(sketch, "E1663", {"start": v(34.42, 48.74) * mm, "mid": v(34.36, 48.8) * mm, "end": v(34.3, 48.74) * mm});
            skArc(sketch, "E1664", {"start": v(34.8, 48.74) * mm, "mid": v(34.86, 48.67) * mm, "end": v(34.93, 48.74) * mm});
            skArc(sketch, "E1665", {"start": v(34.93, 48.74) * mm, "mid": v(34.86, 48.8) * mm, "end": v(34.8, 48.74) * mm});
            skArc(sketch, "E1666", {"start": v(42.03, 54.19) * mm, "mid": v(42.1, 54.12) * mm, "end": v(42.16, 54.19) * mm});
            skArc(sketch, "E1667", {"start": v(42.16, 54.19) * mm, "mid": v(42.1, 54.25) * mm, "end": v(42.03, 54.19) * mm});
            skArc(sketch, "E1668", {"start": v(36.38, 47.2) * mm, "mid": v(36.45, 47.13) * mm, "end": v(36.5, 47.2) * mm});
            skArc(sketch, "E1669", {"start": v(36.5, 47.2) * mm, "mid": v(36.45, 47.25) * mm, "end": v(36.38, 47.2) * mm});
            skArc(sketch, "E1670", {"start": v(36.46, 48.72) * mm, "mid": v(36.52, 48.65) * mm, "end": v(36.59, 48.72) * mm});
            skArc(sketch, "E1671", {"start": v(36.59, 48.72) * mm, "mid": v(36.52, 48.78) * mm, "end": v(36.46, 48.72) * mm});
            skArc(sketch, "E1672", {"start": v(38.36, 49.89) * mm, "mid": v(38.43, 49.82) * mm, "end": v(38.5, 49.89) * mm});
            skArc(sketch, "E1673", {"start": v(38.5, 49.89) * mm, "mid": v(38.43, 49.95) * mm, "end": v(38.36, 49.89) * mm});
            skArc(sketch, "E1674", {"start": v(38.35, 51.39) * mm, "mid": v(38.42, 51.32) * mm, "end": v(38.48, 51.39) * mm});
            skArc(sketch, "E1675", {"start": v(38.48, 51.39) * mm, "mid": v(38.42, 51.45) * mm, "end": v(38.35, 51.39) * mm});
            skArc(sketch, "E1676", {"start": v(38.36, 52.59) * mm, "mid": v(38.43, 52.52) * mm, "end": v(38.49, 52.59) * mm});
            skArc(sketch, "E1677", {"start": v(38.49, 52.59) * mm, "mid": v(38.43, 52.65) * mm, "end": v(38.36, 52.59) * mm});
            skArc(sketch, "E1678", {"start": v(38.35, 54.09) * mm, "mid": v(38.42, 54.02) * mm, "end": v(38.48, 54.09) * mm});
            skArc(sketch, "E1679", {"start": v(38.48, 54.09) * mm, "mid": v(38.42, 54.15) * mm, "end": v(38.35, 54.09) * mm});
            skArc(sketch, "E1680", {"start": v(38.38, 28.86) * mm, "mid": v(38.44, 28.8) * mm, "end": v(38.5, 28.86) * mm});
            skArc(sketch, "E1681", {"start": v(38.5, 28.86) * mm, "mid": v(38.44, 28.92) * mm, "end": v(38.38, 28.86) * mm});
            skArc(sketch, "E1682", {"start": v(37.82, 70.01) * mm, "mid": v(37.88, 69.95) * mm, "end": v(37.95, 70.01) * mm});
            skArc(sketch, "E1683", {"start": v(37.95, 70.01) * mm, "mid": v(37.88, 70.08) * mm, "end": v(37.82, 70.01) * mm});
            skArc(sketch, "E1684", {"start": v(37.82, 68.49) * mm, "mid": v(37.88, 68.43) * mm, "end": v(37.95, 68.49) * mm});
            skArc(sketch, "E1685", {"start": v(37.95, 68.49) * mm, "mid": v(37.88, 68.55) * mm, "end": v(37.82, 68.49) * mm});
            skArc(sketch, "E1686", {"start": v(37.82, 69) * mm, "mid": v(37.88, 68.93) * mm, "end": v(37.95, 69) * mm});
            skArc(sketch, "E1687", {"start": v(37.95, 69) * mm, "mid": v(37.88, 69.06) * mm, "end": v(37.82, 69) * mm});
            skArc(sketch, "E1688", {"start": v(37.82, 66.96) * mm, "mid": v(37.88, 66.9) * mm, "end": v(37.95, 66.96) * mm});
            skArc(sketch, "E1689", {"start": v(37.95, 66.96) * mm, "mid": v(37.88, 67.03) * mm, "end": v(37.82, 66.96) * mm});
            skArc(sketch, "E1690", {"start": v(31.25, 47.24) * mm, "mid": v(31.32, 47.18) * mm, "end": v(31.38, 47.24) * mm});
            skArc(sketch, "E1691", {"start": v(31.38, 47.24) * mm, "mid": v(31.32, 47.3) * mm, "end": v(31.25, 47.24) * mm});
            skArc(sketch, "E1692", {"start": v(42.03, 51.33) * mm, "mid": v(42.1, 51.27) * mm, "end": v(42.15, 51.33) * mm});
            skArc(sketch, "E1693", {"start": v(42.15, 51.33) * mm, "mid": v(42.1, 51.4) * mm, "end": v(42.03, 51.33) * mm});
            skArc(sketch, "E1694", {"start": v(37.82, 65.95) * mm, "mid": v(37.88, 65.89) * mm, "end": v(37.95, 65.95) * mm});
            skArc(sketch, "E1695", {"start": v(37.95, 65.95) * mm, "mid": v(37.88, 66.01) * mm, "end": v(37.82, 65.95) * mm});
            skArc(sketch, "E1696", {"start": v(37.82, 67.98) * mm, "mid": v(37.88, 67.92) * mm, "end": v(37.95, 67.98) * mm});
            skArc(sketch, "E1697", {"start": v(37.95, 67.98) * mm, "mid": v(37.88, 68.04) * mm, "end": v(37.82, 67.98) * mm});
            skArc(sketch, "E1698", {"start": v(40.38, 76.88) * mm, "mid": v(40.44, 76.82) * mm, "end": v(40.5, 76.88) * mm});
            skArc(sketch, "E1699", {"start": v(40.5, 76.88) * mm, "mid": v(40.44, 76.95) * mm, "end": v(40.38, 76.88) * mm});
            skArc(sketch, "E1700", {"start": v(37.82, 65.44) * mm, "mid": v(37.88, 65.38) * mm, "end": v(37.95, 65.44) * mm});
            skArc(sketch, "E1701", {"start": v(37.95, 65.44) * mm, "mid": v(37.88, 65.5) * mm, "end": v(37.82, 65.44) * mm});
            skArc(sketch, "E1702", {"start": v(37.82, 64.42) * mm, "mid": v(37.88, 64.36) * mm, "end": v(37.95, 64.42) * mm});
            skArc(sketch, "E1703", {"start": v(37.95, 64.42) * mm, "mid": v(37.88, 64.49) * mm, "end": v(37.82, 64.42) * mm});
            skArc(sketch, "E1704", {"start": v(35.3, 56.78) * mm, "mid": v(35.35, 56.71) * mm, "end": v(35.42, 56.78) * mm});
            skArc(sketch, "E1705", {"start": v(35.42, 56.78) * mm, "mid": v(35.35, 56.84) * mm, "end": v(35.3, 56.78) * mm});
            skArc(sketch, "E1706", {"start": v(37.82, 64.93) * mm, "mid": v(37.88, 64.87) * mm, "end": v(37.95, 64.93) * mm});
            skArc(sketch, "E1707", {"start": v(37.95, 64.93) * mm, "mid": v(37.88, 65) * mm, "end": v(37.82, 64.93) * mm});
            skArc(sketch, "E1708", {"start": v(37.82, 61.89) * mm, "mid": v(37.88, 61.82) * mm, "end": v(37.95, 61.89) * mm});
            skArc(sketch, "E1709", {"start": v(37.95, 61.89) * mm, "mid": v(37.88, 61.95) * mm, "end": v(37.82, 61.89) * mm});
            skArc(sketch, "E1710", {"start": v(37.82, 63.92) * mm, "mid": v(37.88, 63.86) * mm, "end": v(37.95, 63.92) * mm});
            skArc(sketch, "E1711", {"start": v(37.95, 63.92) * mm, "mid": v(37.88, 63.98) * mm, "end": v(37.82, 63.92) * mm});
            skArc(sketch, "E1712", {"start": v(37.82, 63.41) * mm, "mid": v(37.88, 63.35) * mm, "end": v(37.95, 63.41) * mm});
            skArc(sketch, "E1713", {"start": v(37.95, 63.41) * mm, "mid": v(37.88, 63.47) * mm, "end": v(37.82, 63.41) * mm});
            skArc(sketch, "E1714", {"start": v(37.82, 62.9) * mm, "mid": v(37.88, 62.84) * mm, "end": v(37.95, 62.9) * mm});
            skArc(sketch, "E1715", {"start": v(37.95, 62.9) * mm, "mid": v(37.88, 62.97) * mm, "end": v(37.82, 62.9) * mm});
            skArc(sketch, "E1716", {"start": v(37.58, 55.65) * mm, "mid": v(37.64, 55.59) * mm, "end": v(37.7, 55.65) * mm});
            skArc(sketch, "E1717", {"start": v(37.7, 55.65) * mm, "mid": v(37.64, 55.71) * mm, "end": v(37.58, 55.65) * mm});
            skArc(sketch, "E1718", {"start": v(37.82, 59.86) * mm, "mid": v(37.88, 59.8) * mm, "end": v(37.95, 59.86) * mm});
            skArc(sketch, "E1719", {"start": v(37.95, 59.86) * mm, "mid": v(37.88, 59.92) * mm, "end": v(37.82, 59.86) * mm});
            skArc(sketch, "E1720", {"start": v(37.82, 59.35) * mm, "mid": v(37.88, 59.28) * mm, "end": v(37.95, 59.35) * mm});
            skArc(sketch, "E1721", {"start": v(37.95, 59.35) * mm, "mid": v(37.88, 59.41) * mm, "end": v(37.82, 59.35) * mm});
            skArc(sketch, "E1722", {"start": v(37.8, 58.33) * mm, "mid": v(37.86, 58.27) * mm, "end": v(37.92, 58.33) * mm});
            skArc(sketch, "E1723", {"start": v(37.92, 58.33) * mm, "mid": v(37.86, 58.4) * mm, "end": v(37.8, 58.33) * mm});
            skArc(sketch, "E1724", {"start": v(37.82, 58.84) * mm, "mid": v(37.88, 58.78) * mm, "end": v(37.95, 58.84) * mm});
            skArc(sketch, "E1725", {"start": v(37.95, 58.84) * mm, "mid": v(37.88, 58.9) * mm, "end": v(37.82, 58.84) * mm});
            skArc(sketch, "E1726", {"start": v(37.82, 60.87) * mm, "mid": v(37.88, 60.8) * mm, "end": v(37.95, 60.87) * mm});
            skArc(sketch, "E1727", {"start": v(37.95, 60.87) * mm, "mid": v(37.88, 60.93) * mm, "end": v(37.82, 60.87) * mm});
            skArc(sketch, "E1728", {"start": v(37.82, 61.38) * mm, "mid": v(37.88, 61.32) * mm, "end": v(37.95, 61.38) * mm});
            skArc(sketch, "E1729", {"start": v(37.95, 61.38) * mm, "mid": v(37.88, 61.44) * mm, "end": v(37.82, 61.38) * mm});
            skArc(sketch, "E1730", {"start": v(37.82, 60.36) * mm, "mid": v(37.88, 60.3) * mm, "end": v(37.95, 60.36) * mm});
            skArc(sketch, "E1731", {"start": v(37.95, 60.36) * mm, "mid": v(37.88, 60.43) * mm, "end": v(37.82, 60.36) * mm});
            skArc(sketch, "E1732", {"start": v(37.64, 57.84) * mm, "mid": v(37.7, 57.78) * mm, "end": v(37.77, 57.84) * mm});
            skArc(sketch, "E1733", {"start": v(37.77, 57.84) * mm, "mid": v(37.7, 57.9) * mm, "end": v(37.64, 57.84) * mm});
            skArc(sketch, "E1734", {"start": v(37.37, 57.4) * mm, "mid": v(37.43, 57.34) * mm, "end": v(37.5, 57.4) * mm});
            skArc(sketch, "E1735", {"start": v(37.5, 57.4) * mm, "mid": v(37.43, 57.47) * mm, "end": v(37.37, 57.4) * mm});
            skArc(sketch, "E1736", {"start": v(38.12, 56.1) * mm, "mid": v(38.18, 56.03) * mm, "end": v(38.25, 56.1) * mm});
            skArc(sketch, "E1737", {"start": v(38.25, 56.1) * mm, "mid": v(38.18, 56.15) * mm, "end": v(38.12, 56.1) * mm});
            skArc(sketch, "E1738", {"start": v(37.85, 54.09) * mm, "mid": v(37.9, 54.02) * mm, "end": v(37.97, 54.09) * mm});
            skArc(sketch, "E1739", {"start": v(37.97, 54.09) * mm, "mid": v(37.9, 54.15) * mm, "end": v(37.85, 54.09) * mm});
            skArc(sketch, "E1740", {"start": v(37.34, 54.09) * mm, "mid": v(37.4, 54.02) * mm, "end": v(37.47, 54.09) * mm});
            skArc(sketch, "E1741", {"start": v(37.47, 54.09) * mm, "mid": v(37.4, 54.15) * mm, "end": v(37.34, 54.09) * mm});
            skArc(sketch, "E1742", {"start": v(37.85, 52.59) * mm, "mid": v(37.92, 52.52) * mm, "end": v(37.98, 52.59) * mm});
            skArc(sketch, "E1743", {"start": v(37.98, 52.59) * mm, "mid": v(37.92, 52.65) * mm, "end": v(37.85, 52.59) * mm});
            skArc(sketch, "E1744", {"start": v(37.35, 52.59) * mm, "mid": v(37.4, 52.52) * mm, "end": v(37.47, 52.59) * mm});
            skArc(sketch, "E1745", {"start": v(37.47, 52.59) * mm, "mid": v(37.4, 52.65) * mm, "end": v(37.35, 52.59) * mm});
            skArc(sketch, "E1746", {"start": v(37.34, 51.39) * mm, "mid": v(37.4, 51.32) * mm, "end": v(37.47, 51.39) * mm});
            skArc(sketch, "E1747", {"start": v(37.47, 51.39) * mm, "mid": v(37.4, 51.45) * mm, "end": v(37.34, 51.39) * mm});
            skArc(sketch, "E1748", {"start": v(37.85, 51.39) * mm, "mid": v(37.9, 51.32) * mm, "end": v(37.97, 51.39) * mm});
            skArc(sketch, "E1749", {"start": v(37.97, 51.39) * mm, "mid": v(37.9, 51.45) * mm, "end": v(37.85, 51.39) * mm});
            skArc(sketch, "E1750", {"start": v(37.35, 49.89) * mm, "mid": v(37.41, 49.82) * mm, "end": v(37.48, 49.89) * mm});
            skArc(sketch, "E1751", {"start": v(37.48, 49.89) * mm, "mid": v(37.41, 49.95) * mm, "end": v(37.35, 49.89) * mm});
            skArc(sketch, "E1752", {"start": v(37.86, 49.89) * mm, "mid": v(37.92, 49.82) * mm, "end": v(37.98, 49.89) * mm});
            skArc(sketch, "E1753", {"start": v(37.98, 49.89) * mm, "mid": v(37.92, 49.95) * mm, "end": v(37.86, 49.89) * mm});
            skArc(sketch, "E1754", {"start": v(37.6, 48.34) * mm, "mid": v(37.67, 48.28) * mm, "end": v(37.73, 48.34) * mm});
            skArc(sketch, "E1755", {"start": v(37.73, 48.34) * mm, "mid": v(37.67, 48.4) * mm, "end": v(37.6, 48.34) * mm});
            skArc(sketch, "E1756", {"start": v(31.74, 55.28) * mm, "mid": v(31.8, 55.21) * mm, "end": v(31.87, 55.28) * mm});
            skArc(sketch, "E1757", {"start": v(31.87, 55.28) * mm, "mid": v(31.8, 55.34) * mm, "end": v(31.74, 55.28) * mm});
            skArc(sketch, "E1758", {"start": v(38.02, 48.05) * mm, "mid": v(38.08, 48) * mm, "end": v(38.15, 48.05) * mm});
            skArc(sketch, "E1759", {"start": v(38.15, 48.05) * mm, "mid": v(38.08, 48.12) * mm, "end": v(38.02, 48.05) * mm});
            skArc(sketch, "E1760", {"start": v(37.36, 46.58) * mm, "mid": v(37.42, 46.52) * mm, "end": v(37.49, 46.58) * mm});
            skArc(sketch, "E1761", {"start": v(37.49, 46.58) * mm, "mid": v(37.42, 46.65) * mm, "end": v(37.36, 46.58) * mm});
            skArc(sketch, "E1762", {"start": v(37.82, 73.06) * mm, "mid": v(37.88, 73) * mm, "end": v(37.95, 73.06) * mm});
            skArc(sketch, "E1763", {"start": v(37.95, 73.06) * mm, "mid": v(37.88, 73.12) * mm, "end": v(37.82, 73.06) * mm});
            skArc(sketch, "E1764", {"start": v(37.7, 46.06) * mm, "mid": v(37.76, 46) * mm, "end": v(37.83, 46.06) * mm});
            skArc(sketch, "E1765", {"start": v(37.83, 46.06) * mm, "mid": v(37.76, 46.12) * mm, "end": v(37.7, 46.06) * mm});
            skArc(sketch, "E1766", {"start": v(37.86, 30.06) * mm, "mid": v(37.92, 30) * mm, "end": v(37.99, 30.06) * mm});
            skArc(sketch, "E1767", {"start": v(37.99, 30.06) * mm, "mid": v(37.92, 30.13) * mm, "end": v(37.86, 30.06) * mm});
            skArc(sketch, "E1768", {"start": v(38.05, 29.42) * mm, "mid": v(38.12, 29.36) * mm, "end": v(38.18, 29.42) * mm});
            skArc(sketch, "E1769", {"start": v(38.18, 29.42) * mm, "mid": v(38.12, 29.49) * mm, "end": v(38.05, 29.42) * mm});
            skArc(sketch, "E1770", {"start": v(39.32, 70) * mm, "mid": v(39.38, 69.94) * mm, "end": v(39.44, 70) * mm});
            skArc(sketch, "E1771", {"start": v(39.44, 70) * mm, "mid": v(39.38, 70.07) * mm, "end": v(39.32, 70) * mm});
            skArc(sketch, "E1772", {"start": v(39.32, 67.97) * mm, "mid": v(39.38, 67.9) * mm, "end": v(39.44, 67.97) * mm});
            skArc(sketch, "E1773", {"start": v(39.44, 67.97) * mm, "mid": v(39.38, 68.04) * mm, "end": v(39.32, 67.97) * mm});
            skArc(sketch, "E1774", {"start": v(39.32, 69.5) * mm, "mid": v(39.38, 69.43) * mm, "end": v(39.44, 69.5) * mm});
            skArc(sketch, "E1775", {"start": v(39.44, 69.5) * mm, "mid": v(39.38, 69.56) * mm, "end": v(39.32, 69.5) * mm});
            skArc(sketch, "E1776", {"start": v(31.25, 52.6) * mm, "mid": v(31.31, 52.53) * mm, "end": v(31.38, 52.6) * mm});
            skArc(sketch, "E1777", {"start": v(31.38, 52.6) * mm, "mid": v(31.31, 52.65) * mm, "end": v(31.25, 52.6) * mm});
            skArc(sketch, "E1778", {"start": v(39.32, 62.38) * mm, "mid": v(39.38, 62.32) * mm, "end": v(39.44, 62.38) * mm});
            skArc(sketch, "E1779", {"start": v(39.44, 62.38) * mm, "mid": v(39.38, 62.45) * mm, "end": v(39.32, 62.38) * mm});
            skArc(sketch, "E1780", {"start": v(39.32, 65.94) * mm, "mid": v(39.38, 65.88) * mm, "end": v(39.44, 65.94) * mm});
            skArc(sketch, "E1781", {"start": v(39.44, 65.94) * mm, "mid": v(39.38, 66) * mm, "end": v(39.32, 65.94) * mm});
            skArc(sketch, "E1782", {"start": v(39.32, 64.42) * mm, "mid": v(39.38, 64.35) * mm, "end": v(39.44, 64.42) * mm});
            skArc(sketch, "E1783", {"start": v(39.44, 64.42) * mm, "mid": v(39.38, 64.48) * mm, "end": v(39.32, 64.42) * mm});
            skArc(sketch, "E1784", {"start": v(39.32, 64.92) * mm, "mid": v(39.38, 64.86) * mm, "end": v(39.44, 64.92) * mm});
            skArc(sketch, "E1785", {"start": v(39.44, 64.92) * mm, "mid": v(39.38, 64.99) * mm, "end": v(39.32, 64.92) * mm});
            skArc(sketch, "E1786", {"start": v(39.32, 65.43) * mm, "mid": v(39.38, 65.37) * mm, "end": v(39.44, 65.43) * mm});
            skArc(sketch, "E1787", {"start": v(39.44, 65.43) * mm, "mid": v(39.38, 65.5) * mm, "end": v(39.32, 65.43) * mm});
            skArc(sketch, "E1788", {"start": v(37.82, 63.92) * mm, "mid": v(37.88, 63.85) * mm, "end": v(37.95, 63.92) * mm});
            skArc(sketch, "E1789", {"start": v(39.32, 63.4) * mm, "mid": v(39.38, 63.34) * mm, "end": v(39.44, 63.4) * mm});
            skArc(sketch, "E1790", {"start": v(39.44, 63.4) * mm, "mid": v(39.38, 63.46) * mm, "end": v(39.32, 63.4) * mm});
            skArc(sketch, "E1791", {"start": v(39.32, 63.9) * mm, "mid": v(39.38, 63.85) * mm, "end": v(39.44, 63.9) * mm});
            skArc(sketch, "E1792", {"start": v(39.44, 63.9) * mm, "mid": v(39.38, 63.97) * mm, "end": v(39.32, 63.9) * mm});
            skArc(sketch, "E1793", {"start": v(39.32, 59.84) * mm, "mid": v(39.38, 59.78) * mm, "end": v(39.44, 59.84) * mm});
            skArc(sketch, "E1794", {"start": v(39.44, 59.84) * mm, "mid": v(39.38, 59.9) * mm, "end": v(39.32, 59.84) * mm});
            skArc(sketch, "E1795", {"start": v(39.32, 60.86) * mm, "mid": v(39.38, 60.8) * mm, "end": v(39.44, 60.86) * mm});
            skArc(sketch, "E1796", {"start": v(39.44, 60.86) * mm, "mid": v(39.38, 60.92) * mm, "end": v(39.32, 60.86) * mm});
            skArc(sketch, "E1797", {"start": v(39.32, 61.37) * mm, "mid": v(39.38, 61.3) * mm, "end": v(39.44, 61.37) * mm});
            skArc(sketch, "E1798", {"start": v(39.44, 61.37) * mm, "mid": v(39.38, 61.43) * mm, "end": v(39.32, 61.37) * mm});
            skArc(sketch, "E1799", {"start": v(39.32, 61.88) * mm, "mid": v(39.38, 61.81) * mm, "end": v(39.44, 61.88) * mm});
            skArc(sketch, "E1800", {"start": v(39.44, 61.88) * mm, "mid": v(39.38, 61.94) * mm, "end": v(39.32, 61.88) * mm});
            skArc(sketch, "E1801", {"start": v(39.32, 60.35) * mm, "mid": v(39.38, 60.29) * mm, "end": v(39.44, 60.35) * mm});
            skArc(sketch, "E1802", {"start": v(39.44, 60.35) * mm, "mid": v(39.38, 60.42) * mm, "end": v(39.32, 60.35) * mm});
            skArc(sketch, "E1803", {"start": v(39.18, 57.74) * mm, "mid": v(39.24, 57.68) * mm, "end": v(39.3, 57.74) * mm});
            skArc(sketch, "E1804", {"start": v(39.3, 57.74) * mm, "mid": v(39.24, 57.8) * mm, "end": v(39.18, 57.74) * mm});
            skArc(sketch, "E1805", {"start": v(39.33, 58.33) * mm, "mid": v(39.4, 58.26) * mm, "end": v(39.46, 58.33) * mm});
            skArc(sketch, "E1806", {"start": v(39.46, 58.33) * mm, "mid": v(39.4, 58.39) * mm, "end": v(39.33, 58.33) * mm});
            skArc(sketch, "E1807", {"start": v(39.32, 58.83) * mm, "mid": v(39.38, 58.77) * mm, "end": v(39.44, 58.83) * mm});
            skArc(sketch, "E1808", {"start": v(39.44, 58.83) * mm, "mid": v(39.38, 58.9) * mm, "end": v(39.32, 58.83) * mm});
            skArc(sketch, "E1809", {"start": v(39.32, 59.34) * mm, "mid": v(39.38, 59.27) * mm, "end": v(39.44, 59.34) * mm});
            skArc(sketch, "E1810", {"start": v(39.44, 59.34) * mm, "mid": v(39.38, 59.4) * mm, "end": v(39.32, 59.34) * mm});
            skArc(sketch, "E1811", {"start": v(38.58, 56.6) * mm, "mid": v(38.64, 56.54) * mm, "end": v(38.7, 56.6) * mm});
            skArc(sketch, "E1812", {"start": v(38.7, 56.6) * mm, "mid": v(38.64, 56.66) * mm, "end": v(38.58, 56.6) * mm});
            skArc(sketch, "E1813", {"start": v(38.96, 57.16) * mm, "mid": v(39.02, 57.1) * mm, "end": v(39.09, 57.16) * mm});
            skArc(sketch, "E1814", {"start": v(39.09, 57.16) * mm, "mid": v(39.02, 57.22) * mm, "end": v(38.96, 57.16) * mm});
            skArc(sketch, "E1815", {"start": v(39.37, 54.09) * mm, "mid": v(39.43, 54.02) * mm, "end": v(39.5, 54.09) * mm});
            skArc(sketch, "E1816", {"start": v(39.5, 54.09) * mm, "mid": v(39.43, 54.15) * mm, "end": v(39.37, 54.09) * mm});
            skArc(sketch, "E1817", {"start": v(39.88, 54.09) * mm, "mid": v(39.94, 54.02) * mm, "end": v(40, 54.09) * mm});
            skArc(sketch, "E1818", {"start": v(40, 54.09) * mm, "mid": v(39.94, 54.15) * mm, "end": v(39.88, 54.09) * mm});
            skArc(sketch, "E1819", {"start": v(38.86, 54.09) * mm, "mid": v(38.93, 54.02) * mm, "end": v(38.99, 54.09) * mm});
            skArc(sketch, "E1820", {"start": v(38.99, 54.09) * mm, "mid": v(38.93, 54.15) * mm, "end": v(38.86, 54.09) * mm});
            skArc(sketch, "E1821", {"start": v(39.89, 52.59) * mm, "mid": v(39.95, 52.52) * mm, "end": v(40.01, 52.59) * mm});
            skArc(sketch, "E1822", {"start": v(40.01, 52.59) * mm, "mid": v(39.95, 52.65) * mm, "end": v(39.89, 52.59) * mm});
            skArc(sketch, "E1823", {"start": v(39.38, 52.59) * mm, "mid": v(39.44, 52.52) * mm, "end": v(39.5, 52.59) * mm});
            skArc(sketch, "E1824", {"start": v(39.5, 52.59) * mm, "mid": v(39.44, 52.65) * mm, "end": v(39.38, 52.59) * mm});
            skArc(sketch, "E1825", {"start": v(38.87, 52.59) * mm, "mid": v(38.93, 52.52) * mm, "end": v(39, 52.59) * mm});
            skArc(sketch, "E1826", {"start": v(39, 52.59) * mm, "mid": v(38.93, 52.65) * mm, "end": v(38.87, 52.59) * mm});
            skArc(sketch, "E1827", {"start": v(40.4, 52.59) * mm, "mid": v(40.46, 52.52) * mm, "end": v(40.52, 52.59) * mm});
            skArc(sketch, "E1828", {"start": v(40.52, 52.59) * mm, "mid": v(40.46, 52.65) * mm, "end": v(40.4, 52.59) * mm});
            skArc(sketch, "E1829", {"start": v(41.4, 52.59) * mm, "mid": v(41.47, 52.52) * mm, "end": v(41.54, 52.59) * mm});
            skArc(sketch, "E1830", {"start": v(41.54, 52.59) * mm, "mid": v(41.47, 52.65) * mm, "end": v(41.4, 52.59) * mm});
            skArc(sketch, "E1831", {"start": v(40.9, 52.59) * mm, "mid": v(40.97, 52.52) * mm, "end": v(41.03, 52.59) * mm});
            skArc(sketch, "E1832", {"start": v(41.03, 52.59) * mm, "mid": v(40.97, 52.65) * mm, "end": v(40.9, 52.59) * mm});
            skArc(sketch, "E1833", {"start": v(37.82, 64.43) * mm, "mid": v(37.88, 64.36) * mm, "end": v(37.95, 64.43) * mm});
            skArc(sketch, "E1834", {"start": v(37.95, 64.43) * mm, "mid": v(37.88, 64.5) * mm, "end": v(37.82, 64.43) * mm});
            skArc(sketch, "E1835", {"start": v(42, 49.77) * mm, "mid": v(42.06, 49.71) * mm, "end": v(42.13, 49.77) * mm});
            skArc(sketch, "E1836", {"start": v(42.13, 49.77) * mm, "mid": v(42.06, 49.84) * mm, "end": v(42, 49.77) * mm});
            skArc(sketch, "E1837", {"start": v(38.86, 51.39) * mm, "mid": v(38.93, 51.32) * mm, "end": v(38.99, 51.39) * mm});
            skArc(sketch, "E1838", {"start": v(38.99, 51.39) * mm, "mid": v(38.93, 51.45) * mm, "end": v(38.86, 51.39) * mm});
            skArc(sketch, "E1839", {"start": v(38.87, 49.89) * mm, "mid": v(38.94, 49.82) * mm, "end": v(39, 49.89) * mm});
            skArc(sketch, "E1840", {"start": v(39, 49.89) * mm, "mid": v(38.94, 49.95) * mm, "end": v(38.87, 49.89) * mm});
            skArc(sketch, "E1841", {"start": v(39.88, 51.39) * mm, "mid": v(39.94, 51.32) * mm, "end": v(40, 51.39) * mm});
            skArc(sketch, "E1842", {"start": v(40, 51.39) * mm, "mid": v(39.94, 51.45) * mm, "end": v(39.88, 51.39) * mm});
            skArc(sketch, "E1843", {"start": v(39.37, 51.39) * mm, "mid": v(39.43, 51.32) * mm, "end": v(39.5, 51.39) * mm});
            skArc(sketch, "E1844", {"start": v(39.5, 51.39) * mm, "mid": v(39.43, 51.45) * mm, "end": v(39.37, 51.39) * mm});
            skArc(sketch, "E1845", {"start": v(39.38, 49.89) * mm, "mid": v(39.44, 49.82) * mm, "end": v(39.5, 49.89) * mm});
            skArc(sketch, "E1846", {"start": v(39.5, 49.89) * mm, "mid": v(39.44, 49.95) * mm, "end": v(39.38, 49.89) * mm});
            skArc(sketch, "E1847", {"start": v(39.89, 49.89) * mm, "mid": v(39.95, 49.82) * mm, "end": v(40.02, 49.89) * mm});
            skArc(sketch, "E1848", {"start": v(40.02, 49.89) * mm, "mid": v(39.95, 49.95) * mm, "end": v(39.89, 49.89) * mm});
            skArc(sketch, "E1849", {"start": v(39.1, 46.57) * mm, "mid": v(39.17, 46.5) * mm, "end": v(39.24, 46.57) * mm});
            skArc(sketch, "E1850", {"start": v(39.24, 46.57) * mm, "mid": v(39.17, 46.64) * mm, "end": v(39.1, 46.57) * mm});
            skArc(sketch, "E1851", {"start": v(38.47, 47.66) * mm, "mid": v(38.53, 47.6) * mm, "end": v(38.6, 47.66) * mm});
            skArc(sketch, "E1852", {"start": v(38.6, 47.66) * mm, "mid": v(38.53, 47.72) * mm, "end": v(38.47, 47.66) * mm});
            skArc(sketch, "E1853", {"start": v(38.85, 47.12) * mm, "mid": v(38.91, 47.06) * mm, "end": v(38.98, 47.12) * mm});
            skArc(sketch, "E1854", {"start": v(38.98, 47.12) * mm, "mid": v(38.91, 47.19) * mm, "end": v(38.85, 47.12) * mm});
            skArc(sketch, "E1855", {"start": v(39.24, 27.98) * mm, "mid": v(39.3, 27.91) * mm, "end": v(39.37, 27.98) * mm});
            skArc(sketch, "E1856", {"start": v(39.37, 27.98) * mm, "mid": v(39.3, 28.04) * mm, "end": v(39.24, 27.98) * mm});
            skArc(sketch, "E1857", {"start": v(38.78, 28.36) * mm, "mid": v(38.85, 28.3) * mm, "end": v(38.91, 28.36) * mm});
            skArc(sketch, "E1858", {"start": v(38.91, 28.36) * mm, "mid": v(38.85, 28.42) * mm, "end": v(38.78, 28.36) * mm});
            skArc(sketch, "E1859", {"start": v(39.35, 30.3) * mm, "mid": v(39.41, 30.24) * mm, "end": v(39.48, 30.3) * mm});
            skArc(sketch, "E1860", {"start": v(39.48, 30.3) * mm, "mid": v(39.41, 30.37) * mm, "end": v(39.35, 30.3) * mm});
            skArc(sketch, "E1861", {"start": v(39.6, 29.8) * mm, "mid": v(39.66, 29.74) * mm, "end": v(39.73, 29.8) * mm});
            skArc(sketch, "E1862", {"start": v(39.73, 29.8) * mm, "mid": v(39.66, 29.87) * mm, "end": v(39.6, 29.8) * mm});
            skArc(sketch, "E1863", {"start": v(40, 29.32) * mm, "mid": v(40.07, 29.26) * mm, "end": v(40.13, 29.32) * mm});
            skArc(sketch, "E1864", {"start": v(40.13, 29.32) * mm, "mid": v(40.07, 29.39) * mm, "end": v(40, 29.32) * mm});
            skArc(sketch, "E1865", {"start": v(40.54, 29.02) * mm, "mid": v(40.6, 28.95) * mm, "end": v(40.67, 29.02) * mm});
            skArc(sketch, "E1866", {"start": v(40.67, 29.02) * mm, "mid": v(40.6, 29.08) * mm, "end": v(40.54, 29.02) * mm});
            skArc(sketch, "E1867", {"start": v(41, 28.93) * mm, "mid": v(41.06, 28.86) * mm, "end": v(41.13, 28.93) * mm});
            skArc(sketch, "E1868", {"start": v(41.13, 28.93) * mm, "mid": v(41.06, 28.99) * mm, "end": v(41, 28.93) * mm});
            skArc(sketch, "E1869", {"start": v(41.5, 28.93) * mm, "mid": v(41.57, 28.86) * mm, "end": v(41.63, 28.93) * mm});
            skArc(sketch, "E1870", {"start": v(41.63, 28.93) * mm, "mid": v(41.57, 28.99) * mm, "end": v(41.5, 28.93) * mm});
            skArc(sketch, "E1871", {"start": v(39.82, 27.65) * mm, "mid": v(39.89, 27.58) * mm, "end": v(39.95, 27.65) * mm});
            skArc(sketch, "E1872", {"start": v(39.95, 27.65) * mm, "mid": v(39.89, 27.71) * mm, "end": v(39.82, 27.65) * mm});
            skArc(sketch, "E1873", {"start": v(41, 27.43) * mm, "mid": v(41.07, 27.37) * mm, "end": v(41.13, 27.43) * mm});
            skArc(sketch, "E1874", {"start": v(41.13, 27.43) * mm, "mid": v(41.07, 27.5) * mm, "end": v(41, 27.43) * mm});
            skArc(sketch, "E1875", {"start": v(40.42, 27.47) * mm, "mid": v(40.48, 27.4) * mm, "end": v(40.55, 27.47) * mm});
            skArc(sketch, "E1876", {"start": v(40.55, 27.47) * mm, "mid": v(40.48, 27.53) * mm, "end": v(40.42, 27.47) * mm});
            skArc(sketch, "E1877", {"start": v(41.51, 27.43) * mm, "mid": v(41.58, 27.37) * mm, "end": v(41.64, 27.43) * mm});
            skArc(sketch, "E1878", {"start": v(41.64, 27.43) * mm, "mid": v(41.58, 27.5) * mm, "end": v(41.51, 27.43) * mm});
            skArc(sketch, "E1879", {"start": v(44.2, 44.28) * mm, "mid": v(44.27, 44.22) * mm, "end": v(44.33, 44.28) * mm});
            skArc(sketch, "E1880", {"start": v(44.33, 44.28) * mm, "mid": v(44.27, 44.34) * mm, "end": v(44.2, 44.28) * mm});
            skArc(sketch, "E1881", {"start": v(39.32, 66.45) * mm, "mid": v(39.38, 66.39) * mm, "end": v(39.44, 66.45) * mm});
            skArc(sketch, "E1882", {"start": v(39.44, 66.45) * mm, "mid": v(39.38, 66.51) * mm, "end": v(39.32, 66.45) * mm});
            skArc(sketch, "E1883", {"start": v(30.23, 48.74) * mm, "mid": v(30.3, 48.67) * mm, "end": v(30.36, 48.74) * mm});
            skArc(sketch, "E1884", {"start": v(30.36, 48.74) * mm, "mid": v(30.3, 48.8) * mm, "end": v(30.23, 48.74) * mm});
            skArc(sketch, "E1885", {"start": v(44.44, 49.33) * mm, "mid": v(44.5, 49.27) * mm, "end": v(44.57, 49.33) * mm});
            skArc(sketch, "E1886", {"start": v(44.57, 49.33) * mm, "mid": v(44.5, 49.4) * mm, "end": v(44.44, 49.33) * mm});
            skArc(sketch, "E1887", {"start": v(37.82, 69.5) * mm, "mid": v(37.88, 69.44) * mm, "end": v(37.95, 69.5) * mm});
            skArc(sketch, "E1888", {"start": v(37.95, 69.5) * mm, "mid": v(37.88, 69.57) * mm, "end": v(37.82, 69.5) * mm});
            skArc(sketch, "E1889", {"start": v(29.73, 47.24) * mm, "mid": v(29.8, 47.18) * mm, "end": v(29.86, 47.24) * mm});
            skArc(sketch, "E1890", {"start": v(29.86, 47.24) * mm, "mid": v(29.8, 47.3) * mm, "end": v(29.73, 47.24) * mm});
            skArc(sketch, "E1891", {"start": v(43.5, 76.96) * mm, "mid": v(43.57, 76.9) * mm, "end": v(43.63, 76.96) * mm});
            skArc(sketch, "E1892", {"start": v(43.63, 76.96) * mm, "mid": v(43.57, 77.02) * mm, "end": v(43.5, 76.96) * mm});
            skArc(sketch, "E1893", {"start": v(44.01, 76.96) * mm, "mid": v(44.07, 76.9) * mm, "end": v(44.14, 76.96) * mm});
            skArc(sketch, "E1894", {"start": v(44.14, 76.96) * mm, "mid": v(44.07, 77.02) * mm, "end": v(44.01, 76.96) * mm});
            skArc(sketch, "E1895", {"start": v(42.49, 76.96) * mm, "mid": v(42.55, 76.9) * mm, "end": v(42.61, 76.96) * mm});
            skArc(sketch, "E1896", {"start": v(42.61, 76.96) * mm, "mid": v(42.55, 77.02) * mm, "end": v(42.49, 76.96) * mm});
            skArc(sketch, "E1897", {"start": v(42.48, 75.46) * mm, "mid": v(42.54, 75.4) * mm, "end": v(42.6, 75.46) * mm});
            skArc(sketch, "E1898", {"start": v(42.6, 75.46) * mm, "mid": v(42.54, 75.52) * mm, "end": v(42.48, 75.46) * mm});
            skArc(sketch, "E1899", {"start": v(44, 75.46) * mm, "mid": v(44.07, 75.4) * mm, "end": v(44.13, 75.46) * mm});
            skArc(sketch, "E1900", {"start": v(44.13, 75.46) * mm, "mid": v(44.07, 75.52) * mm, "end": v(44, 75.46) * mm});
            skArc(sketch, "E1901", {"start": v(43.5, 75.46) * mm, "mid": v(43.56, 75.4) * mm, "end": v(43.62, 75.46) * mm});
            skArc(sketch, "E1902", {"start": v(43.62, 75.46) * mm, "mid": v(43.56, 75.52) * mm, "end": v(43.5, 75.46) * mm});
            skArc(sketch, "E1903", {"start": v(42.99, 75.46) * mm, "mid": v(43.05, 75.4) * mm, "end": v(43.11, 75.46) * mm});
            skArc(sketch, "E1904", {"start": v(43.11, 75.46) * mm, "mid": v(43.05, 75.52) * mm, "end": v(42.99, 75.46) * mm});
            skArc(sketch, "E1905", {"start": v(43.24, 57.37) * mm, "mid": v(43.3, 57.3) * mm, "end": v(43.37, 57.37) * mm});
            skArc(sketch, "E1906", {"start": v(43.37, 57.37) * mm, "mid": v(43.3, 57.43) * mm, "end": v(43.24, 57.37) * mm});
            skArc(sketch, "E1907", {"start": v(43.24, 56.86) * mm, "mid": v(43.3, 56.8) * mm, "end": v(43.37, 56.86) * mm});
            skArc(sketch, "E1908", {"start": v(43.37, 56.86) * mm, "mid": v(43.3, 56.93) * mm, "end": v(43.24, 56.86) * mm});
            skArc(sketch, "E1909", {"start": v(43.24, 56.87) * mm, "mid": v(43.3, 56.8) * mm, "end": v(43.37, 56.87) * mm});
            skArc(sketch, "E1910", {"start": v(43.37, 56.87) * mm, "mid": v(43.3, 56.93) * mm, "end": v(43.24, 56.87) * mm});
            skArc(sketch, "E1911", {"start": v(34.3, 54.09) * mm, "mid": v(34.35, 54.03) * mm, "end": v(34.42, 54.09) * mm});
            skArc(sketch, "E1912", {"start": v(34.42, 54.09) * mm, "mid": v(34.35, 54.15) * mm, "end": v(34.3, 54.09) * mm});
            skArc(sketch, "E1913", {"start": v(43.24, 56.36) * mm, "mid": v(43.3, 56.3) * mm, "end": v(43.37, 56.36) * mm});
            skArc(sketch, "E1914", {"start": v(43.37, 56.36) * mm, "mid": v(43.3, 56.42) * mm, "end": v(43.24, 56.36) * mm});
            skArc(sketch, "E1915", {"start": v(29.21, 51.39) * mm, "mid": v(29.27, 51.33) * mm, "end": v(29.34, 51.39) * mm});
            skArc(sketch, "E1916", {"start": v(29.34, 51.39) * mm, "mid": v(29.27, 51.45) * mm, "end": v(29.21, 51.39) * mm});
            skArc(sketch, "E1917", {"start": v(42.59, 52.8) * mm, "mid": v(42.65, 52.73) * mm, "end": v(42.71, 52.8) * mm});
            skArc(sketch, "E1918", {"start": v(42.71, 52.8) * mm, "mid": v(42.65, 52.86) * mm, "end": v(42.59, 52.8) * mm});
            skArc(sketch, "E1919", {"start": v(30.24, 49.9) * mm, "mid": v(30.3, 49.83) * mm, "end": v(30.36, 49.9) * mm});
            skArc(sketch, "E1920", {"start": v(30.36, 49.9) * mm, "mid": v(30.3, 49.95) * mm, "end": v(30.24, 49.9) * mm});
            skArc(sketch, "E1921", {"start": v(43.22, 53.13) * mm, "mid": v(43.28, 53.06) * mm, "end": v(43.35, 53.13) * mm});
            skArc(sketch, "E1922", {"start": v(43.35, 53.13) * mm, "mid": v(43.28, 53.2) * mm, "end": v(43.22, 53.13) * mm});
            skArc(sketch, "E1923", {"start": v(30.23, 51.39) * mm, "mid": v(30.29, 51.33) * mm, "end": v(30.35, 51.39) * mm});
            skArc(sketch, "E1924", {"start": v(30.35, 51.39) * mm, "mid": v(30.29, 51.45) * mm, "end": v(30.23, 51.39) * mm});
            skArc(sketch, "E1925", {"start": v(43.79, 53.57) * mm, "mid": v(43.85, 53.5) * mm, "end": v(43.91, 53.57) * mm});
            skArc(sketch, "E1926", {"start": v(43.91, 53.57) * mm, "mid": v(43.85, 53.63) * mm, "end": v(43.79, 53.57) * mm});
            skArc(sketch, "E1927", {"start": v(28.71, 49.9) * mm, "mid": v(28.78, 49.83) * mm, "end": v(28.84, 49.9) * mm});
            skArc(sketch, "E1928", {"start": v(28.84, 49.9) * mm, "mid": v(28.78, 49.95) * mm, "end": v(28.71, 49.9) * mm});
            skArc(sketch, "E1929", {"start": v(44.2, 54.03) * mm, "mid": v(44.26, 53.96) * mm, "end": v(44.32, 54.03) * mm});
            skArc(sketch, "E1930", {"start": v(44.32, 54.03) * mm, "mid": v(44.26, 54.09) * mm, "end": v(44.2, 54.03) * mm});
            skArc(sketch, "E1931", {"start": v(42.92, 54.87) * mm, "mid": v(42.98, 54.8) * mm, "end": v(43.05, 54.87) * mm});
            skArc(sketch, "E1932", {"start": v(43.05, 54.87) * mm, "mid": v(42.98, 54.94) * mm, "end": v(42.92, 54.87) * mm});
            skArc(sketch, "E1933", {"start": v(43.14, 55.3) * mm, "mid": v(43.2, 55.24) * mm, "end": v(43.27, 55.3) * mm});
            skArc(sketch, "E1934", {"start": v(43.27, 55.3) * mm, "mid": v(43.2, 55.37) * mm, "end": v(43.14, 55.3) * mm});
            skArc(sketch, "E1935", {"start": v(39.32, 68.48) * mm, "mid": v(39.38, 68.42) * mm, "end": v(39.44, 68.48) * mm});
            skArc(sketch, "E1936", {"start": v(39.44, 68.48) * mm, "mid": v(39.38, 68.54) * mm, "end": v(39.32, 68.48) * mm});
            skArc(sketch, "E1937", {"start": v(29.22, 49.9) * mm, "mid": v(29.28, 49.83) * mm, "end": v(29.35, 49.9) * mm});
            skArc(sketch, "E1938", {"start": v(29.35, 49.9) * mm, "mid": v(29.28, 49.95) * mm, "end": v(29.22, 49.9) * mm});
            skArc(sketch, "E1939", {"start": v(44.1, 49.99) * mm, "mid": v(44.17, 49.92) * mm, "end": v(44.24, 49.99) * mm});
            skArc(sketch, "E1940", {"start": v(44.24, 49.99) * mm, "mid": v(44.17, 50.05) * mm, "end": v(44.1, 49.99) * mm});
            skArc(sketch, "E1941", {"start": v(34.78, 56.78) * mm, "mid": v(34.85, 56.71) * mm, "end": v(34.9, 56.78) * mm});
            skArc(sketch, "E1942", {"start": v(34.9, 56.78) * mm, "mid": v(34.85, 56.84) * mm, "end": v(34.78, 56.78) * mm});
            skArc(sketch, "E1943", {"start": v(28.71, 47.24) * mm, "mid": v(28.78, 47.18) * mm, "end": v(28.84, 47.24) * mm});
            skArc(sketch, "E1944", {"start": v(28.84, 47.24) * mm, "mid": v(28.78, 47.3) * mm, "end": v(28.71, 47.24) * mm});
            skArc(sketch, "E1945", {"start": v(43.73, 50.44) * mm, "mid": v(43.8, 50.38) * mm, "end": v(43.86, 50.44) * mm});
            skArc(sketch, "E1946", {"start": v(43.86, 50.44) * mm, "mid": v(43.8, 50.5) * mm, "end": v(43.73, 50.44) * mm});
            skArc(sketch, "E1947", {"start": v(34.3, 51.39) * mm, "mid": v(34.35, 51.33) * mm, "end": v(34.42, 51.39) * mm});
            skArc(sketch, "E1948", {"start": v(34.42, 51.39) * mm, "mid": v(34.35, 51.45) * mm, "end": v(34.3, 51.39) * mm});
            skArc(sketch, "E1949", {"start": v(28.7, 48.74) * mm, "mid": v(28.77, 48.67) * mm, "end": v(28.83, 48.74) * mm});
            skArc(sketch, "E1950", {"start": v(28.83, 48.74) * mm, "mid": v(28.77, 48.8) * mm, "end": v(28.7, 48.74) * mm});
            skArc(sketch, "E1951", {"start": v(43.22, 50.85) * mm, "mid": v(43.28, 50.79) * mm, "end": v(43.35, 50.85) * mm});
            skArc(sketch, "E1952", {"start": v(43.35, 50.85) * mm, "mid": v(43.28, 50.91) * mm, "end": v(43.22, 50.85) * mm});
            skArc(sketch, "E1953", {"start": v(39.32, 62.9) * mm, "mid": v(39.38, 62.83) * mm, "end": v(39.44, 62.9) * mm});
            skArc(sketch, "E1954", {"start": v(39.44, 62.9) * mm, "mid": v(39.38, 62.96) * mm, "end": v(39.32, 62.9) * mm});
            skArc(sketch, "E1955", {"start": v(42.64, 51.16) * mm, "mid": v(42.7, 51.1) * mm, "end": v(42.76, 51.16) * mm});
            skArc(sketch, "E1956", {"start": v(42.76, 51.16) * mm, "mid": v(42.7, 51.22) * mm, "end": v(42.64, 51.16) * mm});
            skArc(sketch, "E1957", {"start": v(37.82, 72.04) * mm, "mid": v(37.88, 71.98) * mm, "end": v(37.95, 72.04) * mm});
            skArc(sketch, "E1958", {"start": v(37.95, 72.04) * mm, "mid": v(37.88, 72.1) * mm, "end": v(37.82, 72.04) * mm});
            skArc(sketch, "E1959", {"start": v(42.53, 49.47) * mm, "mid": v(42.6, 49.4) * mm, "end": v(42.66, 49.47) * mm});
            skArc(sketch, "E1960", {"start": v(42.66, 49.47) * mm, "mid": v(42.6, 49.53) * mm, "end": v(42.53, 49.47) * mm});
            skArc(sketch, "E1961", {"start": v(40.9, 54.09) * mm, "mid": v(40.96, 54.02) * mm, "end": v(41.02, 54.09) * mm});
            skArc(sketch, "E1962", {"start": v(41.02, 54.09) * mm, "mid": v(40.96, 54.15) * mm, "end": v(40.9, 54.09) * mm});
            skArc(sketch, "E1963", {"start": v(31.24, 51.39) * mm, "mid": v(31.3, 51.33) * mm, "end": v(31.37, 51.39) * mm});
            skArc(sketch, "E1964", {"start": v(31.37, 51.39) * mm, "mid": v(31.3, 51.45) * mm, "end": v(31.24, 51.39) * mm});
            skArc(sketch, "E1965", {"start": v(42.9, 49.03) * mm, "mid": v(42.96, 48.97) * mm, "end": v(43.03, 49.03) * mm});
            skArc(sketch, "E1966", {"start": v(43.03, 49.03) * mm, "mid": v(42.96, 49.1) * mm, "end": v(42.9, 49.03) * mm});
            skArc(sketch, "E1967", {"start": v(43.14, 48.51) * mm, "mid": v(43.2, 48.45) * mm, "end": v(43.26, 48.51) * mm});
            skArc(sketch, "E1968", {"start": v(43.26, 48.51) * mm, "mid": v(43.2, 48.58) * mm, "end": v(43.14, 48.51) * mm});
            skArc(sketch, "E1969", {"start": v(37.82, 66.46) * mm, "mid": v(37.88, 66.4) * mm, "end": v(37.95, 66.46) * mm});
            skArc(sketch, "E1970", {"start": v(37.95, 66.46) * mm, "mid": v(37.88, 66.52) * mm, "end": v(37.82, 66.46) * mm});
            skArc(sketch, "E1971", {"start": v(31.76, 47.24) * mm, "mid": v(31.83, 47.18) * mm, "end": v(31.89, 47.24) * mm});
            skArc(sketch, "E1972", {"start": v(31.89, 47.24) * mm, "mid": v(31.83, 47.3) * mm, "end": v(31.76, 47.24) * mm});
            skArc(sketch, "E1973", {"start": v(43.23, 45.93) * mm, "mid": v(43.3, 45.87) * mm, "end": v(43.36, 45.93) * mm});
            skArc(sketch, "E1974", {"start": v(43.36, 45.93) * mm, "mid": v(43.3, 46) * mm, "end": v(43.23, 45.93) * mm});
            skArc(sketch, "E1975", {"start": v(43.47, 45.32) * mm, "mid": v(43.53, 45.26) * mm, "end": v(43.6, 45.32) * mm});
            skArc(sketch, "E1976", {"start": v(43.6, 45.32) * mm, "mid": v(43.53, 45.38) * mm, "end": v(43.47, 45.32) * mm});
            skArc(sketch, "E1977", {"start": v(33.8, 49.9) * mm, "mid": v(33.86, 49.83) * mm, "end": v(33.92, 49.9) * mm});
            skArc(sketch, "E1978", {"start": v(33.92, 49.9) * mm, "mid": v(33.86, 49.95) * mm, "end": v(33.8, 49.9) * mm});
            skArc(sketch, "E1979", {"start": v(43.77, 44.76) * mm, "mid": v(43.84, 44.7) * mm, "end": v(43.9, 44.76) * mm});
            skArc(sketch, "E1980", {"start": v(43.9, 44.76) * mm, "mid": v(43.84, 44.83) * mm, "end": v(43.77, 44.76) * mm});
            skArc(sketch, "E1981", {"start": v(35.31, 52.6) * mm, "mid": v(35.38, 52.53) * mm, "end": v(35.44, 52.6) * mm});
            skArc(sketch, "E1982", {"start": v(35.44, 52.6) * mm, "mid": v(35.38, 52.65) * mm, "end": v(35.31, 52.6) * mm});
            skArc(sketch, "E1983", {"start": v(43.18, 46.46) * mm, "mid": v(43.24, 46.4) * mm, "end": v(43.3, 46.46) * mm});
            skArc(sketch, "E1984", {"start": v(43.3, 46.46) * mm, "mid": v(43.24, 46.52) * mm, "end": v(43.18, 46.46) * mm});
            skArc(sketch, "E1985", {"start": v(41.4, 51.39) * mm, "mid": v(41.47, 51.32) * mm, "end": v(41.53, 51.39) * mm});
            skArc(sketch, "E1986", {"start": v(41.53, 51.39) * mm, "mid": v(41.47, 51.45) * mm, "end": v(41.4, 51.39) * mm});
            skArc(sketch, "E1987", {"start": v(39.32, 67.46) * mm, "mid": v(39.38, 67.4) * mm, "end": v(39.44, 67.46) * mm});
            skArc(sketch, "E1988", {"start": v(39.44, 67.46) * mm, "mid": v(39.38, 67.53) * mm, "end": v(39.32, 67.46) * mm});
            skArc(sketch, "E1989", {"start": v(43.18, 47.47) * mm, "mid": v(43.24, 47.4) * mm, "end": v(43.3, 47.47) * mm});
            skArc(sketch, "E1990", {"start": v(43.3, 47.47) * mm, "mid": v(43.24, 47.54) * mm, "end": v(43.18, 47.47) * mm});
            skArc(sketch, "E1991", {"start": v(41.41, 49.89) * mm, "mid": v(41.48, 49.82) * mm, "end": v(41.54, 49.89) * mm});
            skArc(sketch, "E1992", {"start": v(41.54, 49.89) * mm, "mid": v(41.48, 49.95) * mm, "end": v(41.41, 49.89) * mm});
            skArc(sketch, "E1993", {"start": v(37.82, 70.52) * mm, "mid": v(37.88, 70.46) * mm, "end": v(37.95, 70.52) * mm});
            skArc(sketch, "E1994", {"start": v(37.95, 70.52) * mm, "mid": v(37.88, 70.58) * mm, "end": v(37.82, 70.52) * mm});
            skArc(sketch, "E1995", {"start": v(43.18, 47.98) * mm, "mid": v(43.24, 47.92) * mm, "end": v(43.3, 47.98) * mm});
            skArc(sketch, "E1996", {"start": v(43.3, 47.98) * mm, "mid": v(43.24, 48.04) * mm, "end": v(43.18, 47.98) * mm});
            skArc(sketch, "E1997", {"start": v(29.72, 51.39) * mm, "mid": v(29.78, 51.33) * mm, "end": v(29.85, 51.39) * mm});
            skArc(sketch, "E1998", {"start": v(29.85, 51.39) * mm, "mid": v(29.78, 51.45) * mm, "end": v(29.72, 51.39) * mm});
            skArc(sketch, "E1999", {"start": v(39.23, 76.38) * mm, "mid": v(39.3, 76.31) * mm, "end": v(39.36, 76.38) * mm});
            skArc(sketch, "E2000", {"start": v(39.36, 76.38) * mm, "mid": v(39.3, 76.44) * mm, "end": v(39.23, 76.38) * mm});
            skArc(sketch, "E2001", {"start": v(43.18, 46.96) * mm, "mid": v(43.24, 46.9) * mm, "end": v(43.3, 46.96) * mm});
            skArc(sketch, "E2002", {"start": v(43.3, 46.96) * mm, "mid": v(43.24, 47.03) * mm, "end": v(43.18, 46.96) * mm});
            skArc(sketch, "E2003", {"start": v(30.74, 49.9) * mm, "mid": v(30.8, 49.83) * mm, "end": v(30.87, 49.9) * mm});
            skArc(sketch, "E2004", {"start": v(30.87, 49.9) * mm, "mid": v(30.8, 49.95) * mm, "end": v(30.74, 49.9) * mm});
            skArc(sketch, "E2005", {"start": v(39.79, 76.68) * mm, "mid": v(39.85, 76.62) * mm, "end": v(39.92, 76.68) * mm});
            skArc(sketch, "E2006", {"start": v(39.92, 76.68) * mm, "mid": v(39.85, 76.74) * mm, "end": v(39.79, 76.68) * mm});
            skArc(sketch, "E2007", {"start": v(43.03, 28.93) * mm, "mid": v(43.1, 28.86) * mm, "end": v(43.16, 28.93) * mm});
            skArc(sketch, "E2008", {"start": v(43.16, 28.93) * mm, "mid": v(43.1, 28.99) * mm, "end": v(43.03, 28.93) * mm});
            skArc(sketch, "E2009", {"start": v(43.54, 28.93) * mm, "mid": v(43.6, 28.86) * mm, "end": v(43.67, 28.93) * mm});
            skArc(sketch, "E2010", {"start": v(43.67, 28.93) * mm, "mid": v(43.6, 28.99) * mm, "end": v(43.54, 28.93) * mm});
            skArc(sketch, "E2011", {"start": v(44.05, 28.93) * mm, "mid": v(44.1, 28.86) * mm, "end": v(44.17, 28.93) * mm});
            skArc(sketch, "E2012", {"start": v(44.17, 28.93) * mm, "mid": v(44.1, 28.99) * mm, "end": v(44.05, 28.93) * mm});
            skArc(sketch, "E2013", {"start": v(42.52, 28.93) * mm, "mid": v(42.59, 28.86) * mm, "end": v(42.65, 28.93) * mm});
            skArc(sketch, "E2014", {"start": v(42.65, 28.93) * mm, "mid": v(42.59, 28.99) * mm, "end": v(42.52, 28.93) * mm});
            skArc(sketch, "E2015", {"start": v(42.53, 27.43) * mm, "mid": v(42.6, 27.37) * mm, "end": v(42.66, 27.43) * mm});
            skArc(sketch, "E2016", {"start": v(42.66, 27.43) * mm, "mid": v(42.6, 27.5) * mm, "end": v(42.53, 27.43) * mm});
            skArc(sketch, "E2017", {"start": v(44.05, 27.43) * mm, "mid": v(44.12, 27.37) * mm, "end": v(44.18, 27.43) * mm});
            skArc(sketch, "E2018", {"start": v(44.18, 27.43) * mm, "mid": v(44.12, 27.5) * mm, "end": v(44.05, 27.43) * mm});
            skArc(sketch, "E2019", {"start": v(43.55, 27.43) * mm, "mid": v(43.6, 27.37) * mm, "end": v(43.67, 27.43) * mm});
            skArc(sketch, "E2020", {"start": v(43.67, 27.43) * mm, "mid": v(43.6, 27.5) * mm, "end": v(43.55, 27.43) * mm});
            skArc(sketch, "E2021", {"start": v(43.04, 27.43) * mm, "mid": v(43.1, 27.37) * mm, "end": v(43.16, 27.43) * mm});
            skArc(sketch, "E2022", {"start": v(43.16, 27.43) * mm, "mid": v(43.1, 27.5) * mm, "end": v(43.04, 27.43) * mm});
            skArc(sketch, "E2023", {"start": v(46.04, 76.96) * mm, "mid": v(46.1, 76.9) * mm, "end": v(46.17, 76.96) * mm});
            skArc(sketch, "E2024", {"start": v(46.17, 76.96) * mm, "mid": v(46.1, 77.02) * mm, "end": v(46.04, 76.96) * mm});
            skArc(sketch, "E2025", {"start": v(42.51, 54.44) * mm, "mid": v(42.58, 54.38) * mm, "end": v(42.64, 54.44) * mm});
            skArc(sketch, "E2026", {"start": v(42.64, 54.44) * mm, "mid": v(42.58, 54.5) * mm, "end": v(42.51, 54.44) * mm});
            skArc(sketch, "E2027", {"start": v(44.52, 76.96) * mm, "mid": v(44.58, 76.9) * mm, "end": v(44.65, 76.96) * mm});
            skArc(sketch, "E2028", {"start": v(44.65, 76.96) * mm, "mid": v(44.58, 77.02) * mm, "end": v(44.52, 76.96) * mm});
            skArc(sketch, "E2029", {"start": v(33.77, 56.78) * mm, "mid": v(33.83, 56.71) * mm, "end": v(33.9, 56.78) * mm});
            skArc(sketch, "E2030", {"start": v(33.9, 56.78) * mm, "mid": v(33.83, 56.84) * mm, "end": v(33.77, 56.78) * mm});
            skArc(sketch, "E2031", {"start": v(44.51, 75.46) * mm, "mid": v(44.57, 75.4) * mm, "end": v(44.64, 75.46) * mm});
            skArc(sketch, "E2032", {"start": v(44.64, 75.46) * mm, "mid": v(44.57, 75.52) * mm, "end": v(44.51, 75.46) * mm});
            skArc(sketch, "E2033", {"start": v(45.53, 75.46) * mm, "mid": v(45.6, 75.4) * mm, "end": v(45.65, 75.46) * mm});
            skArc(sketch, "E2034", {"start": v(45.65, 75.46) * mm, "mid": v(45.6, 75.52) * mm, "end": v(45.53, 75.46) * mm});
            skArc(sketch, "E2035", {"start": v(45.02, 75.46) * mm, "mid": v(45.08, 75.4) * mm, "end": v(45.15, 75.46) * mm});
            skArc(sketch, "E2036", {"start": v(45.15, 75.46) * mm, "mid": v(45.08, 75.52) * mm, "end": v(45.02, 75.46) * mm});
            skArc(sketch, "E2037", {"start": v(44.74, 57.36) * mm, "mid": v(44.8, 57.3) * mm, "end": v(44.86, 57.36) * mm});
            skArc(sketch, "E2038", {"start": v(44.86, 57.36) * mm, "mid": v(44.8, 57.42) * mm, "end": v(44.74, 57.36) * mm});
            skArc(sketch, "E2039", {"start": v(35.82, 48.74) * mm, "mid": v(35.88, 48.67) * mm, "end": v(35.94, 48.74) * mm});
            skArc(sketch, "E2040", {"start": v(35.94, 48.74) * mm, "mid": v(35.88, 48.8) * mm, "end": v(35.82, 48.74) * mm});
            skArc(sketch, "E2041", {"start": v(46.08, 59.37) * mm, "mid": v(46.14, 59.3) * mm, "end": v(46.2, 59.37) * mm});
            skArc(sketch, "E2042", {"start": v(46.2, 59.37) * mm, "mid": v(46.14, 59.44) * mm, "end": v(46.08, 59.37) * mm});
            skArc(sketch, "E2043", {"start": v(46.03, 60.9) * mm, "mid": v(46.1, 60.84) * mm, "end": v(46.16, 60.9) * mm});
            skArc(sketch, "E2044", {"start": v(46.16, 60.9) * mm, "mid": v(46.1, 60.97) * mm, "end": v(46.03, 60.9) * mm});
            skArc(sketch, "E2045", {"start": v(44.5, 60.23) * mm, "mid": v(44.56, 60.17) * mm, "end": v(44.62, 60.23) * mm});
            skArc(sketch, "E2046", {"start": v(44.62, 60.23) * mm, "mid": v(44.56, 60.3) * mm, "end": v(44.5, 60.23) * mm});
            skArc(sketch, "E2047", {"start": v(45.07, 60.64) * mm, "mid": v(45.13, 60.57) * mm, "end": v(45.2, 60.64) * mm});
            skArc(sketch, "E2048", {"start": v(45.2, 60.64) * mm, "mid": v(45.13, 60.7) * mm, "end": v(45.07, 60.64) * mm});
            skArc(sketch, "E2049", {"start": v(45.53, 60.87) * mm, "mid": v(45.6, 60.8) * mm, "end": v(45.65, 60.87) * mm});
            skArc(sketch, "E2050", {"start": v(45.65, 60.87) * mm, "mid": v(45.6, 60.93) * mm, "end": v(45.53, 60.87) * mm});
            skArc(sketch, "E2051", {"start": v(45.2, 58.87) * mm, "mid": v(45.26, 58.81) * mm, "end": v(45.32, 58.87) * mm});
            skArc(sketch, "E2052", {"start": v(45.32, 58.87) * mm, "mid": v(45.26, 58.94) * mm, "end": v(45.2, 58.87) * mm});
            skArc(sketch, "E2053", {"start": v(45.61, 59.17) * mm, "mid": v(45.67, 59.1) * mm, "end": v(45.74, 59.17) * mm});
            skArc(sketch, "E2054", {"start": v(45.74, 59.17) * mm, "mid": v(45.67, 59.23) * mm, "end": v(45.61, 59.17) * mm});
            skArc(sketch, "E2055", {"start": v(44.9, 58.35) * mm, "mid": v(44.97, 58.3) * mm, "end": v(45.03, 58.35) * mm});
            skArc(sketch, "E2056", {"start": v(45.03, 58.35) * mm, "mid": v(44.97, 58.42) * mm, "end": v(44.9, 58.35) * mm});
            skArc(sketch, "E2057", {"start": v(37.82, 71.03) * mm, "mid": v(37.88, 70.97) * mm, "end": v(37.95, 71.03) * mm});
            skArc(sketch, "E2058", {"start": v(37.95, 71.03) * mm, "mid": v(37.88, 71.1) * mm, "end": v(37.82, 71.03) * mm});
            skArc(sketch, "E2059", {"start": v(44.73, 57.87) * mm, "mid": v(44.8, 57.8) * mm, "end": v(44.85, 57.87) * mm});
            skArc(sketch, "E2060", {"start": v(44.85, 57.87) * mm, "mid": v(44.8, 57.93) * mm, "end": v(44.73, 57.87) * mm});
            skArc(sketch, "E2061", {"start": v(37.82, 71.54) * mm, "mid": v(37.88, 71.47) * mm, "end": v(37.95, 71.54) * mm});
            skArc(sketch, "E2062", {"start": v(37.95, 71.54) * mm, "mid": v(37.88, 71.6) * mm, "end": v(37.82, 71.54) * mm});
            skArc(sketch, "E2063", {"start": v(44.5, 54.58) * mm, "mid": v(44.56, 54.52) * mm, "end": v(44.63, 54.58) * mm});
            skArc(sketch, "E2064", {"start": v(44.63, 54.58) * mm, "mid": v(44.56, 54.65) * mm, "end": v(44.5, 54.58) * mm});
            skArc(sketch, "E2065", {"start": v(33.78, 48.74) * mm, "mid": v(33.85, 48.67) * mm, "end": v(33.91, 48.74) * mm});
            skArc(sketch, "E2066", {"start": v(33.91, 48.74) * mm, "mid": v(33.85, 48.8) * mm, "end": v(33.78, 48.74) * mm});
            skArc(sketch, "E2067", {"start": v(44.68, 55.2) * mm, "mid": v(44.74, 55.13) * mm, "end": v(44.8, 55.2) * mm});
            skArc(sketch, "E2068", {"start": v(44.8, 55.2) * mm, "mid": v(44.74, 55.26) * mm, "end": v(44.68, 55.2) * mm});
            skArc(sketch, "E2069", {"start": v(35.3, 48.74) * mm, "mid": v(35.37, 48.67) * mm, "end": v(35.44, 48.74) * mm});
            skArc(sketch, "E2070", {"start": v(35.44, 48.74) * mm, "mid": v(35.37, 48.8) * mm, "end": v(35.3, 48.74) * mm});
            skArc(sketch, "E2071", {"start": v(44.74, 56.86) * mm, "mid": v(44.8, 56.8) * mm, "end": v(44.86, 56.86) * mm});
            skArc(sketch, "E2072", {"start": v(44.86, 56.86) * mm, "mid": v(44.8, 56.92) * mm, "end": v(44.74, 56.86) * mm});
            skArc(sketch, "E2073", {"start": v(45.53, 76.96) * mm, "mid": v(45.6, 76.9) * mm, "end": v(45.66, 76.96) * mm});
            skArc(sketch, "E2074", {"start": v(45.66, 76.96) * mm, "mid": v(45.6, 77.02) * mm, "end": v(45.53, 76.96) * mm});
            skArc(sketch, "E2075", {"start": v(44.74, 56.35) * mm, "mid": v(44.8, 56.28) * mm, "end": v(44.86, 56.35) * mm});
            skArc(sketch, "E2076", {"start": v(44.86, 56.35) * mm, "mid": v(44.8, 56.41) * mm, "end": v(44.74, 56.35) * mm});
            skArc(sketch, "E2077", {"start": v(45.03, 76.96) * mm, "mid": v(45.1, 76.9) * mm, "end": v(45.15, 76.96) * mm});
            skArc(sketch, "E2078", {"start": v(45.15, 76.96) * mm, "mid": v(45.1, 77.02) * mm, "end": v(45.03, 76.96) * mm});
            skArc(sketch, "E2079", {"start": v(44.74, 55.84) * mm, "mid": v(44.8, 55.78) * mm, "end": v(44.86, 55.84) * mm});
            skArc(sketch, "E2080", {"start": v(44.86, 55.84) * mm, "mid": v(44.8, 55.9) * mm, "end": v(44.74, 55.84) * mm});
            skArc(sketch, "E2081", {"start": v(37.82, 64.94) * mm, "mid": v(37.88, 64.87) * mm, "end": v(37.95, 64.94) * mm});
            skArc(sketch, "E2082", {"start": v(37.95, 64.94) * mm, "mid": v(37.88, 65) * mm, "end": v(37.82, 64.94) * mm});
            skArc(sketch, "E2083", {"start": v(44.67, 48.57) * mm, "mid": v(44.73, 48.5) * mm, "end": v(44.8, 48.57) * mm});
            skArc(sketch, "E2084", {"start": v(44.8, 48.57) * mm, "mid": v(44.73, 48.63) * mm, "end": v(44.67, 48.57) * mm});
            skArc(sketch, "E2085", {"start": v(29.22, 47.24) * mm, "mid": v(29.29, 47.18) * mm, "end": v(29.35, 47.24) * mm});
            skArc(sketch, "E2086", {"start": v(29.35, 47.24) * mm, "mid": v(29.29, 47.3) * mm, "end": v(29.22, 47.24) * mm});
            skArc(sketch, "E2087", {"start": v(44.69, 43.9) * mm, "mid": v(44.75, 43.84) * mm, "end": v(44.82, 43.9) * mm});
            skArc(sketch, "E2088", {"start": v(44.82, 43.9) * mm, "mid": v(44.75, 43.96) * mm, "end": v(44.69, 43.9) * mm});
            skArc(sketch, "E2089", {"start": v(39.32, 66.96) * mm, "mid": v(39.38, 66.9) * mm, "end": v(39.44, 66.96) * mm});
            skArc(sketch, "E2090", {"start": v(39.44, 66.96) * mm, "mid": v(39.38, 67.02) * mm, "end": v(39.32, 66.96) * mm});
            skArc(sketch, "E2091", {"start": v(30.24, 47.24) * mm, "mid": v(30.3, 47.18) * mm, "end": v(30.37, 47.24) * mm});
            skArc(sketch, "E2092", {"start": v(30.37, 47.24) * mm, "mid": v(30.3, 47.3) * mm, "end": v(30.24, 47.24) * mm});
            skArc(sketch, "E2093", {"start": v(45.27, 43.67) * mm, "mid": v(45.34, 43.6) * mm, "end": v(45.4, 43.67) * mm});
            skArc(sketch, "E2094", {"start": v(45.4, 43.67) * mm, "mid": v(45.34, 43.73) * mm, "end": v(45.27, 43.67) * mm});
            skArc(sketch, "E2095", {"start": v(40.39, 51.39) * mm, "mid": v(40.45, 51.32) * mm, "end": v(40.51, 51.39) * mm});
            skArc(sketch, "E2096", {"start": v(40.51, 51.39) * mm, "mid": v(40.45, 51.45) * mm, "end": v(40.39, 51.39) * mm});
            skArc(sketch, "E2097", {"start": v(33.78, 54.09) * mm, "mid": v(33.85, 54.03) * mm, "end": v(33.9, 54.09) * mm});
            skArc(sketch, "E2098", {"start": v(33.9, 54.09) * mm, "mid": v(33.85, 54.15) * mm, "end": v(33.78, 54.09) * mm});
            skArc(sketch, "E2099", {"start": v(45.9, 43.47) * mm, "mid": v(45.97, 43.4) * mm, "end": v(46.03, 43.47) * mm});
            skArc(sketch, "E2100", {"start": v(46.03, 43.47) * mm, "mid": v(45.97, 43.53) * mm, "end": v(45.9, 43.47) * mm});
            skArc(sketch, "E2101", {"start": v(38.42, 75.59) * mm, "mid": v(38.48, 75.52) * mm, "end": v(38.54, 75.59) * mm});
            skArc(sketch, "E2102", {"start": v(38.54, 75.59) * mm, "mid": v(38.48, 75.65) * mm, "end": v(38.42, 75.59) * mm});
            skArc(sketch, "E2103", {"start": v(44.8, 46) * mm, "mid": v(44.86, 45.95) * mm, "end": v(44.92, 46) * mm});
            skArc(sketch, "E2104", {"start": v(44.92, 46) * mm, "mid": v(44.86, 46.07) * mm, "end": v(44.8, 46) * mm});
            skArc(sketch, "E2105", {"start": v(40.9, 51.39) * mm, "mid": v(40.96, 51.32) * mm, "end": v(41.02, 51.39) * mm});
            skArc(sketch, "E2106", {"start": v(41.02, 51.39) * mm, "mid": v(40.96, 51.45) * mm, "end": v(40.9, 51.39) * mm});
            skArc(sketch, "E2107", {"start": v(34.27, 56.78) * mm, "mid": v(34.34, 56.71) * mm, "end": v(34.4, 56.78) * mm});
            skArc(sketch, "E2108", {"start": v(34.4, 56.78) * mm, "mid": v(34.34, 56.84) * mm, "end": v(34.27, 56.78) * mm});
            skArc(sketch, "E2109", {"start": v(45.1, 45.55) * mm, "mid": v(45.16, 45.49) * mm, "end": v(45.22, 45.55) * mm});
            skArc(sketch, "E2110", {"start": v(45.22, 45.55) * mm, "mid": v(45.16, 45.62) * mm, "end": v(45.1, 45.55) * mm});
            skArc(sketch, "E2111", {"start": v(40.9, 49.89) * mm, "mid": v(40.97, 49.82) * mm, "end": v(41.03, 49.89) * mm});
            skArc(sketch, "E2112", {"start": v(41.03, 49.89) * mm, "mid": v(40.97, 49.95) * mm, "end": v(40.9, 49.89) * mm});
            skArc(sketch, "E2113", {"start": v(29.73, 49.9) * mm, "mid": v(29.8, 49.83) * mm, "end": v(29.86, 49.9) * mm});
            skArc(sketch, "E2114", {"start": v(29.86, 49.9) * mm, "mid": v(29.8, 49.95) * mm, "end": v(29.73, 49.9) * mm});
            skArc(sketch, "E2115", {"start": v(45.52, 45.14) * mm, "mid": v(45.59, 45.07) * mm, "end": v(45.65, 45.14) * mm});
            skArc(sketch, "E2116", {"start": v(45.65, 45.14) * mm, "mid": v(45.59, 45.2) * mm, "end": v(45.52, 45.14) * mm});
            skArc(sketch, "E2117", {"start": v(41.43, 54.09) * mm, "mid": v(41.5, 54.02) * mm, "end": v(41.55, 54.09) * mm});
            skArc(sketch, "E2118", {"start": v(41.55, 54.09) * mm, "mid": v(41.5, 54.15) * mm, "end": v(41.43, 54.09) * mm});
            skArc(sketch, "E2119", {"start": v(33.28, 52.6) * mm, "mid": v(33.35, 52.53) * mm, "end": v(33.4, 52.6) * mm});
            skArc(sketch, "E2120", {"start": v(33.4, 52.6) * mm, "mid": v(33.35, 52.65) * mm, "end": v(33.28, 52.6) * mm});
            skArc(sketch, "E2121", {"start": v(46.03, 44.9) * mm, "mid": v(46.1, 44.85) * mm, "end": v(46.16, 44.9) * mm});
            skArc(sketch, "E2122", {"start": v(46.16, 44.9) * mm, "mid": v(46.1, 44.97) * mm, "end": v(46.03, 44.9) * mm});
            skArc(sketch, "E2123", {"start": v(39.67, 74.68) * mm, "mid": v(39.73, 74.62) * mm, "end": v(39.8, 74.68) * mm});
            skArc(sketch, "E2124", {"start": v(39.8, 74.68) * mm, "mid": v(39.73, 74.75) * mm, "end": v(39.67, 74.68) * mm});
            skArc(sketch, "E2125", {"start": v(44.67, 46.46) * mm, "mid": v(44.74, 46.4) * mm, "end": v(44.8, 46.46) * mm});
            skArc(sketch, "E2126", {"start": v(44.8, 46.46) * mm, "mid": v(44.74, 46.53) * mm, "end": v(44.67, 46.46) * mm});
            skArc(sketch, "E2127", {"start": v(38.77, 76.02) * mm, "mid": v(38.84, 75.96) * mm, "end": v(38.9, 76.02) * mm});
            skArc(sketch, "E2128", {"start": v(38.9, 76.02) * mm, "mid": v(38.84, 76.08) * mm, "end": v(38.77, 76.02) * mm});
            skArc(sketch, "E2129", {"start": v(44.67, 47.99) * mm, "mid": v(44.74, 47.92) * mm, "end": v(44.8, 47.99) * mm});
            skArc(sketch, "E2130", {"start": v(44.8, 47.99) * mm, "mid": v(44.74, 48.05) * mm, "end": v(44.67, 47.99) * mm});
            skArc(sketch, "E2131", {"start": v(40.4, 49.89) * mm, "mid": v(40.46, 49.82) * mm, "end": v(40.52, 49.89) * mm});
            skArc(sketch, "E2132", {"start": v(40.52, 49.89) * mm, "mid": v(40.46, 49.95) * mm, "end": v(40.4, 49.89) * mm});
            skArc(sketch, "E2133", {"start": v(34.28, 55.28) * mm, "mid": v(34.35, 55.21) * mm, "end": v(34.41, 55.28) * mm});
            skArc(sketch, "E2134", {"start": v(34.41, 55.28) * mm, "mid": v(34.35, 55.34) * mm, "end": v(34.28, 55.28) * mm});
            skArc(sketch, "E2135", {"start": v(44.67, 47.48) * mm, "mid": v(44.74, 47.42) * mm, "end": v(44.8, 47.48) * mm});
            skArc(sketch, "E2136", {"start": v(44.8, 47.48) * mm, "mid": v(44.74, 47.54) * mm, "end": v(44.67, 47.48) * mm});
            skArc(sketch, "E2137", {"start": v(40.39, 54.09) * mm, "mid": v(40.45, 54.02) * mm, "end": v(40.51, 54.09) * mm});
            skArc(sketch, "E2138", {"start": v(40.51, 54.09) * mm, "mid": v(40.45, 54.15) * mm, "end": v(40.39, 54.09) * mm});
            skArc(sketch, "E2139", {"start": v(35.82, 52.6) * mm, "mid": v(35.89, 52.53) * mm, "end": v(35.95, 52.6) * mm});
            skArc(sketch, "E2140", {"start": v(35.95, 52.6) * mm, "mid": v(35.89, 52.65) * mm, "end": v(35.82, 52.6) * mm});
            skArc(sketch, "E2141", {"start": v(44.67, 46.97) * mm, "mid": v(44.74, 46.9) * mm, "end": v(44.8, 46.97) * mm});
            skArc(sketch, "E2142", {"start": v(44.8, 46.97) * mm, "mid": v(44.74, 47.04) * mm, "end": v(44.67, 46.97) * mm});
            skArc(sketch, "E2143", {"start": v(31.75, 51.39) * mm, "mid": v(31.81, 51.33) * mm, "end": v(31.88, 51.39) * mm});
            skArc(sketch, "E2144", {"start": v(31.88, 51.39) * mm, "mid": v(31.81, 51.45) * mm, "end": v(31.75, 51.39) * mm});
            skArc(sketch, "E2145", {"start": v(39.42, 74.18) * mm, "mid": v(39.48, 74.11) * mm, "end": v(39.54, 74.18) * mm});
            skArc(sketch, "E2146", {"start": v(39.54, 74.18) * mm, "mid": v(39.48, 74.24) * mm, "end": v(39.42, 74.18) * mm});
            skArc(sketch, "E2147", {"start": v(45.06, 28.93) * mm, "mid": v(45.13, 28.86) * mm, "end": v(45.19, 28.93) * mm});
            skArc(sketch, "E2148", {"start": v(45.19, 28.93) * mm, "mid": v(45.13, 28.99) * mm, "end": v(45.06, 28.93) * mm});
            skArc(sketch, "E2149", {"start": v(33.28, 49.9) * mm, "mid": v(33.35, 49.83) * mm, "end": v(33.41, 49.9) * mm});
            skArc(sketch, "E2150", {"start": v(33.41, 49.9) * mm, "mid": v(33.35, 49.95) * mm, "end": v(33.28, 49.9) * mm});
            skArc(sketch, "E2151", {"start": v(45.57, 28.93) * mm, "mid": v(45.63, 28.86) * mm, "end": v(45.7, 28.93) * mm});
            skArc(sketch, "E2152", {"start": v(45.7, 28.93) * mm, "mid": v(45.63, 28.99) * mm, "end": v(45.57, 28.93) * mm});
            skArc(sketch, "E2153", {"start": v(35.32, 49.9) * mm, "mid": v(35.38, 49.83) * mm, "end": v(35.44, 49.9) * mm});
            skArc(sketch, "E2154", {"start": v(35.44, 49.9) * mm, "mid": v(35.38, 49.95) * mm, "end": v(35.32, 49.9) * mm});
            skArc(sketch, "E2155", {"start": v(46.08, 28.93) * mm, "mid": v(46.14, 28.86) * mm, "end": v(46.2, 28.93) * mm});
            skArc(sketch, "E2156", {"start": v(46.2, 28.93) * mm, "mid": v(46.14, 28.99) * mm, "end": v(46.08, 28.93) * mm});
            skArc(sketch, "E2157", {"start": v(46.03, 75.46) * mm, "mid": v(46.1, 75.4) * mm, "end": v(46.16, 75.46) * mm});
            skArc(sketch, "E2158", {"start": v(46.16, 75.46) * mm, "mid": v(46.1, 75.52) * mm, "end": v(46.03, 75.46) * mm});
            skArc(sketch, "E2159", {"start": v(44.55, 28.93) * mm, "mid": v(44.62, 28.86) * mm, "end": v(44.68, 28.93) * mm});
            skArc(sketch, "E2160", {"start": v(44.68, 28.93) * mm, "mid": v(44.62, 28.99) * mm, "end": v(44.55, 28.93) * mm});
            skArc(sketch, "E2161", {"start": v(44.56, 27.43) * mm, "mid": v(44.63, 27.37) * mm, "end": v(44.69, 27.43) * mm});
            skArc(sketch, "E2162", {"start": v(44.69, 27.43) * mm, "mid": v(44.63, 27.5) * mm, "end": v(44.56, 27.43) * mm});
            skArc(sketch, "E2163", {"start": v(46.09, 27.43) * mm, "mid": v(46.15, 27.37) * mm, "end": v(46.21, 27.43) * mm});
            skArc(sketch, "E2164", {"start": v(46.21, 27.43) * mm, "mid": v(46.15, 27.5) * mm, "end": v(46.09, 27.43) * mm});
            skArc(sketch, "E2165", {"start": v(45.58, 27.43) * mm, "mid": v(45.64, 27.37) * mm, "end": v(45.7, 27.43) * mm});
            skArc(sketch, "E2166", {"start": v(45.7, 27.43) * mm, "mid": v(45.64, 27.5) * mm, "end": v(45.58, 27.43) * mm});
            skArc(sketch, "E2167", {"start": v(45.07, 27.43) * mm, "mid": v(45.13, 27.37) * mm, "end": v(45.2, 27.43) * mm});
            skArc(sketch, "E2168", {"start": v(45.2, 27.43) * mm, "mid": v(45.13, 27.5) * mm, "end": v(45.07, 27.43) * mm});
            skArc(sketch, "E2169", {"start": v(3.7, 83.78) * mm, "mid": v(3.83, 83.65) * mm, "end": v(3.95, 83.78) * mm});
            skArc(sketch, "E2170", {"start": v(3.95, 83.78) * mm, "mid": v(3.83, 83.9) * mm, "end": v(3.7, 83.78) * mm});
            skArc(sketch, "E2171", {"start": v(37.82, 67.47) * mm, "mid": v(37.88, 67.4) * mm, "end": v(37.95, 67.47) * mm});
            skArc(sketch, "E2172", {"start": v(37.95, 67.47) * mm, "mid": v(37.88, 67.54) * mm, "end": v(37.82, 67.47) * mm});
            skArc(sketch, "E2173", {"start": v(48.58, 76.96) * mm, "mid": v(48.65, 76.9) * mm, "end": v(48.7, 76.96) * mm});
            skArc(sketch, "E2174", {"start": v(48.7, 76.96) * mm, "mid": v(48.65, 77.02) * mm, "end": v(48.58, 76.96) * mm});
            skArc(sketch, "E2175", {"start": v(33.26, 56.78) * mm, "mid": v(33.32, 56.71) * mm, "end": v(33.39, 56.78) * mm});
            skArc(sketch, "E2176", {"start": v(33.39, 56.78) * mm, "mid": v(33.32, 56.84) * mm, "end": v(33.26, 56.78) * mm});
            skArc(sketch, "E2177", {"start": v(48.07, 76.96) * mm, "mid": v(48.14, 76.9) * mm, "end": v(48.2, 76.96) * mm});
            skArc(sketch, "E2178", {"start": v(48.2, 76.96) * mm, "mid": v(48.14, 77.02) * mm, "end": v(48.07, 76.96) * mm});
            skArc(sketch, "E2179", {"start": v(43.56, 59.15) * mm, "mid": v(43.62, 59.08) * mm, "end": v(43.68, 59.15) * mm});
            skArc(sketch, "E2180", {"start": v(43.68, 59.15) * mm, "mid": v(43.62, 59.2) * mm, "end": v(43.56, 59.15) * mm});
            skArc(sketch, "E2181", {"start": v(47.57, 76.96) * mm, "mid": v(47.63, 76.9) * mm, "end": v(47.7, 76.96) * mm});
            skArc(sketch, "E2182", {"start": v(47.7, 76.96) * mm, "mid": v(47.63, 77.02) * mm, "end": v(47.57, 76.96) * mm});
            skArc(sketch, "E2183", {"start": v(44.86, 57.36) * mm, "mid": v(44.8, 57.43) * mm, "end": v(44.74, 57.36) * mm});
            skArc(sketch, "E2184", {"start": v(47.06, 76.96) * mm, "mid": v(47.12, 76.9) * mm, "end": v(47.19, 76.96) * mm});
            skArc(sketch, "E2185", {"start": v(47.19, 76.96) * mm, "mid": v(47.12, 77.02) * mm, "end": v(47.06, 76.96) * mm});
            skArc(sketch, "E2186", {"start": v(42.03, 52.67) * mm, "mid": v(42.1, 52.6) * mm, "end": v(42.15, 52.67) * mm});
            skArc(sketch, "E2187", {"start": v(42.15, 52.67) * mm, "mid": v(42.1, 52.73) * mm, "end": v(42.03, 52.67) * mm});
            skArc(sketch, "E2188", {"start": v(5.14, 16.32) * mm, "mid": v(5.27, 16.2) * mm, "end": v(5.4, 16.32) * mm});
            skArc(sketch, "E2189", {"start": v(5.4, 16.32) * mm, "mid": v(5.27, 16.45) * mm, "end": v(5.14, 16.32) * mm});
            skArc(sketch, "E2190", {"start": v(44, 59.78) * mm, "mid": v(44.06, 59.72) * mm, "end": v(44.13, 59.78) * mm});
            skArc(sketch, "E2191", {"start": v(44.13, 59.78) * mm, "mid": v(44.06, 59.85) * mm, "end": v(44, 59.78) * mm});
            skArc(sketch, "E2192", {"start": v(35.8, 56.78) * mm, "mid": v(35.86, 56.71) * mm, "end": v(35.93, 56.78) * mm});
            skArc(sketch, "E2193", {"start": v(35.93, 56.78) * mm, "mid": v(35.86, 56.84) * mm, "end": v(35.8, 56.78) * mm});
            skArc(sketch, "E2194", {"start": v(5.23, 83.76) * mm, "mid": v(5.36, 83.63) * mm, "end": v(5.49, 83.76) * mm});
            skArc(sketch, "E2195", {"start": v(5.49, 83.76) * mm, "mid": v(5.36, 83.89) * mm, "end": v(5.23, 83.76) * mm});
            skArc(sketch, "E2196", {"start": v(43.24, 57.37) * mm, "mid": v(43.3, 57.31) * mm, "end": v(43.37, 57.37) * mm});
            skArc(sketch, "E2197", {"start": v(43.37, 57.37) * mm, "mid": v(43.3, 57.44) * mm, "end": v(43.24, 57.37) * mm});
            skArc(sketch, "E2198", {"start": v(30.21, 56.78) * mm, "mid": v(30.27, 56.71) * mm, "end": v(30.34, 56.78) * mm});
            skArc(sketch, "E2199", {"start": v(30.34, 56.78) * mm, "mid": v(30.27, 56.84) * mm, "end": v(30.21, 56.78) * mm});
            skArc(sketch, "E2200", {"start": v(6.76, 83.76) * mm, "mid": v(6.89, 83.63) * mm, "end": v(7.01, 83.76) * mm});
            skArc(sketch, "E2201", {"start": v(7.01, 83.76) * mm, "mid": v(6.89, 83.89) * mm, "end": v(6.76, 83.76) * mm});
            skArc(sketch, "E2202", {"start": v(43.24, 55.85) * mm, "mid": v(43.3, 55.79) * mm, "end": v(43.37, 55.85) * mm});
            skArc(sketch, "E2203", {"start": v(43.37, 55.85) * mm, "mid": v(43.3, 55.91) * mm, "end": v(43.24, 55.85) * mm});
            skArc(sketch, "E2204", {"start": v(32.75, 56.78) * mm, "mid": v(32.81, 56.71) * mm, "end": v(32.88, 56.78) * mm});
            skArc(sketch, "E2205", {"start": v(32.88, 56.78) * mm, "mid": v(32.81, 56.84) * mm, "end": v(32.75, 56.78) * mm});
            skArc(sketch, "E2206", {"start": v(8.28, 83.76) * mm, "mid": v(8.4, 83.63) * mm, "end": v(8.54, 83.76) * mm});
            skArc(sketch, "E2207", {"start": v(8.54, 83.76) * mm, "mid": v(8.4, 83.89) * mm, "end": v(8.28, 83.76) * mm});
            skArc(sketch, "E2208", {"start": v(43.31, 58.5) * mm, "mid": v(43.38, 58.44) * mm, "end": v(43.44, 58.5) * mm});
            skArc(sketch, "E2209", {"start": v(43.44, 58.5) * mm, "mid": v(43.38, 58.56) * mm, "end": v(43.31, 58.5) * mm});
            skArc(sketch, "E2210", {"start": v(9.8, 83.76) * mm, "mid": v(9.93, 83.63) * mm, "end": v(10.06, 83.76) * mm});
            skArc(sketch, "E2211", {"start": v(10.06, 83.76) * mm, "mid": v(9.93, 83.89) * mm, "end": v(9.8, 83.76) * mm});
            skArc(sketch, "E2212", {"start": v(43.23, 57.95) * mm, "mid": v(43.3, 57.88) * mm, "end": v(43.36, 57.95) * mm});
            skArc(sketch, "E2213", {"start": v(43.36, 57.95) * mm, "mid": v(43.3, 58) * mm, "end": v(43.23, 57.95) * mm});
            skArc(sketch, "E2214", {"start": v(37.82, 62.4) * mm, "mid": v(37.88, 62.33) * mm, "end": v(37.95, 62.4) * mm});
            skArc(sketch, "E2215", {"start": v(37.95, 62.4) * mm, "mid": v(37.88, 62.46) * mm, "end": v(37.82, 62.4) * mm});
            skArc(sketch, "E2216", {"start": v(48.57, 75.46) * mm, "mid": v(48.64, 75.4) * mm, "end": v(48.7, 75.46) * mm});
            skArc(sketch, "E2217", {"start": v(48.7, 75.46) * mm, "mid": v(48.64, 75.52) * mm, "end": v(48.57, 75.46) * mm});
            skArc(sketch, "E2218", {"start": v(48.07, 75.46) * mm, "mid": v(48.13, 75.4) * mm, "end": v(48.2, 75.46) * mm});
            skArc(sketch, "E2219", {"start": v(48.2, 75.46) * mm, "mid": v(48.13, 75.52) * mm, "end": v(48.07, 75.46) * mm});
            skArc(sketch, "E2220", {"start": v(47.56, 75.46) * mm, "mid": v(47.62, 75.4) * mm, "end": v(47.69, 75.46) * mm});
            skArc(sketch, "E2221", {"start": v(47.69, 75.46) * mm, "mid": v(47.62, 75.52) * mm, "end": v(47.56, 75.46) * mm});
            skArc(sketch, "E2222", {"start": v(47.05, 75.46) * mm, "mid": v(47.11, 75.4) * mm, "end": v(47.18, 75.46) * mm});
            skArc(sketch, "E2223", {"start": v(47.18, 75.46) * mm, "mid": v(47.11, 75.52) * mm, "end": v(47.05, 75.46) * mm});
            skArc(sketch, "E2224", {"start": v(11.33, 83.76) * mm, "mid": v(11.46, 83.63) * mm, "end": v(11.58, 83.76) * mm});
            skArc(sketch, "E2225", {"start": v(11.58, 83.76) * mm, "mid": v(11.46, 83.89) * mm, "end": v(11.33, 83.76) * mm});
            skArc(sketch, "E2226", {"start": v(12.85, 83.76) * mm, "mid": v(12.98, 83.63) * mm, "end": v(13.1, 83.76) * mm});
            skArc(sketch, "E2227", {"start": v(13.1, 83.76) * mm, "mid": v(12.98, 83.89) * mm, "end": v(12.85, 83.76) * mm});
            skArc(sketch, "E2228", {"start": v(14.38, 83.76) * mm, "mid": v(14.5, 83.63) * mm, "end": v(14.63, 83.76) * mm});
            skArc(sketch, "E2229", {"start": v(14.63, 83.76) * mm, "mid": v(14.5, 83.89) * mm, "end": v(14.38, 83.76) * mm});
            skArc(sketch, "E2230", {"start": v(15.9, 83.76) * mm, "mid": v(16.03, 83.63) * mm, "end": v(16.16, 83.76) * mm});
            skArc(sketch, "E2231", {"start": v(16.16, 83.76) * mm, "mid": v(16.03, 83.89) * mm, "end": v(15.9, 83.76) * mm});
            skArc(sketch, "E2232", {"start": v(17.43, 83.76) * mm, "mid": v(17.55, 83.63) * mm, "end": v(17.68, 83.76) * mm});
            skArc(sketch, "E2233", {"start": v(17.68, 83.76) * mm, "mid": v(17.55, 83.89) * mm, "end": v(17.43, 83.76) * mm});
            skArc(sketch, "E2234", {"start": v(18.95, 83.76) * mm, "mid": v(19.08, 83.63) * mm, "end": v(19.2, 83.76) * mm});
            skArc(sketch, "E2235", {"start": v(19.2, 83.76) * mm, "mid": v(19.08, 83.89) * mm, "end": v(18.95, 83.76) * mm});
            skArc(sketch, "E2236", {"start": v(20.47, 83.76) * mm, "mid": v(20.6, 83.63) * mm, "end": v(20.73, 83.76) * mm});
            skArc(sketch, "E2237", {"start": v(20.73, 83.76) * mm, "mid": v(20.6, 83.89) * mm, "end": v(20.47, 83.76) * mm});
            skArc(sketch, "E2238", {"start": v(47.05, 60.9) * mm, "mid": v(47.11, 60.84) * mm, "end": v(47.18, 60.9) * mm});
            skArc(sketch, "E2239", {"start": v(47.18, 60.9) * mm, "mid": v(47.11, 60.97) * mm, "end": v(47.05, 60.9) * mm});
            skArc(sketch, "E2240", {"start": v(47.56, 60.9) * mm, "mid": v(47.62, 60.84) * mm, "end": v(47.69, 60.9) * mm});
            skArc(sketch, "E2241", {"start": v(47.69, 60.9) * mm, "mid": v(47.62, 60.97) * mm, "end": v(47.56, 60.9) * mm});
            skArc(sketch, "E2242", {"start": v(48.57, 60.9) * mm, "mid": v(48.64, 60.84) * mm, "end": v(48.7, 60.9) * mm});
            skArc(sketch, "E2243", {"start": v(48.7, 60.9) * mm, "mid": v(48.64, 60.97) * mm, "end": v(48.57, 60.9) * mm});
            skArc(sketch, "E2244", {"start": v(22, 83.76) * mm, "mid": v(22.13, 83.63) * mm, "end": v(22.25, 83.76) * mm});
            skArc(sketch, "E2245", {"start": v(22.25, 83.76) * mm, "mid": v(22.13, 83.89) * mm, "end": v(22, 83.76) * mm});
            skArc(sketch, "E2246", {"start": v(48.56, 59.4) * mm, "mid": v(48.63, 59.34) * mm, "end": v(48.7, 59.4) * mm});
            skArc(sketch, "E2247", {"start": v(48.7, 59.4) * mm, "mid": v(48.63, 59.47) * mm, "end": v(48.56, 59.4) * mm});
            skArc(sketch, "E2248", {"start": v(48.56, 43.38) * mm, "mid": v(48.63, 43.32) * mm, "end": v(48.7, 43.38) * mm});
            skArc(sketch, "E2249", {"start": v(48.7, 43.38) * mm, "mid": v(48.63, 43.44) * mm, "end": v(48.56, 43.38) * mm});
            skArc(sketch, "E2250", {"start": v(33.8, 47.24) * mm, "mid": v(33.86, 47.18) * mm, "end": v(33.92, 47.24) * mm});
            skArc(sketch, "E2251", {"start": v(33.92, 47.24) * mm, "mid": v(33.86, 47.3) * mm, "end": v(33.8, 47.24) * mm});
            skArc(sketch, "E2252", {"start": v(31.73, 56.78) * mm, "mid": v(31.8, 56.71) * mm, "end": v(31.86, 56.78) * mm});
            skArc(sketch, "E2253", {"start": v(31.86, 56.78) * mm, "mid": v(31.8, 56.84) * mm, "end": v(31.73, 56.78) * mm});
            skArc(sketch, "E2254", {"start": v(48.57, 44.88) * mm, "mid": v(48.64, 44.81) * mm, "end": v(48.7, 44.88) * mm});
            skArc(sketch, "E2255", {"start": v(48.7, 44.88) * mm, "mid": v(48.64, 44.94) * mm, "end": v(48.57, 44.88) * mm});
            skArc(sketch, "E2256", {"start": v(32.27, 47.24) * mm, "mid": v(32.33, 47.18) * mm, "end": v(32.4, 47.24) * mm});
            skArc(sketch, "E2257", {"start": v(32.4, 47.24) * mm, "mid": v(32.33, 47.3) * mm, "end": v(32.27, 47.24) * mm});
            skArc(sketch, "E2258", {"start": v(48.62, 28.93) * mm, "mid": v(48.68, 28.86) * mm, "end": v(48.75, 28.93) * mm});
            skArc(sketch, "E2259", {"start": v(48.75, 28.93) * mm, "mid": v(48.68, 28.99) * mm, "end": v(48.62, 28.93) * mm});
            skArc(sketch, "E2260", {"start": v(31.23, 56.78) * mm, "mid": v(31.3, 56.71) * mm, "end": v(31.35, 56.78) * mm});
            skArc(sketch, "E2261", {"start": v(31.35, 56.78) * mm, "mid": v(31.3, 56.84) * mm, "end": v(31.23, 56.78) * mm});
            skArc(sketch, "E2262", {"start": v(47.56, 44.88) * mm, "mid": v(47.62, 44.81) * mm, "end": v(47.69, 44.88) * mm});
            skArc(sketch, "E2263", {"start": v(47.69, 44.88) * mm, "mid": v(47.62, 44.94) * mm, "end": v(47.56, 44.88) * mm});
            skArc(sketch, "E2264", {"start": v(23.52, 83.76) * mm, "mid": v(23.65, 83.63) * mm, "end": v(23.78, 83.76) * mm});
            skArc(sketch, "E2265", {"start": v(23.78, 83.76) * mm, "mid": v(23.65, 83.89) * mm, "end": v(23.52, 83.76) * mm});
            skArc(sketch, "E2266", {"start": v(32.77, 48.74) * mm, "mid": v(32.83, 48.67) * mm, "end": v(32.9, 48.74) * mm});
            skArc(sketch, "E2267", {"start": v(32.9, 48.74) * mm, "mid": v(32.83, 48.8) * mm, "end": v(32.77, 48.74) * mm});
            skArc(sketch, "E2268", {"start": v(47.55, 59.4) * mm, "mid": v(47.61, 59.34) * mm, "end": v(47.68, 59.4) * mm});
            skArc(sketch, "E2269", {"start": v(47.68, 59.4) * mm, "mid": v(47.61, 59.47) * mm, "end": v(47.55, 59.4) * mm});
            skArc(sketch, "E2270", {"start": v(47.6, 28.93) * mm, "mid": v(47.67, 28.86) * mm, "end": v(47.73, 28.93) * mm});
            skArc(sketch, "E2271", {"start": v(47.73, 28.93) * mm, "mid": v(47.67, 28.99) * mm, "end": v(47.6, 28.93) * mm});
            skArc(sketch, "E2272", {"start": v(35.8, 55.28) * mm, "mid": v(35.87, 55.21) * mm, "end": v(35.94, 55.28) * mm});
            skArc(sketch, "E2273", {"start": v(35.94, 55.28) * mm, "mid": v(35.87, 55.34) * mm, "end": v(35.8, 55.28) * mm});
            skArc(sketch, "E2274", {"start": v(47.6, 27.43) * mm, "mid": v(47.67, 27.37) * mm, "end": v(47.74, 27.43) * mm});
            skArc(sketch, "E2275", {"start": v(47.74, 27.43) * mm, "mid": v(47.67, 27.5) * mm, "end": v(47.6, 27.43) * mm});
            skArc(sketch, "E2276", {"start": v(33.27, 51.39) * mm, "mid": v(33.34, 51.33) * mm, "end": v(33.4, 51.39) * mm});
            skArc(sketch, "E2277", {"start": v(33.4, 51.39) * mm, "mid": v(33.34, 51.45) * mm, "end": v(33.27, 51.39) * mm});
            skArc(sketch, "E2278", {"start": v(25.05, 83.76) * mm, "mid": v(25.17, 83.63) * mm, "end": v(25.3, 83.76) * mm});
            skArc(sketch, "E2279", {"start": v(25.3, 83.76) * mm, "mid": v(25.17, 83.89) * mm, "end": v(25.05, 83.76) * mm});
            skArc(sketch, "E2280", {"start": v(47.05, 44.88) * mm, "mid": v(47.11, 44.81) * mm, "end": v(47.18, 44.88) * mm});
            skArc(sketch, "E2281", {"start": v(47.18, 44.88) * mm, "mid": v(47.11, 44.94) * mm, "end": v(47.05, 44.88) * mm});
            skArc(sketch, "E2282", {"start": v(32.78, 47.24) * mm, "mid": v(32.84, 47.18) * mm, "end": v(32.9, 47.24) * mm});
            skArc(sketch, "E2283", {"start": v(32.9, 47.24) * mm, "mid": v(32.84, 47.3) * mm, "end": v(32.78, 47.24) * mm});
            skArc(sketch, "E2284", {"start": v(47.04, 43.38) * mm, "mid": v(47.1, 43.32) * mm, "end": v(47.17, 43.38) * mm});
            skArc(sketch, "E2285", {"start": v(47.17, 43.38) * mm, "mid": v(47.1, 43.44) * mm, "end": v(47.04, 43.38) * mm});
            skArc(sketch, "E2286", {"start": v(34.81, 47.24) * mm, "mid": v(34.87, 47.18) * mm, "end": v(34.94, 47.24) * mm});
            skArc(sketch, "E2287", {"start": v(34.94, 47.24) * mm, "mid": v(34.87, 47.3) * mm, "end": v(34.81, 47.24) * mm});
            skArc(sketch, "E2288", {"start": v(48.63, 27.48) * mm, "mid": v(48.69, 27.42) * mm, "end": v(48.75, 27.48) * mm});
            skArc(sketch, "E2289", {"start": v(48.75, 27.48) * mm, "mid": v(48.69, 27.54) * mm, "end": v(48.63, 27.48) * mm});
            skArc(sketch, "E2290", {"start": v(34.8, 49.9) * mm, "mid": v(34.87, 49.83) * mm, "end": v(34.94, 49.9) * mm});
            skArc(sketch, "E2291", {"start": v(34.94, 49.9) * mm, "mid": v(34.87, 49.95) * mm, "end": v(34.8, 49.9) * mm});
            skArc(sketch, "E2292", {"start": v(47.04, 59.4) * mm, "mid": v(47.1, 59.34) * mm, "end": v(47.17, 59.4) * mm});
            skArc(sketch, "E2293", {"start": v(47.17, 59.4) * mm, "mid": v(47.1, 59.47) * mm, "end": v(47.04, 59.4) * mm});
            skArc(sketch, "E2294", {"start": v(47.1, 28.93) * mm, "mid": v(47.16, 28.86) * mm, "end": v(47.22, 28.93) * mm});
            skArc(sketch, "E2295", {"start": v(47.22, 28.93) * mm, "mid": v(47.16, 28.99) * mm, "end": v(47.1, 28.93) * mm});
            skArc(sketch, "E2296", {"start": v(32.76, 55.28) * mm, "mid": v(32.82, 55.21) * mm, "end": v(32.89, 55.28) * mm});
            skArc(sketch, "E2297", {"start": v(32.89, 55.28) * mm, "mid": v(32.82, 55.34) * mm, "end": v(32.76, 55.28) * mm});
            skArc(sketch, "E2298", {"start": v(47.1, 27.43) * mm, "mid": v(47.17, 27.37) * mm, "end": v(47.23, 27.43) * mm});
            skArc(sketch, "E2299", {"start": v(47.23, 27.43) * mm, "mid": v(47.17, 27.5) * mm, "end": v(47.1, 27.43) * mm});
            skArc(sketch, "E2300", {"start": v(31.24, 54.09) * mm, "mid": v(31.3, 54.03) * mm, "end": v(31.37, 54.09) * mm});
            skArc(sketch, "E2301", {"start": v(31.37, 54.09) * mm, "mid": v(31.3, 54.15) * mm, "end": v(31.24, 54.09) * mm});
            skArc(sketch, "E2302", {"start": v(48.07, 44.88) * mm, "mid": v(48.13, 44.81) * mm, "end": v(48.2, 44.88) * mm});
            skArc(sketch, "E2303", {"start": v(48.2, 44.88) * mm, "mid": v(48.13, 44.94) * mm, "end": v(48.07, 44.88) * mm});
            skArc(sketch, "E2304", {"start": v(34.3, 52.6) * mm, "mid": v(34.36, 52.53) * mm, "end": v(34.42, 52.6) * mm});
            skArc(sketch, "E2305", {"start": v(34.42, 52.6) * mm, "mid": v(34.36, 52.65) * mm, "end": v(34.3, 52.6) * mm});
            skArc(sketch, "E2306", {"start": v(33.28, 48.74) * mm, "mid": v(33.34, 48.67) * mm, "end": v(33.4, 48.74) * mm});
            skArc(sketch, "E2307", {"start": v(33.4, 48.74) * mm, "mid": v(33.34, 48.8) * mm, "end": v(33.28, 48.74) * mm});
            skArc(sketch, "E2308", {"start": v(48.06, 43.38) * mm, "mid": v(48.12, 43.32) * mm, "end": v(48.18, 43.38) * mm});
            skArc(sketch, "E2309", {"start": v(48.18, 43.38) * mm, "mid": v(48.12, 43.44) * mm, "end": v(48.06, 43.38) * mm});
            skArc(sketch, "E2310", {"start": v(35.83, 47.24) * mm, "mid": v(35.9, 47.18) * mm, "end": v(35.95, 47.24) * mm});
            skArc(sketch, "E2311", {"start": v(35.95, 47.24) * mm, "mid": v(35.9, 47.3) * mm, "end": v(35.83, 47.24) * mm});
            skArc(sketch, "E2312", {"start": v(48.06, 59.4) * mm, "mid": v(48.12, 59.34) * mm, "end": v(48.18, 59.4) * mm});
            skArc(sketch, "E2313", {"start": v(48.18, 59.4) * mm, "mid": v(48.12, 59.47) * mm, "end": v(48.06, 59.4) * mm});
            skArc(sketch, "E2314", {"start": v(26.57, 83.76) * mm, "mid": v(26.7, 83.63) * mm, "end": v(26.82, 83.76) * mm});
            skArc(sketch, "E2315", {"start": v(26.82, 83.76) * mm, "mid": v(26.7, 83.89) * mm, "end": v(26.57, 83.76) * mm});
            skArc(sketch, "E2316", {"start": v(48.11, 28.93) * mm, "mid": v(48.17, 28.86) * mm, "end": v(48.24, 28.93) * mm});
            skArc(sketch, "E2317", {"start": v(48.24, 28.93) * mm, "mid": v(48.17, 28.99) * mm, "end": v(48.11, 28.93) * mm});
            skArc(sketch, "E2318", {"start": v(35.3, 55.28) * mm, "mid": v(35.36, 55.21) * mm, "end": v(35.43, 55.28) * mm});
            skArc(sketch, "E2319", {"start": v(35.43, 55.28) * mm, "mid": v(35.36, 55.34) * mm, "end": v(35.3, 55.28) * mm});
            skArc(sketch, "E2320", {"start": v(28.1, 83.76) * mm, "mid": v(28.22, 83.63) * mm, "end": v(28.35, 83.76) * mm});
            skArc(sketch, "E2321", {"start": v(28.35, 83.76) * mm, "mid": v(28.22, 83.89) * mm, "end": v(28.1, 83.76) * mm});
            skArc(sketch, "E2322", {"start": v(29.62, 83.76) * mm, "mid": v(29.75, 83.63) * mm, "end": v(29.87, 83.76) * mm});
            skArc(sketch, "E2323", {"start": v(29.87, 83.76) * mm, "mid": v(29.75, 83.89) * mm, "end": v(29.62, 83.76) * mm});
            skArc(sketch, "E2324", {"start": v(31.14, 83.76) * mm, "mid": v(31.27, 83.63) * mm, "end": v(31.4, 83.76) * mm});
            skArc(sketch, "E2325", {"start": v(31.4, 83.76) * mm, "mid": v(31.27, 83.89) * mm, "end": v(31.14, 83.76) * mm});
            skArc(sketch, "E2326", {"start": v(32.67, 83.76) * mm, "mid": v(32.8, 83.63) * mm, "end": v(32.92, 83.76) * mm});
            skArc(sketch, "E2327", {"start": v(32.92, 83.76) * mm, "mid": v(32.8, 83.89) * mm, "end": v(32.67, 83.76) * mm});
            skArc(sketch, "E2328", {"start": v(34.2, 83.76) * mm, "mid": v(34.32, 83.63) * mm, "end": v(34.44, 83.76) * mm});
            skArc(sketch, "E2329", {"start": v(34.44, 83.76) * mm, "mid": v(34.32, 83.89) * mm, "end": v(34.2, 83.76) * mm});
            skArc(sketch, "E2330", {"start": v(35.71, 83.76) * mm, "mid": v(35.84, 83.63) * mm, "end": v(35.97, 83.76) * mm});
            skArc(sketch, "E2331", {"start": v(35.97, 83.76) * mm, "mid": v(35.84, 83.89) * mm, "end": v(35.71, 83.76) * mm});
            skArc(sketch, "E2332", {"start": v(37.24, 83.76) * mm, "mid": v(37.37, 83.63) * mm, "end": v(37.5, 83.76) * mm});
            skArc(sketch, "E2333", {"start": v(37.5, 83.76) * mm, "mid": v(37.37, 83.89) * mm, "end": v(37.24, 83.76) * mm});
            skArc(sketch, "E2334", {"start": v(38.76, 83.76) * mm, "mid": v(38.89, 83.63) * mm, "end": v(39.02, 83.76) * mm});
            skArc(sketch, "E2335", {"start": v(39.02, 83.76) * mm, "mid": v(38.89, 83.89) * mm, "end": v(38.76, 83.76) * mm});
            skArc(sketch, "E2336", {"start": v(30.75, 47.24) * mm, "mid": v(30.81, 47.18) * mm, "end": v(30.87, 47.24) * mm});
            skArc(sketch, "E2337", {"start": v(30.87, 47.24) * mm, "mid": v(30.81, 47.3) * mm, "end": v(30.75, 47.24) * mm});
            skArc(sketch, "E2338", {"start": v(29.7, 56.78) * mm, "mid": v(29.77, 56.71) * mm, "end": v(29.83, 56.78) * mm});
            skArc(sketch, "E2339", {"start": v(29.83, 56.78) * mm, "mid": v(29.77, 56.84) * mm, "end": v(29.7, 56.78) * mm});
            skArc(sketch, "E2340", {"start": v(40.29, 83.76) * mm, "mid": v(40.41, 83.63) * mm, "end": v(40.54, 83.76) * mm});
            skArc(sketch, "E2341", {"start": v(40.54, 83.76) * mm, "mid": v(40.41, 83.89) * mm, "end": v(40.29, 83.76) * mm});
            skArc(sketch, "E2342", {"start": v(31.75, 48.74) * mm, "mid": v(31.82, 48.67) * mm, "end": v(31.88, 48.74) * mm});
            skArc(sketch, "E2343", {"start": v(31.88, 48.74) * mm, "mid": v(31.82, 48.8) * mm, "end": v(31.75, 48.74) * mm});
            skArc(sketch, "E2344", {"start": v(41.81, 83.76) * mm, "mid": v(41.94, 83.63) * mm, "end": v(42.06, 83.76) * mm});
            skArc(sketch, "E2345", {"start": v(42.06, 83.76) * mm, "mid": v(41.94, 83.89) * mm, "end": v(41.81, 83.76) * mm});
            skArc(sketch, "E2346", {"start": v(39.32, 68.99) * mm, "mid": v(39.38, 68.93) * mm, "end": v(39.44, 68.99) * mm});
            skArc(sketch, "E2347", {"start": v(39.44, 68.99) * mm, "mid": v(39.38, 69.05) * mm, "end": v(39.32, 68.99) * mm});
            skArc(sketch, "E2348", {"start": v(31.24, 48.74) * mm, "mid": v(31.3, 48.67) * mm, "end": v(31.37, 48.74) * mm});
            skArc(sketch, "E2349", {"start": v(31.37, 48.74) * mm, "mid": v(31.3, 48.8) * mm, "end": v(31.24, 48.74) * mm});
            skArc(sketch, "E2350", {"start": v(43.33, 83.76) * mm, "mid": v(43.46, 83.63) * mm, "end": v(43.59, 83.76) * mm});
            skArc(sketch, "E2351", {"start": v(43.59, 83.76) * mm, "mid": v(43.46, 83.89) * mm, "end": v(43.33, 83.76) * mm});
            skArc(sketch, "E2352", {"start": v(30.74, 48.74) * mm, "mid": v(30.8, 48.67) * mm, "end": v(30.86, 48.74) * mm});
            skArc(sketch, "E2353", {"start": v(30.86, 48.74) * mm, "mid": v(30.8, 48.8) * mm, "end": v(30.74, 48.74) * mm});
            skArc(sketch, "E2354", {"start": v(31.25, 49.9) * mm, "mid": v(31.32, 49.83) * mm, "end": v(31.38, 49.9) * mm});
            skArc(sketch, "E2355", {"start": v(31.38, 49.9) * mm, "mid": v(31.32, 49.95) * mm, "end": v(31.25, 49.9) * mm});
            skArc(sketch, "E2356", {"start": v(44.86, 83.76) * mm, "mid": v(44.99, 83.63) * mm, "end": v(45.11, 83.76) * mm});
            skArc(sketch, "E2357", {"start": v(45.11, 83.76) * mm, "mid": v(44.99, 83.89) * mm, "end": v(44.86, 83.76) * mm});
            skArc(sketch, "E2358", {"start": v(33.29, 47.24) * mm, "mid": v(33.35, 47.18) * mm, "end": v(33.41, 47.24) * mm});
            skArc(sketch, "E2359", {"start": v(33.41, 47.24) * mm, "mid": v(33.35, 47.3) * mm, "end": v(33.29, 47.24) * mm});
            skArc(sketch, "E2360", {"start": v(46.38, 83.76) * mm, "mid": v(46.5, 83.63) * mm, "end": v(46.64, 83.76) * mm});
            skArc(sketch, "E2361", {"start": v(46.64, 83.76) * mm, "mid": v(46.5, 83.89) * mm, "end": v(46.38, 83.76) * mm});
            skArc(sketch, "E2362", {"start": v(32.26, 48.74) * mm, "mid": v(32.32, 48.67) * mm, "end": v(32.39, 48.74) * mm});
            skArc(sketch, "E2363", {"start": v(32.39, 48.74) * mm, "mid": v(32.32, 48.8) * mm, "end": v(32.26, 48.74) * mm});
            skArc(sketch, "E2364", {"start": v(47.9, 83.76) * mm, "mid": v(48.03, 83.63) * mm, "end": v(48.16, 83.76) * mm});
            skArc(sketch, "E2365", {"start": v(48.16, 83.76) * mm, "mid": v(48.03, 83.89) * mm, "end": v(47.9, 83.76) * mm});
            skArc(sketch, "E2366", {"start": v(34.3, 47.24) * mm, "mid": v(34.37, 47.18) * mm, "end": v(34.43, 47.24) * mm});
            skArc(sketch, "E2367", {"start": v(34.43, 47.24) * mm, "mid": v(34.37, 47.3) * mm, "end": v(34.3, 47.24) * mm});
            skArc(sketch, "E2368", {"start": v(48.12, 27.43) * mm, "mid": v(48.18, 27.37) * mm, "end": v(48.24, 27.43) * mm});
            skArc(sketch, "E2369", {"start": v(48.24, 27.43) * mm, "mid": v(48.18, 27.5) * mm, "end": v(48.12, 27.43) * mm});
            skArc(sketch, "E2370", {"start": v(32.77, 51.39) * mm, "mid": v(32.83, 51.33) * mm, "end": v(32.9, 51.39) * mm});
            skArc(sketch, "E2371", {"start": v(32.9, 51.39) * mm, "mid": v(32.83, 51.45) * mm, "end": v(32.77, 51.39) * mm});
            skArc(sketch, "E2372", {"start": v(3.6, 16.34) * mm, "mid": v(3.74, 16.21) * mm, "end": v(3.86, 16.34) * mm});
            skArc(sketch, "E2373", {"start": v(3.86, 16.34) * mm, "mid": v(3.74, 16.47) * mm, "end": v(3.6, 16.34) * mm});
            skArc(sketch, "E2374", {"start": v(43, 76.96) * mm, "mid": v(43.06, 76.9) * mm, "end": v(43.12, 76.96) * mm});
            skArc(sketch, "E2375", {"start": v(43.12, 76.96) * mm, "mid": v(43.06, 77.02) * mm, "end": v(43, 76.96) * mm});
            skArc(sketch, "E2376", {"start": v(48.07, 60.9) * mm, "mid": v(48.13, 60.84) * mm, "end": v(48.2, 60.9) * mm});
            skArc(sketch, "E2377", {"start": v(48.2, 60.9) * mm, "mid": v(48.13, 60.97) * mm, "end": v(48.07, 60.9) * mm});
            skArc(sketch, "E2378", {"start": v(8.2, 16.32) * mm, "mid": v(8.32, 16.2) * mm, "end": v(8.45, 16.32) * mm});
            skArc(sketch, "E2379", {"start": v(8.45, 16.32) * mm, "mid": v(8.32, 16.45) * mm, "end": v(8.2, 16.32) * mm});
            skArc(sketch, "E2380", {"start": v(9.72, 16.32) * mm, "mid": v(9.84, 16.2) * mm, "end": v(9.97, 16.32) * mm});
            skArc(sketch, "E2381", {"start": v(9.97, 16.32) * mm, "mid": v(9.84, 16.45) * mm, "end": v(9.72, 16.32) * mm});
            skArc(sketch, "E2382", {"start": v(12.76, 16.32) * mm, "mid": v(12.9, 16.2) * mm, "end": v(13.02, 16.32) * mm});
            skArc(sketch, "E2383", {"start": v(13.02, 16.32) * mm, "mid": v(12.9, 16.45) * mm, "end": v(12.76, 16.32) * mm});
            skArc(sketch, "E2384", {"start": v(14.29, 16.32) * mm, "mid": v(14.41, 16.2) * mm, "end": v(14.54, 16.32) * mm});
            skArc(sketch, "E2385", {"start": v(14.54, 16.32) * mm, "mid": v(14.41, 16.45) * mm, "end": v(14.29, 16.32) * mm});
            skArc(sketch, "E2386", {"start": v(15.81, 16.32) * mm, "mid": v(15.94, 16.2) * mm, "end": v(16.07, 16.32) * mm});
            skArc(sketch, "E2387", {"start": v(16.07, 16.32) * mm, "mid": v(15.94, 16.45) * mm, "end": v(15.81, 16.32) * mm});
            skArc(sketch, "E2388", {"start": v(30.73, 51.39) * mm, "mid": v(30.8, 51.33) * mm, "end": v(30.86, 51.39) * mm});
            skArc(sketch, "E2389", {"start": v(30.86, 51.39) * mm, "mid": v(30.8, 51.45) * mm, "end": v(30.73, 51.39) * mm});
            skArc(sketch, "E2390", {"start": v(17.34, 16.32) * mm, "mid": v(17.46, 16.2) * mm, "end": v(17.59, 16.32) * mm});
            skArc(sketch, "E2391", {"start": v(17.59, 16.32) * mm, "mid": v(17.46, 16.45) * mm, "end": v(17.34, 16.32) * mm});
            skArc(sketch, "E2392", {"start": v(32.77, 52.6) * mm, "mid": v(32.84, 52.53) * mm, "end": v(32.9, 52.6) * mm});
            skArc(sketch, "E2393", {"start": v(32.9, 52.6) * mm, "mid": v(32.84, 52.65) * mm, "end": v(32.77, 52.6) * mm});
            skArc(sketch, "E2394", {"start": v(18.86, 16.32) * mm, "mid": v(18.99, 16.2) * mm, "end": v(19.11, 16.32) * mm});
            skArc(sketch, "E2395", {"start": v(19.11, 16.32) * mm, "mid": v(18.99, 16.45) * mm, "end": v(18.86, 16.32) * mm});
            skArc(sketch, "E2396", {"start": v(31.76, 49.9) * mm, "mid": v(31.82, 49.83) * mm, "end": v(31.89, 49.9) * mm});
            skArc(sketch, "E2397", {"start": v(31.89, 49.9) * mm, "mid": v(31.82, 49.95) * mm, "end": v(31.76, 49.9) * mm});
            skArc(sketch, "E2398", {"start": v(20.38, 16.32) * mm, "mid": v(20.51, 16.2) * mm, "end": v(20.64, 16.32) * mm});
            skArc(sketch, "E2399", {"start": v(20.64, 16.32) * mm, "mid": v(20.51, 16.45) * mm, "end": v(20.38, 16.32) * mm});
            skArc(sketch, "E2400", {"start": v(34.8, 55.28) * mm, "mid": v(34.86, 55.21) * mm, "end": v(34.92, 55.28) * mm});
            skArc(sketch, "E2401", {"start": v(34.92, 55.28) * mm, "mid": v(34.86, 55.34) * mm, "end": v(34.8, 55.28) * mm});
            skArc(sketch, "E2402", {"start": v(21.9, 16.32) * mm, "mid": v(22.03, 16.2) * mm, "end": v(22.16, 16.32) * mm});
            skArc(sketch, "E2403", {"start": v(22.16, 16.32) * mm, "mid": v(22.03, 16.45) * mm, "end": v(21.9, 16.32) * mm});
            skArc(sketch, "E2404", {"start": v(30.72, 56.78) * mm, "mid": v(30.78, 56.71) * mm, "end": v(30.85, 56.78) * mm});
            skArc(sketch, "E2405", {"start": v(30.85, 56.78) * mm, "mid": v(30.78, 56.84) * mm, "end": v(30.72, 56.78) * mm});
            skArc(sketch, "E2406", {"start": v(23.43, 16.32) * mm, "mid": v(23.56, 16.2) * mm, "end": v(23.69, 16.32) * mm});
            skArc(sketch, "E2407", {"start": v(23.69, 16.32) * mm, "mid": v(23.56, 16.45) * mm, "end": v(23.43, 16.32) * mm});
            skArc(sketch, "E2408", {"start": v(32.26, 51.39) * mm, "mid": v(32.32, 51.33) * mm, "end": v(32.39, 51.39) * mm});
            skArc(sketch, "E2409", {"start": v(32.39, 51.39) * mm, "mid": v(32.32, 51.45) * mm, "end": v(32.26, 51.39) * mm});
            skArc(sketch, "E2410", {"start": v(24.96, 16.32) * mm, "mid": v(25.08, 16.2) * mm, "end": v(25.2, 16.32) * mm});
            skArc(sketch, "E2411", {"start": v(25.2, 16.32) * mm, "mid": v(25.08, 16.45) * mm, "end": v(24.96, 16.32) * mm});
            skArc(sketch, "E2412", {"start": v(33.27, 55.28) * mm, "mid": v(33.33, 55.21) * mm, "end": v(33.4, 55.28) * mm});
            skArc(sketch, "E2413", {"start": v(33.4, 55.28) * mm, "mid": v(33.33, 55.34) * mm, "end": v(33.27, 55.28) * mm});
            skArc(sketch, "E2414", {"start": v(26.48, 16.32) * mm, "mid": v(26.6, 16.2) * mm, "end": v(26.73, 16.32) * mm});
            skArc(sketch, "E2415", {"start": v(26.73, 16.32) * mm, "mid": v(26.6, 16.45) * mm, "end": v(26.48, 16.32) * mm});
            skArc(sketch, "E2416", {"start": v(30.73, 54.09) * mm, "mid": v(30.8, 54.03) * mm, "end": v(30.86, 54.09) * mm});
            skArc(sketch, "E2417", {"start": v(30.86, 54.09) * mm, "mid": v(30.8, 54.15) * mm, "end": v(30.73, 54.09) * mm});
            skArc(sketch, "E2418", {"start": v(28, 16.32) * mm, "mid": v(28.13, 16.2) * mm, "end": v(28.26, 16.32) * mm});
            skArc(sketch, "E2419", {"start": v(28.26, 16.32) * mm, "mid": v(28.13, 16.45) * mm, "end": v(28, 16.32) * mm});
            skArc(sketch, "E2420", {"start": v(32.27, 49.9) * mm, "mid": v(32.33, 49.83) * mm, "end": v(32.4, 49.9) * mm});
            skArc(sketch, "E2421", {"start": v(32.4, 49.9) * mm, "mid": v(32.33, 49.95) * mm, "end": v(32.27, 49.9) * mm});
            skArc(sketch, "E2422", {"start": v(29.53, 16.32) * mm, "mid": v(29.65, 16.2) * mm, "end": v(29.78, 16.32) * mm});
            skArc(sketch, "E2423", {"start": v(29.78, 16.32) * mm, "mid": v(29.65, 16.45) * mm, "end": v(29.53, 16.32) * mm});
            skArc(sketch, "E2424", {"start": v(32.78, 49.9) * mm, "mid": v(32.84, 49.83) * mm, "end": v(32.9, 49.9) * mm});
            skArc(sketch, "E2425", {"start": v(32.9, 49.9) * mm, "mid": v(32.84, 49.95) * mm, "end": v(32.78, 49.9) * mm});
            skArc(sketch, "E2426", {"start": v(47.55, 43.38) * mm, "mid": v(47.61, 43.32) * mm, "end": v(47.68, 43.38) * mm});
            skArc(sketch, "E2427", {"start": v(47.68, 43.38) * mm, "mid": v(47.61, 43.44) * mm, "end": v(47.55, 43.38) * mm});
            skArc(sketch, "E2428", {"start": v(35.32, 47.24) * mm, "mid": v(35.38, 47.18) * mm, "end": v(35.45, 47.24) * mm});
            skArc(sketch, "E2429", {"start": v(35.45, 47.24) * mm, "mid": v(35.38, 47.3) * mm, "end": v(35.32, 47.24) * mm});
            skArc(sketch, "E2430", {"start": v(31.05, 16.32) * mm, "mid": v(31.18, 16.2) * mm, "end": v(31.3, 16.32) * mm});
            skArc(sketch, "E2431", {"start": v(31.3, 16.32) * mm, "mid": v(31.18, 16.45) * mm, "end": v(31.05, 16.32) * mm});
            skArc(sketch, "E2432", {"start": v(34.3, 49.9) * mm, "mid": v(34.36, 49.83) * mm, "end": v(34.43, 49.9) * mm});
            skArc(sketch, "E2433", {"start": v(34.43, 49.9) * mm, "mid": v(34.36, 49.95) * mm, "end": v(34.3, 49.9) * mm});
            skArc(sketch, "E2434", {"start": v(40.2, 16.32) * mm, "mid": v(40.32, 16.2) * mm, "end": v(40.45, 16.32) * mm});
            skArc(sketch, "E2435", {"start": v(40.45, 16.32) * mm, "mid": v(40.32, 16.45) * mm, "end": v(40.2, 16.32) * mm});
            skArc(sketch, "E2436", {"start": v(33.78, 55.28) * mm, "mid": v(33.84, 55.21) * mm, "end": v(33.9, 55.28) * mm});
            skArc(sketch, "E2437", {"start": v(33.9, 55.28) * mm, "mid": v(33.84, 55.34) * mm, "end": v(33.78, 55.28) * mm});
            skArc(sketch, "E2438", {"start": v(37.81, 33.35) * mm, "mid": v(37.87, 33.29) * mm, "end": v(37.94, 33.35) * mm});
            skArc(sketch, "E2439", {"start": v(37.94, 33.35) * mm, "mid": v(37.87, 33.42) * mm, "end": v(37.81, 33.35) * mm});
            skArc(sketch, "E2440", {"start": v(37.81, 45.54) * mm, "mid": v(37.87, 45.48) * mm, "end": v(37.94, 45.54) * mm});
            skArc(sketch, "E2441", {"start": v(37.94, 45.54) * mm, "mid": v(37.87, 45.6) * mm, "end": v(37.81, 45.54) * mm});
            skArc(sketch, "E2442", {"start": v(37.81, 45.04) * mm, "mid": v(37.87, 44.97) * mm, "end": v(37.94, 45.04) * mm});
            skArc(sketch, "E2443", {"start": v(37.94, 45.04) * mm, "mid": v(37.87, 45.1) * mm, "end": v(37.81, 45.04) * mm});
            skArc(sketch, "E2444", {"start": v(37.81, 44.53) * mm, "mid": v(37.87, 44.47) * mm, "end": v(37.94, 44.53) * mm});
            skArc(sketch, "E2445", {"start": v(37.94, 44.53) * mm, "mid": v(37.87, 44.6) * mm, "end": v(37.81, 44.53) * mm});
            skArc(sketch, "E2446", {"start": v(37.81, 38.94) * mm, "mid": v(37.87, 38.88) * mm, "end": v(37.94, 38.94) * mm});
            skArc(sketch, "E2447", {"start": v(37.94, 38.94) * mm, "mid": v(37.87, 39) * mm, "end": v(37.81, 38.94) * mm});
            skArc(sketch, "E2448", {"start": v(37.81, 44.02) * mm, "mid": v(37.87, 43.96) * mm, "end": v(37.94, 44.02) * mm});
            skArc(sketch, "E2449", {"start": v(37.94, 44.02) * mm, "mid": v(37.87, 44.08) * mm, "end": v(37.81, 44.02) * mm});
            skArc(sketch, "E2450", {"start": v(37.81, 43) * mm, "mid": v(37.87, 42.94) * mm, "end": v(37.94, 43) * mm});
            skArc(sketch, "E2451", {"start": v(37.94, 43) * mm, "mid": v(37.87, 43.07) * mm, "end": v(37.81, 43) * mm});
            skArc(sketch, "E2452", {"start": v(37.81, 43.51) * mm, "mid": v(37.87, 43.45) * mm, "end": v(37.94, 43.51) * mm});
            skArc(sketch, "E2453", {"start": v(37.94, 43.51) * mm, "mid": v(37.87, 43.58) * mm, "end": v(37.81, 43.51) * mm});
            skArc(sketch, "E2454", {"start": v(37.81, 39.96) * mm, "mid": v(37.87, 39.9) * mm, "end": v(37.94, 39.96) * mm});
            skArc(sketch, "E2455", {"start": v(37.94, 39.96) * mm, "mid": v(37.87, 40.02) * mm, "end": v(37.81, 39.96) * mm});
            skArc(sketch, "E2456", {"start": v(37.81, 41.48) * mm, "mid": v(37.87, 41.42) * mm, "end": v(37.94, 41.48) * mm});
            skArc(sketch, "E2457", {"start": v(37.94, 41.48) * mm, "mid": v(37.87, 41.54) * mm, "end": v(37.81, 41.48) * mm});
            skArc(sketch, "E2458", {"start": v(37.81, 40.97) * mm, "mid": v(37.87, 40.9) * mm, "end": v(37.94, 40.97) * mm});
            skArc(sketch, "E2459", {"start": v(37.94, 40.97) * mm, "mid": v(37.87, 41.04) * mm, "end": v(37.81, 40.97) * mm});
            skArc(sketch, "E2460", {"start": v(37.81, 40.46) * mm, "mid": v(37.87, 40.4) * mm, "end": v(37.94, 40.46) * mm});
            skArc(sketch, "E2461", {"start": v(37.94, 40.46) * mm, "mid": v(37.87, 40.53) * mm, "end": v(37.81, 40.46) * mm});
            skArc(sketch, "E2462", {"start": v(37.81, 42.5) * mm, "mid": v(37.87, 42.43) * mm, "end": v(37.94, 42.5) * mm});
            skArc(sketch, "E2463", {"start": v(37.94, 42.5) * mm, "mid": v(37.87, 42.56) * mm, "end": v(37.81, 42.5) * mm});
            skArc(sketch, "E2464", {"start": v(37.81, 41.99) * mm, "mid": v(37.87, 41.93) * mm, "end": v(37.94, 41.99) * mm});
            skArc(sketch, "E2465", {"start": v(37.94, 41.99) * mm, "mid": v(37.87, 42.05) * mm, "end": v(37.81, 41.99) * mm});
            skArc(sketch, "E2466", {"start": v(37.81, 39.45) * mm, "mid": v(37.87, 39.39) * mm, "end": v(37.94, 39.45) * mm});
            skArc(sketch, "E2467", {"start": v(37.94, 39.45) * mm, "mid": v(37.87, 39.51) * mm, "end": v(37.81, 39.45) * mm});
            skArc(sketch, "E2468", {"start": v(37.81, 36.4) * mm, "mid": v(37.87, 36.34) * mm, "end": v(37.94, 36.4) * mm});
            skArc(sketch, "E2469", {"start": v(37.94, 36.4) * mm, "mid": v(37.87, 36.46) * mm, "end": v(37.81, 36.4) * mm});
            skArc(sketch, "E2470", {"start": v(37.81, 38.43) * mm, "mid": v(37.87, 38.37) * mm, "end": v(37.94, 38.43) * mm});
            skArc(sketch, "E2471", {"start": v(37.94, 38.43) * mm, "mid": v(37.87, 38.5) * mm, "end": v(37.81, 38.43) * mm});
            skArc(sketch, "E2472", {"start": v(37.81, 36.9) * mm, "mid": v(37.87, 36.85) * mm, "end": v(37.94, 36.9) * mm});
            skArc(sketch, "E2473", {"start": v(37.94, 36.9) * mm, "mid": v(37.87, 36.97) * mm, "end": v(37.81, 36.9) * mm});
            skArc(sketch, "E2474", {"start": v(37.81, 37.42) * mm, "mid": v(37.87, 37.35) * mm, "end": v(37.94, 37.42) * mm});
            skArc(sketch, "E2475", {"start": v(37.94, 37.42) * mm, "mid": v(37.87, 37.48) * mm, "end": v(37.81, 37.42) * mm});
            skArc(sketch, "E2476", {"start": v(37.81, 37.92) * mm, "mid": v(37.87, 37.86) * mm, "end": v(37.94, 37.92) * mm});
            skArc(sketch, "E2477", {"start": v(37.94, 37.92) * mm, "mid": v(37.87, 37.99) * mm, "end": v(37.81, 37.92) * mm});
            skArc(sketch, "E2478", {"start": v(37.81, 34.88) * mm, "mid": v(37.87, 34.81) * mm, "end": v(37.94, 34.88) * mm});
            skArc(sketch, "E2479", {"start": v(37.94, 34.88) * mm, "mid": v(37.87, 34.94) * mm, "end": v(37.81, 34.88) * mm});
            skArc(sketch, "E2480", {"start": v(37.81, 35.38) * mm, "mid": v(37.87, 35.32) * mm, "end": v(37.94, 35.38) * mm});
            skArc(sketch, "E2481", {"start": v(37.94, 35.38) * mm, "mid": v(37.87, 35.45) * mm, "end": v(37.81, 35.38) * mm});
            skArc(sketch, "E2482", {"start": v(37.81, 35.9) * mm, "mid": v(37.87, 35.83) * mm, "end": v(37.94, 35.9) * mm});
            skArc(sketch, "E2483", {"start": v(37.94, 35.9) * mm, "mid": v(37.87, 35.96) * mm, "end": v(37.81, 35.9) * mm});
            skArc(sketch, "E2484", {"start": v(37.81, 34.37) * mm, "mid": v(37.87, 34.3) * mm, "end": v(37.94, 34.37) * mm});
            skArc(sketch, "E2485", {"start": v(37.94, 34.37) * mm, "mid": v(37.87, 34.43) * mm, "end": v(37.81, 34.37) * mm});
            skArc(sketch, "E2486", {"start": v(37.81, 33.86) * mm, "mid": v(37.87, 33.8) * mm, "end": v(37.94, 33.86) * mm});
            skArc(sketch, "E2487", {"start": v(37.94, 33.86) * mm, "mid": v(37.87, 33.92) * mm, "end": v(37.81, 33.86) * mm});
            skArc(sketch, "E2488", {"start": v(37.81, 32.34) * mm, "mid": v(37.87, 32.27) * mm, "end": v(37.94, 32.34) * mm});
            skArc(sketch, "E2489", {"start": v(37.94, 32.34) * mm, "mid": v(37.87, 32.4) * mm, "end": v(37.81, 32.34) * mm});
            skArc(sketch, "E2490", {"start": v(37.81, 32.84) * mm, "mid": v(37.87, 32.78) * mm, "end": v(37.94, 32.84) * mm});
            skArc(sketch, "E2491", {"start": v(37.94, 32.84) * mm, "mid": v(37.87, 32.9) * mm, "end": v(37.81, 32.84) * mm});
            skArc(sketch, "E2492", {"start": v(37.81, 31.83) * mm, "mid": v(37.87, 31.77) * mm, "end": v(37.94, 31.83) * mm});
            skArc(sketch, "E2493", {"start": v(37.94, 31.83) * mm, "mid": v(37.87, 31.9) * mm, "end": v(37.81, 31.83) * mm});
            skArc(sketch, "E2494", {"start": v(37.81, 31.32) * mm, "mid": v(37.87, 31.26) * mm, "end": v(37.94, 31.32) * mm});
            skArc(sketch, "E2495", {"start": v(37.94, 31.32) * mm, "mid": v(37.87, 31.38) * mm, "end": v(37.81, 31.32) * mm});
            skArc(sketch, "E2496", {"start": v(37.81, 30.81) * mm, "mid": v(37.87, 30.75) * mm, "end": v(37.94, 30.81) * mm});
            skArc(sketch, "E2497", {"start": v(37.94, 30.81) * mm, "mid": v(37.87, 30.88) * mm, "end": v(37.81, 30.81) * mm});
            skArc(sketch, "E2498", {"start": v(39.3, 37.43) * mm, "mid": v(39.37, 37.36) * mm, "end": v(39.43, 37.43) * mm});
            skArc(sketch, "E2499", {"start": v(39.43, 37.43) * mm, "mid": v(39.37, 37.5) * mm, "end": v(39.3, 37.43) * mm});
            skArc(sketch, "E2500", {"start": v(39.3, 45.04) * mm, "mid": v(39.37, 44.98) * mm, "end": v(39.43, 45.04) * mm});
            skArc(sketch, "E2501", {"start": v(39.43, 45.04) * mm, "mid": v(39.37, 45.1) * mm, "end": v(39.3, 45.04) * mm});
            skArc(sketch, "E2502", {"start": v(39.3, 45.55) * mm, "mid": v(39.37, 45.49) * mm, "end": v(39.43, 45.55) * mm});
            skArc(sketch, "E2503", {"start": v(39.43, 45.55) * mm, "mid": v(39.37, 45.62) * mm, "end": v(39.3, 45.55) * mm});
            skArc(sketch, "E2504", {"start": v(39.3, 44.54) * mm, "mid": v(39.37, 44.47) * mm, "end": v(39.43, 44.54) * mm});
            skArc(sketch, "E2505", {"start": v(39.43, 44.54) * mm, "mid": v(39.37, 44.6) * mm, "end": v(39.3, 44.54) * mm});
            skArc(sketch, "E2506", {"start": v(39.3, 44.03) * mm, "mid": v(39.37, 43.96) * mm, "end": v(39.43, 44.03) * mm});
            skArc(sketch, "E2507", {"start": v(39.43, 44.03) * mm, "mid": v(39.37, 44.1) * mm, "end": v(39.3, 44.03) * mm});
            skArc(sketch, "E2508", {"start": v(39.3, 42.5) * mm, "mid": v(39.37, 42.44) * mm, "end": v(39.43, 42.5) * mm});
            skArc(sketch, "E2509", {"start": v(39.43, 42.5) * mm, "mid": v(39.37, 42.57) * mm, "end": v(39.3, 42.5) * mm});
            skArc(sketch, "E2510", {"start": v(39.3, 43.01) * mm, "mid": v(39.37, 42.95) * mm, "end": v(39.43, 43.01) * mm});
            skArc(sketch, "E2511", {"start": v(39.43, 43.01) * mm, "mid": v(39.37, 43.08) * mm, "end": v(39.3, 43.01) * mm});
            skArc(sketch, "E2512", {"start": v(39.3, 43.52) * mm, "mid": v(39.37, 43.46) * mm, "end": v(39.43, 43.52) * mm});
            skArc(sketch, "E2513", {"start": v(39.43, 43.52) * mm, "mid": v(39.37, 43.58) * mm, "end": v(39.3, 43.52) * mm});
            skArc(sketch, "E2514", {"start": v(39.3, 40.98) * mm, "mid": v(39.37, 40.92) * mm, "end": v(39.43, 40.98) * mm});
            skArc(sketch, "E2515", {"start": v(39.43, 40.98) * mm, "mid": v(39.37, 41.04) * mm, "end": v(39.3, 40.98) * mm});
            skArc(sketch, "E2516", {"start": v(39.3, 41.49) * mm, "mid": v(39.37, 41.42) * mm, "end": v(39.43, 41.49) * mm});
            skArc(sketch, "E2517", {"start": v(39.43, 41.49) * mm, "mid": v(39.37, 41.55) * mm, "end": v(39.3, 41.49) * mm});
            skArc(sketch, "E2518", {"start": v(39.3, 42) * mm, "mid": v(39.37, 41.93) * mm, "end": v(39.43, 42) * mm});
            skArc(sketch, "E2519", {"start": v(39.43, 42) * mm, "mid": v(39.37, 42.06) * mm, "end": v(39.3, 42) * mm});
            skArc(sketch, "E2520", {"start": v(39.3, 38.95) * mm, "mid": v(39.37, 38.88) * mm, "end": v(39.43, 38.95) * mm});
            skArc(sketch, "E2521", {"start": v(39.43, 38.95) * mm, "mid": v(39.37, 39.01) * mm, "end": v(39.3, 38.95) * mm});
            skArc(sketch, "E2522", {"start": v(39.3, 38.44) * mm, "mid": v(39.37, 38.38) * mm, "end": v(39.43, 38.44) * mm});
            skArc(sketch, "E2523", {"start": v(39.43, 38.44) * mm, "mid": v(39.37, 38.5) * mm, "end": v(39.3, 38.44) * mm});
            skArc(sketch, "E2524", {"start": v(39.3, 37.93) * mm, "mid": v(39.37, 37.87) * mm, "end": v(39.43, 37.93) * mm});
            skArc(sketch, "E2525", {"start": v(39.43, 37.93) * mm, "mid": v(39.37, 38) * mm, "end": v(39.3, 37.93) * mm});
            skArc(sketch, "E2526", {"start": v(39.3, 39.96) * mm, "mid": v(39.37, 39.9) * mm, "end": v(39.43, 39.96) * mm});
            skArc(sketch, "E2527", {"start": v(39.43, 39.96) * mm, "mid": v(39.37, 40.03) * mm, "end": v(39.3, 39.96) * mm});
            skArc(sketch, "E2528", {"start": v(39.3, 40.47) * mm, "mid": v(39.37, 40.4) * mm, "end": v(39.43, 40.47) * mm});
            skArc(sketch, "E2529", {"start": v(39.43, 40.47) * mm, "mid": v(39.37, 40.54) * mm, "end": v(39.3, 40.47) * mm});
            skArc(sketch, "E2530", {"start": v(39.3, 39.46) * mm, "mid": v(39.37, 39.4) * mm, "end": v(39.43, 39.46) * mm});
            skArc(sketch, "E2531", {"start": v(39.43, 39.46) * mm, "mid": v(39.37, 39.52) * mm, "end": v(39.3, 39.46) * mm});
            skArc(sketch, "E2532", {"start": v(39.3, 39.97) * mm, "mid": v(39.37, 39.9) * mm, "end": v(39.43, 39.97) * mm});
            skArc(sketch, "E2533", {"start": v(39.43, 39.97) * mm, "mid": v(39.37, 40.03) * mm, "end": v(39.3, 39.97) * mm});
            skArc(sketch, "E2534", {"start": v(39.3, 32.85) * mm, "mid": v(39.37, 32.8) * mm, "end": v(39.43, 32.85) * mm});
            skArc(sketch, "E2535", {"start": v(39.43, 32.85) * mm, "mid": v(39.37, 32.92) * mm, "end": v(39.3, 32.85) * mm});
            skArc(sketch, "E2536", {"start": v(39.3, 35.9) * mm, "mid": v(39.37, 35.84) * mm, "end": v(39.43, 35.9) * mm});
            skArc(sketch, "E2537", {"start": v(39.43, 35.9) * mm, "mid": v(39.37, 35.97) * mm, "end": v(39.3, 35.9) * mm});
            skArc(sketch, "E2538", {"start": v(39.3, 35.4) * mm, "mid": v(39.37, 35.33) * mm, "end": v(39.43, 35.4) * mm});
            skArc(sketch, "E2539", {"start": v(39.43, 35.4) * mm, "mid": v(39.37, 35.46) * mm, "end": v(39.3, 35.4) * mm});
            skArc(sketch, "E2540", {"start": v(39.3, 34.89) * mm, "mid": v(39.37, 34.82) * mm, "end": v(39.43, 34.89) * mm});
            skArc(sketch, "E2541", {"start": v(39.43, 34.89) * mm, "mid": v(39.37, 34.95) * mm, "end": v(39.3, 34.89) * mm});
            skArc(sketch, "E2542", {"start": v(16.17, 46.6) * mm, "mid": v(16.23, 46.53) * mm, "end": v(16.3, 46.6) * mm});
            skArc(sketch, "E2543", {"start": v(16.3, 46.6) * mm, "mid": v(16.23, 46.65) * mm, "end": v(16.17, 46.6) * mm});
            skArc(sketch, "E2544", {"start": v(16.6, 46.96) * mm, "mid": v(16.67, 46.9) * mm, "end": v(16.74, 46.96) * mm});
            skArc(sketch, "E2545", {"start": v(16.74, 46.96) * mm, "mid": v(16.67, 47.02) * mm, "end": v(16.6, 46.96) * mm});
            skArc(sketch, "E2546", {"start": v(16.46, 48.53) * mm, "mid": v(16.52, 48.47) * mm, "end": v(16.58, 48.53) * mm});
            skArc(sketch, "E2547", {"start": v(16.58, 48.53) * mm, "mid": v(16.52, 48.6) * mm, "end": v(16.46, 48.53) * mm});
            skArc(sketch, "E2548", {"start": v(39.3, 30.82) * mm, "mid": v(39.37, 30.76) * mm, "end": v(39.43, 30.82) * mm});
            skArc(sketch, "E2549", {"start": v(39.43, 30.82) * mm, "mid": v(39.37, 30.89) * mm, "end": v(39.3, 30.82) * mm});
            skArc(sketch, "E2550", {"start": v(39.3, 32.35) * mm, "mid": v(39.37, 32.28) * mm, "end": v(39.43, 32.35) * mm});
            skArc(sketch, "E2551", {"start": v(39.43, 32.35) * mm, "mid": v(39.37, 32.41) * mm, "end": v(39.3, 32.35) * mm});
            skArc(sketch, "E2552", {"start": v(39.3, 31.84) * mm, "mid": v(39.37, 31.78) * mm, "end": v(39.43, 31.84) * mm});
            skArc(sketch, "E2553", {"start": v(39.43, 31.84) * mm, "mid": v(39.37, 31.9) * mm, "end": v(39.3, 31.84) * mm});
            skArc(sketch, "E2554", {"start": v(39.3, 31.33) * mm, "mid": v(39.37, 31.27) * mm, "end": v(39.43, 31.33) * mm});
            skArc(sketch, "E2555", {"start": v(39.43, 31.33) * mm, "mid": v(39.37, 31.4) * mm, "end": v(39.3, 31.33) * mm});
            skArc(sketch, "E2556", {"start": v(39.3, 33.36) * mm, "mid": v(39.37, 33.3) * mm, "end": v(39.43, 33.36) * mm});
            skArc(sketch, "E2557", {"start": v(39.43, 33.36) * mm, "mid": v(39.37, 33.43) * mm, "end": v(39.3, 33.36) * mm});
            skArc(sketch, "E2558", {"start": v(39.3, 34.38) * mm, "mid": v(39.37, 34.32) * mm, "end": v(39.43, 34.38) * mm});
            skArc(sketch, "E2559", {"start": v(39.43, 34.38) * mm, "mid": v(39.37, 34.44) * mm, "end": v(39.3, 34.38) * mm});
            skArc(sketch, "E2560", {"start": v(39.3, 36.41) * mm, "mid": v(39.37, 36.35) * mm, "end": v(39.43, 36.41) * mm});
            skArc(sketch, "E2561", {"start": v(39.43, 36.41) * mm, "mid": v(39.37, 36.47) * mm, "end": v(39.3, 36.41) * mm});
            skArc(sketch, "E2562", {"start": v(39.3, 36.92) * mm, "mid": v(39.37, 36.86) * mm, "end": v(39.43, 36.92) * mm});
            skArc(sketch, "E2563", {"start": v(39.43, 36.92) * mm, "mid": v(39.37, 36.98) * mm, "end": v(39.3, 36.92) * mm});
            skArc(sketch, "E2564", {"start": v(39.3, 33.87) * mm, "mid": v(39.37, 33.8) * mm, "end": v(39.43, 33.87) * mm});
            skArc(sketch, "E2565", {"start": v(39.43, 33.87) * mm, "mid": v(39.37, 33.93) * mm, "end": v(39.3, 33.87) * mm});
            skArc(sketch, "E2566", {"start": v(17.14, 47.15) * mm, "mid": v(17.2, 47.08) * mm, "end": v(17.27, 47.15) * mm});
            skArc(sketch, "E2567", {"start": v(17.27, 47.15) * mm, "mid": v(17.2, 47.21) * mm, "end": v(17.14, 47.15) * mm});
            skArc(sketch, "E2568", {"start": v(17.07, 48.7) * mm, "mid": v(17.13, 48.65) * mm, "end": v(17.2, 48.7) * mm});
            skArc(sketch, "E2569", {"start": v(17.2, 48.7) * mm, "mid": v(17.13, 48.77) * mm, "end": v(17.07, 48.7) * mm});
            skArc(sketch, "E2570", {"start": v(15.85, 48.28) * mm, "mid": v(15.91, 48.21) * mm, "end": v(15.97, 48.28) * mm});
            skArc(sketch, "E2571", {"start": v(15.97, 48.28) * mm, "mid": v(15.91, 48.34) * mm, "end": v(15.85, 48.28) * mm});
            skArc(sketch, "E2572", {"start": v(15.29, 47.9) * mm, "mid": v(15.35, 47.83) * mm, "end": v(15.42, 47.9) * mm});
            skArc(sketch, "E2573", {"start": v(15.42, 47.9) * mm, "mid": v(15.35, 47.96) * mm, "end": v(15.29, 47.9) * mm});
            skArc(sketch, "E2574", {"start": v(15.7, 39.94) * mm, "mid": v(15.77, 39.88) * mm, "end": v(15.83, 39.94) * mm});
            skArc(sketch, "E2575", {"start": v(15.83, 39.94) * mm, "mid": v(15.77, 40) * mm, "end": v(15.7, 39.94) * mm});
            skArc(sketch, "E2576", {"start": v(15.7, 40.45) * mm, "mid": v(15.77, 40.39) * mm, "end": v(15.83, 40.45) * mm});
            skArc(sketch, "E2577", {"start": v(15.83, 40.45) * mm, "mid": v(15.77, 40.51) * mm, "end": v(15.7, 40.45) * mm});
            skArc(sketch, "E2578", {"start": v(15.7, 39.43) * mm, "mid": v(15.77, 39.37) * mm, "end": v(15.83, 39.43) * mm});
            skArc(sketch, "E2579", {"start": v(15.83, 39.43) * mm, "mid": v(15.77, 39.5) * mm, "end": v(15.7, 39.43) * mm});
            skArc(sketch, "E2580", {"start": v(15.7, 41.97) * mm, "mid": v(15.77, 41.9) * mm, "end": v(15.83, 41.97) * mm});
            skArc(sketch, "E2581", {"start": v(15.83, 41.97) * mm, "mid": v(15.77, 42.03) * mm, "end": v(15.7, 41.97) * mm});
            skArc(sketch, "E2582", {"start": v(15.7, 42.48) * mm, "mid": v(15.77, 42.42) * mm, "end": v(15.83, 42.48) * mm});
            skArc(sketch, "E2583", {"start": v(15.83, 42.48) * mm, "mid": v(15.77, 42.54) * mm, "end": v(15.7, 42.48) * mm});
            skArc(sketch, "E2584", {"start": v(15.7, 40.45) * mm, "mid": v(15.77, 40.38) * mm, "end": v(15.83, 40.45) * mm});
            skArc(sketch, "E2585", {"start": v(15.7, 40.95) * mm, "mid": v(15.77, 40.9) * mm, "end": v(15.83, 40.95) * mm});
            skArc(sketch, "E2586", {"start": v(15.83, 40.95) * mm, "mid": v(15.77, 41.02) * mm, "end": v(15.7, 40.95) * mm});
            skArc(sketch, "E2587", {"start": v(15.7, 41.46) * mm, "mid": v(15.77, 41.4) * mm, "end": v(15.83, 41.46) * mm});
            skArc(sketch, "E2588", {"start": v(15.83, 41.46) * mm, "mid": v(15.77, 41.53) * mm, "end": v(15.7, 41.46) * mm});
            skArc(sketch, "E2589", {"start": v(15.7, 44.51) * mm, "mid": v(15.77, 44.45) * mm, "end": v(15.83, 44.51) * mm});
            skArc(sketch, "E2590", {"start": v(15.83, 44.51) * mm, "mid": v(15.77, 44.57) * mm, "end": v(15.7, 44.51) * mm});
            skArc(sketch, "E2591", {"start": v(15.7, 45.02) * mm, "mid": v(15.77, 44.96) * mm, "end": v(15.83, 45.02) * mm});
            skArc(sketch, "E2592", {"start": v(15.83, 45.02) * mm, "mid": v(15.77, 45.08) * mm, "end": v(15.7, 45.02) * mm});
            skArc(sketch, "E2593", {"start": v(15.7, 45.53) * mm, "mid": v(15.77, 45.46) * mm, "end": v(15.83, 45.53) * mm});
            skArc(sketch, "E2594", {"start": v(15.83, 45.53) * mm, "mid": v(15.77, 45.6) * mm, "end": v(15.7, 45.53) * mm});
            skArc(sketch, "E2595", {"start": v(15.7, 43.5) * mm, "mid": v(15.77, 43.43) * mm, "end": v(15.83, 43.5) * mm});
            skArc(sketch, "E2596", {"start": v(15.83, 43.5) * mm, "mid": v(15.77, 43.56) * mm, "end": v(15.7, 43.5) * mm});
            skArc(sketch, "E2597", {"start": v(15.7, 42.99) * mm, "mid": v(15.77, 42.92) * mm, "end": v(15.83, 42.99) * mm});
            skArc(sketch, "E2598", {"start": v(15.83, 42.99) * mm, "mid": v(15.77, 43.05) * mm, "end": v(15.7, 42.99) * mm});
            skArc(sketch, "E2599", {"start": v(15.7, 44) * mm, "mid": v(15.77, 43.94) * mm, "end": v(15.83, 44) * mm});
            skArc(sketch, "E2600", {"start": v(15.83, 44) * mm, "mid": v(15.77, 44.07) * mm, "end": v(15.7, 44) * mm});
            skArc(sketch, "E2601", {"start": v(15.85, 46.1) * mm, "mid": v(15.92, 46.03) * mm, "end": v(15.98, 46.1) * mm});
            skArc(sketch, "E2602", {"start": v(15.98, 46.1) * mm, "mid": v(15.92, 46.16) * mm, "end": v(15.85, 46.1) * mm});
            skArc(sketch, "E2603", {"start": v(14.21, 41.98) * mm, "mid": v(14.27, 41.92) * mm, "end": v(14.34, 41.98) * mm});
            skArc(sketch, "E2604", {"start": v(14.34, 41.98) * mm, "mid": v(14.27, 42.04) * mm, "end": v(14.21, 41.98) * mm});
            skArc(sketch, "E2605", {"start": v(14.21, 39.95) * mm, "mid": v(14.27, 39.89) * mm, "end": v(14.34, 39.95) * mm});
            skArc(sketch, "E2606", {"start": v(14.34, 39.95) * mm, "mid": v(14.27, 40.02) * mm, "end": v(14.21, 39.95) * mm});
            skArc(sketch, "E2607", {"start": v(14.21, 39.44) * mm, "mid": v(14.27, 39.38) * mm, "end": v(14.34, 39.44) * mm});
            skArc(sketch, "E2608", {"start": v(14.34, 39.44) * mm, "mid": v(14.27, 39.5) * mm, "end": v(14.21, 39.44) * mm});
            skArc(sketch, "E2609", {"start": v(14.21, 41.47) * mm, "mid": v(14.27, 41.4) * mm, "end": v(14.34, 41.47) * mm});
            skArc(sketch, "E2610", {"start": v(14.34, 41.47) * mm, "mid": v(14.27, 41.54) * mm, "end": v(14.21, 41.47) * mm});
            skArc(sketch, "E2611", {"start": v(14.21, 40.97) * mm, "mid": v(14.27, 40.9) * mm, "end": v(14.34, 40.97) * mm});
            skArc(sketch, "E2612", {"start": v(14.34, 40.97) * mm, "mid": v(14.27, 41.03) * mm, "end": v(14.21, 40.97) * mm});
            skArc(sketch, "E2613", {"start": v(14.21, 40.46) * mm, "mid": v(14.27, 40.4) * mm, "end": v(14.34, 40.46) * mm});
            skArc(sketch, "E2614", {"start": v(14.34, 40.46) * mm, "mid": v(14.27, 40.52) * mm, "end": v(14.21, 40.46) * mm});
            skArc(sketch, "E2615", {"start": v(14.34, 39.95) * mm, "mid": v(14.27, 40.01) * mm, "end": v(14.21, 39.95) * mm});
            skArc(sketch, "E2616", {"start": v(14.21, 44.52) * mm, "mid": v(14.27, 44.46) * mm, "end": v(14.34, 44.52) * mm});
            skArc(sketch, "E2617", {"start": v(14.34, 44.52) * mm, "mid": v(14.27, 44.58) * mm, "end": v(14.21, 44.52) * mm});
            skArc(sketch, "E2618", {"start": v(14.21, 43.5) * mm, "mid": v(14.27, 43.44) * mm, "end": v(14.34, 43.5) * mm});
            skArc(sketch, "E2619", {"start": v(14.34, 43.5) * mm, "mid": v(14.27, 43.57) * mm, "end": v(14.21, 43.5) * mm});
            skArc(sketch, "E2620", {"start": v(14.21, 43) * mm, "mid": v(14.27, 42.93) * mm, "end": v(14.34, 43) * mm});
            skArc(sketch, "E2621", {"start": v(14.34, 43) * mm, "mid": v(14.27, 43.06) * mm, "end": v(14.21, 43) * mm});
            skArc(sketch, "E2622", {"start": v(14.21, 42.49) * mm, "mid": v(14.27, 42.43) * mm, "end": v(14.34, 42.49) * mm});
            skArc(sketch, "E2623", {"start": v(14.34, 42.49) * mm, "mid": v(14.27, 42.55) * mm, "end": v(14.21, 42.49) * mm});
            skArc(sketch, "E2624", {"start": v(14.21, 44.01) * mm, "mid": v(14.27, 43.95) * mm, "end": v(14.34, 44.01) * mm});
            skArc(sketch, "E2625", {"start": v(14.34, 44.01) * mm, "mid": v(14.27, 44.08) * mm, "end": v(14.21, 44.01) * mm});
            skArc(sketch, "E2626", {"start": v(14.3, 46.22) * mm, "mid": v(14.36, 46.16) * mm, "end": v(14.42, 46.22) * mm});
            skArc(sketch, "E2627", {"start": v(14.42, 46.22) * mm, "mid": v(14.36, 46.28) * mm, "end": v(14.3, 46.22) * mm});
            skArc(sketch, "E2628", {"start": v(14.21, 45.54) * mm, "mid": v(14.27, 45.47) * mm, "end": v(14.34, 45.54) * mm});
            skArc(sketch, "E2629", {"start": v(14.34, 45.54) * mm, "mid": v(14.27, 45.6) * mm, "end": v(14.21, 45.54) * mm});
            skArc(sketch, "E2630", {"start": v(14.21, 45.03) * mm, "mid": v(14.27, 44.97) * mm, "end": v(14.34, 45.03) * mm});
            skArc(sketch, "E2631", {"start": v(14.34, 45.03) * mm, "mid": v(14.27, 45.1) * mm, "end": v(14.21, 45.03) * mm});
            skArc(sketch, "E2632", {"start": v(14.8, 47.36) * mm, "mid": v(14.87, 47.3) * mm, "end": v(14.93, 47.36) * mm});
            skArc(sketch, "E2633", {"start": v(14.93, 47.36) * mm, "mid": v(14.87, 47.43) * mm, "end": v(14.8, 47.36) * mm});
            skArc(sketch, "E2634", {"start": v(14.5, 46.83) * mm, "mid": v(14.56, 46.77) * mm, "end": v(14.63, 46.83) * mm});
            skArc(sketch, "E2635", {"start": v(14.63, 46.83) * mm, "mid": v(14.56, 46.9) * mm, "end": v(14.5, 46.83) * mm});
            skArc(sketch, "E2636", {"start": v(6.92, 27.41) * mm, "mid": v(6.99, 27.35) * mm, "end": v(7.05, 27.41) * mm});
            skArc(sketch, "E2637", {"start": v(7.05, 27.41) * mm, "mid": v(6.99, 27.48) * mm, "end": v(6.92, 27.41) * mm});
            skArc(sketch, "E2638", {"start": v(6.93, 28.91) * mm, "mid": v(7, 28.85) * mm, "end": v(7.06, 28.91) * mm});
            skArc(sketch, "E2639", {"start": v(7.06, 28.91) * mm, "mid": v(7, 28.97) * mm, "end": v(6.93, 28.91) * mm});
            skArc(sketch, "E2640", {"start": v(11.5, 27.41) * mm, "mid": v(11.56, 27.35) * mm, "end": v(11.62, 27.41) * mm});
            skArc(sketch, "E2641", {"start": v(11.62, 27.41) * mm, "mid": v(11.56, 27.48) * mm, "end": v(11.5, 27.41) * mm});
            skArc(sketch, "E2642", {"start": v(11.5, 28.91) * mm, "mid": v(11.57, 28.85) * mm, "end": v(11.63, 28.91) * mm});
            skArc(sketch, "E2643", {"start": v(11.63, 28.91) * mm, "mid": v(11.57, 28.97) * mm, "end": v(11.5, 28.91) * mm});
            skArc(sketch, "E2644", {"start": v(15.26, 29.01) * mm, "mid": v(15.32, 28.95) * mm, "end": v(15.39, 29.01) * mm});
            skArc(sketch, "E2645", {"start": v(15.39, 29.01) * mm, "mid": v(15.32, 29.08) * mm, "end": v(15.26, 29.01) * mm});
            skArc(sketch, "E2646", {"start": v(15.7, 30.8) * mm, "mid": v(15.77, 30.73) * mm, "end": v(15.83, 30.8) * mm});
            skArc(sketch, "E2647", {"start": v(15.83, 30.8) * mm, "mid": v(15.77, 30.86) * mm, "end": v(15.7, 30.8) * mm});
            skArc(sketch, "E2648", {"start": v(15.53, 29.6) * mm, "mid": v(15.6, 29.54) * mm, "end": v(15.66, 29.6) * mm});
            skArc(sketch, "E2649", {"start": v(15.66, 29.6) * mm, "mid": v(15.6, 29.67) * mm, "end": v(15.53, 29.6) * mm});
            skArc(sketch, "E2650", {"start": v(15.67, 30.23) * mm, "mid": v(15.74, 30.17) * mm, "end": v(15.8, 30.23) * mm});
            skArc(sketch, "E2651", {"start": v(15.8, 30.23) * mm, "mid": v(15.74, 30.3) * mm, "end": v(15.67, 30.23) * mm});
            skArc(sketch, "E2652", {"start": v(12.01, 28.91) * mm, "mid": v(12.08, 28.85) * mm, "end": v(12.14, 28.91) * mm});
            skArc(sketch, "E2653", {"start": v(12.14, 28.91) * mm, "mid": v(12.08, 28.97) * mm, "end": v(12.01, 28.91) * mm});
            skArc(sketch, "E2654", {"start": v(12.52, 28.91) * mm, "mid": v(12.58, 28.85) * mm, "end": v(12.65, 28.91) * mm});
            skArc(sketch, "E2655", {"start": v(12.65, 28.91) * mm, "mid": v(12.58, 28.97) * mm, "end": v(12.52, 28.91) * mm});
            skArc(sketch, "E2656", {"start": v(12, 27.41) * mm, "mid": v(12.07, 27.35) * mm, "end": v(12.13, 27.41) * mm});
            skArc(sketch, "E2657", {"start": v(12.13, 27.41) * mm, "mid": v(12.07, 27.48) * mm, "end": v(12, 27.41) * mm});
            skArc(sketch, "E2658", {"start": v(13.17, 27.53) * mm, "mid": v(13.24, 27.46) * mm, "end": v(13.3, 27.53) * mm});
            skArc(sketch, "E2659", {"start": v(13.3, 27.53) * mm, "mid": v(13.24, 27.59) * mm, "end": v(13.17, 27.53) * mm});
            skArc(sketch, "E2660", {"start": v(12.51, 27.41) * mm, "mid": v(12.58, 27.35) * mm, "end": v(12.64, 27.41) * mm});
            skArc(sketch, "E2661", {"start": v(12.64, 27.41) * mm, "mid": v(12.58, 27.48) * mm, "end": v(12.51, 27.41) * mm});
            skArc(sketch, "E2662", {"start": v(14.21, 30.8) * mm, "mid": v(14.27, 30.74) * mm, "end": v(14.34, 30.8) * mm});
            skArc(sketch, "E2663", {"start": v(14.34, 30.8) * mm, "mid": v(14.27, 30.87) * mm, "end": v(14.21, 30.8) * mm});
            skArc(sketch, "E2664", {"start": v(13.05, 29.02) * mm, "mid": v(13.12, 28.96) * mm, "end": v(13.18, 29.02) * mm});
            skArc(sketch, "E2665", {"start": v(13.18, 29.02) * mm, "mid": v(13.12, 29.09) * mm, "end": v(13.05, 29.02) * mm});
            skArc(sketch, "E2666", {"start": v(13.56, 29.33) * mm, "mid": v(13.62, 29.27) * mm, "end": v(13.69, 29.33) * mm});
            skArc(sketch, "E2667", {"start": v(13.69, 29.33) * mm, "mid": v(13.62, 29.4) * mm, "end": v(13.56, 29.33) * mm});
            skArc(sketch, "E2668", {"start": v(13.94, 29.76) * mm, "mid": v(14, 29.7) * mm, "end": v(14.07, 29.76) * mm});
            skArc(sketch, "E2669", {"start": v(14.07, 29.76) * mm, "mid": v(14, 29.82) * mm, "end": v(13.94, 29.76) * mm});
            skArc(sketch, "E2670", {"start": v(14.15, 30.26) * mm, "mid": v(14.2, 30.2) * mm, "end": v(14.27, 30.26) * mm});
            skArc(sketch, "E2671", {"start": v(14.27, 30.26) * mm, "mid": v(14.2, 30.32) * mm, "end": v(14.15, 30.26) * mm});
            skArc(sketch, "E2672", {"start": v(13.85, 27.73) * mm, "mid": v(13.92, 27.66) * mm, "end": v(13.98, 27.73) * mm});
            skArc(sketch, "E2673", {"start": v(13.98, 27.73) * mm, "mid": v(13.92, 27.8) * mm, "end": v(13.85, 27.73) * mm});
            skArc(sketch, "E2674", {"start": v(14.4, 28.06) * mm, "mid": v(14.46, 28) * mm, "end": v(14.52, 28.06) * mm});
            skArc(sketch, "E2675", {"start": v(14.52, 28.06) * mm, "mid": v(14.46, 28.12) * mm, "end": v(14.4, 28.06) * mm});
            skArc(sketch, "E2676", {"start": v(14.86, 28.5) * mm, "mid": v(14.93, 28.43) * mm, "end": v(15, 28.5) * mm});
            skArc(sketch, "E2677", {"start": v(15, 28.5) * mm, "mid": v(14.93, 28.56) * mm, "end": v(14.86, 28.5) * mm});
            skArc(sketch, "E2678", {"start": v(14.21, 33.86) * mm, "mid": v(14.27, 33.8) * mm, "end": v(14.34, 33.86) * mm});
            skArc(sketch, "E2679", {"start": v(14.34, 33.86) * mm, "mid": v(14.27, 33.92) * mm, "end": v(14.21, 33.86) * mm});
            skArc(sketch, "E2680", {"start": v(15.7, 33.85) * mm, "mid": v(15.77, 33.78) * mm, "end": v(15.83, 33.85) * mm});
            skArc(sketch, "E2681", {"start": v(15.83, 33.85) * mm, "mid": v(15.77, 33.9) * mm, "end": v(15.7, 33.85) * mm});
            skArc(sketch, "E2682", {"start": v(14.21, 31.32) * mm, "mid": v(14.27, 31.25) * mm, "end": v(14.34, 31.32) * mm});
            skArc(sketch, "E2683", {"start": v(14.34, 31.32) * mm, "mid": v(14.27, 31.38) * mm, "end": v(14.21, 31.32) * mm});
            skArc(sketch, "E2684", {"start": v(14.21, 31.82) * mm, "mid": v(14.27, 31.76) * mm, "end": v(14.34, 31.82) * mm});
            skArc(sketch, "E2685", {"start": v(14.34, 31.82) * mm, "mid": v(14.27, 31.89) * mm, "end": v(14.21, 31.82) * mm});
            skArc(sketch, "E2686", {"start": v(14.21, 33.35) * mm, "mid": v(14.27, 33.28) * mm, "end": v(14.34, 33.35) * mm});
            skArc(sketch, "E2687", {"start": v(14.34, 33.35) * mm, "mid": v(14.27, 33.41) * mm, "end": v(14.21, 33.35) * mm});
            skArc(sketch, "E2688", {"start": v(14.21, 32.84) * mm, "mid": v(14.27, 32.78) * mm, "end": v(14.34, 32.84) * mm});
            skArc(sketch, "E2689", {"start": v(14.34, 32.84) * mm, "mid": v(14.27, 32.9) * mm, "end": v(14.21, 32.84) * mm});
            skArc(sketch, "E2690", {"start": v(14.21, 32.33) * mm, "mid": v(14.27, 32.27) * mm, "end": v(14.34, 32.33) * mm});
            skArc(sketch, "E2691", {"start": v(14.34, 32.33) * mm, "mid": v(14.27, 32.4) * mm, "end": v(14.21, 32.33) * mm});
            skArc(sketch, "E2692", {"start": v(15.7, 31.3) * mm, "mid": v(15.77, 31.24) * mm, "end": v(15.83, 31.3) * mm});
            skArc(sketch, "E2693", {"start": v(15.83, 31.3) * mm, "mid": v(15.77, 31.37) * mm, "end": v(15.7, 31.3) * mm});
            skArc(sketch, "E2694", {"start": v(15.7, 31.81) * mm, "mid": v(15.77, 31.75) * mm, "end": v(15.83, 31.81) * mm});
            skArc(sketch, "E2695", {"start": v(15.83, 31.81) * mm, "mid": v(15.77, 31.88) * mm, "end": v(15.7, 31.81) * mm});
            skArc(sketch, "E2696", {"start": v(15.7, 33.34) * mm, "mid": v(15.77, 33.27) * mm, "end": v(15.83, 33.34) * mm});
            skArc(sketch, "E2697", {"start": v(15.83, 33.34) * mm, "mid": v(15.77, 33.4) * mm, "end": v(15.7, 33.34) * mm});
            skArc(sketch, "E2698", {"start": v(15.7, 32.83) * mm, "mid": v(15.77, 32.77) * mm, "end": v(15.83, 32.83) * mm});
            skArc(sketch, "E2699", {"start": v(15.83, 32.83) * mm, "mid": v(15.77, 32.9) * mm, "end": v(15.7, 32.83) * mm});
            skArc(sketch, "E2700", {"start": v(15.7, 32.32) * mm, "mid": v(15.77, 32.26) * mm, "end": v(15.83, 32.32) * mm});
            skArc(sketch, "E2701", {"start": v(15.83, 32.32) * mm, "mid": v(15.77, 32.39) * mm, "end": v(15.7, 32.32) * mm});
            skArc(sketch, "E2702", {"start": v(15.7, 34.35) * mm, "mid": v(15.77, 34.3) * mm, "end": v(15.83, 34.35) * mm});
            skArc(sketch, "E2703", {"start": v(15.83, 34.35) * mm, "mid": v(15.77, 34.42) * mm, "end": v(15.7, 34.35) * mm});
            skArc(sketch, "E2704", {"start": v(15.7, 35.88) * mm, "mid": v(15.77, 35.81) * mm, "end": v(15.83, 35.88) * mm});
            skArc(sketch, "E2705", {"start": v(15.83, 35.88) * mm, "mid": v(15.77, 35.94) * mm, "end": v(15.7, 35.88) * mm});
            skArc(sketch, "E2706", {"start": v(15.7, 35.37) * mm, "mid": v(15.77, 35.3) * mm, "end": v(15.83, 35.37) * mm});
            skArc(sketch, "E2707", {"start": v(15.83, 35.37) * mm, "mid": v(15.77, 35.43) * mm, "end": v(15.7, 35.37) * mm});
            skArc(sketch, "E2708", {"start": v(15.7, 34.86) * mm, "mid": v(15.77, 34.8) * mm, "end": v(15.83, 34.86) * mm});
            skArc(sketch, "E2709", {"start": v(15.83, 34.86) * mm, "mid": v(15.77, 34.93) * mm, "end": v(15.7, 34.86) * mm});
            skArc(sketch, "E2710", {"start": v(15.7, 37.9) * mm, "mid": v(15.77, 37.85) * mm, "end": v(15.83, 37.9) * mm});
            skArc(sketch, "E2711", {"start": v(15.83, 37.9) * mm, "mid": v(15.77, 37.97) * mm, "end": v(15.7, 37.9) * mm});
            skArc(sketch, "E2712", {"start": v(15.7, 37.4) * mm, "mid": v(15.77, 37.34) * mm, "end": v(15.83, 37.4) * mm});
            skArc(sketch, "E2713", {"start": v(15.83, 37.4) * mm, "mid": v(15.77, 37.47) * mm, "end": v(15.7, 37.4) * mm});
            skArc(sketch, "E2714", {"start": v(15.7, 36.9) * mm, "mid": v(15.77, 36.83) * mm, "end": v(15.83, 36.9) * mm});
            skArc(sketch, "E2715", {"start": v(15.83, 36.9) * mm, "mid": v(15.77, 36.96) * mm, "end": v(15.7, 36.9) * mm});
            skArc(sketch, "E2716", {"start": v(15.7, 38.42) * mm, "mid": v(15.77, 38.35) * mm, "end": v(15.83, 38.42) * mm});
            skArc(sketch, "E2717", {"start": v(15.83, 38.42) * mm, "mid": v(15.77, 38.48) * mm, "end": v(15.7, 38.42) * mm});
            skArc(sketch, "E2718", {"start": v(15.7, 36.39) * mm, "mid": v(15.77, 36.32) * mm, "end": v(15.83, 36.39) * mm});
            skArc(sketch, "E2719", {"start": v(15.83, 36.39) * mm, "mid": v(15.77, 36.45) * mm, "end": v(15.7, 36.39) * mm});
            skArc(sketch, "E2720", {"start": v(15.7, 38.92) * mm, "mid": v(15.77, 38.86) * mm, "end": v(15.83, 38.92) * mm});
            skArc(sketch, "E2721", {"start": v(15.83, 38.92) * mm, "mid": v(15.77, 38.99) * mm, "end": v(15.7, 38.92) * mm});
            skArc(sketch, "E2722", {"start": v(14.21, 37.92) * mm, "mid": v(14.27, 37.86) * mm, "end": v(14.34, 37.92) * mm});
            skArc(sketch, "E2723", {"start": v(14.34, 37.92) * mm, "mid": v(14.27, 37.98) * mm, "end": v(14.21, 37.92) * mm});
            skArc(sketch, "E2724", {"start": v(14.21, 34.36) * mm, "mid": v(14.27, 34.3) * mm, "end": v(14.34, 34.36) * mm});
            skArc(sketch, "E2725", {"start": v(14.34, 34.36) * mm, "mid": v(14.27, 34.43) * mm, "end": v(14.21, 34.36) * mm});
            skArc(sketch, "E2726", {"start": v(14.21, 36.4) * mm, "mid": v(14.27, 36.33) * mm, "end": v(14.34, 36.4) * mm});
            skArc(sketch, "E2727", {"start": v(14.34, 36.4) * mm, "mid": v(14.27, 36.46) * mm, "end": v(14.21, 36.4) * mm});
            skArc(sketch, "E2728", {"start": v(14.21, 36.9) * mm, "mid": v(14.27, 36.84) * mm, "end": v(14.34, 36.9) * mm});
            skArc(sketch, "E2729", {"start": v(14.34, 36.9) * mm, "mid": v(14.27, 36.97) * mm, "end": v(14.21, 36.9) * mm});
            skArc(sketch, "E2730", {"start": v(14.21, 37.41) * mm, "mid": v(14.27, 37.35) * mm, "end": v(14.34, 37.41) * mm});
            skArc(sketch, "E2731", {"start": v(14.34, 37.41) * mm, "mid": v(14.27, 37.48) * mm, "end": v(14.21, 37.41) * mm});
            skArc(sketch, "E2732", {"start": v(14.21, 34.87) * mm, "mid": v(14.27, 34.8) * mm, "end": v(14.34, 34.87) * mm});
            skArc(sketch, "E2733", {"start": v(14.34, 34.87) * mm, "mid": v(14.27, 34.94) * mm, "end": v(14.21, 34.87) * mm});
            skArc(sketch, "E2734", {"start": v(14.21, 35.38) * mm, "mid": v(14.27, 35.32) * mm, "end": v(14.34, 35.38) * mm});
            skArc(sketch, "E2735", {"start": v(14.34, 35.38) * mm, "mid": v(14.27, 35.44) * mm, "end": v(14.21, 35.38) * mm});
            skArc(sketch, "E2736", {"start": v(14.21, 35.89) * mm, "mid": v(14.27, 35.82) * mm, "end": v(14.34, 35.89) * mm});
            skArc(sketch, "E2737", {"start": v(14.34, 35.89) * mm, "mid": v(14.27, 35.95) * mm, "end": v(14.21, 35.89) * mm});
            skArc(sketch, "E2738", {"start": v(14.21, 38.43) * mm, "mid": v(14.27, 38.36) * mm, "end": v(14.34, 38.43) * mm});
            skArc(sketch, "E2739", {"start": v(14.34, 38.43) * mm, "mid": v(14.27, 38.5) * mm, "end": v(14.21, 38.43) * mm});
            skArc(sketch, "E2740", {"start": v(14.21, 38.93) * mm, "mid": v(14.27, 38.87) * mm, "end": v(14.34, 38.93) * mm});
            skArc(sketch, "E2741", {"start": v(14.34, 38.93) * mm, "mid": v(14.27, 39) * mm, "end": v(14.21, 38.93) * mm});
            skArc(sketch, "E2742", {"start": v(10.48, 27.41) * mm, "mid": v(10.54, 27.35) * mm, "end": v(10.6, 27.41) * mm});
            skArc(sketch, "E2743", {"start": v(10.6, 27.41) * mm, "mid": v(10.54, 27.48) * mm, "end": v(10.48, 27.41) * mm});
            skArc(sketch, "E2744", {"start": v(9.97, 27.41) * mm, "mid": v(10.04, 27.35) * mm, "end": v(10.1, 27.41) * mm});
            skArc(sketch, "E2745", {"start": v(10.1, 27.41) * mm, "mid": v(10.04, 27.48) * mm, "end": v(9.97, 27.41) * mm});
            skArc(sketch, "E2746", {"start": v(9.46, 27.41) * mm, "mid": v(9.53, 27.35) * mm, "end": v(9.6, 27.41) * mm});
            skArc(sketch, "E2747", {"start": v(9.6, 27.41) * mm, "mid": v(9.53, 27.48) * mm, "end": v(9.46, 27.41) * mm});
            skArc(sketch, "E2748", {"start": v(10.99, 27.41) * mm, "mid": v(11.05, 27.35) * mm, "end": v(11.12, 27.41) * mm});
            skArc(sketch, "E2749", {"start": v(11.12, 27.41) * mm, "mid": v(11.05, 27.48) * mm, "end": v(10.99, 27.41) * mm});
            skArc(sketch, "E2750", {"start": v(11, 28.91) * mm, "mid": v(11.06, 28.85) * mm, "end": v(11.12, 28.91) * mm});
            skArc(sketch, "E2751", {"start": v(11.12, 28.91) * mm, "mid": v(11.06, 28.97) * mm, "end": v(11, 28.91) * mm});
            skArc(sketch, "E2752", {"start": v(9.47, 28.91) * mm, "mid": v(9.54, 28.85) * mm, "end": v(9.6, 28.91) * mm});
            skArc(sketch, "E2753", {"start": v(9.6, 28.91) * mm, "mid": v(9.54, 28.97) * mm, "end": v(9.47, 28.91) * mm});
            skArc(sketch, "E2754", {"start": v(9.98, 28.91) * mm, "mid": v(10.04, 28.85) * mm, "end": v(10.1, 28.91) * mm});
            skArc(sketch, "E2755", {"start": v(10.1, 28.91) * mm, "mid": v(10.04, 28.97) * mm, "end": v(9.98, 28.91) * mm});
            skArc(sketch, "E2756", {"start": v(10.49, 28.91) * mm, "mid": v(10.55, 28.85) * mm, "end": v(10.61, 28.91) * mm});
            skArc(sketch, "E2757", {"start": v(10.61, 28.91) * mm, "mid": v(10.55, 28.97) * mm, "end": v(10.49, 28.91) * mm});
            skArc(sketch, "E2758", {"start": v(8.45, 27.41) * mm, "mid": v(8.51, 27.35) * mm, "end": v(8.58, 27.41) * mm});
            skArc(sketch, "E2759", {"start": v(8.58, 27.41) * mm, "mid": v(8.51, 27.48) * mm, "end": v(8.45, 27.41) * mm});
            skArc(sketch, "E2760", {"start": v(7.94, 27.41) * mm, "mid": v(8, 27.35) * mm, "end": v(8.07, 27.41) * mm});
            skArc(sketch, "E2761", {"start": v(8.07, 27.41) * mm, "mid": v(8, 27.48) * mm, "end": v(7.94, 27.41) * mm});
            skArc(sketch, "E2762", {"start": v(7.43, 27.41) * mm, "mid": v(7.5, 27.35) * mm, "end": v(7.56, 27.41) * mm});
            skArc(sketch, "E2763", {"start": v(7.56, 27.41) * mm, "mid": v(7.5, 27.48) * mm, "end": v(7.43, 27.41) * mm});
            skArc(sketch, "E2764", {"start": v(8.96, 27.41) * mm, "mid": v(9.02, 27.35) * mm, "end": v(9.08, 27.41) * mm});
            skArc(sketch, "E2765", {"start": v(9.08, 27.41) * mm, "mid": v(9.02, 27.48) * mm, "end": v(8.96, 27.41) * mm});
            skArc(sketch, "E2766", {"start": v(8.96, 28.91) * mm, "mid": v(9.03, 28.85) * mm, "end": v(9.1, 28.91) * mm});
            skArc(sketch, "E2767", {"start": v(9.1, 28.91) * mm, "mid": v(9.03, 28.97) * mm, "end": v(8.96, 28.91) * mm});
            skArc(sketch, "E2768", {"start": v(7.44, 28.91) * mm, "mid": v(7.5, 28.85) * mm, "end": v(7.57, 28.91) * mm});
            skArc(sketch, "E2769", {"start": v(7.57, 28.91) * mm, "mid": v(7.5, 28.97) * mm, "end": v(7.44, 28.91) * mm});
            skArc(sketch, "E2770", {"start": v(7.95, 28.91) * mm, "mid": v(8.01, 28.85) * mm, "end": v(8.07, 28.91) * mm});
            skArc(sketch, "E2771", {"start": v(8.07, 28.91) * mm, "mid": v(8.01, 28.97) * mm, "end": v(7.95, 28.91) * mm});
            skArc(sketch, "E2772", {"start": v(8.46, 28.91) * mm, "mid": v(8.52, 28.85) * mm, "end": v(8.58, 28.91) * mm});
            skArc(sketch, "E2773", {"start": v(8.58, 28.91) * mm, "mid": v(8.52, 28.97) * mm, "end": v(8.46, 28.91) * mm});
            skArc(sketch, "E2774", {"start": v(3.37, 27.46) * mm, "mid": v(3.43, 27.4) * mm, "end": v(3.5, 27.46) * mm});
            skArc(sketch, "E2775", {"start": v(3.5, 27.46) * mm, "mid": v(3.43, 27.53) * mm, "end": v(3.37, 27.46) * mm});
            skArc(sketch, "E2776", {"start": v(4.9, 27.41) * mm, "mid": v(4.96, 27.35) * mm, "end": v(5.02, 27.41) * mm});
            skArc(sketch, "E2777", {"start": v(5.02, 27.41) * mm, "mid": v(4.96, 27.48) * mm, "end": v(4.9, 27.41) * mm});
            skArc(sketch, "E2778", {"start": v(5.4, 27.41) * mm, "mid": v(5.46, 27.35) * mm, "end": v(5.53, 27.41) * mm});
            skArc(sketch, "E2779", {"start": v(5.53, 27.41) * mm, "mid": v(5.46, 27.48) * mm, "end": v(5.4, 27.41) * mm});
            skArc(sketch, "E2780", {"start": v(5.9, 27.41) * mm, "mid": v(5.97, 27.35) * mm, "end": v(6.04, 27.41) * mm});
            skArc(sketch, "E2781", {"start": v(6.04, 27.41) * mm, "mid": v(5.97, 27.48) * mm, "end": v(5.9, 27.41) * mm});
            skArc(sketch, "E2782", {"start": v(6.42, 27.41) * mm, "mid": v(6.48, 27.35) * mm, "end": v(6.54, 27.41) * mm});
            skArc(sketch, "E2783", {"start": v(6.54, 27.41) * mm, "mid": v(6.48, 27.48) * mm, "end": v(6.42, 27.41) * mm});
            skArc(sketch, "E2784", {"start": v(4.38, 27.41) * mm, "mid": v(4.45, 27.35) * mm, "end": v(4.51, 27.41) * mm});
            skArc(sketch, "E2785", {"start": v(4.51, 27.41) * mm, "mid": v(4.45, 27.48) * mm, "end": v(4.38, 27.41) * mm});
            skArc(sketch, "E2786", {"start": v(3.88, 27.41) * mm, "mid": v(3.94, 27.35) * mm, "end": v(4, 27.41) * mm});
            skArc(sketch, "E2787", {"start": v(4, 27.41) * mm, "mid": v(3.94, 27.48) * mm, "end": v(3.88, 27.41) * mm});
            skArc(sketch, "E2788", {"start": v(3.38, 28.91) * mm, "mid": v(3.44, 28.85) * mm, "end": v(3.5, 28.91) * mm});
            skArc(sketch, "E2789", {"start": v(3.5, 28.91) * mm, "mid": v(3.44, 28.97) * mm, "end": v(3.38, 28.91) * mm});
            skArc(sketch, "E2790", {"start": v(4.9, 28.91) * mm, "mid": v(4.96, 28.85) * mm, "end": v(5.03, 28.91) * mm});
            skArc(sketch, "E2791", {"start": v(5.03, 28.91) * mm, "mid": v(4.96, 28.97) * mm, "end": v(4.9, 28.91) * mm});
            skArc(sketch, "E2792", {"start": v(5.4, 28.91) * mm, "mid": v(5.47, 28.85) * mm, "end": v(5.53, 28.91) * mm});
            skArc(sketch, "E2793", {"start": v(5.53, 28.91) * mm, "mid": v(5.47, 28.97) * mm, "end": v(5.4, 28.91) * mm});
            skArc(sketch, "E2794", {"start": v(5.92, 28.91) * mm, "mid": v(5.98, 28.85) * mm, "end": v(6.04, 28.91) * mm});
            skArc(sketch, "E2795", {"start": v(6.04, 28.91) * mm, "mid": v(5.98, 28.97) * mm, "end": v(5.92, 28.91) * mm});
            skArc(sketch, "E2796", {"start": v(6.42, 28.91) * mm, "mid": v(6.49, 28.85) * mm, "end": v(6.55, 28.91) * mm});
            skArc(sketch, "E2797", {"start": v(6.55, 28.91) * mm, "mid": v(6.49, 28.97) * mm, "end": v(6.42, 28.91) * mm});
            skArc(sketch, "E2798", {"start": v(4.4, 28.91) * mm, "mid": v(4.46, 28.85) * mm, "end": v(4.52, 28.91) * mm});
            skArc(sketch, "E2799", {"start": v(4.52, 28.91) * mm, "mid": v(4.46, 28.97) * mm, "end": v(4.4, 28.91) * mm});
            skArc(sketch, "E2800", {"start": v(3.88, 28.91) * mm, "mid": v(3.95, 28.85) * mm, "end": v(4.01, 28.91) * mm});
            skArc(sketch, "E2801", {"start": v(4.01, 28.91) * mm, "mid": v(3.95, 28.97) * mm, "end": v(3.88, 28.91) * mm});
            skArc(sketch, "E2802", {"start": v(11.52, 49.8) * mm, "mid": v(11.58, 49.74) * mm, "end": v(11.65, 49.8) * mm});
            skArc(sketch, "E2803", {"start": v(11.65, 49.8) * mm, "mid": v(11.58, 49.87) * mm, "end": v(11.52, 49.8) * mm});
            skArc(sketch, "E2804", {"start": v(11.01, 49.5) * mm, "mid": v(11.08, 49.43) * mm, "end": v(11.14, 49.5) * mm});
            skArc(sketch, "E2805", {"start": v(11.14, 49.5) * mm, "mid": v(11.08, 49.56) * mm, "end": v(11.01, 49.5) * mm});
            skArc(sketch, "E2806", {"start": v(8.08, 45.19) * mm, "mid": v(8.15, 45.13) * mm, "end": v(8.2, 45.19) * mm});
            skArc(sketch, "E2807", {"start": v(8.2, 45.19) * mm, "mid": v(8.15, 45.25) * mm, "end": v(8.08, 45.19) * mm});
            skArc(sketch, "E2808", {"start": v(7.55, 44.94) * mm, "mid": v(7.61, 44.87) * mm, "end": v(7.68, 44.94) * mm});
            skArc(sketch, "E2809", {"start": v(7.68, 44.94) * mm, "mid": v(7.61, 45) * mm, "end": v(7.55, 44.94) * mm});
            skArc(sketch, "E2810", {"start": v(8.84, 46.96) * mm, "mid": v(8.9, 46.9) * mm, "end": v(8.97, 46.96) * mm});
            skArc(sketch, "E2811", {"start": v(8.97, 46.96) * mm, "mid": v(8.9, 47.02) * mm, "end": v(8.84, 46.96) * mm});
            skArc(sketch, "E2812", {"start": v(8.84, 47.46) * mm, "mid": v(8.9, 47.4) * mm, "end": v(8.97, 47.46) * mm});
            skArc(sketch, "E2813", {"start": v(8.97, 47.46) * mm, "mid": v(8.9, 47.53) * mm, "end": v(8.84, 47.46) * mm});
            skArc(sketch, "E2814", {"start": v(8.84, 47.97) * mm, "mid": v(8.9, 47.9) * mm, "end": v(8.97, 47.97) * mm});
            skArc(sketch, "E2815", {"start": v(8.97, 47.97) * mm, "mid": v(8.9, 48.04) * mm, "end": v(8.84, 47.97) * mm});
            skArc(sketch, "E2816", {"start": v(10.34, 46.95) * mm, "mid": v(10.4, 46.88) * mm, "end": v(10.47, 46.95) * mm});
            skArc(sketch, "E2817", {"start": v(10.47, 46.95) * mm, "mid": v(10.4, 47.01) * mm, "end": v(10.34, 46.95) * mm});
            skArc(sketch, "E2818", {"start": v(10.34, 47.96) * mm, "mid": v(10.4, 47.9) * mm, "end": v(10.47, 47.96) * mm});
            skArc(sketch, "E2819", {"start": v(10.47, 47.96) * mm, "mid": v(10.4, 48.03) * mm, "end": v(10.34, 47.96) * mm});
            skArc(sketch, "E2820", {"start": v(10.34, 47.45) * mm, "mid": v(10.4, 47.4) * mm, "end": v(10.47, 47.45) * mm});
            skArc(sketch, "E2821", {"start": v(10.47, 47.45) * mm, "mid": v(10.4, 47.52) * mm, "end": v(10.34, 47.45) * mm});
            skArc(sketch, "E2822", {"start": v(8.51, 45.57) * mm, "mid": v(8.58, 45.5) * mm, "end": v(8.64, 45.57) * mm});
            skArc(sketch, "E2823", {"start": v(8.64, 45.57) * mm, "mid": v(8.58, 45.63) * mm, "end": v(8.51, 45.57) * mm});
            skArc(sketch, "E2824", {"start": v(8.74, 46.03) * mm, "mid": v(8.8, 45.96) * mm, "end": v(8.87, 46.03) * mm});
            skArc(sketch, "E2825", {"start": v(8.87, 46.03) * mm, "mid": v(8.8, 46.1) * mm, "end": v(8.74, 46.03) * mm});
            skArc(sketch, "E2826", {"start": v(10.34, 46.44) * mm, "mid": v(10.4, 46.38) * mm, "end": v(10.47, 46.44) * mm});
            skArc(sketch, "E2827", {"start": v(10.47, 46.44) * mm, "mid": v(10.4, 46.5) * mm, "end": v(10.34, 46.44) * mm});
            skArc(sketch, "E2828", {"start": v(8.84, 46.45) * mm, "mid": v(8.9, 46.39) * mm, "end": v(8.97, 46.45) * mm});
            skArc(sketch, "E2829", {"start": v(8.97, 46.45) * mm, "mid": v(8.9, 46.51) * mm, "end": v(8.84, 46.45) * mm});
            skArc(sketch, "E2830", {"start": v(7.6, 43.53) * mm, "mid": v(7.67, 43.46) * mm, "end": v(7.74, 43.53) * mm});
            skArc(sketch, "E2831", {"start": v(7.74, 43.53) * mm, "mid": v(7.67, 43.6) * mm, "end": v(7.6, 43.53) * mm});
            skArc(sketch, "E2832", {"start": v(8.22, 43.7) * mm, "mid": v(8.28, 43.64) * mm, "end": v(8.35, 43.7) * mm});
            skArc(sketch, "E2833", {"start": v(8.35, 43.7) * mm, "mid": v(8.28, 43.77) * mm, "end": v(8.22, 43.7) * mm});
            skArc(sketch, "E2834", {"start": v(8.83, 44) * mm, "mid": v(8.9, 43.94) * mm, "end": v(8.96, 44) * mm});
            skArc(sketch, "E2835", {"start": v(8.96, 44) * mm, "mid": v(8.9, 44.06) * mm, "end": v(8.83, 44) * mm});
            skArc(sketch, "E2836", {"start": v(9.3, 44.36) * mm, "mid": v(9.37, 44.3) * mm, "end": v(9.43, 44.36) * mm});
            skArc(sketch, "E2837", {"start": v(9.43, 44.36) * mm, "mid": v(9.37, 44.42) * mm, "end": v(9.3, 44.36) * mm});
            skArc(sketch, "E2838", {"start": v(9.7, 44.82) * mm, "mid": v(9.77, 44.75) * mm, "end": v(9.83, 44.82) * mm});
            skArc(sketch, "E2839", {"start": v(9.83, 44.82) * mm, "mid": v(9.77, 44.88) * mm, "end": v(9.7, 44.82) * mm});
            skArc(sketch, "E2840", {"start": v(10.08, 45.42) * mm, "mid": v(10.14, 45.35) * mm, "end": v(10.2, 45.42) * mm});
            skArc(sketch, "E2841", {"start": v(10.2, 45.42) * mm, "mid": v(10.14, 45.48) * mm, "end": v(10.08, 45.42) * mm});
            skArc(sketch, "E2842", {"start": v(10.26, 45.92) * mm, "mid": v(10.33, 45.85) * mm, "end": v(10.4, 45.92) * mm});
            skArc(sketch, "E2843", {"start": v(10.4, 45.92) * mm, "mid": v(10.33, 45.98) * mm, "end": v(10.26, 45.92) * mm});
            skArc(sketch, "E2844", {"start": v(8.85, 48.5) * mm, "mid": v(8.91, 48.44) * mm, "end": v(8.98, 48.5) * mm});
            skArc(sketch, "E2845", {"start": v(8.98, 48.5) * mm, "mid": v(8.91, 48.57) * mm, "end": v(8.85, 48.5) * mm});
            skArc(sketch, "E2846", {"start": v(9.15, 49.5) * mm, "mid": v(9.22, 49.43) * mm, "end": v(9.28, 49.5) * mm});
            skArc(sketch, "E2847", {"start": v(9.28, 49.5) * mm, "mid": v(9.22, 49.56) * mm, "end": v(9.15, 49.5) * mm});
            skArc(sketch, "E2848", {"start": v(9.43, 49.98) * mm, "mid": v(9.5, 49.91) * mm, "end": v(9.56, 49.98) * mm});
            skArc(sketch, "E2849", {"start": v(9.56, 49.98) * mm, "mid": v(9.5, 50.04) * mm, "end": v(9.43, 49.98) * mm});
            skArc(sketch, "E2850", {"start": v(9.81, 50.43) * mm, "mid": v(9.88, 50.37) * mm, "end": v(9.94, 50.43) * mm});
            skArc(sketch, "E2851", {"start": v(9.94, 50.43) * mm, "mid": v(9.88, 50.5) * mm, "end": v(9.81, 50.43) * mm});
            skArc(sketch, "E2852", {"start": v(10.3, 50.84) * mm, "mid": v(10.36, 50.78) * mm, "end": v(10.42, 50.84) * mm});
            skArc(sketch, "E2853", {"start": v(10.42, 50.84) * mm, "mid": v(10.36, 50.9) * mm, "end": v(10.3, 50.84) * mm});
            skArc(sketch, "E2854", {"start": v(10.83, 51.13) * mm, "mid": v(10.9, 51.06) * mm, "end": v(10.96, 51.13) * mm});
            skArc(sketch, "E2855", {"start": v(10.96, 51.13) * mm, "mid": v(10.9, 51.19) * mm, "end": v(10.83, 51.13) * mm});
            skArc(sketch, "E2856", {"start": v(6.98, 43.5) * mm, "mid": v(7.05, 43.44) * mm, "end": v(7.1, 43.5) * mm});
            skArc(sketch, "E2857", {"start": v(7.1, 43.5) * mm, "mid": v(7.05, 43.57) * mm, "end": v(6.98, 43.5) * mm});
            skArc(sketch, "E2858", {"start": v(6.97, 44.86) * mm, "mid": v(7.04, 44.8) * mm, "end": v(7.1, 44.86) * mm});
            skArc(sketch, "E2859", {"start": v(7.1, 44.86) * mm, "mid": v(7.04, 44.92) * mm, "end": v(6.97, 44.86) * mm});
            skArc(sketch, "E2860", {"start": v(10.6, 49.04) * mm, "mid": v(10.67, 48.98) * mm, "end": v(10.73, 49.04) * mm});
            skArc(sketch, "E2861", {"start": v(10.73, 49.04) * mm, "mid": v(10.67, 49.1) * mm, "end": v(10.6, 49.04) * mm});
            skArc(sketch, "E2862", {"start": v(10.36, 48.5) * mm, "mid": v(10.42, 48.43) * mm, "end": v(10.48, 48.5) * mm});
            skArc(sketch, "E2863", {"start": v(10.48, 48.5) * mm, "mid": v(10.42, 48.56) * mm, "end": v(10.36, 48.5) * mm});
            skArc(sketch, "E2864", {"start": v(11.52, 51.29) * mm, "mid": v(11.58, 51.22) * mm, "end": v(11.65, 51.29) * mm});
            skArc(sketch, "E2865", {"start": v(11.65, 51.29) * mm, "mid": v(11.58, 51.35) * mm, "end": v(11.52, 51.29) * mm});
            skArc(sketch, "E2866", {"start": v(3.42, 44.86) * mm, "mid": v(3.48, 44.8) * mm, "end": v(3.55, 44.86) * mm});
            skArc(sketch, "E2867", {"start": v(3.55, 44.86) * mm, "mid": v(3.48, 44.92) * mm, "end": v(3.42, 44.86) * mm});
            skArc(sketch, "E2868", {"start": v(3.93, 44.86) * mm, "mid": v(4, 44.8) * mm, "end": v(4.05, 44.86) * mm});
            skArc(sketch, "E2869", {"start": v(4.05, 44.86) * mm, "mid": v(4, 44.92) * mm, "end": v(3.93, 44.86) * mm});
            skArc(sketch, "E2870", {"start": v(4.43, 44.86) * mm, "mid": v(4.5, 44.8) * mm, "end": v(4.56, 44.86) * mm});
            skArc(sketch, "E2871", {"start": v(4.56, 44.86) * mm, "mid": v(4.5, 44.92) * mm, "end": v(4.43, 44.86) * mm});
            skArc(sketch, "E2872", {"start": v(6.47, 44.86) * mm, "mid": v(6.53, 44.8) * mm, "end": v(6.6, 44.86) * mm});
            skArc(sketch, "E2873", {"start": v(6.6, 44.86) * mm, "mid": v(6.53, 44.92) * mm, "end": v(6.47, 44.86) * mm});
            skArc(sketch, "E2874", {"start": v(5.96, 44.86) * mm, "mid": v(6.02, 44.8) * mm, "end": v(6.09, 44.86) * mm});
            skArc(sketch, "E2875", {"start": v(6.09, 44.86) * mm, "mid": v(6.02, 44.92) * mm, "end": v(5.96, 44.86) * mm});
            skArc(sketch, "E2876", {"start": v(5.45, 44.86) * mm, "mid": v(5.51, 44.8) * mm, "end": v(5.58, 44.86) * mm});
            skArc(sketch, "E2877", {"start": v(5.58, 44.86) * mm, "mid": v(5.51, 44.92) * mm, "end": v(5.45, 44.86) * mm});
            skArc(sketch, "E2878", {"start": v(4.94, 44.86) * mm, "mid": v(5, 44.8) * mm, "end": v(5.07, 44.86) * mm});
            skArc(sketch, "E2879", {"start": v(5.07, 44.86) * mm, "mid": v(5, 44.92) * mm, "end": v(4.94, 44.86) * mm});
            skArc(sketch, "E2880", {"start": v(4.95, 43.5) * mm, "mid": v(5.01, 43.44) * mm, "end": v(5.08, 43.5) * mm});
            skArc(sketch, "E2881", {"start": v(5.08, 43.5) * mm, "mid": v(5.01, 43.57) * mm, "end": v(4.95, 43.5) * mm});
            skArc(sketch, "E2882", {"start": v(5.46, 43.5) * mm, "mid": v(5.52, 43.44) * mm, "end": v(5.59, 43.5) * mm});
            skArc(sketch, "E2883", {"start": v(5.59, 43.5) * mm, "mid": v(5.52, 43.57) * mm, "end": v(5.46, 43.5) * mm});
            skArc(sketch, "E2884", {"start": v(5.97, 43.5) * mm, "mid": v(6.03, 43.44) * mm, "end": v(6.1, 43.5) * mm});
            skArc(sketch, "E2885", {"start": v(6.1, 43.5) * mm, "mid": v(6.03, 43.57) * mm, "end": v(5.97, 43.5) * mm});
            skArc(sketch, "E2886", {"start": v(6.47, 43.5) * mm, "mid": v(6.54, 43.44) * mm, "end": v(6.6, 43.5) * mm});
            skArc(sketch, "E2887", {"start": v(6.6, 43.5) * mm, "mid": v(6.54, 43.57) * mm, "end": v(6.47, 43.5) * mm});
            skArc(sketch, "E2888", {"start": v(3.43, 43.5) * mm, "mid": v(3.49, 43.44) * mm, "end": v(3.55, 43.5) * mm});
            skArc(sketch, "E2889", {"start": v(3.55, 43.5) * mm, "mid": v(3.49, 43.57) * mm, "end": v(3.43, 43.5) * mm});
            skArc(sketch, "E2890", {"start": v(11.6, 54.18) * mm, "mid": v(11.66, 54.12) * mm, "end": v(11.72, 54.18) * mm});
            skArc(sketch, "E2891", {"start": v(11.72, 54.18) * mm, "mid": v(11.66, 54.24) * mm, "end": v(11.6, 54.18) * mm});
            skArc(sketch, "E2892", {"start": v(8.9, 55.19) * mm, "mid": v(8.97, 55.12) * mm, "end": v(9.03, 55.19) * mm});
            skArc(sketch, "E2893", {"start": v(9.03, 55.19) * mm, "mid": v(8.97, 55.25) * mm, "end": v(8.9, 55.19) * mm});
            skArc(sketch, "E2894", {"start": v(8.78, 57.35) * mm, "mid": v(8.84, 57.28) * mm, "end": v(8.9, 57.35) * mm});
            skArc(sketch, "E2895", {"start": v(8.9, 57.35) * mm, "mid": v(8.84, 57.4) * mm, "end": v(8.78, 57.35) * mm});
            skArc(sketch, "E2896", {"start": v(9.03, 54.58) * mm, "mid": v(9.1, 54.51) * mm, "end": v(9.16, 54.58) * mm});
            skArc(sketch, "E2897", {"start": v(9.16, 54.58) * mm, "mid": v(9.1, 54.64) * mm, "end": v(9.03, 54.58) * mm});
            skArc(sketch, "E2898", {"start": v(10.86, 52.82) * mm, "mid": v(10.92, 52.76) * mm, "end": v(10.99, 52.82) * mm});
            skArc(sketch, "E2899", {"start": v(10.99, 52.82) * mm, "mid": v(10.92, 52.89) * mm, "end": v(10.86, 52.82) * mm});
            skArc(sketch, "E2900", {"start": v(10.2, 53.18) * mm, "mid": v(10.26, 53.12) * mm, "end": v(10.33, 53.18) * mm});
            skArc(sketch, "E2901", {"start": v(10.33, 53.18) * mm, "mid": v(10.26, 53.24) * mm, "end": v(10.2, 53.18) * mm});
            skArc(sketch, "E2902", {"start": v(9.7, 53.56) * mm, "mid": v(9.76, 53.5) * mm, "end": v(9.82, 53.56) * mm});
            skArc(sketch, "E2903", {"start": v(9.82, 53.56) * mm, "mid": v(9.76, 53.62) * mm, "end": v(9.7, 53.56) * mm});
            skArc(sketch, "E2904", {"start": v(9.31, 54.02) * mm, "mid": v(9.38, 53.95) * mm, "end": v(9.44, 54.02) * mm});
            skArc(sketch, "E2905", {"start": v(9.44, 54.02) * mm, "mid": v(9.38, 54.08) * mm, "end": v(9.31, 54.02) * mm});
            skArc(sketch, "E2906", {"start": v(10.66, 54.78) * mm, "mid": v(10.72, 54.72) * mm, "end": v(10.78, 54.78) * mm});
            skArc(sketch, "E2907", {"start": v(10.78, 54.78) * mm, "mid": v(10.72, 54.84) * mm, "end": v(10.66, 54.78) * mm});
            skArc(sketch, "E2908", {"start": v(10.42, 55.29) * mm, "mid": v(10.48, 55.22) * mm, "end": v(10.54, 55.29) * mm});
            skArc(sketch, "E2909", {"start": v(10.54, 55.29) * mm, "mid": v(10.48, 55.35) * mm, "end": v(10.42, 55.29) * mm});
            skArc(sketch, "E2910", {"start": v(10.28, 57.35) * mm, "mid": v(10.34, 57.29) * mm, "end": v(10.4, 57.35) * mm});
            skArc(sketch, "E2911", {"start": v(10.4, 57.35) * mm, "mid": v(10.34, 57.42) * mm, "end": v(10.28, 57.35) * mm});
            skArc(sketch, "E2912", {"start": v(10.28, 56.85) * mm, "mid": v(10.34, 56.78) * mm, "end": v(10.4, 56.85) * mm});
            skArc(sketch, "E2913", {"start": v(10.4, 56.85) * mm, "mid": v(10.34, 56.9) * mm, "end": v(10.28, 56.85) * mm});
            skArc(sketch, "E2914", {"start": v(8.16, 60.7) * mm, "mid": v(8.22, 60.65) * mm, "end": v(8.28, 60.7) * mm});
            skArc(sketch, "E2915", {"start": v(8.28, 60.7) * mm, "mid": v(8.22, 60.77) * mm, "end": v(8.16, 60.7) * mm});
            skArc(sketch, "E2916", {"start": v(8.71, 60.43) * mm, "mid": v(8.78, 60.37) * mm, "end": v(8.84, 60.43) * mm});
            skArc(sketch, "E2917", {"start": v(8.84, 60.43) * mm, "mid": v(8.78, 60.5) * mm, "end": v(8.71, 60.43) * mm});
            skArc(sketch, "E2918", {"start": v(8.6, 58.32) * mm, "mid": v(8.66, 58.26) * mm, "end": v(8.73, 58.32) * mm});
            skArc(sketch, "E2919", {"start": v(8.73, 58.32) * mm, "mid": v(8.66, 58.39) * mm, "end": v(8.6, 58.32) * mm});
            skArc(sketch, "E2920", {"start": v(8.78, 57.87) * mm, "mid": v(8.84, 57.8) * mm, "end": v(8.9, 57.87) * mm});
            skArc(sketch, "E2921", {"start": v(8.9, 57.87) * mm, "mid": v(8.84, 57.93) * mm, "end": v(8.78, 57.87) * mm});
            skArc(sketch, "E2922", {"start": v(10.4, 56.85) * mm, "mid": v(10.34, 56.91) * mm, "end": v(10.28, 56.85) * mm});
            skArc(sketch, "E2923", {"start": v(10.28, 56.34) * mm, "mid": v(10.34, 56.28) * mm, "end": v(10.4, 56.34) * mm});
            skArc(sketch, "E2924", {"start": v(10.4, 56.34) * mm, "mid": v(10.34, 56.4) * mm, "end": v(10.28, 56.34) * mm});
            skArc(sketch, "E2925", {"start": v(10.28, 55.83) * mm, "mid": v(10.34, 55.77) * mm, "end": v(10.4, 55.83) * mm});
            skArc(sketch, "E2926", {"start": v(10.4, 55.83) * mm, "mid": v(10.34, 55.9) * mm, "end": v(10.28, 55.83) * mm});
            skArc(sketch, "E2927", {"start": v(10.28, 57.36) * mm, "mid": v(10.34, 57.3) * mm, "end": v(10.4, 57.36) * mm});
            skArc(sketch, "E2928", {"start": v(10.4, 57.36) * mm, "mid": v(10.34, 57.42) * mm, "end": v(10.28, 57.36) * mm});
            skArc(sketch, "E2929", {"start": v(10.29, 57.93) * mm, "mid": v(10.35, 57.87) * mm, "end": v(10.42, 57.93) * mm});
            skArc(sketch, "E2930", {"start": v(10.42, 57.93) * mm, "mid": v(10.35, 58) * mm, "end": v(10.29, 57.93) * mm});
            skArc(sketch, "E2931", {"start": v(10.16, 58.54) * mm, "mid": v(10.23, 58.48) * mm, "end": v(10.29, 58.54) * mm});
            skArc(sketch, "E2932", {"start": v(10.29, 58.54) * mm, "mid": v(10.23, 58.6) * mm, "end": v(10.16, 58.54) * mm});
            skArc(sketch, "E2933", {"start": v(11.06, 54.4) * mm, "mid": v(11.13, 54.35) * mm, "end": v(11.2, 54.4) * mm});
            skArc(sketch, "E2934", {"start": v(11.2, 54.4) * mm, "mid": v(11.13, 54.47) * mm, "end": v(11.06, 54.4) * mm});
            skArc(sketch, "E2935", {"start": v(8.78, 55.82) * mm, "mid": v(8.84, 55.76) * mm, "end": v(8.9, 55.82) * mm});
            skArc(sketch, "E2936", {"start": v(8.9, 55.82) * mm, "mid": v(8.84, 55.89) * mm, "end": v(8.78, 55.82) * mm});
            skArc(sketch, "E2937", {"start": v(8.78, 56.33) * mm, "mid": v(8.84, 56.27) * mm, "end": v(8.9, 56.33) * mm});
            skArc(sketch, "E2938", {"start": v(8.9, 56.33) * mm, "mid": v(8.84, 56.4) * mm, "end": v(8.78, 56.33) * mm});
            skArc(sketch, "E2939", {"start": v(8.78, 56.84) * mm, "mid": v(8.84, 56.78) * mm, "end": v(8.9, 56.84) * mm});
            skArc(sketch, "E2940", {"start": v(8.9, 56.84) * mm, "mid": v(8.84, 56.9) * mm, "end": v(8.78, 56.84) * mm});
            skArc(sketch, "E2941", {"start": v(8.9, 57.35) * mm, "mid": v(8.84, 57.41) * mm, "end": v(8.78, 57.35) * mm});
            skArc(sketch, "E2942", {"start": v(9.93, 59.14) * mm, "mid": v(10, 59.08) * mm, "end": v(10.06, 59.14) * mm});
            skArc(sketch, "E2943", {"start": v(10.06, 59.14) * mm, "mid": v(10, 59.2) * mm, "end": v(9.93, 59.14) * mm});
            skArc(sketch, "E2944", {"start": v(9.64, 59.62) * mm, "mid": v(9.7, 59.56) * mm, "end": v(9.76, 59.62) * mm});
            skArc(sketch, "E2945", {"start": v(9.76, 59.62) * mm, "mid": v(9.7, 59.68) * mm, "end": v(9.64, 59.62) * mm});
            skArc(sketch, "E2946", {"start": v(11.52, 52.62) * mm, "mid": v(11.58, 52.56) * mm, "end": v(11.65, 52.62) * mm});
            skArc(sketch, "E2947", {"start": v(11.65, 52.62) * mm, "mid": v(11.58, 52.68) * mm, "end": v(11.52, 52.62) * mm});
            skArc(sketch, "E2948", {"start": v(4.44, 43.5) * mm, "mid": v(4.5, 43.44) * mm, "end": v(4.57, 43.5) * mm});
            skArc(sketch, "E2949", {"start": v(4.57, 43.5) * mm, "mid": v(4.5, 43.57) * mm, "end": v(4.44, 43.5) * mm});
            skArc(sketch, "E2950", {"start": v(3.93, 43.5) * mm, "mid": v(4, 43.44) * mm, "end": v(4.06, 43.5) * mm});
            skArc(sketch, "E2951", {"start": v(4.06, 43.5) * mm, "mid": v(4, 43.57) * mm, "end": v(3.93, 43.5) * mm});
            skArc(sketch, "E2952", {"start": v(6.97, 60.89) * mm, "mid": v(7.04, 60.83) * mm, "end": v(7.1, 60.89) * mm});
            skArc(sketch, "E2953", {"start": v(7.1, 60.89) * mm, "mid": v(7.04, 60.95) * mm, "end": v(6.97, 60.89) * mm});
            skArc(sketch, "E2954", {"start": v(6.98, 59.4) * mm, "mid": v(7.05, 59.33) * mm, "end": v(7.1, 59.4) * mm});
            skArc(sketch, "E2955", {"start": v(7.1, 59.4) * mm, "mid": v(7.05, 59.46) * mm, "end": v(6.98, 59.4) * mm});
            skArc(sketch, "E2956", {"start": v(9.22, 60.05) * mm, "mid": v(9.29, 59.98) * mm, "end": v(9.35, 60.05) * mm});
            skArc(sketch, "E2957", {"start": v(9.35, 60.05) * mm, "mid": v(9.29, 60.11) * mm, "end": v(9.22, 60.05) * mm});
            skArc(sketch, "E2958", {"start": v(7.52, 59.3) * mm, "mid": v(7.58, 59.24) * mm, "end": v(7.64, 59.3) * mm});
            skArc(sketch, "E2959", {"start": v(7.64, 59.3) * mm, "mid": v(7.58, 59.36) * mm, "end": v(7.52, 59.3) * mm});
            skArc(sketch, "E2960", {"start": v(7.52, 60.86) * mm, "mid": v(7.58, 60.8) * mm, "end": v(7.65, 60.86) * mm});
            skArc(sketch, "E2961", {"start": v(7.65, 60.86) * mm, "mid": v(7.58, 60.93) * mm, "end": v(7.52, 60.86) * mm});
            skArc(sketch, "E2962", {"start": v(8.37, 58.77) * mm, "mid": v(8.44, 58.7) * mm, "end": v(8.5, 58.77) * mm});
            skArc(sketch, "E2963", {"start": v(8.5, 58.77) * mm, "mid": v(8.44, 58.83) * mm, "end": v(8.37, 58.77) * mm});
            skArc(sketch, "E2964", {"start": v(8.02, 59.1) * mm, "mid": v(8.08, 59.03) * mm, "end": v(8.14, 59.1) * mm});
            skArc(sketch, "E2965", {"start": v(8.14, 59.1) * mm, "mid": v(8.08, 59.16) * mm, "end": v(8.02, 59.1) * mm});
            skArc(sketch, "E2966", {"start": v(3.42, 60.89) * mm, "mid": v(3.48, 60.83) * mm, "end": v(3.55, 60.89) * mm});
            skArc(sketch, "E2967", {"start": v(3.55, 60.89) * mm, "mid": v(3.48, 60.95) * mm, "end": v(3.42, 60.89) * mm});
            skArc(sketch, "E2968", {"start": v(4.94, 60.89) * mm, "mid": v(5, 60.83) * mm, "end": v(5.07, 60.89) * mm});
            skArc(sketch, "E2969", {"start": v(5.07, 60.89) * mm, "mid": v(5, 60.95) * mm, "end": v(4.94, 60.89) * mm});
            skArc(sketch, "E2970", {"start": v(5.45, 60.89) * mm, "mid": v(5.51, 60.83) * mm, "end": v(5.58, 60.89) * mm});
            skArc(sketch, "E2971", {"start": v(5.58, 60.89) * mm, "mid": v(5.51, 60.95) * mm, "end": v(5.45, 60.89) * mm});
            skArc(sketch, "E2972", {"start": v(5.96, 60.89) * mm, "mid": v(6.02, 60.83) * mm, "end": v(6.09, 60.89) * mm});
            skArc(sketch, "E2973", {"start": v(6.09, 60.89) * mm, "mid": v(6.02, 60.95) * mm, "end": v(5.96, 60.89) * mm});
            skArc(sketch, "E2974", {"start": v(6.47, 60.89) * mm, "mid": v(6.53, 60.83) * mm, "end": v(6.6, 60.89) * mm});
            skArc(sketch, "E2975", {"start": v(6.6, 60.89) * mm, "mid": v(6.53, 60.95) * mm, "end": v(6.47, 60.89) * mm});
            skArc(sketch, "E2976", {"start": v(4.43, 60.89) * mm, "mid": v(4.5, 60.83) * mm, "end": v(4.56, 60.89) * mm});
            skArc(sketch, "E2977", {"start": v(4.56, 60.89) * mm, "mid": v(4.5, 60.95) * mm, "end": v(4.43, 60.89) * mm});
            skArc(sketch, "E2978", {"start": v(3.93, 60.89) * mm, "mid": v(4, 60.83) * mm, "end": v(4.05, 60.89) * mm});
            skArc(sketch, "E2979", {"start": v(4.05, 60.89) * mm, "mid": v(4, 60.95) * mm, "end": v(3.93, 60.89) * mm});
            skArc(sketch, "E2980", {"start": v(3.43, 59.4) * mm, "mid": v(3.49, 59.33) * mm, "end": v(3.55, 59.4) * mm});
            skArc(sketch, "E2981", {"start": v(3.55, 59.4) * mm, "mid": v(3.49, 59.46) * mm, "end": v(3.43, 59.4) * mm});
            skArc(sketch, "E2982", {"start": v(4.95, 59.4) * mm, "mid": v(5.01, 59.33) * mm, "end": v(5.08, 59.4) * mm});
            skArc(sketch, "E2983", {"start": v(5.08, 59.4) * mm, "mid": v(5.01, 59.46) * mm, "end": v(4.95, 59.4) * mm});
            skArc(sketch, "E2984", {"start": v(5.46, 59.4) * mm, "mid": v(5.52, 59.33) * mm, "end": v(5.59, 59.4) * mm});
            skArc(sketch, "E2985", {"start": v(5.59, 59.4) * mm, "mid": v(5.52, 59.46) * mm, "end": v(5.46, 59.4) * mm});
            skArc(sketch, "E2986", {"start": v(5.97, 59.4) * mm, "mid": v(6.03, 59.33) * mm, "end": v(6.1, 59.4) * mm});
            skArc(sketch, "E2987", {"start": v(6.1, 59.4) * mm, "mid": v(6.03, 59.46) * mm, "end": v(5.97, 59.4) * mm});
            skArc(sketch, "E2988", {"start": v(6.47, 59.4) * mm, "mid": v(6.54, 59.33) * mm, "end": v(6.6, 59.4) * mm});
            skArc(sketch, "E2989", {"start": v(6.6, 59.4) * mm, "mid": v(6.54, 59.46) * mm, "end": v(6.47, 59.4) * mm});
            skArc(sketch, "E2990", {"start": v(4.44, 59.4) * mm, "mid": v(4.5, 59.33) * mm, "end": v(4.57, 59.4) * mm});
            skArc(sketch, "E2991", {"start": v(4.57, 59.4) * mm, "mid": v(4.5, 59.46) * mm, "end": v(4.44, 59.4) * mm});
            skArc(sketch, "E2992", {"start": v(3.93, 59.4) * mm, "mid": v(4, 59.33) * mm, "end": v(4.06, 59.4) * mm});
            skArc(sketch, "E2993", {"start": v(4.06, 59.4) * mm, "mid": v(4, 59.46) * mm, "end": v(3.93, 59.4) * mm});
            skArc(sketch, "E2994", {"start": v(17.08, 55.3) * mm, "mid": v(17.15, 55.24) * mm, "end": v(17.21, 55.3) * mm});
            skArc(sketch, "E2995", {"start": v(17.21, 55.3) * mm, "mid": v(17.15, 55.37) * mm, "end": v(17.08, 55.3) * mm});
            skArc(sketch, "E2996", {"start": v(16.5, 55.4) * mm, "mid": v(16.56, 55.34) * mm, "end": v(16.63, 55.4) * mm});
            skArc(sketch, "E2997", {"start": v(16.63, 55.4) * mm, "mid": v(16.56, 55.47) * mm, "end": v(16.5, 55.4) * mm});
            skArc(sketch, "E2998", {"start": v(15.88, 55.7) * mm, "mid": v(15.95, 55.64) * mm, "end": v(16, 55.7) * mm});
            skArc(sketch, "E2999", {"start": v(16, 55.7) * mm, "mid": v(15.95, 55.77) * mm, "end": v(15.88, 55.7) * mm});
            skArc(sketch, "E3000", {"start": v(15.35, 56.06) * mm, "mid": v(15.41, 56) * mm, "end": v(15.48, 56.06) * mm});
            skArc(sketch, "E3001", {"start": v(15.48, 56.06) * mm, "mid": v(15.41, 56.13) * mm, "end": v(15.35, 56.06) * mm});
            skArc(sketch, "E3002", {"start": v(14.82, 56.55) * mm, "mid": v(14.89, 56.48) * mm, "end": v(14.95, 56.55) * mm});
            skArc(sketch, "E3003", {"start": v(14.95, 56.55) * mm, "mid": v(14.89, 56.61) * mm, "end": v(14.82, 56.55) * mm});
            skArc(sketch, "E3004", {"start": v(14.5, 57.1) * mm, "mid": v(14.56, 57.04) * mm, "end": v(14.62, 57.1) * mm});
            skArc(sketch, "E3005", {"start": v(14.62, 57.1) * mm, "mid": v(14.56, 57.17) * mm, "end": v(14.5, 57.1) * mm});
            skArc(sketch, "E3006", {"start": v(14.24, 57.7) * mm, "mid": v(14.3, 57.63) * mm, "end": v(14.37, 57.7) * mm});
            skArc(sketch, "E3007", {"start": v(14.37, 57.7) * mm, "mid": v(14.3, 57.75) * mm, "end": v(14.24, 57.7) * mm});
            skArc(sketch, "E3008", {"start": v(14.2, 58.29) * mm, "mid": v(14.27, 58.22) * mm, "end": v(14.33, 58.29) * mm});
            skArc(sketch, "E3009", {"start": v(14.33, 58.29) * mm, "mid": v(14.27, 58.35) * mm, "end": v(14.2, 58.29) * mm});
            skArc(sketch, "E3010", {"start": v(17.13, 56.8) * mm, "mid": v(17.2, 56.75) * mm, "end": v(17.26, 56.8) * mm});
            skArc(sketch, "E3011", {"start": v(17.26, 56.8) * mm, "mid": v(17.2, 56.87) * mm, "end": v(17.13, 56.8) * mm});
            skArc(sketch, "E3012", {"start": v(16.63, 56.98) * mm, "mid": v(16.7, 56.91) * mm, "end": v(16.75, 56.98) * mm});
            skArc(sketch, "E3013", {"start": v(16.75, 56.98) * mm, "mid": v(16.7, 57.04) * mm, "end": v(16.63, 56.98) * mm});
            skArc(sketch, "E3014", {"start": v(15.9, 57.74) * mm, "mid": v(15.96, 57.68) * mm, "end": v(16.02, 57.74) * mm});
            skArc(sketch, "E3015", {"start": v(16.02, 57.74) * mm, "mid": v(15.96, 57.8) * mm, "end": v(15.9, 57.74) * mm});
            skArc(sketch, "E3016", {"start": v(15.71, 74.06) * mm, "mid": v(15.78, 74) * mm, "end": v(15.84, 74.06) * mm});
            skArc(sketch, "E3017", {"start": v(15.84, 74.06) * mm, "mid": v(15.78, 74.12) * mm, "end": v(15.71, 74.06) * mm});
            skArc(sketch, "E3018", {"start": v(15.66, 74.56) * mm, "mid": v(15.72, 74.5) * mm, "end": v(15.79, 74.56) * mm});
            skArc(sketch, "E3019", {"start": v(15.79, 74.56) * mm, "mid": v(15.72, 74.63) * mm, "end": v(15.66, 74.56) * mm});
            skArc(sketch, "E3020", {"start": v(15.48, 75.12) * mm, "mid": v(15.54, 75.06) * mm, "end": v(15.6, 75.12) * mm});
            skArc(sketch, "E3021", {"start": v(15.6, 75.12) * mm, "mid": v(15.54, 75.19) * mm, "end": v(15.48, 75.12) * mm});
            skArc(sketch, "E3022", {"start": v(16.69, 54.07) * mm, "mid": v(16.75, 54) * mm, "end": v(16.81, 54.07) * mm});
            skArc(sketch, "E3023", {"start": v(16.81, 54.07) * mm, "mid": v(16.75, 54.13) * mm, "end": v(16.69, 54.07) * mm});
            skArc(sketch, "E3024", {"start": v(16.68, 52.57) * mm, "mid": v(16.74, 52.5) * mm, "end": v(16.8, 52.57) * mm});
            skArc(sketch, "E3025", {"start": v(16.8, 52.57) * mm, "mid": v(16.74, 52.64) * mm, "end": v(16.68, 52.57) * mm});
            skArc(sketch, "E3026", {"start": v(16.69, 51.37) * mm, "mid": v(16.75, 51.3) * mm, "end": v(16.81, 51.37) * mm});
            skArc(sketch, "E3027", {"start": v(16.81, 51.37) * mm, "mid": v(16.75, 51.43) * mm, "end": v(16.69, 51.37) * mm});
            skArc(sketch, "E3028", {"start": v(16.68, 49.87) * mm, "mid": v(16.74, 49.8) * mm, "end": v(16.8, 49.87) * mm});
            skArc(sketch, "E3029", {"start": v(16.8, 49.87) * mm, "mid": v(16.74, 49.94) * mm, "end": v(16.68, 49.87) * mm});
            skArc(sketch, "E3030", {"start": v(17.7, 52.57) * mm, "mid": v(17.76, 52.5) * mm, "end": v(17.82, 52.57) * mm});
            skArc(sketch, "E3031", {"start": v(17.82, 52.57) * mm, "mid": v(17.76, 52.64) * mm, "end": v(17.7, 52.57) * mm});
            skArc(sketch, "E3032", {"start": v(17.7, 54.07) * mm, "mid": v(17.77, 54) * mm, "end": v(17.83, 54.07) * mm});
            skArc(sketch, "E3033", {"start": v(17.83, 54.07) * mm, "mid": v(17.77, 54.13) * mm, "end": v(17.7, 54.07) * mm});
            skArc(sketch, "E3034", {"start": v(17.7, 51.37) * mm, "mid": v(17.77, 51.3) * mm, "end": v(17.83, 51.37) * mm});
            skArc(sketch, "E3035", {"start": v(17.83, 51.37) * mm, "mid": v(17.77, 51.43) * mm, "end": v(17.7, 51.37) * mm});
            skArc(sketch, "E3036", {"start": v(17.7, 49.87) * mm, "mid": v(17.76, 49.8) * mm, "end": v(17.82, 49.87) * mm});
            skArc(sketch, "E3037", {"start": v(17.82, 49.87) * mm, "mid": v(17.76, 49.94) * mm, "end": v(17.7, 49.87) * mm});
            skArc(sketch, "E3038", {"start": v(18.21, 51.37) * mm, "mid": v(18.28, 51.3) * mm, "end": v(18.34, 51.37) * mm});
            skArc(sketch, "E3039", {"start": v(18.34, 51.37) * mm, "mid": v(18.28, 51.43) * mm, "end": v(18.21, 51.37) * mm});
            skArc(sketch, "E3040", {"start": v(18.21, 54.07) * mm, "mid": v(18.28, 54) * mm, "end": v(18.34, 54.07) * mm});
            skArc(sketch, "E3041", {"start": v(18.34, 54.07) * mm, "mid": v(18.28, 54.13) * mm, "end": v(18.21, 54.07) * mm});
            skArc(sketch, "E3042", {"start": v(18.2, 52.57) * mm, "mid": v(18.27, 52.5) * mm, "end": v(18.33, 52.57) * mm});
            skArc(sketch, "E3043", {"start": v(18.33, 52.57) * mm, "mid": v(18.27, 52.64) * mm, "end": v(18.2, 52.57) * mm});
            skArc(sketch, "E3044", {"start": v(18.2, 49.87) * mm, "mid": v(18.27, 49.8) * mm, "end": v(18.33, 49.87) * mm});
            skArc(sketch, "E3045", {"start": v(18.33, 49.87) * mm, "mid": v(18.27, 49.94) * mm, "end": v(18.2, 49.87) * mm});
            skArc(sketch, "E3046", {"start": v(17.19, 52.57) * mm, "mid": v(17.25, 52.5) * mm, "end": v(17.32, 52.57) * mm});
            skArc(sketch, "E3047", {"start": v(17.32, 52.57) * mm, "mid": v(17.25, 52.64) * mm, "end": v(17.19, 52.57) * mm});
            skArc(sketch, "E3048", {"start": v(17.2, 54.07) * mm, "mid": v(17.26, 54) * mm, "end": v(17.32, 54.07) * mm});
            skArc(sketch, "E3049", {"start": v(17.32, 54.07) * mm, "mid": v(17.26, 54.13) * mm, "end": v(17.2, 54.07) * mm});
            skArc(sketch, "E3050", {"start": v(17.2, 51.37) * mm, "mid": v(17.26, 51.3) * mm, "end": v(17.32, 51.37) * mm});
            skArc(sketch, "E3051", {"start": v(17.32, 51.37) * mm, "mid": v(17.26, 51.43) * mm, "end": v(17.2, 51.37) * mm});
            skArc(sketch, "E3052", {"start": v(17.19, 49.87) * mm, "mid": v(17.25, 49.8) * mm, "end": v(17.31, 49.87) * mm});
            skArc(sketch, "E3053", {"start": v(17.31, 49.87) * mm, "mid": v(17.25, 49.94) * mm, "end": v(17.19, 49.87) * mm});
            skArc(sketch, "E3054", {"start": v(15.16, 54.07) * mm, "mid": v(15.23, 54) * mm, "end": v(15.3, 54.07) * mm});
            skArc(sketch, "E3055", {"start": v(15.3, 54.07) * mm, "mid": v(15.23, 54.13) * mm, "end": v(15.16, 54.07) * mm});
            skArc(sketch, "E3056", {"start": v(15.67, 54.07) * mm, "mid": v(15.74, 54) * mm, "end": v(15.8, 54.07) * mm});
            skArc(sketch, "E3057", {"start": v(15.8, 54.07) * mm, "mid": v(15.74, 54.13) * mm, "end": v(15.67, 54.07) * mm});
            skArc(sketch, "E3058", {"start": v(16.18, 54.07) * mm, "mid": v(16.24, 54) * mm, "end": v(16.3, 54.07) * mm});
            skArc(sketch, "E3059", {"start": v(16.3, 54.07) * mm, "mid": v(16.24, 54.13) * mm, "end": v(16.18, 54.07) * mm});
            skArc(sketch, "E3060", {"start": v(15.16, 52.57) * mm, "mid": v(15.22, 52.5) * mm, "end": v(15.28, 52.57) * mm});
            skArc(sketch, "E3061", {"start": v(15.28, 52.57) * mm, "mid": v(15.22, 52.64) * mm, "end": v(15.16, 52.57) * mm});
            skArc(sketch, "E3062", {"start": v(15.66, 52.57) * mm, "mid": v(15.73, 52.5) * mm, "end": v(15.8, 52.57) * mm});
            skArc(sketch, "E3063", {"start": v(15.8, 52.57) * mm, "mid": v(15.73, 52.64) * mm, "end": v(15.66, 52.57) * mm});
            skArc(sketch, "E3064", {"start": v(16.17, 52.57) * mm, "mid": v(16.24, 52.5) * mm, "end": v(16.3, 52.57) * mm});
            skArc(sketch, "E3065", {"start": v(16.3, 52.57) * mm, "mid": v(16.24, 52.64) * mm, "end": v(16.17, 52.57) * mm});
            skArc(sketch, "E3066", {"start": v(16.18, 51.37) * mm, "mid": v(16.24, 51.3) * mm, "end": v(16.3, 51.37) * mm});
            skArc(sketch, "E3067", {"start": v(16.3, 51.37) * mm, "mid": v(16.24, 51.43) * mm, "end": v(16.18, 51.37) * mm});
            skArc(sketch, "E3068", {"start": v(15.67, 51.37) * mm, "mid": v(15.74, 51.3) * mm, "end": v(15.8, 51.37) * mm});
            skArc(sketch, "E3069", {"start": v(15.8, 51.37) * mm, "mid": v(15.74, 51.43) * mm, "end": v(15.67, 51.37) * mm});
            skArc(sketch, "E3070", {"start": v(15.16, 51.37) * mm, "mid": v(15.23, 51.3) * mm, "end": v(15.3, 51.37) * mm});
            skArc(sketch, "E3071", {"start": v(15.3, 51.37) * mm, "mid": v(15.23, 51.43) * mm, "end": v(15.16, 51.37) * mm});
            skArc(sketch, "E3072", {"start": v(16.17, 49.87) * mm, "mid": v(16.23, 49.8) * mm, "end": v(16.3, 49.87) * mm});
            skArc(sketch, "E3073", {"start": v(16.3, 49.87) * mm, "mid": v(16.23, 49.94) * mm, "end": v(16.17, 49.87) * mm});
            skArc(sketch, "E3074", {"start": v(15.66, 49.87) * mm, "mid": v(15.73, 49.8) * mm, "end": v(15.79, 49.87) * mm});
            skArc(sketch, "E3075", {"start": v(15.79, 49.87) * mm, "mid": v(15.73, 49.94) * mm, "end": v(15.66, 49.87) * mm});
            skArc(sketch, "E3076", {"start": v(15.15, 49.87) * mm, "mid": v(15.22, 49.8) * mm, "end": v(15.28, 49.87) * mm});
            skArc(sketch, "E3077", {"start": v(15.28, 49.87) * mm, "mid": v(15.22, 49.94) * mm, "end": v(15.15, 49.87) * mm});
            skArc(sketch, "E3078", {"start": v(14.15, 54.07) * mm, "mid": v(14.21, 54) * mm, "end": v(14.27, 54.07) * mm});
            skArc(sketch, "E3079", {"start": v(14.27, 54.07) * mm, "mid": v(14.21, 54.13) * mm, "end": v(14.15, 54.07) * mm});
            skArc(sketch, "E3080", {"start": v(13.64, 54.07) * mm, "mid": v(13.7, 54) * mm, "end": v(13.77, 54.07) * mm});
            skArc(sketch, "E3081", {"start": v(13.77, 54.07) * mm, "mid": v(13.7, 54.13) * mm, "end": v(13.64, 54.07) * mm});
            skArc(sketch, "E3082", {"start": v(14.66, 54.07) * mm, "mid": v(14.72, 54) * mm, "end": v(14.78, 54.07) * mm});
            skArc(sketch, "E3083", {"start": v(14.78, 54.07) * mm, "mid": v(14.72, 54.13) * mm, "end": v(14.66, 54.07) * mm});
            skArc(sketch, "E3084", {"start": v(13.63, 52.57) * mm, "mid": v(13.7, 52.5) * mm, "end": v(13.76, 52.57) * mm});
            skArc(sketch, "E3085", {"start": v(13.76, 52.57) * mm, "mid": v(13.7, 52.64) * mm, "end": v(13.63, 52.57) * mm});
            skArc(sketch, "E3086", {"start": v(14.14, 52.57) * mm, "mid": v(14.2, 52.5) * mm, "end": v(14.27, 52.57) * mm});
            skArc(sketch, "E3087", {"start": v(14.27, 52.57) * mm, "mid": v(14.2, 52.64) * mm, "end": v(14.14, 52.57) * mm});
            skArc(sketch, "E3088", {"start": v(14.65, 52.57) * mm, "mid": v(14.71, 52.5) * mm, "end": v(14.78, 52.57) * mm});
            skArc(sketch, "E3089", {"start": v(14.78, 52.57) * mm, "mid": v(14.71, 52.64) * mm, "end": v(14.65, 52.57) * mm});
            skArc(sketch, "E3090", {"start": v(14.66, 51.37) * mm, "mid": v(14.72, 51.3) * mm, "end": v(14.78, 51.37) * mm});
            skArc(sketch, "E3091", {"start": v(14.78, 51.37) * mm, "mid": v(14.72, 51.43) * mm, "end": v(14.66, 51.37) * mm});
            skArc(sketch, "E3092", {"start": v(14.65, 49.87) * mm, "mid": v(14.7, 49.8) * mm, "end": v(14.77, 49.87) * mm});
            skArc(sketch, "E3093", {"start": v(14.77, 49.87) * mm, "mid": v(14.7, 49.94) * mm, "end": v(14.65, 49.87) * mm});
            skArc(sketch, "E3094", {"start": v(13.64, 51.37) * mm, "mid": v(13.7, 51.3) * mm, "end": v(13.77, 51.37) * mm});
            skArc(sketch, "E3095", {"start": v(13.77, 51.37) * mm, "mid": v(13.7, 51.43) * mm, "end": v(13.64, 51.37) * mm});
            skArc(sketch, "E3096", {"start": v(14.15, 51.37) * mm, "mid": v(14.21, 51.3) * mm, "end": v(14.27, 51.37) * mm});
            skArc(sketch, "E3097", {"start": v(14.27, 51.37) * mm, "mid": v(14.21, 51.43) * mm, "end": v(14.15, 51.37) * mm});
            skArc(sketch, "E3098", {"start": v(14.14, 49.87) * mm, "mid": v(14.2, 49.8) * mm, "end": v(14.26, 49.87) * mm});
            skArc(sketch, "E3099", {"start": v(14.26, 49.87) * mm, "mid": v(14.2, 49.94) * mm, "end": v(14.14, 49.87) * mm});
            skArc(sketch, "E3100", {"start": v(13.63, 49.87) * mm, "mid": v(13.7, 49.8) * mm, "end": v(13.76, 49.87) * mm});
            skArc(sketch, "E3101", {"start": v(13.76, 49.87) * mm, "mid": v(13.7, 49.94) * mm, "end": v(13.63, 49.87) * mm});
            skArc(sketch, "E3102", {"start": v(13.12, 52.57) * mm, "mid": v(13.19, 52.5) * mm, "end": v(13.25, 52.57) * mm});
            skArc(sketch, "E3103", {"start": v(13.25, 52.57) * mm, "mid": v(13.19, 52.64) * mm, "end": v(13.12, 52.57) * mm});
            skArc(sketch, "E3104", {"start": v(13.1, 75.26) * mm, "mid": v(13.16, 75.2) * mm, "end": v(13.23, 75.26) * mm});
            skArc(sketch, "E3105", {"start": v(13.23, 75.26) * mm, "mid": v(13.16, 75.32) * mm, "end": v(13.1, 75.26) * mm});
            skArc(sketch, "E3106", {"start": v(13.58, 75) * mm, "mid": v(13.64, 74.93) * mm, "end": v(13.7, 75) * mm});
            skArc(sketch, "E3107", {"start": v(13.7, 75) * mm, "mid": v(13.64, 75.06) * mm, "end": v(13.58, 75) * mm});
            skArc(sketch, "E3108", {"start": v(12.1, 52.57) * mm, "mid": v(12.17, 52.5) * mm, "end": v(12.24, 52.57) * mm});
            skArc(sketch, "E3109", {"start": v(12.24, 52.57) * mm, "mid": v(12.17, 52.64) * mm, "end": v(12.1, 52.57) * mm});
            skArc(sketch, "E3110", {"start": v(12.62, 52.57) * mm, "mid": v(12.68, 52.5) * mm, "end": v(12.74, 52.57) * mm});
            skArc(sketch, "E3111", {"start": v(12.74, 52.57) * mm, "mid": v(12.68, 52.64) * mm, "end": v(12.62, 52.57) * mm});
            skArc(sketch, "E3112", {"start": v(12.62, 54.07) * mm, "mid": v(12.69, 54) * mm, "end": v(12.75, 54.07) * mm});
            skArc(sketch, "E3113", {"start": v(12.75, 54.07) * mm, "mid": v(12.69, 54.13) * mm, "end": v(12.62, 54.07) * mm});
            skArc(sketch, "E3114", {"start": v(12.12, 54.07) * mm, "mid": v(12.18, 54) * mm, "end": v(12.24, 54.07) * mm});
            skArc(sketch, "E3115", {"start": v(12.24, 54.07) * mm, "mid": v(12.18, 54.13) * mm, "end": v(12.12, 54.07) * mm});
            skArc(sketch, "E3116", {"start": v(13.94, 74.57) * mm, "mid": v(14, 74.5) * mm, "end": v(14.07, 74.57) * mm});
            skArc(sketch, "E3117", {"start": v(14.07, 74.57) * mm, "mid": v(14, 74.64) * mm, "end": v(13.94, 74.57) * mm});
            skArc(sketch, "E3118", {"start": v(14.14, 74.06) * mm, "mid": v(14.2, 74) * mm, "end": v(14.27, 74.06) * mm});
            skArc(sketch, "E3119", {"start": v(14.27, 74.06) * mm, "mid": v(14.2, 74.13) * mm, "end": v(14.14, 74.06) * mm});
            skArc(sketch, "E3120", {"start": v(13.13, 54.07) * mm, "mid": v(13.2, 54) * mm, "end": v(13.26, 54.07) * mm});
            skArc(sketch, "E3121", {"start": v(13.26, 54.07) * mm, "mid": v(13.2, 54.13) * mm, "end": v(13.13, 54.07) * mm});
            skArc(sketch, "E3122", {"start": v(13.12, 49.87) * mm, "mid": v(13.19, 49.8) * mm, "end": v(13.25, 49.87) * mm});
            skArc(sketch, "E3123", {"start": v(13.25, 49.87) * mm, "mid": v(13.19, 49.94) * mm, "end": v(13.12, 49.87) * mm});
            skArc(sketch, "E3124", {"start": v(13.8, 76.7) * mm, "mid": v(13.87, 76.63) * mm, "end": v(13.93, 76.7) * mm});
            skArc(sketch, "E3125", {"start": v(13.93, 76.7) * mm, "mid": v(13.87, 76.76) * mm, "end": v(13.8, 76.7) * mm});
            skArc(sketch, "E3126", {"start": v(14.31, 76.4) * mm, "mid": v(14.38, 76.33) * mm, "end": v(14.44, 76.4) * mm});
            skArc(sketch, "E3127", {"start": v(14.44, 76.4) * mm, "mid": v(14.38, 76.46) * mm, "end": v(14.31, 76.4) * mm});
            skArc(sketch, "E3128", {"start": v(12.1, 49.87) * mm, "mid": v(12.17, 49.8) * mm, "end": v(12.23, 49.87) * mm});
            skArc(sketch, "E3129", {"start": v(12.23, 49.87) * mm, "mid": v(12.17, 49.94) * mm, "end": v(12.1, 49.87) * mm});
            skArc(sketch, "E3130", {"start": v(12.61, 49.87) * mm, "mid": v(12.68, 49.8) * mm, "end": v(12.74, 49.87) * mm});
            skArc(sketch, "E3131", {"start": v(12.74, 49.87) * mm, "mid": v(12.68, 49.94) * mm, "end": v(12.61, 49.87) * mm});
            skArc(sketch, "E3132", {"start": v(12.62, 51.37) * mm, "mid": v(12.69, 51.3) * mm, "end": v(12.75, 51.37) * mm});
            skArc(sketch, "E3133", {"start": v(12.75, 51.37) * mm, "mid": v(12.69, 51.43) * mm, "end": v(12.62, 51.37) * mm});
            skArc(sketch, "E3134", {"start": v(12.12, 51.37) * mm, "mid": v(12.18, 51.3) * mm, "end": v(12.24, 51.37) * mm});
            skArc(sketch, "E3135", {"start": v(12.24, 51.37) * mm, "mid": v(12.18, 51.43) * mm, "end": v(12.12, 51.37) * mm});
            skArc(sketch, "E3136", {"start": v(14.77, 76.04) * mm, "mid": v(14.83, 75.97) * mm, "end": v(14.9, 76.04) * mm});
            skArc(sketch, "E3137", {"start": v(14.9, 76.04) * mm, "mid": v(14.83, 76.1) * mm, "end": v(14.77, 76.04) * mm});
            skArc(sketch, "E3138", {"start": v(15.13, 75.6) * mm, "mid": v(15.19, 75.54) * mm, "end": v(15.25, 75.6) * mm});
            skArc(sketch, "E3139", {"start": v(15.25, 75.6) * mm, "mid": v(15.19, 75.67) * mm, "end": v(15.13, 75.6) * mm});
            skArc(sketch, "E3140", {"start": v(13.13, 51.37) * mm, "mid": v(13.2, 51.3) * mm, "end": v(13.26, 51.37) * mm});
            skArc(sketch, "E3141", {"start": v(13.26, 51.37) * mm, "mid": v(13.2, 51.43) * mm, "end": v(13.13, 51.37) * mm});
            skArc(sketch, "E3142", {"start": v(23.28, 47.22) * mm, "mid": v(23.34, 47.16) * mm, "end": v(23.4, 47.22) * mm});
            skArc(sketch, "E3143", {"start": v(23.4, 47.22) * mm, "mid": v(23.34, 47.29) * mm, "end": v(23.28, 47.22) * mm});
            skArc(sketch, "E3144", {"start": v(23.29, 48.72) * mm, "mid": v(23.35, 48.66) * mm, "end": v(23.42, 48.72) * mm});
            skArc(sketch, "E3145", {"start": v(23.42, 48.72) * mm, "mid": v(23.35, 48.79) * mm, "end": v(23.29, 48.72) * mm});
            skArc(sketch, "E3146", {"start": v(24.8, 47.22) * mm, "mid": v(24.87, 47.16) * mm, "end": v(24.93, 47.22) * mm});
            skArc(sketch, "E3147", {"start": v(24.93, 47.22) * mm, "mid": v(24.87, 47.29) * mm, "end": v(24.8, 47.22) * mm});
            skArc(sketch, "E3148", {"start": v(24.3, 47.22) * mm, "mid": v(24.36, 47.16) * mm, "end": v(24.42, 47.22) * mm});
            skArc(sketch, "E3149", {"start": v(24.42, 47.22) * mm, "mid": v(24.36, 47.29) * mm, "end": v(24.3, 47.22) * mm});
            skArc(sketch, "E3150", {"start": v(23.79, 47.22) * mm, "mid": v(23.85, 47.16) * mm, "end": v(23.91, 47.22) * mm});
            skArc(sketch, "E3151", {"start": v(23.91, 47.22) * mm, "mid": v(23.85, 47.29) * mm, "end": v(23.79, 47.22) * mm});
            skArc(sketch, "E3152", {"start": v(24.81, 48.72) * mm, "mid": v(24.88, 48.66) * mm, "end": v(24.94, 48.72) * mm});
            skArc(sketch, "E3153", {"start": v(24.94, 48.72) * mm, "mid": v(24.88, 48.79) * mm, "end": v(24.81, 48.72) * mm});
            skArc(sketch, "E3154", {"start": v(24.3, 48.72) * mm, "mid": v(24.37, 48.66) * mm, "end": v(24.43, 48.72) * mm});
            skArc(sketch, "E3155", {"start": v(24.43, 48.72) * mm, "mid": v(24.37, 48.79) * mm, "end": v(24.3, 48.72) * mm});
            skArc(sketch, "E3156", {"start": v(23.8, 48.72) * mm, "mid": v(23.86, 48.66) * mm, "end": v(23.92, 48.72) * mm});
            skArc(sketch, "E3157", {"start": v(23.92, 48.72) * mm, "mid": v(23.86, 48.79) * mm, "end": v(23.8, 48.72) * mm});
            skArc(sketch, "E3158", {"start": v(21.76, 47.22) * mm, "mid": v(21.82, 47.16) * mm, "end": v(21.88, 47.22) * mm});
            skArc(sketch, "E3159", {"start": v(21.88, 47.22) * mm, "mid": v(21.82, 47.29) * mm, "end": v(21.76, 47.22) * mm});
            skArc(sketch, "E3160", {"start": v(22.26, 47.22) * mm, "mid": v(22.33, 47.16) * mm, "end": v(22.4, 47.22) * mm});
            skArc(sketch, "E3161", {"start": v(22.4, 47.22) * mm, "mid": v(22.33, 47.29) * mm, "end": v(22.26, 47.22) * mm});
            skArc(sketch, "E3162", {"start": v(22.77, 47.22) * mm, "mid": v(22.83, 47.16) * mm, "end": v(22.9, 47.22) * mm});
            skArc(sketch, "E3163", {"start": v(22.9, 47.22) * mm, "mid": v(22.83, 47.29) * mm, "end": v(22.77, 47.22) * mm});
            skArc(sketch, "E3164", {"start": v(21.77, 48.72) * mm, "mid": v(21.83, 48.66) * mm, "end": v(21.9, 48.72) * mm});
            skArc(sketch, "E3165", {"start": v(21.9, 48.72) * mm, "mid": v(21.83, 48.79) * mm, "end": v(21.77, 48.72) * mm});
            skArc(sketch, "E3166", {"start": v(22.27, 48.72) * mm, "mid": v(22.34, 48.66) * mm, "end": v(22.4, 48.72) * mm});
            skArc(sketch, "E3167", {"start": v(22.4, 48.72) * mm, "mid": v(22.34, 48.79) * mm, "end": v(22.27, 48.72) * mm});
            skArc(sketch, "E3168", {"start": v(22.78, 48.72) * mm, "mid": v(22.84, 48.66) * mm, "end": v(22.9, 48.72) * mm});
            skArc(sketch, "E3169", {"start": v(22.9, 48.72) * mm, "mid": v(22.84, 48.79) * mm, "end": v(22.78, 48.72) * mm});
            skArc(sketch, "E3170", {"start": v(20.23, 47.22) * mm, "mid": v(20.3, 47.16) * mm, "end": v(20.36, 47.22) * mm});
            skArc(sketch, "E3171", {"start": v(20.36, 47.22) * mm, "mid": v(20.3, 47.29) * mm, "end": v(20.23, 47.22) * mm});
            skArc(sketch, "E3172", {"start": v(20.74, 47.22) * mm, "mid": v(20.8, 47.16) * mm, "end": v(20.87, 47.22) * mm});
            skArc(sketch, "E3173", {"start": v(20.87, 47.22) * mm, "mid": v(20.8, 47.29) * mm, "end": v(20.74, 47.22) * mm});
            skArc(sketch, "E3174", {"start": v(20.75, 48.72) * mm, "mid": v(20.81, 48.66) * mm, "end": v(20.88, 48.72) * mm});
            skArc(sketch, "E3175", {"start": v(20.88, 48.72) * mm, "mid": v(20.81, 48.79) * mm, "end": v(20.75, 48.72) * mm});
            skArc(sketch, "E3176", {"start": v(20.24, 48.72) * mm, "mid": v(20.3, 48.66) * mm, "end": v(20.37, 48.72) * mm});
            skArc(sketch, "E3177", {"start": v(20.37, 48.72) * mm, "mid": v(20.3, 48.79) * mm, "end": v(20.24, 48.72) * mm});
            skArc(sketch, "E3178", {"start": v(21.25, 47.22) * mm, "mid": v(21.31, 47.16) * mm, "end": v(21.37, 47.22) * mm});
            skArc(sketch, "E3179", {"start": v(21.37, 47.22) * mm, "mid": v(21.31, 47.29) * mm, "end": v(21.25, 47.22) * mm});
            skArc(sketch, "E3180", {"start": v(21.26, 48.72) * mm, "mid": v(21.32, 48.66) * mm, "end": v(21.38, 48.72) * mm});
            skArc(sketch, "E3181", {"start": v(21.38, 48.72) * mm, "mid": v(21.32, 48.79) * mm, "end": v(21.26, 48.72) * mm});
            skArc(sketch, "E3182", {"start": v(19.72, 47.22) * mm, "mid": v(19.79, 47.16) * mm, "end": v(19.85, 47.22) * mm});
            skArc(sketch, "E3183", {"start": v(19.85, 47.22) * mm, "mid": v(19.79, 47.29) * mm, "end": v(19.72, 47.22) * mm});
            skArc(sketch, "E3184", {"start": v(17.7, 47.22) * mm, "mid": v(17.75, 47.16) * mm, "end": v(17.82, 47.22) * mm});
            skArc(sketch, "E3185", {"start": v(17.82, 47.22) * mm, "mid": v(17.75, 47.29) * mm, "end": v(17.7, 47.22) * mm});
            skArc(sketch, "E3186", {"start": v(18.2, 47.22) * mm, "mid": v(18.26, 47.16) * mm, "end": v(18.33, 47.22) * mm});
            skArc(sketch, "E3187", {"start": v(18.33, 47.22) * mm, "mid": v(18.26, 47.29) * mm, "end": v(18.2, 47.22) * mm});
            skArc(sketch, "E3188", {"start": v(18.7, 47.22) * mm, "mid": v(18.77, 47.16) * mm, "end": v(18.83, 47.22) * mm});
            skArc(sketch, "E3189", {"start": v(18.83, 47.22) * mm, "mid": v(18.77, 47.29) * mm, "end": v(18.7, 47.22) * mm});
            skArc(sketch, "E3190", {"start": v(19.22, 47.22) * mm, "mid": v(19.28, 47.16) * mm, "end": v(19.34, 47.22) * mm});
            skArc(sketch, "E3191", {"start": v(19.34, 47.22) * mm, "mid": v(19.28, 47.29) * mm, "end": v(19.22, 47.22) * mm});
            skArc(sketch, "E3192", {"start": v(19.23, 48.72) * mm, "mid": v(19.29, 48.66) * mm, "end": v(19.35, 48.72) * mm});
            skArc(sketch, "E3193", {"start": v(19.35, 48.72) * mm, "mid": v(19.29, 48.79) * mm, "end": v(19.23, 48.72) * mm});
            skArc(sketch, "E3194", {"start": v(18.72, 48.72) * mm, "mid": v(18.78, 48.66) * mm, "end": v(18.84, 48.72) * mm});
            skArc(sketch, "E3195", {"start": v(18.84, 48.72) * mm, "mid": v(18.78, 48.79) * mm, "end": v(18.72, 48.72) * mm});
            skArc(sketch, "E3196", {"start": v(18.2, 48.72) * mm, "mid": v(18.27, 48.66) * mm, "end": v(18.34, 48.72) * mm});
            skArc(sketch, "E3197", {"start": v(18.34, 48.72) * mm, "mid": v(18.27, 48.79) * mm, "end": v(18.2, 48.72) * mm});
            skArc(sketch, "E3198", {"start": v(17.7, 48.72) * mm, "mid": v(17.76, 48.66) * mm, "end": v(17.83, 48.72) * mm});
            skArc(sketch, "E3199", {"start": v(17.83, 48.72) * mm, "mid": v(17.76, 48.79) * mm, "end": v(17.7, 48.72) * mm});
            skArc(sketch, "E3200", {"start": v(19.73, 48.72) * mm, "mid": v(19.8, 48.66) * mm, "end": v(19.86, 48.72) * mm});
            skArc(sketch, "E3201", {"start": v(19.86, 48.72) * mm, "mid": v(19.8, 48.79) * mm, "end": v(19.73, 48.72) * mm});
            skArc(sketch, "E3202", {"start": v(23.28, 49.88) * mm, "mid": v(23.35, 49.81) * mm, "end": v(23.4, 49.88) * mm});
            skArc(sketch, "E3203", {"start": v(23.4, 49.88) * mm, "mid": v(23.35, 49.94) * mm, "end": v(23.28, 49.88) * mm});
            skArc(sketch, "E3204", {"start": v(23.29, 51.37) * mm, "mid": v(23.35, 51.3) * mm, "end": v(23.42, 51.37) * mm});
            skArc(sketch, "E3205", {"start": v(23.42, 51.37) * mm, "mid": v(23.35, 51.44) * mm, "end": v(23.29, 51.37) * mm});
            skArc(sketch, "E3206", {"start": v(24.8, 49.88) * mm, "mid": v(24.87, 49.81) * mm, "end": v(24.93, 49.88) * mm});
            skArc(sketch, "E3207", {"start": v(24.93, 49.88) * mm, "mid": v(24.87, 49.94) * mm, "end": v(24.8, 49.88) * mm});
            skArc(sketch, "E3208", {"start": v(24.3, 49.88) * mm, "mid": v(24.36, 49.81) * mm, "end": v(24.42, 49.88) * mm});
            skArc(sketch, "E3209", {"start": v(24.42, 49.88) * mm, "mid": v(24.36, 49.94) * mm, "end": v(24.3, 49.88) * mm});
            skArc(sketch, "E3210", {"start": v(6.73, 68.2) * mm, "mid": v(7.11, 67.81) * mm, "end": v(7.5, 68.2) * mm});
            skArc(sketch, "E3211", {"start": v(7.5, 68.2) * mm, "mid": v(7.11, 68.57) * mm, "end": v(6.73, 68.2) * mm});
            skArc(sketch, "E3212", {"start": v(8.98, 49.07) * mm, "mid": v(9.04, 49) * mm, "end": v(9.1, 49.07) * mm});
            skArc(sketch, "E3213", {"start": v(9.1, 49.07) * mm, "mid": v(9.04, 49.13) * mm, "end": v(8.98, 49.07) * mm});
            skArc(sketch, "E3214", {"start": v(39.23, 46.04) * mm, "mid": v(39.3, 45.98) * mm, "end": v(39.36, 46.04) * mm});
            skArc(sketch, "E3215", {"start": v(39.36, 46.04) * mm, "mid": v(39.3, 46.1) * mm, "end": v(39.23, 46.04) * mm});
            skArc(sketch, "E3216", {"start": v(15.7, 71.01) * mm, "mid": v(15.76, 70.95) * mm, "end": v(15.83, 71.01) * mm});
            skArc(sketch, "E3217", {"start": v(15.83, 71.01) * mm, "mid": v(15.76, 71.08) * mm, "end": v(15.7, 71.01) * mm});
            skArc(sketch, "E3218", {"start": v(15.7, 71.52) * mm, "mid": v(15.76, 71.46) * mm, "end": v(15.83, 71.52) * mm});
            skArc(sketch, "E3219", {"start": v(15.83, 71.52) * mm, "mid": v(15.76, 71.58) * mm, "end": v(15.7, 71.52) * mm});
            skArc(sketch, "E3220", {"start": v(3.41, 76.94) * mm, "mid": v(3.47, 76.88) * mm, "end": v(3.54, 76.94) * mm});
            skArc(sketch, "E3221", {"start": v(3.54, 76.94) * mm, "mid": v(3.47, 77) * mm, "end": v(3.41, 76.94) * mm});
            skArc(sketch, "E3222", {"start": v(3.92, 76.94) * mm, "mid": v(3.98, 76.88) * mm, "end": v(4.05, 76.94) * mm});
            skArc(sketch, "E3223", {"start": v(4.05, 76.94) * mm, "mid": v(3.98, 77) * mm, "end": v(3.92, 76.94) * mm});
            skArc(sketch, "E3224", {"start": v(7.48, 76.94) * mm, "mid": v(7.54, 76.88) * mm, "end": v(7.6, 76.94) * mm});
            skArc(sketch, "E3225", {"start": v(7.6, 76.94) * mm, "mid": v(7.54, 77) * mm, "end": v(7.48, 76.94) * mm});
            skArc(sketch, "E3226", {"start": v(6.97, 76.94) * mm, "mid": v(7.03, 76.88) * mm, "end": v(7.1, 76.94) * mm});
            skArc(sketch, "E3227", {"start": v(7.1, 76.94) * mm, "mid": v(7.03, 77) * mm, "end": v(6.97, 76.94) * mm});
            skArc(sketch, "E3228", {"start": v(8.5, 76.94) * mm, "mid": v(8.55, 76.88) * mm, "end": v(8.62, 76.94) * mm});
            skArc(sketch, "E3229", {"start": v(8.62, 76.94) * mm, "mid": v(8.55, 77) * mm, "end": v(8.5, 76.94) * mm});
            skArc(sketch, "E3230", {"start": v(7.98, 76.94) * mm, "mid": v(8.05, 76.88) * mm, "end": v(8.11, 76.94) * mm});
            skArc(sketch, "E3231", {"start": v(8.11, 76.94) * mm, "mid": v(8.05, 77) * mm, "end": v(7.98, 76.94) * mm});
            skArc(sketch, "E3232", {"start": v(5.95, 76.94) * mm, "mid": v(6.01, 76.88) * mm, "end": v(6.08, 76.94) * mm});
            skArc(sketch, "E3233", {"start": v(6.08, 76.94) * mm, "mid": v(6.01, 77) * mm, "end": v(5.95, 76.94) * mm});
            skArc(sketch, "E3234", {"start": v(5.44, 76.94) * mm, "mid": v(5.5, 76.88) * mm, "end": v(5.57, 76.94) * mm});
            skArc(sketch, "E3235", {"start": v(5.57, 76.94) * mm, "mid": v(5.5, 77) * mm, "end": v(5.44, 76.94) * mm});
            skArc(sketch, "E3236", {"start": v(4.43, 76.94) * mm, "mid": v(4.5, 76.88) * mm, "end": v(4.55, 76.94) * mm});
            skArc(sketch, "E3237", {"start": v(4.55, 76.94) * mm, "mid": v(4.5, 77) * mm, "end": v(4.43, 76.94) * mm});
            skArc(sketch, "E3238", {"start": v(6.46, 76.94) * mm, "mid": v(6.52, 76.88) * mm, "end": v(6.59, 76.94) * mm});
            skArc(sketch, "E3239", {"start": v(6.59, 76.94) * mm, "mid": v(6.52, 77) * mm, "end": v(6.46, 76.94) * mm});
            skArc(sketch, "E3240", {"start": v(10.52, 76.94) * mm, "mid": v(10.59, 76.88) * mm, "end": v(10.65, 76.94) * mm});
            skArc(sketch, "E3241", {"start": v(10.65, 76.94) * mm, "mid": v(10.59, 77) * mm, "end": v(10.52, 76.94) * mm});
            skArc(sketch, "E3242", {"start": v(10.02, 76.94) * mm, "mid": v(10.08, 76.88) * mm, "end": v(10.14, 76.94) * mm});
            skArc(sketch, "E3243", {"start": v(10.14, 76.94) * mm, "mid": v(10.08, 77) * mm, "end": v(10.02, 76.94) * mm});
            skArc(sketch, "E3244", {"start": v(4.94, 76.94) * mm, "mid": v(5, 76.88) * mm, "end": v(5.06, 76.94) * mm});
            skArc(sketch, "E3245", {"start": v(5.06, 76.94) * mm, "mid": v(5, 77) * mm, "end": v(4.94, 76.94) * mm});
            skArc(sketch, "E3246", {"start": v(15.7, 64.4) * mm, "mid": v(15.76, 64.35) * mm, "end": v(15.83, 64.4) * mm});
            skArc(sketch, "E3247", {"start": v(15.83, 64.4) * mm, "mid": v(15.76, 64.47) * mm, "end": v(15.7, 64.4) * mm});
            skArc(sketch, "E3248", {"start": v(15.7, 63.9) * mm, "mid": v(15.76, 63.84) * mm, "end": v(15.83, 63.9) * mm});
            skArc(sketch, "E3249", {"start": v(15.83, 63.9) * mm, "mid": v(15.76, 63.96) * mm, "end": v(15.7, 63.9) * mm});
            skArc(sketch, "E3250", {"start": v(15.7, 68.98) * mm, "mid": v(15.76, 68.92) * mm, "end": v(15.83, 68.98) * mm});
            skArc(sketch, "E3251", {"start": v(15.83, 68.98) * mm, "mid": v(15.76, 69.04) * mm, "end": v(15.7, 68.98) * mm});
            skArc(sketch, "E3252", {"start": v(15.7, 68.47) * mm, "mid": v(15.76, 68.4) * mm, "end": v(15.83, 68.47) * mm});
            skArc(sketch, "E3253", {"start": v(15.83, 68.47) * mm, "mid": v(15.76, 68.54) * mm, "end": v(15.7, 68.47) * mm});
            skArc(sketch, "E3254", {"start": v(15.7, 67.97) * mm, "mid": v(15.76, 67.9) * mm, "end": v(15.83, 67.97) * mm});
            skArc(sketch, "E3255", {"start": v(15.83, 67.97) * mm, "mid": v(15.76, 68.03) * mm, "end": v(15.7, 67.97) * mm});
            skArc(sketch, "E3256", {"start": v(15.7, 65.93) * mm, "mid": v(15.76, 65.87) * mm, "end": v(15.83, 65.93) * mm});
            skArc(sketch, "E3257", {"start": v(15.83, 65.93) * mm, "mid": v(15.76, 66) * mm, "end": v(15.7, 65.93) * mm});
            skArc(sketch, "E3258", {"start": v(14.2, 65.92) * mm, "mid": v(14.26, 65.86) * mm, "end": v(14.33, 65.92) * mm});
            skArc(sketch, "E3259", {"start": v(14.33, 65.92) * mm, "mid": v(14.26, 65.99) * mm, "end": v(14.2, 65.92) * mm});
            skArc(sketch, "E3260", {"start": v(14.2, 67.96) * mm, "mid": v(14.26, 67.9) * mm, "end": v(14.33, 67.96) * mm});
            skArc(sketch, "E3261", {"start": v(14.33, 67.96) * mm, "mid": v(14.26, 68.02) * mm, "end": v(14.2, 67.96) * mm});
            skArc(sketch, "E3262", {"start": v(14.2, 61.35) * mm, "mid": v(14.26, 61.3) * mm, "end": v(14.33, 61.35) * mm});
            skArc(sketch, "E3263", {"start": v(14.33, 61.35) * mm, "mid": v(14.26, 61.42) * mm, "end": v(14.2, 61.35) * mm});
            skArc(sketch, "E3264", {"start": v(14.2, 60.85) * mm, "mid": v(14.26, 60.78) * mm, "end": v(14.33, 60.85) * mm});
            skArc(sketch, "E3265", {"start": v(14.33, 60.85) * mm, "mid": v(14.26, 60.9) * mm, "end": v(14.2, 60.85) * mm});
            skArc(sketch, "E3266", {"start": v(21.26, 55.26) * mm, "mid": v(21.33, 55.2) * mm, "end": v(21.4, 55.26) * mm});
            skArc(sketch, "E3267", {"start": v(21.4, 55.26) * mm, "mid": v(21.33, 55.33) * mm, "end": v(21.26, 55.26) * mm});
            skArc(sketch, "E3268", {"start": v(14.2, 72.53) * mm, "mid": v(14.26, 72.46) * mm, "end": v(14.33, 72.53) * mm});
            skArc(sketch, "E3269", {"start": v(14.33, 72.53) * mm, "mid": v(14.26, 72.6) * mm, "end": v(14.2, 72.53) * mm});
            skArc(sketch, "E3270", {"start": v(24.82, 54.07) * mm, "mid": v(24.88, 54) * mm, "end": v(24.94, 54.07) * mm});
            skArc(sketch, "E3271", {"start": v(24.94, 54.07) * mm, "mid": v(24.88, 54.14) * mm, "end": v(24.82, 54.07) * mm});
            skArc(sketch, "E3272", {"start": v(21.76, 52.58) * mm, "mid": v(21.82, 52.51) * mm, "end": v(21.89, 52.58) * mm});
            skArc(sketch, "E3273", {"start": v(21.89, 52.58) * mm, "mid": v(21.82, 52.64) * mm, "end": v(21.76, 52.58) * mm});
            skArc(sketch, "E3274", {"start": v(22.27, 52.58) * mm, "mid": v(22.33, 52.51) * mm, "end": v(22.4, 52.58) * mm});
            skArc(sketch, "E3275", {"start": v(22.4, 52.58) * mm, "mid": v(22.33, 52.64) * mm, "end": v(22.27, 52.58) * mm});
            skArc(sketch, "E3276", {"start": v(22.78, 52.58) * mm, "mid": v(22.84, 52.51) * mm, "end": v(22.9, 52.58) * mm});
            skArc(sketch, "E3277", {"start": v(22.9, 52.58) * mm, "mid": v(22.84, 52.64) * mm, "end": v(22.78, 52.58) * mm});
            skArc(sketch, "E3278", {"start": v(21.77, 54.07) * mm, "mid": v(21.83, 54) * mm, "end": v(21.9, 54.07) * mm});
            skArc(sketch, "E3279", {"start": v(21.9, 54.07) * mm, "mid": v(21.83, 54.14) * mm, "end": v(21.77, 54.07) * mm});
            skArc(sketch, "E3280", {"start": v(14.2, 70.5) * mm, "mid": v(14.26, 70.43) * mm, "end": v(14.33, 70.5) * mm});
            skArc(sketch, "E3281", {"start": v(14.33, 70.5) * mm, "mid": v(14.26, 70.56) * mm, "end": v(14.2, 70.5) * mm});
            skArc(sketch, "E3282", {"start": v(14.2, 71) * mm, "mid": v(14.26, 70.94) * mm, "end": v(14.33, 71) * mm});
            skArc(sketch, "E3283", {"start": v(14.33, 71) * mm, "mid": v(14.26, 71.07) * mm, "end": v(14.2, 71) * mm});
            skArc(sketch, "E3284", {"start": v(11.54, 76.94) * mm, "mid": v(11.6, 76.88) * mm, "end": v(11.67, 76.94) * mm});
            skArc(sketch, "E3285", {"start": v(11.67, 76.94) * mm, "mid": v(11.6, 77) * mm, "end": v(11.54, 76.94) * mm});
            skArc(sketch, "E3286", {"start": v(14.2, 73.04) * mm, "mid": v(14.26, 72.97) * mm, "end": v(14.33, 73.04) * mm});
            skArc(sketch, "E3287", {"start": v(14.33, 73.04) * mm, "mid": v(14.26, 73.1) * mm, "end": v(14.2, 73.04) * mm});
            skArc(sketch, "E3288", {"start": v(11.03, 76.94) * mm, "mid": v(11.1, 76.88) * mm, "end": v(11.16, 76.94) * mm});
            skArc(sketch, "E3289", {"start": v(11.16, 76.94) * mm, "mid": v(11.1, 77) * mm, "end": v(11.03, 76.94) * mm});
            skArc(sketch, "E3290", {"start": v(9, 76.94) * mm, "mid": v(9.06, 76.88) * mm, "end": v(9.13, 76.94) * mm});
            skArc(sketch, "E3291", {"start": v(9.13, 76.94) * mm, "mid": v(9.06, 77) * mm, "end": v(9, 76.94) * mm});
            skArc(sketch, "E3292", {"start": v(14.2, 72.02) * mm, "mid": v(14.26, 71.96) * mm, "end": v(14.33, 72.02) * mm});
            skArc(sketch, "E3293", {"start": v(14.33, 72.02) * mm, "mid": v(14.26, 72.08) * mm, "end": v(14.2, 72.02) * mm});
            skArc(sketch, "E3294", {"start": v(13.16, 76.9) * mm, "mid": v(13.22, 76.84) * mm, "end": v(13.29, 76.9) * mm});
            skArc(sketch, "E3295", {"start": v(13.29, 76.9) * mm, "mid": v(13.22, 76.96) * mm, "end": v(13.16, 76.9) * mm});
            skArc(sketch, "E3296", {"start": v(14.2, 73.54) * mm, "mid": v(14.26, 73.48) * mm, "end": v(14.33, 73.54) * mm});
            skArc(sketch, "E3297", {"start": v(14.33, 73.54) * mm, "mid": v(14.26, 73.6) * mm, "end": v(14.2, 73.54) * mm});
            skArc(sketch, "E3298", {"start": v(21.27, 56.76) * mm, "mid": v(21.34, 56.7) * mm, "end": v(21.4, 56.76) * mm});
            skArc(sketch, "E3299", {"start": v(21.4, 56.76) * mm, "mid": v(21.34, 56.82) * mm, "end": v(21.27, 56.76) * mm});
            skArc(sketch, "E3300", {"start": v(19.73, 52.58) * mm, "mid": v(19.8, 52.51) * mm, "end": v(19.86, 52.58) * mm});
            skArc(sketch, "E3301", {"start": v(19.86, 52.58) * mm, "mid": v(19.8, 52.64) * mm, "end": v(19.73, 52.58) * mm});
            skArc(sketch, "E3302", {"start": v(21.26, 54.07) * mm, "mid": v(21.32, 54) * mm, "end": v(21.39, 54.07) * mm});
            skArc(sketch, "E3303", {"start": v(21.39, 54.07) * mm, "mid": v(21.32, 54.14) * mm, "end": v(21.26, 54.07) * mm});
            skArc(sketch, "E3304", {"start": v(21.25, 52.58) * mm, "mid": v(21.32, 52.51) * mm, "end": v(21.38, 52.58) * mm});
            skArc(sketch, "E3305", {"start": v(21.38, 52.58) * mm, "mid": v(21.32, 52.64) * mm, "end": v(21.25, 52.58) * mm});
            skArc(sketch, "E3306", {"start": v(20.24, 54.07) * mm, "mid": v(20.3, 54) * mm, "end": v(20.37, 54.07) * mm});
            skArc(sketch, "E3307", {"start": v(20.37, 54.07) * mm, "mid": v(20.3, 54.14) * mm, "end": v(20.24, 54.07) * mm});
            skArc(sketch, "E3308", {"start": v(14.2, 58.81) * mm, "mid": v(14.26, 58.75) * mm, "end": v(14.33, 58.81) * mm});
            skArc(sketch, "E3309", {"start": v(14.33, 58.81) * mm, "mid": v(14.26, 58.88) * mm, "end": v(14.2, 58.81) * mm});
            skArc(sketch, "E3310", {"start": v(15.7, 59.33) * mm, "mid": v(15.76, 59.27) * mm, "end": v(15.82, 59.33) * mm});
            skArc(sketch, "E3311", {"start": v(15.82, 59.33) * mm, "mid": v(15.76, 59.4) * mm, "end": v(15.7, 59.33) * mm});
            skArc(sketch, "E3312", {"start": v(15.7, 58.31) * mm, "mid": v(15.76, 58.25) * mm, "end": v(15.82, 58.31) * mm});
            skArc(sketch, "E3313", {"start": v(15.82, 58.31) * mm, "mid": v(15.76, 58.38) * mm, "end": v(15.7, 58.31) * mm});
            skArc(sketch, "E3314", {"start": v(20.75, 54.07) * mm, "mid": v(20.82, 54) * mm, "end": v(20.88, 54.07) * mm});
            skArc(sketch, "E3315", {"start": v(20.88, 54.07) * mm, "mid": v(20.82, 54.14) * mm, "end": v(20.75, 54.07) * mm});
            skArc(sketch, "E3316", {"start": v(15.7, 58.82) * mm, "mid": v(15.76, 58.76) * mm, "end": v(15.82, 58.82) * mm});
            skArc(sketch, "E3317", {"start": v(15.82, 58.82) * mm, "mid": v(15.76, 58.88) * mm, "end": v(15.7, 58.82) * mm});
            skArc(sketch, "E3318", {"start": v(14.2, 61.86) * mm, "mid": v(14.26, 61.8) * mm, "end": v(14.33, 61.86) * mm});
            skArc(sketch, "E3319", {"start": v(14.33, 61.86) * mm, "mid": v(14.26, 61.93) * mm, "end": v(14.2, 61.86) * mm});
            skArc(sketch, "E3320", {"start": v(14.2, 60.34) * mm, "mid": v(14.26, 60.27) * mm, "end": v(14.33, 60.34) * mm});
            skArc(sketch, "E3321", {"start": v(14.33, 60.34) * mm, "mid": v(14.26, 60.4) * mm, "end": v(14.2, 60.34) * mm});
            skArc(sketch, "E3322", {"start": v(5.45, 75.45) * mm, "mid": v(5.51, 75.38) * mm, "end": v(5.58, 75.45) * mm});
            skArc(sketch, "E3323", {"start": v(5.58, 75.45) * mm, "mid": v(5.51, 75.5) * mm, "end": v(5.45, 75.45) * mm});
            skArc(sketch, "E3324", {"start": v(12.05, 76.94) * mm, "mid": v(12.11, 76.88) * mm, "end": v(12.17, 76.94) * mm});
            skArc(sketch, "E3325", {"start": v(12.17, 76.94) * mm, "mid": v(12.11, 77) * mm, "end": v(12.05, 76.94) * mm});
            skArc(sketch, "E3326", {"start": v(4.94, 75.45) * mm, "mid": v(5, 75.38) * mm, "end": v(5.07, 75.45) * mm});
            skArc(sketch, "E3327", {"start": v(5.07, 75.45) * mm, "mid": v(5, 75.5) * mm, "end": v(4.94, 75.45) * mm});
            skArc(sketch, "E3328", {"start": v(3.93, 75.45) * mm, "mid": v(4, 75.38) * mm, "end": v(4.05, 75.45) * mm});
            skArc(sketch, "E3329", {"start": v(4.05, 75.45) * mm, "mid": v(4, 75.5) * mm, "end": v(3.93, 75.45) * mm});
            skArc(sketch, "E3330", {"start": v(5.96, 75.45) * mm, "mid": v(6.02, 75.38) * mm, "end": v(6.09, 75.45) * mm});
            skArc(sketch, "E3331", {"start": v(6.09, 75.45) * mm, "mid": v(6.02, 75.5) * mm, "end": v(5.96, 75.45) * mm});
            skArc(sketch, "E3332", {"start": v(6.47, 75.45) * mm, "mid": v(6.53, 75.38) * mm, "end": v(6.6, 75.45) * mm});
            skArc(sketch, "E3333", {"start": v(6.6, 75.45) * mm, "mid": v(6.53, 75.5) * mm, "end": v(6.47, 75.45) * mm});
            skArc(sketch, "E3334", {"start": v(4.43, 75.45) * mm, "mid": v(4.5, 75.38) * mm, "end": v(4.56, 75.45) * mm});
            skArc(sketch, "E3335", {"start": v(4.56, 75.45) * mm, "mid": v(4.5, 75.5) * mm, "end": v(4.43, 75.45) * mm});
            skArc(sketch, "E3336", {"start": v(15.7, 62.89) * mm, "mid": v(15.76, 62.82) * mm, "end": v(15.82, 62.89) * mm});
            skArc(sketch, "E3337", {"start": v(15.82, 62.89) * mm, "mid": v(15.76, 62.95) * mm, "end": v(15.7, 62.89) * mm});
            skArc(sketch, "E3338", {"start": v(15.7, 63.4) * mm, "mid": v(15.76, 63.33) * mm, "end": v(15.82, 63.4) * mm});
            skArc(sketch, "E3339", {"start": v(15.82, 63.4) * mm, "mid": v(15.76, 63.46) * mm, "end": v(15.7, 63.4) * mm});
            skArc(sketch, "E3340", {"start": v(15.7, 63.9) * mm, "mid": v(15.76, 63.84) * mm, "end": v(15.82, 63.9) * mm});
            skArc(sketch, "E3341", {"start": v(15.82, 63.9) * mm, "mid": v(15.76, 63.96) * mm, "end": v(15.7, 63.9) * mm});
            skArc(sketch, "E3342", {"start": v(3.42, 75.45) * mm, "mid": v(3.48, 75.38) * mm, "end": v(3.55, 75.45) * mm});
            skArc(sketch, "E3343", {"start": v(3.55, 75.45) * mm, "mid": v(3.48, 75.5) * mm, "end": v(3.42, 75.45) * mm});
            skArc(sketch, "E3344", {"start": v(6.97, 75.45) * mm, "mid": v(7.04, 75.38) * mm, "end": v(7.1, 75.45) * mm});
            skArc(sketch, "E3345", {"start": v(7.1, 75.45) * mm, "mid": v(7.04, 75.5) * mm, "end": v(6.97, 75.45) * mm});
            skArc(sketch, "E3346", {"start": v(16.22, 57.3) * mm, "mid": v(16.28, 57.23) * mm, "end": v(16.35, 57.3) * mm});
            skArc(sketch, "E3347", {"start": v(16.35, 57.3) * mm, "mid": v(16.28, 57.36) * mm, "end": v(16.22, 57.3) * mm});
            skArc(sketch, "E3348", {"start": v(15.7, 60.85) * mm, "mid": v(15.76, 60.79) * mm, "end": v(15.82, 60.85) * mm});
            skArc(sketch, "E3349", {"start": v(15.82, 60.85) * mm, "mid": v(15.76, 60.92) * mm, "end": v(15.7, 60.85) * mm});
            skArc(sketch, "E3350", {"start": v(10.53, 75.45) * mm, "mid": v(10.6, 75.38) * mm, "end": v(10.66, 75.45) * mm});
            skArc(sketch, "E3351", {"start": v(10.66, 75.45) * mm, "mid": v(10.6, 75.5) * mm, "end": v(10.53, 75.45) * mm});
            skArc(sketch, "E3352", {"start": v(15.7, 61.36) * mm, "mid": v(15.76, 61.3) * mm, "end": v(15.82, 61.36) * mm});
            skArc(sketch, "E3353", {"start": v(15.82, 61.36) * mm, "mid": v(15.76, 61.42) * mm, "end": v(15.7, 61.36) * mm});
            skArc(sketch, "E3354", {"start": v(23.8, 54.07) * mm, "mid": v(23.86, 54) * mm, "end": v(23.93, 54.07) * mm});
            skArc(sketch, "E3355", {"start": v(23.93, 54.07) * mm, "mid": v(23.86, 54.14) * mm, "end": v(23.8, 54.07) * mm});
            skArc(sketch, "E3356", {"start": v(15.7, 61.87) * mm, "mid": v(15.76, 61.8) * mm, "end": v(15.82, 61.87) * mm});
            skArc(sketch, "E3357", {"start": v(15.82, 61.87) * mm, "mid": v(15.76, 61.93) * mm, "end": v(15.7, 61.87) * mm});
            skArc(sketch, "E3358", {"start": v(14.2, 64.9) * mm, "mid": v(14.26, 64.84) * mm, "end": v(14.33, 64.9) * mm});
            skArc(sketch, "E3359", {"start": v(14.33, 64.9) * mm, "mid": v(14.26, 64.97) * mm, "end": v(14.2, 64.9) * mm});
            skArc(sketch, "E3360", {"start": v(14.2, 64.4) * mm, "mid": v(14.26, 64.34) * mm, "end": v(14.33, 64.4) * mm});
            skArc(sketch, "E3361", {"start": v(14.33, 64.4) * mm, "mid": v(14.26, 64.46) * mm, "end": v(14.2, 64.4) * mm});
            skArc(sketch, "E3362", {"start": v(24.82, 55.26) * mm, "mid": v(24.88, 55.2) * mm, "end": v(24.95, 55.26) * mm});
            skArc(sketch, "E3363", {"start": v(24.95, 55.26) * mm, "mid": v(24.88, 55.33) * mm, "end": v(24.82, 55.26) * mm});
            skArc(sketch, "E3364", {"start": v(15.7, 64.92) * mm, "mid": v(15.76, 64.85) * mm, "end": v(15.83, 64.92) * mm});
            skArc(sketch, "E3365", {"start": v(15.83, 64.92) * mm, "mid": v(15.76, 64.98) * mm, "end": v(15.7, 64.92) * mm});
            skArc(sketch, "E3366", {"start": v(14.2, 59.32) * mm, "mid": v(14.26, 59.26) * mm, "end": v(14.33, 59.32) * mm});
            skArc(sketch, "E3367", {"start": v(14.33, 59.32) * mm, "mid": v(14.26, 59.39) * mm, "end": v(14.2, 59.32) * mm});
            skArc(sketch, "E3368", {"start": v(15.7, 59.84) * mm, "mid": v(15.76, 59.77) * mm, "end": v(15.82, 59.84) * mm});
            skArc(sketch, "E3369", {"start": v(15.82, 59.84) * mm, "mid": v(15.76, 59.9) * mm, "end": v(15.7, 59.84) * mm});
            skArc(sketch, "E3370", {"start": v(11.55, 75.45) * mm, "mid": v(11.61, 75.38) * mm, "end": v(11.67, 75.45) * mm});
            skArc(sketch, "E3371", {"start": v(11.67, 75.45) * mm, "mid": v(11.61, 75.5) * mm, "end": v(11.55, 75.45) * mm});
            skArc(sketch, "E3372", {"start": v(17.83, 54.07) * mm, "mid": v(17.77, 54.14) * mm, "end": v(17.7, 54.07) * mm});
            skArc(sketch, "E3373", {"start": v(18.34, 54.07) * mm, "mid": v(18.28, 54.14) * mm, "end": v(18.21, 54.07) * mm});
            skArc(sketch, "E3374", {"start": v(14.2, 59.83) * mm, "mid": v(14.26, 59.77) * mm, "end": v(14.33, 59.83) * mm});
            skArc(sketch, "E3375", {"start": v(14.33, 59.83) * mm, "mid": v(14.26, 59.9) * mm, "end": v(14.2, 59.83) * mm});
            skArc(sketch, "E3376", {"start": v(12.56, 76.94) * mm, "mid": v(12.62, 76.88) * mm, "end": v(12.68, 76.94) * mm});
            skArc(sketch, "E3377", {"start": v(12.68, 76.94) * mm, "mid": v(12.62, 77) * mm, "end": v(12.56, 76.94) * mm});
            skArc(sketch, "E3378", {"start": v(15.7, 60.35) * mm, "mid": v(15.76, 60.28) * mm, "end": v(15.82, 60.35) * mm});
            skArc(sketch, "E3379", {"start": v(15.82, 60.35) * mm, "mid": v(15.76, 60.4) * mm, "end": v(15.7, 60.35) * mm});
            skArc(sketch, "E3380", {"start": v(24.8, 52.58) * mm, "mid": v(24.87, 52.51) * mm, "end": v(24.94, 52.58) * mm});
            skArc(sketch, "E3381", {"start": v(24.94, 52.58) * mm, "mid": v(24.87, 52.64) * mm, "end": v(24.8, 52.58) * mm});
            skArc(sketch, "E3382", {"start": v(18.72, 51.37) * mm, "mid": v(18.78, 51.3) * mm, "end": v(18.84, 51.37) * mm});
            skArc(sketch, "E3383", {"start": v(18.84, 51.37) * mm, "mid": v(18.78, 51.44) * mm, "end": v(18.72, 51.37) * mm});
            skArc(sketch, "E3384", {"start": v(10.02, 75.45) * mm, "mid": v(10.09, 75.38) * mm, "end": v(10.15, 75.45) * mm});
            skArc(sketch, "E3385", {"start": v(10.15, 75.45) * mm, "mid": v(10.09, 75.5) * mm, "end": v(10.02, 75.45) * mm});
            skArc(sketch, "E3386", {"start": v(11.04, 75.45) * mm, "mid": v(11.1, 75.38) * mm, "end": v(11.17, 75.45) * mm});
            skArc(sketch, "E3387", {"start": v(11.17, 75.45) * mm, "mid": v(11.1, 75.5) * mm, "end": v(11.04, 75.45) * mm});
            skArc(sketch, "E3388", {"start": v(12.05, 75.45) * mm, "mid": v(12.12, 75.38) * mm, "end": v(12.18, 75.45) * mm});
            skArc(sketch, "E3389", {"start": v(12.18, 75.45) * mm, "mid": v(12.12, 75.5) * mm, "end": v(12.05, 75.45) * mm});
            skArc(sketch, "E3390", {"start": v(18.2, 51.37) * mm, "mid": v(18.27, 51.3) * mm, "end": v(18.34, 51.37) * mm});
            skArc(sketch, "E3391", {"start": v(18.34, 51.37) * mm, "mid": v(18.27, 51.44) * mm, "end": v(18.2, 51.37) * mm});
            skArc(sketch, "E3392", {"start": v(17.7, 51.37) * mm, "mid": v(17.76, 51.3) * mm, "end": v(17.83, 51.37) * mm});
            skArc(sketch, "E3393", {"start": v(17.83, 51.37) * mm, "mid": v(17.76, 51.44) * mm, "end": v(17.7, 51.37) * mm});
            skArc(sketch, "E3394", {"start": v(14.33, 64.4) * mm, "mid": v(14.26, 64.47) * mm, "end": v(14.2, 64.4) * mm});
            skArc(sketch, "E3395", {"start": v(19.73, 51.37) * mm, "mid": v(19.8, 51.3) * mm, "end": v(19.86, 51.37) * mm});
            skArc(sketch, "E3396", {"start": v(19.86, 51.37) * mm, "mid": v(19.8, 51.44) * mm, "end": v(19.73, 51.37) * mm});
            skArc(sketch, "E3397", {"start": v(14.2, 71.51) * mm, "mid": v(14.26, 71.45) * mm, "end": v(14.33, 71.51) * mm});
            skArc(sketch, "E3398", {"start": v(14.33, 71.51) * mm, "mid": v(14.26, 71.57) * mm, "end": v(14.2, 71.51) * mm});
            skArc(sketch, "E3399", {"start": v(23.28, 52.58) * mm, "mid": v(23.35, 52.51) * mm, "end": v(23.41, 52.58) * mm});
            skArc(sketch, "E3400", {"start": v(23.41, 52.58) * mm, "mid": v(23.35, 52.64) * mm, "end": v(23.28, 52.58) * mm});
            skArc(sketch, "E3401", {"start": v(23.3, 54.07) * mm, "mid": v(23.36, 54) * mm, "end": v(23.42, 54.07) * mm});
            skArc(sketch, "E3402", {"start": v(23.42, 54.07) * mm, "mid": v(23.36, 54.14) * mm, "end": v(23.3, 54.07) * mm});
            skArc(sketch, "E3403", {"start": v(23.8, 52.58) * mm, "mid": v(23.86, 52.51) * mm, "end": v(23.92, 52.58) * mm});
            skArc(sketch, "E3404", {"start": v(23.92, 52.58) * mm, "mid": v(23.86, 52.64) * mm, "end": v(23.8, 52.58) * mm});
            skArc(sketch, "E3405", {"start": v(24.3, 52.58) * mm, "mid": v(24.36, 52.51) * mm, "end": v(24.43, 52.58) * mm});
            skArc(sketch, "E3406", {"start": v(24.43, 52.58) * mm, "mid": v(24.36, 52.64) * mm, "end": v(24.3, 52.58) * mm});
            skArc(sketch, "E3407", {"start": v(15.7, 73.55) * mm, "mid": v(15.76, 73.49) * mm, "end": v(15.83, 73.55) * mm});
            skArc(sketch, "E3408", {"start": v(15.83, 73.55) * mm, "mid": v(15.76, 73.62) * mm, "end": v(15.7, 73.55) * mm});
            skArc(sketch, "E3409", {"start": v(9.51, 75.45) * mm, "mid": v(9.58, 75.38) * mm, "end": v(9.64, 75.45) * mm});
            skArc(sketch, "E3410", {"start": v(9.64, 75.45) * mm, "mid": v(9.58, 75.5) * mm, "end": v(9.51, 75.45) * mm});
            skArc(sketch, "E3411", {"start": v(14.2, 69.99) * mm, "mid": v(14.26, 69.92) * mm, "end": v(14.33, 69.99) * mm});
            skArc(sketch, "E3412", {"start": v(14.33, 69.99) * mm, "mid": v(14.26, 70.05) * mm, "end": v(14.2, 69.99) * mm});
            skArc(sketch, "E3413", {"start": v(9.5, 76.94) * mm, "mid": v(9.57, 76.88) * mm, "end": v(9.63, 76.94) * mm});
            skArc(sketch, "E3414", {"start": v(9.63, 76.94) * mm, "mid": v(9.57, 77) * mm, "end": v(9.5, 76.94) * mm});
            skArc(sketch, "E3415", {"start": v(15.7, 70) * mm, "mid": v(15.76, 69.93) * mm, "end": v(15.83, 70) * mm});
            skArc(sketch, "E3416", {"start": v(15.83, 70) * mm, "mid": v(15.76, 70.06) * mm, "end": v(15.7, 70) * mm});
            skArc(sketch, "E3417", {"start": v(14.2, 64.9) * mm, "mid": v(14.26, 64.85) * mm, "end": v(14.33, 64.9) * mm});
            skArc(sketch, "E3418", {"start": v(15.7, 73.05) * mm, "mid": v(15.76, 72.98) * mm, "end": v(15.83, 73.05) * mm});
            skArc(sketch, "E3419", {"start": v(15.83, 73.05) * mm, "mid": v(15.76, 73.1) * mm, "end": v(15.7, 73.05) * mm});
            skArc(sketch, "E3420", {"start": v(15.7, 72.54) * mm, "mid": v(15.76, 72.47) * mm, "end": v(15.83, 72.54) * mm});
            skArc(sketch, "E3421", {"start": v(15.83, 72.54) * mm, "mid": v(15.76, 72.6) * mm, "end": v(15.7, 72.54) * mm});
            skArc(sketch, "E3422", {"start": v(24.31, 55.26) * mm, "mid": v(24.38, 55.2) * mm, "end": v(24.44, 55.26) * mm});
            skArc(sketch, "E3423", {"start": v(24.44, 55.26) * mm, "mid": v(24.38, 55.33) * mm, "end": v(24.31, 55.26) * mm});
            skArc(sketch, "E3424", {"start": v(23.8, 55.26) * mm, "mid": v(23.87, 55.2) * mm, "end": v(23.93, 55.26) * mm});
            skArc(sketch, "E3425", {"start": v(23.93, 55.26) * mm, "mid": v(23.87, 55.33) * mm, "end": v(23.8, 55.26) * mm});
            skArc(sketch, "E3426", {"start": v(14.2, 63.9) * mm, "mid": v(14.26, 63.83) * mm, "end": v(14.33, 63.9) * mm});
            skArc(sketch, "E3427", {"start": v(14.33, 63.9) * mm, "mid": v(14.26, 63.96) * mm, "end": v(14.2, 63.9) * mm});
            skArc(sketch, "E3428", {"start": v(24.3, 54.07) * mm, "mid": v(24.37, 54) * mm, "end": v(24.43, 54.07) * mm});
            skArc(sketch, "E3429", {"start": v(24.43, 54.07) * mm, "mid": v(24.37, 54.14) * mm, "end": v(24.3, 54.07) * mm});
            skArc(sketch, "E3430", {"start": v(24.32, 56.76) * mm, "mid": v(24.38, 56.7) * mm, "end": v(24.45, 56.76) * mm});
            skArc(sketch, "E3431", {"start": v(24.45, 56.76) * mm, "mid": v(24.38, 56.82) * mm, "end": v(24.32, 56.76) * mm});
            skArc(sketch, "E3432", {"start": v(24.83, 56.76) * mm, "mid": v(24.9, 56.7) * mm, "end": v(24.96, 56.76) * mm});
            skArc(sketch, "E3433", {"start": v(24.96, 56.76) * mm, "mid": v(24.9, 56.82) * mm, "end": v(24.83, 56.76) * mm});
            skArc(sketch, "E3434", {"start": v(14.2, 63.39) * mm, "mid": v(14.26, 63.32) * mm, "end": v(14.33, 63.39) * mm});
            skArc(sketch, "E3435", {"start": v(14.33, 63.39) * mm, "mid": v(14.26, 63.45) * mm, "end": v(14.2, 63.39) * mm});
            skArc(sketch, "E3436", {"start": v(21.77, 55.26) * mm, "mid": v(21.84, 55.2) * mm, "end": v(21.9, 55.26) * mm});
            skArc(sketch, "E3437", {"start": v(21.9, 55.26) * mm, "mid": v(21.84, 55.33) * mm, "end": v(21.77, 55.26) * mm});
            skArc(sketch, "E3438", {"start": v(12.56, 75.4) * mm, "mid": v(12.63, 75.33) * mm, "end": v(12.69, 75.4) * mm});
            skArc(sketch, "E3439", {"start": v(12.69, 75.4) * mm, "mid": v(12.63, 75.46) * mm, "end": v(12.56, 75.4) * mm});
            skArc(sketch, "E3440", {"start": v(8.5, 75.45) * mm, "mid": v(8.56, 75.38) * mm, "end": v(8.63, 75.45) * mm});
            skArc(sketch, "E3441", {"start": v(8.63, 75.45) * mm, "mid": v(8.56, 75.5) * mm, "end": v(8.5, 75.45) * mm});
            skArc(sketch, "E3442", {"start": v(22.28, 55.26) * mm, "mid": v(22.34, 55.2) * mm, "end": v(22.4, 55.26) * mm});
            skArc(sketch, "E3443", {"start": v(22.4, 55.26) * mm, "mid": v(22.34, 55.33) * mm, "end": v(22.28, 55.26) * mm});
            skArc(sketch, "E3444", {"start": v(22.79, 55.26) * mm, "mid": v(22.85, 55.2) * mm, "end": v(22.92, 55.26) * mm});
            skArc(sketch, "E3445", {"start": v(22.92, 55.26) * mm, "mid": v(22.85, 55.33) * mm, "end": v(22.79, 55.26) * mm});
            skArc(sketch, "E3446", {"start": v(23.3, 55.26) * mm, "mid": v(23.36, 55.2) * mm, "end": v(23.42, 55.26) * mm});
            skArc(sketch, "E3447", {"start": v(23.42, 55.26) * mm, "mid": v(23.36, 55.33) * mm, "end": v(23.3, 55.26) * mm});
            skArc(sketch, "E3448", {"start": v(9, 75.45) * mm, "mid": v(9.07, 75.38) * mm, "end": v(9.13, 75.45) * mm});
            skArc(sketch, "E3449", {"start": v(9.13, 75.45) * mm, "mid": v(9.07, 75.5) * mm, "end": v(9, 75.45) * mm});
            skArc(sketch, "E3450", {"start": v(8, 75.45) * mm, "mid": v(8.05, 75.38) * mm, "end": v(8.12, 75.45) * mm});
            skArc(sketch, "E3451", {"start": v(8.12, 75.45) * mm, "mid": v(8.05, 75.5) * mm, "end": v(8, 75.45) * mm});
            skArc(sketch, "E3452", {"start": v(7.48, 75.45) * mm, "mid": v(7.55, 75.38) * mm, "end": v(7.6, 75.45) * mm});
            skArc(sketch, "E3453", {"start": v(7.6, 75.45) * mm, "mid": v(7.55, 75.5) * mm, "end": v(7.48, 75.45) * mm});
            skArc(sketch, "E3454", {"start": v(18.2, 49.88) * mm, "mid": v(18.27, 49.81) * mm, "end": v(18.33, 49.88) * mm});
            skArc(sketch, "E3455", {"start": v(18.33, 49.88) * mm, "mid": v(18.27, 49.94) * mm, "end": v(18.2, 49.88) * mm});
            skArc(sketch, "E3456", {"start": v(20.23, 49.88) * mm, "mid": v(20.3, 49.81) * mm, "end": v(20.36, 49.88) * mm});
            skArc(sketch, "E3457", {"start": v(20.36, 49.88) * mm, "mid": v(20.3, 49.94) * mm, "end": v(20.23, 49.88) * mm});
            skArc(sketch, "E3458", {"start": v(20.74, 49.88) * mm, "mid": v(20.8, 49.81) * mm, "end": v(20.87, 49.88) * mm});
            skArc(sketch, "E3459", {"start": v(20.87, 49.88) * mm, "mid": v(20.8, 49.94) * mm, "end": v(20.74, 49.88) * mm});
            skArc(sketch, "E3460", {"start": v(18.7, 49.88) * mm, "mid": v(18.77, 49.81) * mm, "end": v(18.84, 49.88) * mm});
            skArc(sketch, "E3461", {"start": v(18.84, 49.88) * mm, "mid": v(18.77, 49.94) * mm, "end": v(18.7, 49.88) * mm});
            skArc(sketch, "E3462", {"start": v(20.75, 51.37) * mm, "mid": v(20.81, 51.3) * mm, "end": v(20.88, 51.37) * mm});
            skArc(sketch, "E3463", {"start": v(20.88, 51.37) * mm, "mid": v(20.81, 51.44) * mm, "end": v(20.75, 51.37) * mm});
            skArc(sketch, "E3464", {"start": v(20.24, 51.37) * mm, "mid": v(20.3, 51.3) * mm, "end": v(20.37, 51.37) * mm});
            skArc(sketch, "E3465", {"start": v(20.37, 51.37) * mm, "mid": v(20.3, 51.44) * mm, "end": v(20.24, 51.37) * mm});
            skArc(sketch, "E3466", {"start": v(22.28, 54.07) * mm, "mid": v(22.34, 54) * mm, "end": v(22.4, 54.07) * mm});
            skArc(sketch, "E3467", {"start": v(22.4, 54.07) * mm, "mid": v(22.34, 54.14) * mm, "end": v(22.28, 54.07) * mm});
            skArc(sketch, "E3468", {"start": v(21.25, 49.88) * mm, "mid": v(21.31, 49.81) * mm, "end": v(21.38, 49.88) * mm});
            skArc(sketch, "E3469", {"start": v(21.38, 49.88) * mm, "mid": v(21.31, 49.94) * mm, "end": v(21.25, 49.88) * mm});
            skArc(sketch, "E3470", {"start": v(22.78, 54.07) * mm, "mid": v(22.85, 54) * mm, "end": v(22.91, 54.07) * mm});
            skArc(sketch, "E3471", {"start": v(22.91, 54.07) * mm, "mid": v(22.85, 54.14) * mm, "end": v(22.78, 54.07) * mm});
            skArc(sketch, "E3472", {"start": v(21.26, 51.37) * mm, "mid": v(21.32, 51.3) * mm, "end": v(21.38, 51.37) * mm});
            skArc(sketch, "E3473", {"start": v(21.38, 51.37) * mm, "mid": v(21.32, 51.44) * mm, "end": v(21.26, 51.37) * mm});
            skArc(sketch, "E3474", {"start": v(19.22, 49.88) * mm, "mid": v(19.28, 49.81) * mm, "end": v(19.34, 49.88) * mm});
            skArc(sketch, "E3475", {"start": v(19.34, 49.88) * mm, "mid": v(19.28, 49.94) * mm, "end": v(19.22, 49.88) * mm});
            skArc(sketch, "E3476", {"start": v(22.8, 56.76) * mm, "mid": v(22.86, 56.7) * mm, "end": v(22.92, 56.76) * mm});
            skArc(sketch, "E3477", {"start": v(22.92, 56.76) * mm, "mid": v(22.86, 56.82) * mm, "end": v(22.8, 56.76) * mm});
            skArc(sketch, "E3478", {"start": v(18.72, 55.26) * mm, "mid": v(18.79, 55.2) * mm, "end": v(18.85, 55.26) * mm});
            skArc(sketch, "E3479", {"start": v(18.85, 55.26) * mm, "mid": v(18.79, 55.33) * mm, "end": v(18.72, 55.26) * mm});
            skArc(sketch, "E3480", {"start": v(22.29, 56.76) * mm, "mid": v(22.35, 56.7) * mm, "end": v(22.42, 56.76) * mm});
            skArc(sketch, "E3481", {"start": v(22.42, 56.76) * mm, "mid": v(22.35, 56.82) * mm, "end": v(22.29, 56.76) * mm});
            skArc(sketch, "E3482", {"start": v(18.22, 55.26) * mm, "mid": v(18.28, 55.2) * mm, "end": v(18.34, 55.26) * mm});
            skArc(sketch, "E3483", {"start": v(18.34, 55.26) * mm, "mid": v(18.28, 55.33) * mm, "end": v(18.22, 55.26) * mm});
            skArc(sketch, "E3484", {"start": v(17.7, 55.26) * mm, "mid": v(17.77, 55.2) * mm, "end": v(17.84, 55.26) * mm});
            skArc(sketch, "E3485", {"start": v(17.84, 55.26) * mm, "mid": v(17.77, 55.33) * mm, "end": v(17.7, 55.26) * mm});
            skArc(sketch, "E3486", {"start": v(20.76, 55.26) * mm, "mid": v(20.82, 55.2) * mm, "end": v(20.88, 55.26) * mm});
            skArc(sketch, "E3487", {"start": v(20.88, 55.26) * mm, "mid": v(20.82, 55.33) * mm, "end": v(20.76, 55.26) * mm});
            skArc(sketch, "E3488", {"start": v(20.25, 55.26) * mm, "mid": v(20.31, 55.2) * mm, "end": v(20.38, 55.26) * mm});
            skArc(sketch, "E3489", {"start": v(20.38, 55.26) * mm, "mid": v(20.31, 55.33) * mm, "end": v(20.25, 55.26) * mm});
            skArc(sketch, "E3490", {"start": v(19.74, 55.26) * mm, "mid": v(19.8, 55.2) * mm, "end": v(19.87, 55.26) * mm});
            skArc(sketch, "E3491", {"start": v(19.87, 55.26) * mm, "mid": v(19.8, 55.33) * mm, "end": v(19.74, 55.26) * mm});
            skArc(sketch, "E3492", {"start": v(21.76, 49.88) * mm, "mid": v(21.82, 49.81) * mm, "end": v(21.88, 49.88) * mm});
            skArc(sketch, "E3493", {"start": v(21.88, 49.88) * mm, "mid": v(21.82, 49.94) * mm, "end": v(21.76, 49.88) * mm});
            skArc(sketch, "E3494", {"start": v(20.74, 52.58) * mm, "mid": v(20.8, 52.51) * mm, "end": v(20.87, 52.58) * mm});
            skArc(sketch, "E3495", {"start": v(20.87, 52.58) * mm, "mid": v(20.8, 52.64) * mm, "end": v(20.74, 52.58) * mm});
            skArc(sketch, "E3496", {"start": v(22.78, 51.37) * mm, "mid": v(22.84, 51.3) * mm, "end": v(22.9, 51.37) * mm});
            skArc(sketch, "E3497", {"start": v(22.9, 51.37) * mm, "mid": v(22.84, 51.44) * mm, "end": v(22.78, 51.37) * mm});
            skArc(sketch, "E3498", {"start": v(15.7, 64.4) * mm, "mid": v(15.76, 64.35) * mm, "end": v(15.82, 64.4) * mm});
            skArc(sketch, "E3499", {"start": v(15.82, 64.4) * mm, "mid": v(15.76, 64.47) * mm, "end": v(15.7, 64.4) * mm});
            skArc(sketch, "E3500", {"start": v(22.27, 51.37) * mm, "mid": v(22.34, 51.3) * mm, "end": v(22.4, 51.37) * mm});
            skArc(sketch, "E3501", {"start": v(22.4, 51.37) * mm, "mid": v(22.34, 51.44) * mm, "end": v(22.27, 51.37) * mm});
            skArc(sketch, "E3502", {"start": v(20.24, 52.58) * mm, "mid": v(20.3, 52.51) * mm, "end": v(20.36, 52.58) * mm});
            skArc(sketch, "E3503", {"start": v(20.36, 52.58) * mm, "mid": v(20.3, 52.64) * mm, "end": v(20.24, 52.58) * mm});
            skArc(sketch, "E3504", {"start": v(21.77, 51.37) * mm, "mid": v(21.83, 51.3) * mm, "end": v(21.9, 51.37) * mm});
            skArc(sketch, "E3505", {"start": v(21.9, 51.37) * mm, "mid": v(21.83, 51.44) * mm, "end": v(21.77, 51.37) * mm});
            skArc(sketch, "E3506", {"start": v(17.7, 52.58) * mm, "mid": v(17.76, 52.51) * mm, "end": v(17.82, 52.58) * mm});
            skArc(sketch, "E3507", {"start": v(17.82, 52.58) * mm, "mid": v(17.76, 52.64) * mm, "end": v(17.7, 52.58) * mm});
            skArc(sketch, "E3508", {"start": v(19.23, 55.26) * mm, "mid": v(19.3, 55.2) * mm, "end": v(19.36, 55.26) * mm});
            skArc(sketch, "E3509", {"start": v(19.36, 55.26) * mm, "mid": v(19.3, 55.33) * mm, "end": v(19.23, 55.26) * mm});
            skArc(sketch, "E3510", {"start": v(22.77, 49.88) * mm, "mid": v(22.84, 49.81) * mm, "end": v(22.9, 49.88) * mm});
            skArc(sketch, "E3511", {"start": v(22.9, 49.88) * mm, "mid": v(22.84, 49.94) * mm, "end": v(22.77, 49.88) * mm});
            skArc(sketch, "E3512", {"start": v(23.8, 51.37) * mm, "mid": v(23.86, 51.3) * mm, "end": v(23.92, 51.37) * mm});
            skArc(sketch, "E3513", {"start": v(23.92, 51.37) * mm, "mid": v(23.86, 51.44) * mm, "end": v(23.8, 51.37) * mm});
            skArc(sketch, "E3514", {"start": v(15.7, 70.5) * mm, "mid": v(15.76, 70.44) * mm, "end": v(15.83, 70.5) * mm});
            skArc(sketch, "E3515", {"start": v(15.83, 70.5) * mm, "mid": v(15.76, 70.57) * mm, "end": v(15.7, 70.5) * mm});
            skArc(sketch, "E3516", {"start": v(23.79, 49.88) * mm, "mid": v(23.85, 49.81) * mm, "end": v(23.92, 49.88) * mm});
            skArc(sketch, "E3517", {"start": v(23.92, 49.88) * mm, "mid": v(23.85, 49.94) * mm, "end": v(23.79, 49.88) * mm});
            skArc(sketch, "E3518", {"start": v(19.24, 56.76) * mm, "mid": v(19.3, 56.7) * mm, "end": v(19.37, 56.76) * mm});
            skArc(sketch, "E3519", {"start": v(19.37, 56.76) * mm, "mid": v(19.3, 56.82) * mm, "end": v(19.24, 56.76) * mm});
            skArc(sketch, "E3520", {"start": v(14.2, 67.45) * mm, "mid": v(14.26, 67.38) * mm, "end": v(14.33, 67.45) * mm});
            skArc(sketch, "E3521", {"start": v(14.33, 67.45) * mm, "mid": v(14.26, 67.51) * mm, "end": v(14.2, 67.45) * mm});
            skArc(sketch, "E3522", {"start": v(24.81, 51.37) * mm, "mid": v(24.88, 51.3) * mm, "end": v(24.94, 51.37) * mm});
            skArc(sketch, "E3523", {"start": v(24.94, 51.37) * mm, "mid": v(24.88, 51.44) * mm, "end": v(24.81, 51.37) * mm});
            skArc(sketch, "E3524", {"start": v(19.74, 54.07) * mm, "mid": v(19.8, 54) * mm, "end": v(19.86, 54.07) * mm});
            skArc(sketch, "E3525", {"start": v(19.86, 54.07) * mm, "mid": v(19.8, 54.14) * mm, "end": v(19.74, 54.07) * mm});
            skArc(sketch, "E3526", {"start": v(14.2, 66.94) * mm, "mid": v(14.26, 66.88) * mm, "end": v(14.33, 66.94) * mm});
            skArc(sketch, "E3527", {"start": v(14.33, 66.94) * mm, "mid": v(14.26, 67) * mm, "end": v(14.2, 66.94) * mm});
            skArc(sketch, "E3528", {"start": v(14.2, 66.43) * mm, "mid": v(14.26, 66.37) * mm, "end": v(14.33, 66.43) * mm});
            skArc(sketch, "E3529", {"start": v(14.33, 66.43) * mm, "mid": v(14.26, 66.5) * mm, "end": v(14.2, 66.43) * mm});
            skArc(sketch, "E3530", {"start": v(18.2, 52.58) * mm, "mid": v(18.27, 52.51) * mm, "end": v(18.33, 52.58) * mm});
            skArc(sketch, "E3531", {"start": v(18.33, 52.58) * mm, "mid": v(18.27, 52.64) * mm, "end": v(18.2, 52.58) * mm});
            skArc(sketch, "E3532", {"start": v(19.73, 49.88) * mm, "mid": v(19.79, 49.81) * mm, "end": v(19.85, 49.88) * mm});
            skArc(sketch, "E3533", {"start": v(19.85, 49.88) * mm, "mid": v(19.79, 49.94) * mm, "end": v(19.73, 49.88) * mm});
            skArc(sketch, "E3534", {"start": v(15.7, 69.49) * mm, "mid": v(15.76, 69.43) * mm, "end": v(15.83, 69.49) * mm});
            skArc(sketch, "E3535", {"start": v(15.83, 69.49) * mm, "mid": v(15.76, 69.55) * mm, "end": v(15.7, 69.49) * mm});
            skArc(sketch, "E3536", {"start": v(18.73, 56.76) * mm, "mid": v(18.8, 56.7) * mm, "end": v(18.86, 56.76) * mm});
            skArc(sketch, "E3537", {"start": v(18.86, 56.76) * mm, "mid": v(18.8, 56.82) * mm, "end": v(18.73, 56.76) * mm});
            skArc(sketch, "E3538", {"start": v(19.23, 51.37) * mm, "mid": v(19.29, 51.3) * mm, "end": v(19.35, 51.37) * mm});
            skArc(sketch, "E3539", {"start": v(19.35, 51.37) * mm, "mid": v(19.29, 51.44) * mm, "end": v(19.23, 51.37) * mm});
            skArc(sketch, "E3540", {"start": v(14.2, 62.88) * mm, "mid": v(14.26, 62.81) * mm, "end": v(14.33, 62.88) * mm});
            skArc(sketch, "E3541", {"start": v(14.33, 62.88) * mm, "mid": v(14.26, 62.94) * mm, "end": v(14.2, 62.88) * mm});
            skArc(sketch, "E3542", {"start": v(15.7, 72.03) * mm, "mid": v(15.76, 71.97) * mm, "end": v(15.83, 72.03) * mm});
            skArc(sketch, "E3543", {"start": v(15.83, 72.03) * mm, "mid": v(15.76, 72.1) * mm, "end": v(15.7, 72.03) * mm});
            skArc(sketch, "E3544", {"start": v(17.34, 20.5) * mm, "mid": v(17.46, 20.36) * mm, "end": v(17.59, 20.5) * mm});
            skArc(sketch, "E3545", {"start": v(17.59, 20.5) * mm, "mid": v(17.46, 20.62) * mm, "end": v(17.34, 20.5) * mm});
            skArc(sketch, "E3546", {"start": v(3.6, 20.5) * mm, "mid": v(3.74, 20.38) * mm, "end": v(3.86, 20.5) * mm});
            skArc(sketch, "E3547", {"start": v(3.86, 20.5) * mm, "mid": v(3.74, 20.63) * mm, "end": v(3.6, 20.5) * mm});
            skArc(sketch, "E3548", {"start": v(15.7, 66.44) * mm, "mid": v(15.76, 66.38) * mm, "end": v(15.83, 66.44) * mm});
            skArc(sketch, "E3549", {"start": v(15.83, 66.44) * mm, "mid": v(15.76, 66.5) * mm, "end": v(15.7, 66.44) * mm});
            skArc(sketch, "E3550", {"start": v(15.7, 66.95) * mm, "mid": v(15.76, 66.89) * mm, "end": v(15.83, 66.95) * mm});
            skArc(sketch, "E3551", {"start": v(15.83, 66.95) * mm, "mid": v(15.76, 67.01) * mm, "end": v(15.7, 66.95) * mm});
            skArc(sketch, "E3552", {"start": v(23.81, 56.76) * mm, "mid": v(23.88, 56.7) * mm, "end": v(23.94, 56.76) * mm});
            skArc(sketch, "E3553", {"start": v(23.94, 56.76) * mm, "mid": v(23.88, 56.82) * mm, "end": v(23.81, 56.76) * mm});
            skArc(sketch, "E3554", {"start": v(45.82, 53.43) * mm, "mid": v(45.95, 53.3) * mm, "end": v(46.08, 53.43) * mm});
            skArc(sketch, "E3555", {"start": v(46.08, 53.43) * mm, "mid": v(45.95, 53.56) * mm, "end": v(45.82, 53.43) * mm});
            skArc(sketch, "E3556", {"start": v(14.2, 68.97) * mm, "mid": v(14.26, 68.9) * mm, "end": v(14.33, 68.97) * mm});
            skArc(sketch, "E3557", {"start": v(14.33, 68.97) * mm, "mid": v(14.26, 69.03) * mm, "end": v(14.2, 68.97) * mm});
            skArc(sketch, "E3558", {"start": v(22.27, 49.88) * mm, "mid": v(22.33, 49.81) * mm, "end": v(22.4, 49.88) * mm});
            skArc(sketch, "E3559", {"start": v(22.4, 49.88) * mm, "mid": v(22.33, 49.94) * mm, "end": v(22.27, 49.88) * mm});
            skArc(sketch, "E3560", {"start": v(19.22, 52.58) * mm, "mid": v(19.28, 52.51) * mm, "end": v(19.35, 52.58) * mm});
            skArc(sketch, "E3561", {"start": v(19.35, 52.58) * mm, "mid": v(19.28, 52.64) * mm, "end": v(19.22, 52.58) * mm});
            skArc(sketch, "E3562", {"start": v(45.82, 47.34) * mm, "mid": v(45.95, 47.21) * mm, "end": v(46.08, 47.34) * mm});
            skArc(sketch, "E3563", {"start": v(46.08, 47.34) * mm, "mid": v(45.95, 47.46) * mm, "end": v(45.82, 47.34) * mm});
            skArc(sketch, "E3564", {"start": v(21.78, 56.76) * mm, "mid": v(21.84, 56.7) * mm, "end": v(21.9, 56.76) * mm});
            skArc(sketch, "E3565", {"start": v(21.9, 56.76) * mm, "mid": v(21.84, 56.82) * mm, "end": v(21.78, 56.76) * mm});
            skArc(sketch, "E3566", {"start": v(47.68, 54.96) * mm, "mid": v(47.8, 54.83) * mm, "end": v(47.93, 54.96) * mm});
            skArc(sketch, "E3567", {"start": v(47.93, 54.96) * mm, "mid": v(47.8, 55.08) * mm, "end": v(47.68, 54.96) * mm});
            skArc(sketch, "E3568", {"start": v(23.43, 20.5) * mm, "mid": v(23.56, 20.36) * mm, "end": v(23.69, 20.5) * mm});
            skArc(sketch, "E3569", {"start": v(23.69, 20.5) * mm, "mid": v(23.56, 20.62) * mm, "end": v(23.43, 20.5) * mm});
            skArc(sketch, "E3570", {"start": v(4.07, 51.22) * mm, "mid": v(4.2, 51.1) * mm, "end": v(4.32, 51.22) * mm});
            skArc(sketch, "E3571", {"start": v(4.32, 51.22) * mm, "mid": v(4.2, 51.35) * mm, "end": v(4.07, 51.22) * mm});
            skArc(sketch, "E3572", {"start": v(4.07, 54.27) * mm, "mid": v(4.2, 54.15) * mm, "end": v(4.32, 54.27) * mm});
            skArc(sketch, "E3573", {"start": v(4.32, 54.27) * mm, "mid": v(4.2, 54.4) * mm, "end": v(4.07, 54.27) * mm});
            skArc(sketch, "E3574", {"start": v(4.07, 55.8) * mm, "mid": v(4.2, 55.67) * mm, "end": v(4.32, 55.8) * mm});
            skArc(sketch, "E3575", {"start": v(4.32, 55.8) * mm, "mid": v(4.2, 55.92) * mm, "end": v(4.07, 55.8) * mm});
            skArc(sketch, "E3576", {"start": v(4.07, 57.32) * mm, "mid": v(4.2, 57.2) * mm, "end": v(4.32, 57.32) * mm});
            skArc(sketch, "E3577", {"start": v(4.32, 57.32) * mm, "mid": v(4.2, 57.45) * mm, "end": v(4.07, 57.32) * mm});
            skArc(sketch, "E3578", {"start": v(4.07, 52.75) * mm, "mid": v(4.2, 52.62) * mm, "end": v(4.32, 52.75) * mm});
            skArc(sketch, "E3579", {"start": v(4.32, 52.75) * mm, "mid": v(4.2, 52.88) * mm, "end": v(4.07, 52.75) * mm});
            skArc(sketch, "E3580", {"start": v(6.76, 46.63) * mm, "mid": v(6.89, 46.5) * mm, "end": v(7.01, 46.63) * mm});
            skArc(sketch, "E3581", {"start": v(7.01, 46.63) * mm, "mid": v(6.89, 46.75) * mm, "end": v(6.76, 46.63) * mm});
            skArc(sketch, "E3582", {"start": v(14.2, 68.46) * mm, "mid": v(14.26, 68.4) * mm, "end": v(14.33, 68.46) * mm});
            skArc(sketch, "E3583", {"start": v(14.33, 68.46) * mm, "mid": v(14.26, 68.53) * mm, "end": v(14.2, 68.46) * mm});
            skArc(sketch, "E3584", {"start": v(12.76, 20.5) * mm, "mid": v(12.9, 20.36) * mm, "end": v(13.02, 20.5) * mm});
            skArc(sketch, "E3585", {"start": v(13.02, 20.5) * mm, "mid": v(12.9, 20.62) * mm, "end": v(12.76, 20.5) * mm});
            skArc(sketch, "E3586", {"start": v(18.86, 20.5) * mm, "mid": v(18.99, 20.36) * mm, "end": v(19.11, 20.5) * mm});
            skArc(sketch, "E3587", {"start": v(19.11, 20.5) * mm, "mid": v(18.99, 20.62) * mm, "end": v(18.86, 20.5) * mm});
            skArc(sketch, "E3588", {"start": v(17.72, 56.76) * mm, "mid": v(17.78, 56.7) * mm, "end": v(17.84, 56.76) * mm});
            skArc(sketch, "E3589", {"start": v(17.84, 56.76) * mm, "mid": v(17.78, 56.82) * mm, "end": v(17.72, 56.76) * mm});
            skArc(sketch, "E3590", {"start": v(4.07, 46.65) * mm, "mid": v(4.2, 46.53) * mm, "end": v(4.32, 46.65) * mm});
            skArc(sketch, "E3591", {"start": v(4.32, 46.65) * mm, "mid": v(4.2, 46.78) * mm, "end": v(4.07, 46.65) * mm});
            skArc(sketch, "E3592", {"start": v(34.1, 20.5) * mm, "mid": v(34.23, 20.36) * mm, "end": v(34.35, 20.5) * mm});
            skArc(sketch, "E3593", {"start": v(34.35, 20.5) * mm, "mid": v(34.23, 20.62) * mm, "end": v(34.1, 20.5) * mm});
            skArc(sketch, "E3594", {"start": v(15.7, 65.43) * mm, "mid": v(15.76, 65.36) * mm, "end": v(15.82, 65.43) * mm});
            skArc(sketch, "E3595", {"start": v(15.82, 65.43) * mm, "mid": v(15.76, 65.49) * mm, "end": v(15.7, 65.43) * mm});
            skArc(sketch, "E3596", {"start": v(14.2, 62.37) * mm, "mid": v(14.26, 62.3) * mm, "end": v(14.33, 62.37) * mm});
            skArc(sketch, "E3597", {"start": v(14.33, 62.37) * mm, "mid": v(14.26, 62.43) * mm, "end": v(14.2, 62.37) * mm});
            skArc(sketch, "E3598", {"start": v(6.67, 20.5) * mm, "mid": v(6.8, 20.36) * mm, "end": v(6.92, 20.5) * mm});
            skArc(sketch, "E3599", {"start": v(6.92, 20.5) * mm, "mid": v(6.8, 20.62) * mm, "end": v(6.67, 20.5) * mm});
            skArc(sketch, "E3600", {"start": v(35.62, 20.5) * mm, "mid": v(35.75, 20.36) * mm, "end": v(35.88, 20.5) * mm});
            skArc(sketch, "E3601", {"start": v(35.88, 20.5) * mm, "mid": v(35.75, 20.62) * mm, "end": v(35.62, 20.5) * mm});
            skArc(sketch, "E3602", {"start": v(47.82, 20.5) * mm, "mid": v(47.94, 20.36) * mm, "end": v(48.07, 20.5) * mm});
            skArc(sketch, "E3603", {"start": v(48.07, 20.5) * mm, "mid": v(47.94, 20.62) * mm, "end": v(47.82, 20.5) * mm});
            skArc(sketch, "E3604", {"start": v(31.9, 21.1) * mm, "mid": v(32.29, 20.72) * mm, "end": v(32.67, 21.1) * mm});
            skArc(sketch, "E3605", {"start": v(32.67, 21.1) * mm, "mid": v(32.29, 21.48) * mm, "end": v(31.9, 21.1) * mm});
            skArc(sketch, "E3606", {"start": v(46.3, 20.5) * mm, "mid": v(46.42, 20.36) * mm, "end": v(46.55, 20.5) * mm});
            skArc(sketch, "E3607", {"start": v(46.55, 20.5) * mm, "mid": v(46.42, 20.62) * mm, "end": v(46.3, 20.5) * mm});
            skArc(sketch, "E3608", {"start": v(44.77, 20.5) * mm, "mid": v(44.9, 20.36) * mm, "end": v(45.02, 20.5) * mm});
            skArc(sketch, "E3609", {"start": v(45.02, 20.5) * mm, "mid": v(44.9, 20.62) * mm, "end": v(44.77, 20.5) * mm});
            skArc(sketch, "E3610", {"start": v(43.24, 20.5) * mm, "mid": v(43.37, 20.36) * mm, "end": v(43.5, 20.5) * mm});
            skArc(sketch, "E3611", {"start": v(43.5, 20.5) * mm, "mid": v(43.37, 20.62) * mm, "end": v(43.24, 20.5) * mm});
            skArc(sketch, "E3612", {"start": v(4.07, 49.7) * mm, "mid": v(4.2, 49.57) * mm, "end": v(4.32, 49.7) * mm});
            skArc(sketch, "E3613", {"start": v(4.32, 49.7) * mm, "mid": v(4.2, 49.83) * mm, "end": v(4.07, 49.7) * mm});
            skArc(sketch, "E3614", {"start": v(18.72, 54.07) * mm, "mid": v(18.78, 54) * mm, "end": v(18.85, 54.07) * mm});
            skArc(sketch, "E3615", {"start": v(18.85, 54.07) * mm, "mid": v(18.78, 54.14) * mm, "end": v(18.72, 54.07) * mm});
            skArc(sketch, "E3616", {"start": v(43.84, 67.86) * mm, "mid": v(44.22, 67.48) * mm, "end": v(44.6, 67.86) * mm});
            skArc(sketch, "E3617", {"start": v(44.6, 67.86) * mm, "mid": v(44.22, 68.24) * mm, "end": v(43.84, 67.86) * mm});
            skArc(sketch, "E3618", {"start": v(29.53, 20.5) * mm, "mid": v(29.65, 20.36) * mm, "end": v(29.78, 20.5) * mm});
            skArc(sketch, "E3619", {"start": v(29.78, 20.5) * mm, "mid": v(29.65, 20.62) * mm, "end": v(29.53, 20.5) * mm});
            skArc(sketch, "E3620", {"start": v(47.68, 53.43) * mm, "mid": v(47.8, 53.3) * mm, "end": v(47.93, 53.43) * mm});
            skArc(sketch, "E3621", {"start": v(47.93, 53.43) * mm, "mid": v(47.8, 53.56) * mm, "end": v(47.68, 53.43) * mm});
            skArc(sketch, "E3622", {"start": v(45.82, 58) * mm, "mid": v(45.95, 57.88) * mm, "end": v(46.08, 58) * mm});
            skArc(sketch, "E3623", {"start": v(46.08, 58) * mm, "mid": v(45.95, 58.13) * mm, "end": v(45.82, 58) * mm});
            skArc(sketch, "E3624", {"start": v(21.9, 20.5) * mm, "mid": v(22.03, 20.36) * mm, "end": v(22.16, 20.5) * mm});
            skArc(sketch, "E3625", {"start": v(22.16, 20.5) * mm, "mid": v(22.03, 20.62) * mm, "end": v(21.9, 20.5) * mm});
            skArc(sketch, "E3626", {"start": v(24.96, 20.5) * mm, "mid": v(25.08, 20.36) * mm, "end": v(25.2, 20.5) * mm});
            skArc(sketch, "E3627", {"start": v(25.2, 20.5) * mm, "mid": v(25.08, 20.62) * mm, "end": v(24.96, 20.5) * mm});
            skArc(sketch, "E3628", {"start": v(26.48, 20.5) * mm, "mid": v(26.6, 20.36) * mm, "end": v(26.73, 20.5) * mm});
            skArc(sketch, "E3629", {"start": v(26.73, 20.5) * mm, "mid": v(26.6, 20.62) * mm, "end": v(26.48, 20.5) * mm});
            skArc(sketch, "E3630", {"start": v(45.82, 56.48) * mm, "mid": v(45.95, 56.35) * mm, "end": v(46.08, 56.48) * mm});
            skArc(sketch, "E3631", {"start": v(46.08, 56.48) * mm, "mid": v(45.95, 56.6) * mm, "end": v(45.82, 56.48) * mm});
            skArc(sketch, "E3632", {"start": v(4.07, 48.18) * mm, "mid": v(4.2, 48.05) * mm, "end": v(4.32, 48.18) * mm});
            skArc(sketch, "E3633", {"start": v(4.32, 48.18) * mm, "mid": v(4.2, 48.3) * mm, "end": v(4.07, 48.18) * mm});
            skArc(sketch, "E3634", {"start": v(28, 20.5) * mm, "mid": v(28.13, 20.36) * mm, "end": v(28.26, 20.5) * mm});
            skArc(sketch, "E3635", {"start": v(28.26, 20.5) * mm, "mid": v(28.13, 20.62) * mm, "end": v(28, 20.5) * mm});
            skArc(sketch, "E3636", {"start": v(41.72, 20.5) * mm, "mid": v(41.85, 20.36) * mm, "end": v(41.97, 20.5) * mm});
            skArc(sketch, "E3637", {"start": v(41.97, 20.5) * mm, "mid": v(41.85, 20.62) * mm, "end": v(41.72, 20.5) * mm});
            skArc(sketch, "E3638", {"start": v(40.2, 20.5) * mm, "mid": v(40.32, 20.36) * mm, "end": v(40.45, 20.5) * mm});
            skArc(sketch, "E3639", {"start": v(40.45, 20.5) * mm, "mid": v(40.32, 20.62) * mm, "end": v(40.2, 20.5) * mm});
            skArc(sketch, "E3640", {"start": v(37.15, 20.5) * mm, "mid": v(37.27, 20.36) * mm, "end": v(37.4, 20.5) * mm});
            skArc(sketch, "E3641", {"start": v(37.4, 20.5) * mm, "mid": v(37.27, 20.62) * mm, "end": v(37.15, 20.5) * mm});
            skArc(sketch, "E3642", {"start": v(18.71, 52.58) * mm, "mid": v(18.78, 52.51) * mm, "end": v(18.84, 52.58) * mm});
            skArc(sketch, "E3643", {"start": v(18.84, 52.58) * mm, "mid": v(18.78, 52.64) * mm, "end": v(18.71, 52.58) * mm});
            skArc(sketch, "E3644", {"start": v(17.7, 49.88) * mm, "mid": v(17.76, 49.81) * mm, "end": v(17.82, 49.88) * mm});
            skArc(sketch, "E3645", {"start": v(17.82, 49.88) * mm, "mid": v(17.76, 49.94) * mm, "end": v(17.7, 49.88) * mm});
            skArc(sketch, "E3646", {"start": v(19.75, 56.76) * mm, "mid": v(19.81, 56.7) * mm, "end": v(19.88, 56.76) * mm});
            skArc(sketch, "E3647", {"start": v(19.88, 56.76) * mm, "mid": v(19.81, 56.82) * mm, "end": v(19.75, 56.76) * mm});
            skArc(sketch, "E3648", {"start": v(47.68, 51.9) * mm, "mid": v(47.8, 51.78) * mm, "end": v(47.93, 51.9) * mm});
            skArc(sketch, "E3649", {"start": v(47.93, 51.9) * mm, "mid": v(47.8, 52.04) * mm, "end": v(47.68, 51.9) * mm});
            skArc(sketch, "E3650", {"start": v(47.68, 47.34) * mm, "mid": v(47.8, 47.21) * mm, "end": v(47.93, 47.34) * mm});
            skArc(sketch, "E3651", {"start": v(47.93, 47.34) * mm, "mid": v(47.8, 47.46) * mm, "end": v(47.68, 47.34) * mm});
            skArc(sketch, "E3652", {"start": v(6.76, 55.77) * mm, "mid": v(6.89, 55.64) * mm, "end": v(7.01, 55.77) * mm});
            skArc(sketch, "E3653", {"start": v(7.01, 55.77) * mm, "mid": v(6.89, 55.9) * mm, "end": v(6.76, 55.77) * mm});
            skArc(sketch, "E3654", {"start": v(6.76, 54.25) * mm, "mid": v(6.89, 54.12) * mm, "end": v(7.01, 54.25) * mm});
            skArc(sketch, "E3655", {"start": v(7.01, 54.25) * mm, "mid": v(6.89, 54.37) * mm, "end": v(6.76, 54.25) * mm});
            skArc(sketch, "E3656", {"start": v(47.68, 58) * mm, "mid": v(47.8, 57.88) * mm, "end": v(47.93, 58) * mm});
            skArc(sketch, "E3657", {"start": v(47.93, 58) * mm, "mid": v(47.8, 58.13) * mm, "end": v(47.68, 58) * mm});
            skArc(sketch, "E3658", {"start": v(6.76, 52.72) * mm, "mid": v(6.89, 52.6) * mm, "end": v(7.01, 52.72) * mm});
            skArc(sketch, "E3659", {"start": v(7.01, 52.72) * mm, "mid": v(6.89, 52.85) * mm, "end": v(6.76, 52.72) * mm});
            skArc(sketch, "E3660", {"start": v(6.76, 57.3) * mm, "mid": v(6.89, 57.17) * mm, "end": v(7.01, 57.3) * mm});
            skArc(sketch, "E3661", {"start": v(7.01, 57.3) * mm, "mid": v(6.89, 57.42) * mm, "end": v(6.76, 57.3) * mm});
            skArc(sketch, "E3662", {"start": v(45.82, 54.96) * mm, "mid": v(45.95, 54.83) * mm, "end": v(46.08, 54.96) * mm});
            skArc(sketch, "E3663", {"start": v(46.08, 54.96) * mm, "mid": v(45.95, 55.08) * mm, "end": v(45.82, 54.96) * mm});
            skArc(sketch, "E3664", {"start": v(6.76, 51.2) * mm, "mid": v(6.89, 51.07) * mm, "end": v(7.01, 51.2) * mm});
            skArc(sketch, "E3665", {"start": v(7.01, 51.2) * mm, "mid": v(6.89, 51.33) * mm, "end": v(6.76, 51.2) * mm});
            skArc(sketch, "E3666", {"start": v(45.82, 51.9) * mm, "mid": v(45.95, 51.78) * mm, "end": v(46.08, 51.9) * mm});
            skArc(sketch, "E3667", {"start": v(46.08, 51.9) * mm, "mid": v(45.95, 52.04) * mm, "end": v(45.82, 51.9) * mm});
            skArc(sketch, "E3668", {"start": v(45.82, 50.39) * mm, "mid": v(45.95, 50.26) * mm, "end": v(46.08, 50.39) * mm});
            skArc(sketch, "E3669", {"start": v(46.08, 50.39) * mm, "mid": v(45.95, 50.51) * mm, "end": v(45.82, 50.39) * mm});
            skArc(sketch, "E3670", {"start": v(5.14, 20.5) * mm, "mid": v(5.27, 20.36) * mm, "end": v(5.4, 20.5) * mm});
            skArc(sketch, "E3671", {"start": v(5.4, 20.5) * mm, "mid": v(5.27, 20.62) * mm, "end": v(5.14, 20.5) * mm});
            skArc(sketch, "E3672", {"start": v(45.82, 48.86) * mm, "mid": v(45.95, 48.73) * mm, "end": v(46.08, 48.86) * mm});
            skArc(sketch, "E3673", {"start": v(46.08, 48.86) * mm, "mid": v(45.95, 48.99) * mm, "end": v(45.82, 48.86) * mm});
            skArc(sketch, "E3674", {"start": v(11.24, 20.5) * mm, "mid": v(11.37, 20.36) * mm, "end": v(11.5, 20.5) * mm});
            skArc(sketch, "E3675", {"start": v(11.5, 20.5) * mm, "mid": v(11.37, 20.62) * mm, "end": v(11.24, 20.5) * mm});
            skArc(sketch, "E3676", {"start": v(47.68, 48.86) * mm, "mid": v(47.8, 48.73) * mm, "end": v(47.93, 48.86) * mm});
            skArc(sketch, "E3677", {"start": v(47.93, 48.86) * mm, "mid": v(47.8, 48.99) * mm, "end": v(47.68, 48.86) * mm});
            skArc(sketch, "E3678", {"start": v(47.68, 56.48) * mm, "mid": v(47.8, 56.35) * mm, "end": v(47.93, 56.48) * mm});
            skArc(sketch, "E3679", {"start": v(47.93, 56.48) * mm, "mid": v(47.8, 56.6) * mm, "end": v(47.68, 56.48) * mm});
            skArc(sketch, "E3680", {"start": v(9.72, 20.5) * mm, "mid": v(9.84, 20.36) * mm, "end": v(9.97, 20.5) * mm});
            skArc(sketch, "E3681", {"start": v(9.97, 20.5) * mm, "mid": v(9.84, 20.62) * mm, "end": v(9.72, 20.5) * mm});
            skArc(sketch, "E3682", {"start": v(19.23, 54.07) * mm, "mid": v(19.3, 54) * mm, "end": v(19.35, 54.07) * mm});
            skArc(sketch, "E3683", {"start": v(19.35, 54.07) * mm, "mid": v(19.3, 54.14) * mm, "end": v(19.23, 54.07) * mm});
            skArc(sketch, "E3684", {"start": v(24.3, 51.37) * mm, "mid": v(24.37, 51.3) * mm, "end": v(24.43, 51.37) * mm});
            skArc(sketch, "E3685", {"start": v(24.43, 51.37) * mm, "mid": v(24.37, 51.44) * mm, "end": v(24.3, 51.37) * mm});
            skArc(sketch, "E3686", {"start": v(20.76, 56.76) * mm, "mid": v(20.83, 56.7) * mm, "end": v(20.9, 56.76) * mm});
            skArc(sketch, "E3687", {"start": v(20.9, 56.76) * mm, "mid": v(20.83, 56.82) * mm, "end": v(20.76, 56.76) * mm});
            skArc(sketch, "E3688", {"start": v(23.3, 56.76) * mm, "mid": v(23.37, 56.7) * mm, "end": v(23.43, 56.76) * mm});
            skArc(sketch, "E3689", {"start": v(23.43, 56.76) * mm, "mid": v(23.37, 56.82) * mm, "end": v(23.3, 56.76) * mm});
            skArc(sketch, "E3690", {"start": v(15.7, 62.38) * mm, "mid": v(15.76, 62.31) * mm, "end": v(15.82, 62.38) * mm});
            skArc(sketch, "E3691", {"start": v(15.82, 62.38) * mm, "mid": v(15.76, 62.44) * mm, "end": v(15.7, 62.38) * mm});
            skArc(sketch, "E3692", {"start": v(37.81, 74) * mm, "mid": v(37.87, 73.94) * mm, "end": v(37.94, 74) * mm});
            skArc(sketch, "E3693", {"start": v(37.94, 74) * mm, "mid": v(37.87, 74.07) * mm, "end": v(37.81, 74) * mm});
            skArc(sketch, "E3694", {"start": v(15.7, 64.92) * mm, "mid": v(15.76, 64.85) * mm, "end": v(15.82, 64.92) * mm});
            skArc(sketch, "E3695", {"start": v(15.82, 64.92) * mm, "mid": v(15.76, 64.98) * mm, "end": v(15.7, 64.92) * mm});
            skArc(sketch, "E3696", {"start": v(20.26, 56.76) * mm, "mid": v(20.32, 56.7) * mm, "end": v(20.38, 56.76) * mm});
            skArc(sketch, "E3697", {"start": v(20.38, 56.76) * mm, "mid": v(20.32, 56.82) * mm, "end": v(20.26, 56.76) * mm});
            skArc(sketch, "E3698", {"start": v(15.7, 67.46) * mm, "mid": v(15.76, 67.4) * mm, "end": v(15.83, 67.46) * mm});
            skArc(sketch, "E3699", {"start": v(15.83, 67.46) * mm, "mid": v(15.76, 67.52) * mm, "end": v(15.7, 67.46) * mm});
            skArc(sketch, "E3700", {"start": v(18.22, 56.76) * mm, "mid": v(18.29, 56.7) * mm, "end": v(18.35, 56.76) * mm});
            skArc(sketch, "E3701", {"start": v(18.35, 56.76) * mm, "mid": v(18.29, 56.82) * mm, "end": v(18.22, 56.76) * mm});
            skArc(sketch, "E3702", {"start": v(14.2, 65.42) * mm, "mid": v(14.26, 65.35) * mm, "end": v(14.33, 65.42) * mm});
            skArc(sketch, "E3703", {"start": v(14.33, 65.42) * mm, "mid": v(14.26, 65.48) * mm, "end": v(14.2, 65.42) * mm});
            skArc(sketch, "E3704", {"start": v(6.86, 35.55) * mm, "mid": v(7.24, 35.17) * mm, "end": v(7.62, 35.55) * mm});
            skArc(sketch, "E3705", {"start": v(7.62, 35.55) * mm, "mid": v(7.24, 35.93) * mm, "end": v(6.86, 35.55) * mm});
            skArc(sketch, "E3706", {"start": v(14.2, 69.48) * mm, "mid": v(14.26, 69.42) * mm, "end": v(14.33, 69.48) * mm});
            skArc(sketch, "E3707", {"start": v(14.33, 69.48) * mm, "mid": v(14.26, 69.54) * mm, "end": v(14.2, 69.48) * mm});
            skArc(sketch, "E3708", {"start": v(20.17, 21.13) * mm, "mid": v(20.55, 20.74) * mm, "end": v(20.93, 21.13) * mm});
            skArc(sketch, "E3709", {"start": v(20.93, 21.13) * mm, "mid": v(20.55, 21.5) * mm, "end": v(20.17, 21.13) * mm});
            skArc(sketch, "E3710", {"start": v(8.2, 20.5) * mm, "mid": v(8.32, 20.36) * mm, "end": v(8.45, 20.5) * mm});
            skArc(sketch, "E3711", {"start": v(8.45, 20.5) * mm, "mid": v(8.32, 20.62) * mm, "end": v(8.2, 20.5) * mm});
            skArc(sketch, "E3712", {"start": v(47.68, 50.39) * mm, "mid": v(47.8, 50.26) * mm, "end": v(47.93, 50.39) * mm});
            skArc(sketch, "E3713", {"start": v(47.93, 50.39) * mm, "mid": v(47.8, 50.51) * mm, "end": v(47.68, 50.39) * mm});
            skPoint(sketch, "E3714", {"position": v(26.85, 68.48) * mm});
            skSolve(sketch);
        }
        {
            var Q0;
            Q0=qCreatedBy(makeId("Top.planeOp"),FACE);
            var sketch = newSketch(context, id + "F4", { "sketchPlane" : qUnion([Q0])});
            skPoint(sketch, "E3715", {"position": v(6.07, 87.9) * mm});
            skPoint(sketch, "E3716", {"position": v(7.11, 68.2) * mm});
            skPoint(sketch, "E3717", {"position": v(7.24, 35.55) * mm});
            skPoint(sketch, "E3718", {"position": v(5.49, 13.86) * mm});
            skPoint(sketch, "E3719", {"position": v(46.66, 13.86) * mm});
            skPoint(sketch, "E3720", {"position": v(44.17, 35.37) * mm});
            skPoint(sketch, "E3721", {"position": v(44.22, 67.86) * mm});
            skPoint(sketch, "E3722", {"position": v(46.23, 87.93) * mm});
            skPoint(sketch, "E3723", {"position": v(26.8, 63.5) * mm});
            skCircle(sketch, "E3724", {"center": v(6.07, 87.9) * mm, "radius": 0.85 * mm});
            skCircle(sketch, "E3725", {"center": v(7.11, 68.2) * mm, "radius": 0.85 * mm});
            skCircle(sketch, "E3726", {"center": v(7.24, 35.55) * mm, "radius": 0.85 * mm});
            skCircle(sketch, "E3727", {"center": v(5.49, 13.86) * mm, "radius": 0.85 * mm});
            skCircle(sketch, "E3728", {"center": v(46.23, 87.93) * mm, "radius": 0.85 * mm});
            skCircle(sketch, "E3729", {"center": v(44.22, 67.86) * mm, "radius": 0.85 * mm});
            skCircle(sketch, "E3730", {"center": v(44.17, 35.37) * mm, "radius": 0.85 * mm});
            skCircle(sketch, "E3731", {"center": v(46.66, 13.86) * mm, "radius": 0.85 * mm});
            skCircle(sketch, "E3732", {"center": v(26.8, 63.5) * mm, "radius": 0.85 * mm});
            skSolve(sketch);
        }
        {
            var Q0;
            Q0=qCreatedBy(makeId("Top.planeOp"),FACE);
            var sketch = newSketch(context, id + "F5", { "sketchPlane" : qUnion([Q0])});
            skLineSegment(sketch, "E3733", {"start": v(3.17, 3.43) * mm, "end": v(48.9, 3.43) * mm});
            skLineSegment(sketch, "E3734", {"start": v(3.17, 98.17) * mm, "end": v(48.9, 98.17) * mm});
            skLineSegment(sketch, "E3735", {"start": v(26.8, 3.43) * mm, "end": v(26.8, 63.5) * mm});
            skLineSegment(sketch, "E3736", {"start": v(26.8, 63.5) * mm, "end": v(26.8, 98.17) * mm});
            skPoint(sketch, "E3736.endSnap0", {"position": v(26.03, 98.17) * mm});
            skLineSegment(sketch, "E3737", {"start": v(23.68, 98.17) * mm, "end": v(23.68, 3.43) * mm});
            skLineSegment(sketch, "E3738.MirrorCS", {"start": v(29.92, 98.17) * mm, "end": v(29.92, 3.43) * mm});
            skSolve(sketch);
        }
        {
            var Q0;
            Q0=qCreatedBy(makeId("Top.planeOp"),FACE);
            var sketch = newSketch(context, id + "F6", { "sketchPlane" : qUnion([Q0])});
            skLineSegment(sketch, "E3739", {"start": v(26.03, 98.43) * mm, "end": v(26.03, 90.65) * mm});
            skPoint(sketch, "E3740", {"position": v(26.03, 94.54) * mm});
            skLineSegment(sketch, "E3741", {"start": v(26.03, 94.54) * mm, "end": v(3.17, 94.54) * mm});
            skCircle(sketch, "E3742", {"center": v(15.87, 94.54) * mm, "radius": 1.13 * mm});
            skCircle(sketch, "E3743.MirrorC", {"center": v(36.2, 94.54) * mm, "radius": 1.13 * mm});
            skLineSegment(sketch, "E3744", {"start": v(26.04, 3.18) * mm, "end": v(26.04, 11.85) * mm});
            skPoint(sketch, "E3745", {"position": v(26.03, 7.51) * mm});
            skLineSegment(sketch, "E3746", {"start": v(26.03, 7.51) * mm, "end": v(3.17, 7.51) * mm});
            skCircle(sketch, "E3747", {"center": v(15.87, 7.51) * mm, "radius": 1.13 * mm});
            skCircle(sketch, "E3748.MirrorC", {"center": v(36.2, 7.51) * mm, "radius": 1.13 * mm});
            skSolve(sketch);
        }
        {
            var Q0;
            {var subQ1=sQuery(id+"F5.wireOp",EDGE,"E3735");Q0=makeQuery(id+"F5.imprint","IMPRINT",FACE,{"disambiguationData":[TD([[makeQuery(id+"F5.imprint","IMPRINT",EDGE,{"derivedFrom":subQ1}),-1.0]])]});}
            var Q1;
            {var subQ1=sQuery(id+"F5.wireOp",EDGE,"E3735");Q1=makeQuery(id+"F5.imprint","IMPRINT",FACE,{"disambiguationData":[TD([[makeQuery(id+"F5.imprint","IMPRINT",EDGE,{"derivedFrom":subQ1}),1.0]])]});}
            extrude(context, id + "F7", {"entities" : qUnion([Q0, Q1]), "operationType" : NewBodyOperationType.REMOVE, "oppositeDirection" : true, "depth" : 1.65 * mm});
        }
        {
            var Q0;
            Q0=makeQuery(id+"F6.imprint","IMPRINT",FACE,{"disambiguationData":[TD([[makeQuery(id+"F6.imprint","IMPRINT",EDGE,{"derivedFrom":sQuery(id+"F6.wireOp",EDGE,"E3743.MirrorC")}),-1.0]])]});
            var Q1;
            {var subQ0=sQuery(id+"F6.wireOp",EDGE,"E3742");var subQ1=sQuery(id+"F6.wireOp",EDGE,"E3741");var subQ2=makeQuery(id+"F6.imprint","INTERSECT",VERTEX,{"disambiguationData":[OD(0.0)],"derivedFrom":[subQ1,subQ0]});Q1=makeQuery(id+"F6.imprint","IMPRINT",FACE,{"disambiguationData":[TD([[makeQuery(id+"F6.imprint","IMPRINT",EDGE,{"disambiguationData":[TD([[subQ2,1.0]])],"derivedFrom":subQ1}),1.0]])]});}
            var Q2;
            {var subQ0=sQuery(id+"F6.wireOp",EDGE,"E3742");var subQ1=sQuery(id+"F6.wireOp",EDGE,"E3741");var subQ2=makeQuery(id+"F6.imprint","INTERSECT",VERTEX,{"disambiguationData":[OD(0.0)],"derivedFrom":[subQ1,subQ0]});Q2=makeQuery(id+"F6.imprint","IMPRINT",FACE,{"disambiguationData":[TD([[makeQuery(id+"F6.imprint","IMPRINT",EDGE,{"disambiguationData":[TD([[subQ2,1.0]])],"derivedFrom":subQ1}),-1.0]])]});}
            var Q3;
            Q3=makeQuery(id+"F6.imprint","IMPRINT",FACE,{"disambiguationData":[TD([[makeQuery(id+"F6.imprint","IMPRINT",EDGE,{"derivedFrom":sQuery(id+"F6.wireOp",EDGE,"E3748.MirrorC")}),-1.0]])]});
            var Q4;
            {var subQ0=sQuery(id+"F6.wireOp",EDGE,"E3747");var subQ1=sQuery(id+"F6.wireOp",EDGE,"E3746");var subQ2=makeQuery(id+"F6.imprint","INTERSECT",VERTEX,{"disambiguationData":[OD(0.0)],"derivedFrom":[subQ1,subQ0]});Q4=makeQuery(id+"F6.imprint","IMPRINT",FACE,{"disambiguationData":[TD([[makeQuery(id+"F6.imprint","IMPRINT",EDGE,{"disambiguationData":[TD([[subQ2,1.0]])],"derivedFrom":subQ1}),-1.0]])]});}
            var Q5;
            {var subQ0=sQuery(id+"F6.wireOp",EDGE,"E3747");var subQ1=sQuery(id+"F6.wireOp",EDGE,"E3746");var subQ2=makeQuery(id+"F6.imprint","INTERSECT",VERTEX,{"disambiguationData":[OD(0.0)],"derivedFrom":[subQ1,subQ0]});Q5=makeQuery(id+"F6.imprint","IMPRINT",FACE,{"disambiguationData":[TD([[makeQuery(id+"F6.imprint","IMPRINT",EDGE,{"disambiguationData":[TD([[subQ2,1.0]])],"derivedFrom":subQ1}),1.0]])]});}
            var Q6;
            Q6=makeQuery(id+"F4.imprint","IMPRINT",FACE,{"disambiguationData":[TD([[makeQuery(id+"F4.imprint","IMPRINT",EDGE,{"derivedFrom":sQuery(id+"F4.wireOp",EDGE,"E3724")}),1.0]])]});
            var Q7;
            Q7=makeQuery(id+"F4.imprint","IMPRINT",FACE,{"disambiguationData":[TD([[makeQuery(id+"F4.imprint","IMPRINT",EDGE,{"derivedFrom":sQuery(id+"F4.wireOp",EDGE,"E3725")}),1.0]])]});
            var Q8;
            Q8=makeQuery(id+"F4.imprint","IMPRINT",FACE,{"disambiguationData":[TD([[makeQuery(id+"F4.imprint","IMPRINT",EDGE,{"derivedFrom":sQuery(id+"F4.wireOp",EDGE,"E3726")}),1.0]])]});
            var Q9;
            Q9=makeQuery(id+"F4.imprint","IMPRINT",FACE,{"disambiguationData":[TD([[makeQuery(id+"F4.imprint","IMPRINT",EDGE,{"derivedFrom":sQuery(id+"F4.wireOp",EDGE,"E3731")}),1.0]])]});
            var Q10;
            Q10=makeQuery(id+"F4.imprint","IMPRINT",FACE,{"disambiguationData":[TD([[makeQuery(id+"F4.imprint","IMPRINT",EDGE,{"derivedFrom":sQuery(id+"F4.wireOp",EDGE,"E3727")}),1.0]])]});
            var Q11;
            Q11=makeQuery(id+"F4.imprint","IMPRINT",FACE,{"disambiguationData":[TD([[makeQuery(id+"F4.imprint","IMPRINT",EDGE,{"derivedFrom":sQuery(id+"F4.wireOp",EDGE,"E3730")}),1.0]])]});
            var Q12;
            Q12=makeQuery(id+"F4.imprint","IMPRINT",FACE,{"disambiguationData":[TD([[makeQuery(id+"F4.imprint","IMPRINT",EDGE,{"derivedFrom":sQuery(id+"F4.wireOp",EDGE,"E3729")}),1.0]])]});
            var Q13;
            Q13=makeQuery(id+"F4.imprint","IMPRINT",FACE,{"disambiguationData":[TD([[makeQuery(id+"F4.imprint","IMPRINT",EDGE,{"derivedFrom":sQuery(id+"F4.wireOp",EDGE,"E3728")}),1.0]])]});
            extrude(context, id + "F8", {"entities" : qUnion([Q0, Q1, Q2, Q3, Q4, Q5, Q6, Q7, Q8, Q9, Q10, Q11, Q12, Q13]), "operationType" : NewBodyOperationType.REMOVE, "endBound" : BoundingType.UP_TO_NEXT, "oppositeDirection" : true, "depth" : 25.4 * mm});
        }
        {
            var Q0;
            Q0=makeQuery(id+"F1.opExtrude","SWEPT_FACE",FACE,{"disambiguationData":[OSD([sQuery(id+"F0.wireOp",EDGE,"E1.bottom")])]});
            var sketch = newSketch(context, id + "F9", { "sketchPlane" : qUnion([Q0])});
            skCircle(sketch, "E3749", {"center": v(10.61, -3.18) * mm, "radius": 1.13 * mm});
            skLineSegment(sketch, "E3750", {"start": v(26.03, -6.35) * mm, "end": v(26.03, 0) * mm});
            skCircle(sketch, "E3751.MirrorC", {"center": v(41.46, -3.18) * mm, "radius": 1.13 * mm});
            skSolve(sketch);
        }
        {
            var Q0;
            Q0=makeQuery(id+"F1.opExtrude","SWEPT_FACE",FACE,{"disambiguationData":[OSD([sQuery(id+"F0.wireOp",EDGE,"E1.top")])]});
            var sketch = newSketch(context, id + "F10", { "sketchPlane" : qUnion([Q0])});
            skCircle(sketch, "E3752", {"center": v(-41.46, -3.18) * mm, "radius": 1.13 * mm});
            skLineSegment(sketch, "E3753", {"start": v(-26.03, -6.35) * mm, "end": v(-26.03, 0) * mm});
            skCircle(sketch, "E3754.MirrorC", {"center": v(-10.61, -3.18) * mm, "radius": 1.13 * mm});
            skSolve(sketch);
        }
        {
            var Q0;
            Q0=makeQuery(id+"F10.imprint","IMPRINT",FACE,{"disambiguationData":[TD([[makeQuery(id+"F10.imprint","IMPRINT",EDGE,{"derivedFrom":sQuery(id+"F10.wireOp",EDGE,"E3752")}),1.0]])]});
            var Q1;
            Q1=makeQuery(id+"F10.imprint","IMPRINT",FACE,{"disambiguationData":[TD([[makeQuery(id+"F10.imprint","IMPRINT",EDGE,{"derivedFrom":sQuery(id+"F10.wireOp",EDGE,"E3754.MirrorC")}),-1.0]])]});
            extrude(context, id + "F11", {"entities" : qUnion([Q0, Q1]), "operationType" : NewBodyOperationType.REMOVE, "oppositeDirection" : true, "depth" : 6.35 * mm});
        }
        {
            var Q0;
            Q0=makeQuery(id+"F9.imprint","IMPRINT",FACE,{"disambiguationData":[TD([[makeQuery(id+"F9.imprint","IMPRINT",EDGE,{"derivedFrom":sQuery(id+"F9.wireOp",EDGE,"E3749")}),1.0]])]});
            var Q1;
            Q1=makeQuery(id+"F9.imprint","IMPRINT",FACE,{"disambiguationData":[TD([[makeQuery(id+"F9.imprint","IMPRINT",EDGE,{"derivedFrom":sQuery(id+"F9.wireOp",EDGE,"E3751.MirrorC")}),-1.0]])]});
            extrude(context, id + "F12", {"entities" : qUnion([Q0, Q1]), "operationType" : NewBodyOperationType.REMOVE, "oppositeDirection" : true, "depth" : 6.35 * mm});
        }
        {
            var Q0;
            Q0=makeQuery(id+"F7.boolean.opBoolean","COPY",FACE,{"derivedFrom":makeQuery(id+"F7.opExtrude","CAP_FACE",FACE,{"disambiguationData":[OSD([sQuery(id+"F5.wireOp",EDGE,"E3733"),sQuery(id+"F5.wireOp",EDGE,"E3734"),sQuery(id+"F5.wireOp",EDGE,"E3737"),sQuery(id+"F5.wireOp",EDGE,"E3738.MirrorCS")])],"isStart":false})});
            var sketch = newSketch(context, id + "F13", { "sketchPlane" : qUnion([Q0])});
            skPoint(sketch, "E3755", {"position": v(26.8, 63.5) * mm});
            skLineSegment(sketch, "E3756", {"start": v(26.8, 63.5) * mm, "end": v(26.8, 98.17) * mm});
            skLineSegment(sketch, "E3757", {"start": v(26.8, 63.5) * mm, "end": v(26.8, 3.43) * mm});
            skCircle(sketch, "E3758", {"center": v(26.8, 39.8) * mm, "radius": 0.85 * mm});
            skCircle(sketch, "E3759", {"center": v(26.8, 34.2) * mm, "radius": 0.85 * mm});
            skCircle(sketch, "E3760", {"center": v(26.8, 10.5) * mm, "radius": 0.85 * mm});
            skCircle(sketch, "E3761", {"center": v(26.8, 69.1) * mm, "radius": 0.85 * mm});
            skCircle(sketch, "E3762", {"center": v(26.8, 92.8) * mm, "radius": 0.85 * mm});
            skCircle(sketch, "E3763", {"center": v(26.8, 63.5) * mm, "radius": 0.85 * mm});
            skSolve(sketch);
        }
        {
            var Q0;
            {var subQ0=sQuery(id+"F13.wireOp",EDGE,"E3762");var subQ1=sQuery(id+"F13.wireOp",EDGE,"E3756");var subQ2=makeQuery(id+"F13.imprint","INTERSECT",VERTEX,{"disambiguationData":[OD(0.0)],"derivedFrom":[subQ1,subQ0]});Q0=makeQuery(id+"F13.imprint","IMPRINT",FACE,{"disambiguationData":[TD([[makeQuery(id+"F13.imprint","IMPRINT",EDGE,{"disambiguationData":[TD([[subQ2,-1.0]])],"derivedFrom":subQ1}),1.0]])]});}
            var Q1;
            {var subQ0=sQuery(id+"F13.wireOp",EDGE,"E3762");var subQ1=sQuery(id+"F13.wireOp",EDGE,"E3756");var subQ2=makeQuery(id+"F13.imprint","INTERSECT",VERTEX,{"disambiguationData":[OD(0.0)],"derivedFrom":[subQ1,subQ0]});Q1=makeQuery(id+"F13.imprint","IMPRINT",FACE,{"disambiguationData":[TD([[makeQuery(id+"F13.imprint","IMPRINT",EDGE,{"disambiguationData":[TD([[subQ2,-1.0]])],"derivedFrom":subQ1}),-1.0]])]});}
            var Q2;
            {var subQ0=sQuery(id+"F13.wireOp",EDGE,"E3761");var subQ1=sQuery(id+"F13.wireOp",EDGE,"E3756");var subQ2=makeQuery(id+"F13.imprint","INTERSECT",VERTEX,{"disambiguationData":[OD(0.0)],"derivedFrom":[subQ1,subQ0]});Q2=makeQuery(id+"F13.imprint","IMPRINT",FACE,{"disambiguationData":[TD([[makeQuery(id+"F13.imprint","IMPRINT",EDGE,{"disambiguationData":[TD([[subQ2,-1.0]])],"derivedFrom":subQ1}),1.0]])]});}
            var Q3;
            {var subQ0=sQuery(id+"F13.wireOp",EDGE,"E3761");var subQ1=sQuery(id+"F13.wireOp",EDGE,"E3756");var subQ2=makeQuery(id+"F13.imprint","INTERSECT",VERTEX,{"disambiguationData":[OD(0.0)],"derivedFrom":[subQ1,subQ0]});Q3=makeQuery(id+"F13.imprint","IMPRINT",FACE,{"disambiguationData":[TD([[makeQuery(id+"F13.imprint","IMPRINT",EDGE,{"disambiguationData":[TD([[subQ2,-1.0]])],"derivedFrom":subQ1}),-1.0]])]});}
            var Q4;
            {var subQ0=sQuery(id+"F13.wireOp",EDGE,"E3758");var subQ1=sQuery(id+"F13.wireOp",EDGE,"E3757");var subQ2=makeQuery(id+"F13.imprint","INTERSECT",VERTEX,{"disambiguationData":[OD(0.0)],"derivedFrom":[subQ1,subQ0]});Q4=makeQuery(id+"F13.imprint","IMPRINT",FACE,{"disambiguationData":[TD([[makeQuery(id+"F13.imprint","IMPRINT",EDGE,{"disambiguationData":[TD([[subQ2,-1.0]])],"derivedFrom":subQ1}),-1.0]])]});}
            var Q5;
            {var subQ0=sQuery(id+"F13.wireOp",EDGE,"E3758");var subQ1=sQuery(id+"F13.wireOp",EDGE,"E3757");var subQ2=makeQuery(id+"F13.imprint","INTERSECT",VERTEX,{"disambiguationData":[OD(0.0)],"derivedFrom":[subQ1,subQ0]});Q5=makeQuery(id+"F13.imprint","IMPRINT",FACE,{"disambiguationData":[TD([[makeQuery(id+"F13.imprint","IMPRINT",EDGE,{"disambiguationData":[TD([[subQ2,-1.0]])],"derivedFrom":subQ1}),1.0]])]});}
            var Q6;
            {var subQ0=sQuery(id+"F13.wireOp",EDGE,"E3759");var subQ1=sQuery(id+"F13.wireOp",EDGE,"E3757");var subQ2=makeQuery(id+"F13.imprint","INTERSECT",VERTEX,{"disambiguationData":[OD(0.0)],"derivedFrom":[subQ1,subQ0]});Q6=makeQuery(id+"F13.imprint","IMPRINT",FACE,{"disambiguationData":[TD([[makeQuery(id+"F13.imprint","IMPRINT",EDGE,{"disambiguationData":[TD([[subQ2,-1.0]])],"derivedFrom":subQ1}),-1.0]])]});}
            var Q7;
            {var subQ0=sQuery(id+"F13.wireOp",EDGE,"E3759");var subQ1=sQuery(id+"F13.wireOp",EDGE,"E3757");var subQ2=makeQuery(id+"F13.imprint","INTERSECT",VERTEX,{"disambiguationData":[OD(0.0)],"derivedFrom":[subQ1,subQ0]});Q7=makeQuery(id+"F13.imprint","IMPRINT",FACE,{"disambiguationData":[TD([[makeQuery(id+"F13.imprint","IMPRINT",EDGE,{"disambiguationData":[TD([[subQ2,-1.0]])],"derivedFrom":subQ1}),1.0]])]});}
            var Q8;
            {var subQ0=sQuery(id+"F13.wireOp",EDGE,"E3760");var subQ1=sQuery(id+"F13.wireOp",EDGE,"E3757");var subQ2=makeQuery(id+"F13.imprint","INTERSECT",VERTEX,{"disambiguationData":[OD(0.0)],"derivedFrom":[subQ1,subQ0]});Q8=makeQuery(id+"F13.imprint","IMPRINT",FACE,{"disambiguationData":[TD([[makeQuery(id+"F13.imprint","IMPRINT",EDGE,{"disambiguationData":[TD([[subQ2,-1.0]])],"derivedFrom":subQ1}),-1.0]])]});}
            var Q9;
            {var subQ0=sQuery(id+"F13.wireOp",EDGE,"E3760");var subQ1=sQuery(id+"F13.wireOp",EDGE,"E3757");var subQ2=makeQuery(id+"F13.imprint","INTERSECT",VERTEX,{"disambiguationData":[OD(0.0)],"derivedFrom":[subQ1,subQ0]});Q9=makeQuery(id+"F13.imprint","IMPRINT",FACE,{"disambiguationData":[TD([[makeQuery(id+"F13.imprint","IMPRINT",EDGE,{"disambiguationData":[TD([[subQ2,-1.0]])],"derivedFrom":subQ1}),1.0]])]});}
            var Q10;
            {var subQ0=sQuery(id+"F13.wireOp",EDGE,"E3757");var subQ1=sQuery(id+"F13.wireOp",EDGE,"E3756");var subQ2=makeQuery(id+"F13.imprint","INTERSECT",VERTEX,{"derivedFrom":[subQ1,subQ0]});Q10=makeQuery(id+"F13.imprint","IMPRINT",FACE,{"disambiguationData":[TD([[makeQuery(id+"F13.imprint","IMPRINT",EDGE,{"disambiguationData":[TD([[subQ2,-1.0]])],"derivedFrom":subQ1}),-1.0]])]});}
            var Q11;
            {var subQ0=sQuery(id+"F13.wireOp",EDGE,"E3757");var subQ1=sQuery(id+"F13.wireOp",EDGE,"E3756");var subQ2=makeQuery(id+"F13.imprint","INTERSECT",VERTEX,{"derivedFrom":[subQ1,subQ0]});Q11=makeQuery(id+"F13.imprint","IMPRINT",FACE,{"disambiguationData":[TD([[makeQuery(id+"F13.imprint","IMPRINT",EDGE,{"disambiguationData":[TD([[subQ2,-1.0]])],"derivedFrom":subQ1}),1.0]])]});}
            extrude(context, id + "F14", {"entities" : qUnion([Q0, Q1, Q2, Q3, Q4, Q5, Q6, Q7, Q8, Q9, Q10, Q11]), "operationType" : NewBodyOperationType.REMOVE, "endBound" : BoundingType.UP_TO_NEXT, "oppositeDirection" : true, "depth" : 25.4 * mm});
        }
    });
